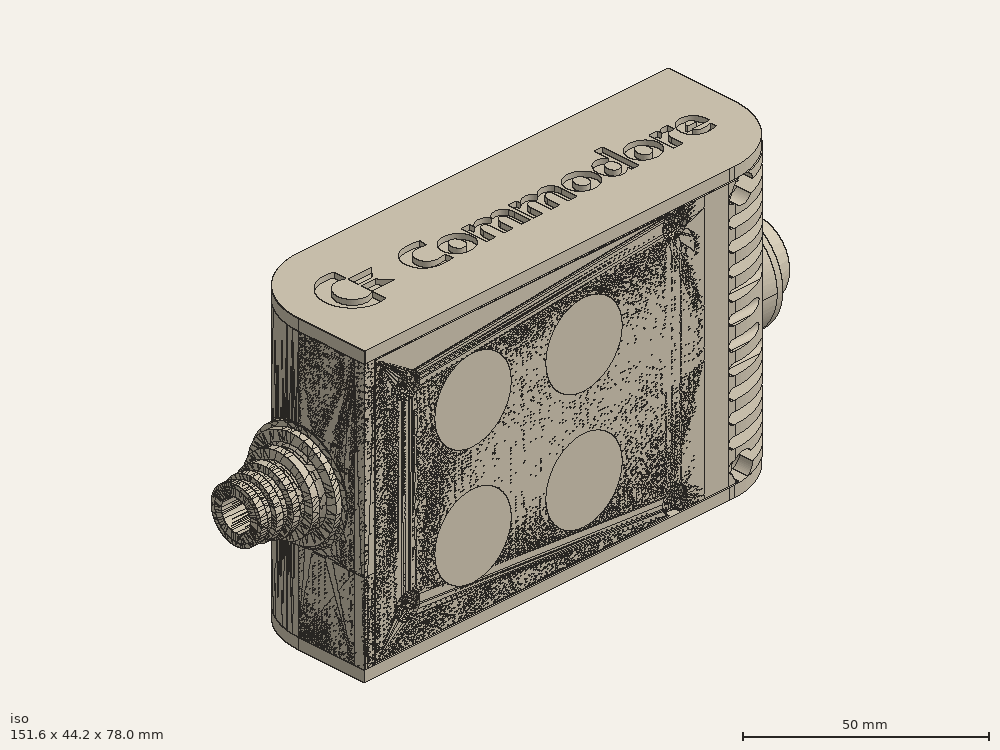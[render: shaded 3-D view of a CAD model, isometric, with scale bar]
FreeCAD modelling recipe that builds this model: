
FCSTD DOCUMENT  (FreeCAD 0.19R0.19.2)
Label: enclosure_223FCStd
License: All rights reserved
LicenseURL: http://en.wikipedia.org/wiki/All_rights_reserved
objects: Part::Revolution×152, Part::MultiFuse×148, Part::Feature×146, Sketcher::SketchObject×93, Part::Extrusion×78, Part::Cut×74, Part::Cylinder×70, Part::Fillet×58, Part::Box×38, App::MeasureDistance×4, Part::Chamfer×4, Part::FeaturePython×2, Image::ImagePlane×1, PartDesign::Body×1, Part::Mirroring×1
note: 865 computed .brp shape members not serialized (recipe doc carries the construction recipe); baked Part::Feature solids carry a one-line shape summary decoded from their .brp

FEATURE [Sketcher::SketchObject] Sketch  label="topSketch"
  FullyConstrained = true
  sketch-geometry (20):
    g0: LineSegment StartX=5.21097e-06 StartY=3 StartZ=0 EndX=5.21097e-06 EndY=19 EndZ=0
    g1: ArcOfCircle CenterX=19 CenterY=19 CenterZ=0 NormalX=0 NormalY=0 NormalZ=1 AngleXU=0 Radius=19 StartAngle=1.5708 EndAngle=3.14159
    g2: ArcOfCircle CenterX=19 CenterY=19 CenterZ=0 NormalX=0 NormalY=0 NormalZ=1 AngleXU=0 Radius=16 StartAngle=1.5708 EndAngle=3.14159
    g3: LineSegment StartX=114 StartY=35 StartZ=0 EndX=19 EndY=35 EndZ=0
    g4: LineSegment StartX=5.21097e-06 StartY=3 StartZ=0 EndX=5.21097e-06 EndY=0 EndZ=0
    g5: LineSegment StartX=3 StartY=0 StartZ=0 EndX=5.21097e-06 EndY=0 EndZ=0
    g6: LineSegment StartX=3 StartY=19 StartZ=0 EndX=3 EndY=0 EndZ=0
    g7: LineSegment StartX=19 StartY=38 StartZ=0 EndX=124 EndY=38 EndZ=0
    g8: Circle CenterX=119 CenterY=35 CenterZ=0 NormalX=0 NormalY=0 NormalZ=1 AngleXU=0 Radius=1
    g9: Circle CenterX=121 CenterY=35 CenterZ=0 NormalX=0 NormalY=0 NormalZ=1 AngleXU=0 Radius=1
    g10: Circle CenterX=121 CenterY=33 CenterZ=0 NormalX=0 NormalY=0 NormalZ=1 AngleXU=0 Radius=1
    g11: BSplineCurve PolesCount=3 KnotsCount=2 Degree=2 IsPeriodic=0
    g12: GeomPoint X=119 Y=35 Z=0
    g13: GeomPoint X=121 Y=33 Z=0
    g14: LineSegment StartX=119 StartY=35 StartZ=0 EndX=114 EndY=35 EndZ=0
    g15: ArcOfCircle CenterX=105 CenterY=19 CenterZ=0 NormalX=0 NormalY=0 NormalZ=1 AngleXU=0 Radius=19 StartAngle=5.7297 EndAngle=6.28319
    g16: ArcOfCircle CenterX=105 CenterY=19 CenterZ=0 NormalX=0 NormalY=0 NormalZ=1 AngleXU=0 Radius=16 StartAngle=5.60905 EndAngle=6.28319
    g17: LineSegment StartX=121 StartY=33 StartZ=0 EndX=121 EndY=19 EndZ=0
    g18: LineSegment StartX=124 StartY=38 StartZ=0 EndX=124 EndY=19 EndZ=0
    g19: LineSegment StartX=117.5 StartY=9.01251 StartZ=0 EndX=121.163 EndY=9.0125 EndZ=0
  constraints (46):
    c: Vertical(g0)
    c: Block(g0)
    c: Coincident(g1,g0)
    c: Block(g1)
    c: Coincident(g2,g1)
    c: Block(g2)
    c: Coincident(g3,g2)
    c: Horizontal(g3)
    c: Tangent(g3,g2)
    c: Coincident(g4,g0)
    c: Distance(g4) = 3
    c: Vertical(g4)
    c: Coincident(g5,g4)
    c: Horizontal(g5)
    c: Coincident(g6,g2)
    c: Coincident(g6,g5)
    c: Vertical(g6)
    c: Horizontal(g7)
    c: Distance(g7) = 105
    c: Coincident(g7,g1)
    c: Block(g3)
    c: Weight(g8) = 1
    c: Equal(g8,g9)
    c: Equal(g8,g10)
    c: InternalAlignment(g8,g11)
    c: InternalAlignment(g9,g11)
    c: InternalAlignment(g10,g11)
    c: InternalAlignment(g12,g11)
    c: InternalAlignment(g13,g11)
    c: Block(g11)
    c: Coincident(g14,g11)
    c: Coincident(g14,g3)
    c: Horizontal(g14)
    c: Block(g15)
    c: Coincident(g16,g15)
    c: Block(g16)
    c: Coincident(g17,g11)
    c: Coincident(g17,g16)
    c: Vertical(g17)
    c: Distance(g17) = 14
    c: Coincident(g18,g7)
    c: Coincident(g18,g15)
    c: Vertical(g18)
    c: Distance(g18) = 19
    c: Coincident(g19,g16)
    c: Coincident(g19,g15)
FEATURE [Sketcher::SketchObject] Sketch001  label="bottomSketch"
  FullyConstrained = true
  sketch-geometry (32):
    g0: LineSegment StartX=3.3 StartY=-6.03275e-07 StartZ=0 EndX=98 EndY=-6.03275e-07 EndZ=0
    g1: ArcOfCircle CenterX=98 CenterY=19 CenterZ=0 NormalX=0 NormalY=0 NormalZ=1 AngleXU=0 Radius=19 StartAngle=4.71239 EndAngle=5.71103
    g2: LineSegment StartX=6.3 StartY=8 StartZ=0 EndX=3.3 EndY=8 EndZ=0
    g3: LineSegment StartX=3.3 StartY=8 StartZ=0 EndX=3.3 EndY=-6.03275e-07 EndZ=0
    g4: ArcOfCircle CenterX=8.3 CenterY=5 CenterZ=0 NormalX=0 NormalY=0 NormalZ=1 AngleXU=0 Radius=2 StartAngle=3.14159 EndAngle=4.71239
    g5: LineSegment StartX=6.3 StartY=8 StartZ=0 EndX=6.3 EndY=5 EndZ=0
    g6: ArcOfCircle CenterX=98 CenterY=19 CenterZ=0 NormalX=0 NormalY=0 NormalZ=1 AngleXU=0 Radius=12.7 StartAngle=4.71239 EndAngle=6.28319
    g7: LineSegment StartX=94.7 StartY=3 StartZ=0 EndX=8.3 EndY=3 EndZ=0
    g8-g12: Circle x5 (B-spline internal-alignment scaffolding for g13; pole/knot coordinates omitted)
    g13: BSplineCurve PolesCount=5 KnotsCount=3 Degree=3 IsPeriodic=0
    g14: GeomPoint X=98 Y=6.3 Z=0
    g15: GeomPoint X=96.3938 Y=4.71946 Z=0
    g16: GeomPoint X=94.7 Y=3 Z=0
    g17-g23: Circle x7 (B-spline internal-alignment scaffolding for g24; pole/knot coordinates omitted)
    g24: BSplineCurve PolesCount=7 KnotsCount=5 Degree=3 IsPeriodic=0
    g25-g29: GeomPoint x5 (B-spline internal-alignment scaffolding for g24; pole/knot coordinates omitted)
    g30: ArcOfCircle CenterX=98 CenterY=19 CenterZ=0 NormalX=0 NormalY=0 NormalZ=1 AngleXU=0 Radius=15.7 StartAngle=5.81226 EndAngle=6.28319
    g31: LineSegment StartX=110.7 StartY=19 StartZ=0 EndX=113.7 EndY=19 EndZ=0
  constraints (41):
    c: Horizontal(g0)
    c: Coincident(g1,g0)
    c: Block(g1)
    c: Horizontal(g2)
    c: Distance(g2) = 3
    c: Coincident(g3,g2)
    c: Vertical(g3)
    c: Coincident(g3,g0)
    c: Block(g4)
    c: Block(g2)
    c: Coincident(g5,g2)
    c: Coincident(g5,g4)
    c: Vertical(g5)
    c: Coincident(g6,g1)
    c: Block(g6)
    c: Coincident(g7,g4)
    c: Horizontal(g7)
    c: Block(g0)
    c: Block(g7)
    c: Block(g3)
    c: Coincident(g13,g6)
    c: Weight(g8) = 1
    c: Equal(g8, g9-g12) x4
    c: Coincident(g13,g7)
    c: InternalAlignment(g8-g12 -> g13) x5
    c: InternalAlignment(g14,g13)
    c: InternalAlignment(g15,g13)
    c: InternalAlignment(g16,g13)
    c: Block(g13)
    c: Weight(g17) = 1
    c: Equal(g17, g18-g23) x6
    c: Coincident(g24,g1)
    c: InternalAlignment(g17-g23 -> g24) x7
    c: InternalAlignment(g25-g29 -> g24) x5
    c: Block(g24)
    c: Coincident(g30,g24)
    c: Coincident(g31,g6)
    c: Coincident(g31,g30)
    c: Horizontal(g31)
    c: Block(g31)
    c: Block(g30)
FEATURE [Part::Extrusion] Extrude  label="top"
  Base = -> Sketch
  Dir = (0,0,1)
  DirMode = 2
  FaceMakerClass = Part::FaceMakerBullseye
  LengthFwd = 72
  LengthRev = 0
  Solid = true
  Symmetric = false
FEATURE [Part::Extrusion] Extrude001  label="bottom"
  Base = -> Sketch001
  Dir = (0,0,1)
  DirMode = 2
  FaceMakerClass = Part::FaceMakerBullseye
  LengthFwd = 71.4
  LengthRev = 0
  Placement = pos=(0,0,0.3) rot=(0,0,1;0rad)
  Solid = true
  Symmetric = false
FEATURE [Sketcher::SketchObject] Sketch002  label="topSketch001"
  FullyConstrained = true
  sketch-geometry (8):
    g0: ArcOfCircle CenterX=19 CenterY=19.0975 CenterZ=0 NormalX=0 NormalY=0 NormalZ=1 AngleXU=0 Radius=18.9025 StartAngle=1.5708 EndAngle=3.14674
    g1: LineSegment StartX=0.0977805 StartY=19.0003 StartZ=0 EndX=0.0977805 EndY=0.000251602 EndZ=0
    g2: LineSegment StartX=19 StartY=38 StartZ=0 EndX=124 EndY=38 EndZ=0
    g3: LineSegment StartX=0.0977805 StartY=0.000251602 StartZ=0 EndX=105.098 EndY=0.000251602 EndZ=0
    g4: LineSegment StartX=124 StartY=38 StartZ=0 EndX=125.616 EndY=38 EndZ=0
    g5: LineSegment StartX=105.098 StartY=0.000251602 StartZ=0 EndX=106.713 EndY=0.000251602 EndZ=0
    g6: ArcOfCircle CenterX=106.616 CenterY=19 CenterZ=0 NormalX=0 NormalY=0 NormalZ=1 AngleXU=0 Radius=19 StartAngle=4.71754 EndAngle=6.28319
    g7: LineSegment StartX=125.616 StartY=38 StartZ=0 EndX=125.616 EndY=19 EndZ=0
  constraints (21):
    c: Block(g0)
    c: Coincident(g1,g0)
    c: Vertical(g1)
    c: Horizontal(g2)
    c: Distance(g2) = 105
    c: Coincident(g2,g0)
    c: Distance(g1) = 19
    c: Coincident(g3,g1)
    c: Horizontal(g3)
    c: Distance(g3) = 105
    c: Coincident(g4,g2)
    c: Horizontal(g4)
    c: Distance(g4) = 1.61553
    c: Horizontal(g5)
    c: Equal(g4,g5) = 1.61553
    c: Coincident(g5,g3)
    c: Block(g6)
    c: Coincident(g6,g5)
    c: Coincident(g7,g4)
    c: Coincident(g7,g6)
    c: Vertical(g7)
FEATURE [Part::Extrusion] Extrude002  label="sideA"
  Base = -> Sketch002
  Dir = (0,0,1)
  DirMode = 2
  FaceMakerClass = Part::FaceMakerBullseye
  LengthFwd = 3
  LengthRev = 0
  Placement = pos=(0,0,-3) rot=(0,0,1;0rad)
  Solid = true
  Symmetric = false
FEATURE [Sketcher::SketchObject] Sketch003  label="topSketch002"
  FullyConstrained = true
  sketch-geometry (6):
    g0: LineSegment StartX=19 StartY=38 StartZ=0 EndX=117 EndY=38 EndZ=0
    g1: ArcOfCircle CenterX=19 CenterY=19 CenterZ=0 NormalX=0 NormalY=0 NormalZ=1 AngleXU=0 Radius=19 StartAngle=1.5708 EndAngle=3.14159
    g2: LineSegment StartX=117 StartY=38 StartZ=0 EndX=117 EndY=19 EndZ=0
    g3: LineSegment StartX=98 StartY=1.0161e-12 StartZ=0 EndX=5.22862e-06 EndY=1.0161e-12 EndZ=0
    g4: LineSegment StartX=5.22862e-06 StartY=19 StartZ=0 EndX=5.22862e-06 EndY=1.0161e-12 EndZ=0
    g5: ArcOfCircle CenterX=98 CenterY=19 CenterZ=0 NormalX=0 NormalY=0 NormalZ=1 AngleXU=0 Radius=19 StartAngle=4.71239 EndAngle=6.28319
  constraints (16):
    c: Horizontal(g0)
    c: Distance(g0) = 98
    c: Coincident(g1,g0)
    c: Block(g1)
    c: Coincident(g2,g0)
    c: Vertical(g2)
    c: Distance(g2) = 19
    c: Horizontal(g3)
    c: Coincident(g4,g1)
    c: Vertical(g4)
    c: Coincident(g3,g4)
    c: Block(g3)
    c: Coincident(g5,g2)
    c: Coincident(g5,g3)
    c: Block(g0)
    c: Block(g5)
FEATURE [Sketcher::SketchObject] Sketch004
  FullyConstrained = true
  MapMode = 3
  Placement = pos=(0,0,0) rot=(1,0,0;1.5708rad)
  Support = -> [Extrude]
  sketch-geometry (8):
    g0: Circle CenterX=80.351 CenterY=-67.6202 CenterZ=0 NormalX=0 NormalY=0 NormalZ=1 AngleXU=0 Radius=2
    g1: Circle CenterX=80.351 CenterY=-67.6202 CenterZ=0 NormalX=0 NormalY=0 NormalZ=1 AngleXU=0 Radius=3
    g2: Circle CenterX=80.351 CenterY=-4.92017 CenterZ=0 NormalX=0 NormalY=0 NormalZ=1 AngleXU=0 Radius=2
    g3: Circle CenterX=80.351 CenterY=-4.92017 CenterZ=0 NormalX=0 NormalY=0 NormalZ=1 AngleXU=0 Radius=3
    g4: Circle CenterX=23.851 CenterY=-4.92017 CenterZ=0 NormalX=0 NormalY=0 NormalZ=1 AngleXU=0 Radius=2
    g5: Circle CenterX=23.851 CenterY=-4.92017 CenterZ=0 NormalX=0 NormalY=0 NormalZ=1 AngleXU=0 Radius=3
    g6: Circle CenterX=23.851 CenterY=-67.6202 CenterZ=0 NormalX=0 NormalY=0 NormalZ=1 AngleXU=0 Radius=2
    g7: Circle CenterX=23.851 CenterY=-67.6202 CenterZ=0 NormalX=0 NormalY=0 NormalZ=1 AngleXU=0 Radius=3
  constraints (8):
    c: Block(g3)
    c: Block(g2)
    c: Block(g1)
    c: Block(g0)
    c: Block(g6)
    c: Block(g7)
    c: Block(g4)
    c: Block(g5)
FEATURE [Part::Extrusion] Extrude004
  Base = -> Sketch004
  Dir = (0,-1,2e-16)
  DirMode = 2
  FaceMakerClass = Part::FaceMakerBullseye
  LengthFwd = 6
  LengthRev = 0
  Placement = pos=(0,9,0) rot=(0,0,1;0rad)
  Solid = true
  Symmetric = false
FEATURE [Sketcher::SketchObject] Sketch005
  FullyConstrained = true
  MapMode = 3
  Placement = pos=(0,0,0) rot=(1,0,0;1.5708rad)
  Support = -> [Extrude]
  sketch-geometry (8):
    g0: Circle CenterX=80.351 CenterY=-67.6202 CenterZ=0 NormalX=0 NormalY=0 NormalZ=1 AngleXU=0 Radius=3
    g1: Circle CenterX=80.351 CenterY=-4.92017 CenterZ=0 NormalX=0 NormalY=0 NormalZ=1 AngleXU=0 Radius=3
    g2: Circle CenterX=23.851 CenterY=-4.92017 CenterZ=0 NormalX=0 NormalY=0 NormalZ=1 AngleXU=0 Radius=3
    g3: Circle CenterX=23.851 CenterY=-67.6202 CenterZ=0 NormalX=0 NormalY=0 NormalZ=1 AngleXU=0 Radius=3
    g4: Circle CenterX=23.851 CenterY=-67.6202 CenterZ=0 NormalX=0 NormalY=0 NormalZ=1 AngleXU=0 Radius=5
    g5: Circle CenterX=80.351 CenterY=-67.6202 CenterZ=0 NormalX=0 NormalY=0 NormalZ=1 AngleXU=0 Radius=5
    g6: Circle CenterX=23.851 CenterY=-4.92017 CenterZ=0 NormalX=0 NormalY=0 NormalZ=1 AngleXU=0 Radius=5
    g7: Circle CenterX=80.351 CenterY=-4.92017 CenterZ=0 NormalX=0 NormalY=0 NormalZ=1 AngleXU=0 Radius=5
  constraints (8):
    c: Block(g1)
    c: Block(g0)
    c: Block(g3)
    c: Block(g2)
    c: Block(g5)
    c: Block(g4)
    c: Block(g6)
    c: Block(g7)
FEATURE [Part::Extrusion] Extrude005
  Base = -> Sketch005
  Dir = (0,-1,2e-16)
  DirMode = 2
  FaceMakerClass = Part::FaceMakerBullseye
  LengthFwd = 2
  LengthRev = 0
  Solid = true
  Symmetric = false
FEATURE [Sketcher::SketchObject] Sketch006
  FullyConstrained = true
  MapMode = 3
  Placement = pos=(0,0,0) rot=(1,0,0;1.5708rad)
  sketch-geometry (8):
    g0: Circle CenterX=80.351 CenterY=-67.6202 CenterZ=0 NormalX=0 NormalY=0 NormalZ=1 AngleXU=0 Radius=3
    g1: Circle CenterX=80.351 CenterY=-4.92017 CenterZ=0 NormalX=0 NormalY=0 NormalZ=1 AngleXU=0 Radius=3
    g2: Circle CenterX=23.851 CenterY=-4.92017 CenterZ=0 NormalX=0 NormalY=0 NormalZ=1 AngleXU=0 Radius=3
    g3: Circle CenterX=23.851 CenterY=-67.6202 CenterZ=0 NormalX=0 NormalY=0 NormalZ=1 AngleXU=0 Radius=3
    g4: Circle CenterX=23.851 CenterY=-67.6202 CenterZ=0 NormalX=0 NormalY=0 NormalZ=1 AngleXU=0 Radius=5
    g5: Circle CenterX=80.351 CenterY=-67.6202 CenterZ=0 NormalX=0 NormalY=0 NormalZ=1 AngleXU=0 Radius=5
    g6: Circle CenterX=23.851 CenterY=-4.92017 CenterZ=0 NormalX=0 NormalY=0 NormalZ=1 AngleXU=0 Radius=5
    g7: Circle CenterX=80.351 CenterY=-4.92017 CenterZ=0 NormalX=0 NormalY=0 NormalZ=1 AngleXU=0 Radius=5
  constraints (8):
    c: Block(g1)
    c: Block(g0)
    c: Block(g3)
    c: Block(g2)
    c: Block(g5)
    c: Block(g4)
    c: Block(g6)
    c: Block(g7)
FEATURE [Part::Extrusion] Extrude007
  Base = -> Sketch006
  Dir = (0,-1,2e-16)
  DirMode = 2
  FaceMakerClass = Part::FaceMakerBullseye
  LengthFwd = 2
  LengthRev = 0
  Solid = true
  Symmetric = false
FEATURE [Part::Fillet] Fillet
  Base = -> Extrude007
  Edges = 4 edges r=1.99: [Edge6,Edge12,Edge18,Edge24]
FEATURE [Part::Cut] Cut
  Base = -> Extrude005
  Placement = pos=(0,5,0) rot=(0,0,1;0rad)
  Tool = -> Fillet
FEATURE [Part::MultiFuse] Fusion  label="pCBScrews"
  Placement = pos=(-2.5,0,72.3) rot=(0,0,1;0rad)
  Shapes = -> [Extrude004,Cut]
FEATURE [App::MeasureDistance] Distance  label="Distance: 0.69 mm"
  Distance = 0.685967
  P1 = (24.0138,2.9647,0.3)
  P2 = (23.8901,3,-0.373787)
FEATURE [App::MeasureDistance] Distance001  label="Distance: 0.53 mm"
  Distance = 0.533607
  P1 = (80.2939,3,72.2334)
  P2 = (80.281,2.99661,71.7)
FEATURE [Part::Fillet] Fillet001
  Base = -> Extrude001
  Edges = 1 edges r=2.4: [Edge17]
FEATURE [Part::Fillet] Fillet002  label="bottom001"
  Base = -> Fillet001
  Edges = 1 edges r=2.4: [Edge36]
FEATURE [Part::Fillet] Fillet003  label="top001"
  Base = -> Extrude
  Edges = 1 edges r=2: [Edge1]
FEATURE [Sketcher::SketchObject] Sketch007
  FullyConstrained = true
  sketch-geometry (16):
    g0: LineSegment StartX=4 StartY=0 StartZ=0 EndX=4 EndY=2.4 EndZ=0
    g1: LineSegment StartX=4 StartY=2.4 StartZ=0 EndX=7 EndY=2.4 EndZ=0
    g2: LineSegment StartX=4 StartY=0 StartZ=0 EndX=5.7 EndY=0 EndZ=0
    g3: LineSegment StartX=5.7 StartY=0 StartZ=0 EndX=5.7 EndY=-5.6 EndZ=0
    g4-g8: Circle x5 (B-spline internal-alignment scaffolding for g9; pole/knot coordinates omitted)
    g9: BSplineCurve PolesCount=5 KnotsCount=3 Degree=3 IsPeriodic=0
    g10: GeomPoint X=7 Y=2.4 Z=0
    g11: GeomPoint X=10.4582 Y=-1.55472 Z=0
    g12: GeomPoint X=14 Y=-5.6 Z=0
    g13: LineSegment StartX=14 StartY=-5.6 StartZ=0 EndX=14 EndY=-14.1 EndZ=0
    g14: LineSegment StartX=14 StartY=-14.1 StartZ=0 EndX=6.5 EndY=-14.1 EndZ=0
    g15: LineSegment StartX=5.7 StartY=-5.6 StartZ=0 EndX=6.5 EndY=-14.1 EndZ=0
  constraints (28):
    c: Distance(g0) = 2.4
    c: Vertical(g0)
    c: Block(g0)
    c: Coincident(g1,g0)
    c: Horizontal(g1)
    c: Distance(g1) = 3
    c: Coincident(g2,g0)
    c: Horizontal(g2)
    c: Distance(g2) = 1.7
    c: Coincident(g3,g2)
    c: Vertical(g3)
    c: Distance(g3) = 5.6
    c: Coincident(g9,g1)
    c: Weight(g4) = 1
    c: Equal(g4, g5-g8) x4
    c: InternalAlignment(g4-g8 -> g9) x5
    c: InternalAlignment(g10,g9)
    c: InternalAlignment(g11,g9)
    c: InternalAlignment(g12,g9)
    c: Block(g9)
    c: Coincident(g13,g9)
    c: Vertical(g13)
    c: Distance(g13) = 8.5
    c: Coincident(g14,g13)
    c: Horizontal(g14)
    c: Distance(g14) = 7.5
    c: Coincident(g15,g3)
    c: Coincident(g15,g14)
FEATURE [Part::Feature] Face
  shape: bbox 10 x 16.5 x 2e-07 mm, 1 faces, 0 solids (baked)
FEATURE [Part::Revolution] Revolve  label="plugHousing"
  Angle = 360
  Axis = (0,1,0)
  Base = (0,0,0)
  FaceMakerClass = Part::FaceMakerBullseye
  Placement = pos=(0,0,36.15) rot=(0,0,1;0rad)
  Solid = false
  Source = -> Face
  Symmetric = false
FEATURE [Part::Feature] Face001
  shape: bbox 10 x 16.5 x 2e-07 mm, 1 faces, 0 solids (baked)
FEATURE [Part::Revolution] Revolve001  label="plugHousing001"
  Angle = 360
  Axis = (0,1,0)
  Base = (0,0,0)
  FaceMakerClass = Part::FaceMakerBullseye
  Placement = pos=(0,0,36.15) rot=(0,0,1;0rad)
  Solid = false
  Source = -> Face001
  Symmetric = false
FEATURE [Part::MultiFuse] Fusion001  label="plugHousing002"
  Placement = pos=(0,0,0) rot=(0,0,1;1.5708rad)
  Shapes = -> [Revolve001,Revolve]
FEATURE [Part::Feature] Face002
  shape: bbox 10 x 16.5 x 2e-07 mm, 1 faces, 0 solids (baked)
FEATURE [Part::Revolution] Revolve003  label="plugHousing005"
  Angle = 360
  Axis = (0,1,0)
  Base = (0,0,0)
  FaceMakerClass = Part::FaceMakerBullseye
  Placement = pos=(0,0,36.15) rot=(0,0,1;0rad)
  Solid = false
  Source = -> Face002
  Symmetric = false
FEATURE [Part::Feature] Face003
  shape: bbox 10 x 16.5 x 2e-07 mm, 1 faces, 0 solids (baked)
FEATURE [Part::Revolution] Revolve002  label="plugHousing003"
  Angle = 360
  Axis = (0,1,0)
  Base = (0,0,0)
  FaceMakerClass = Part::FaceMakerBullseye
  Placement = pos=(0,0,36.15) rot=(0,0,1;0rad)
  Solid = false
  Source = -> Face003
  Symmetric = false
FEATURE [Part::MultiFuse] Fusion002  label="plugHousing004"
  Placement = pos=(0,0,0) rot=(0,0,1;1.5708rad)
  Shapes = -> [Revolve002,Revolve003]
FEATURE [Part::MultiFuse] Fusion003  label="plugHousing006"
  Placement = pos=(0,19,0) rot=(0,0,1;3.14159rad)
  Shapes = -> [Fusion002,Fusion001]
FEATURE [Part::Feature] Face004
  shape: bbox 10 x 16.5 x 2e-07 mm, 1 faces, 0 solids (baked)
FEATURE [Part::Revolution] Revolve006  label="plugHousing010"
  Angle = 360
  Axis = (0,1,0)
  Base = (0,0,0)
  FaceMakerClass = Part::FaceMakerBullseye
  Placement = pos=(0,0,36.15) rot=(0,0,1;0rad)
  Solid = false
  Source = -> Face004
  Symmetric = false
FEATURE [Part::Feature] Face005
  shape: bbox 10 x 16.5 x 2e-07 mm, 1 faces, 0 solids (baked)
FEATURE [Part::Revolution] Revolve007  label="plugHousing011"
  Angle = 360
  Axis = (0,1,0)
  Base = (0,0,0)
  FaceMakerClass = Part::FaceMakerBullseye
  Placement = pos=(0,0,36.15) rot=(0,0,1;0rad)
  Solid = false
  Source = -> Face005
  Symmetric = false
FEATURE [Part::Feature] Face006
  shape: bbox 10 x 16.5 x 2e-07 mm, 1 faces, 0 solids (baked)
FEATURE [Part::Revolution] Revolve004  label="plugHousing007"
  Angle = 360
  Axis = (0,1,0)
  Base = (0,0,0)
  FaceMakerClass = Part::FaceMakerBullseye
  Placement = pos=(0,0,36.15) rot=(0,0,1;0rad)
  Solid = false
  Source = -> Face006
  Symmetric = false
FEATURE [Part::MultiFuse] Fusion004  label="plugHousing009"
  Placement = pos=(0,0,0) rot=(0,0,1;1.5708rad)
  Shapes = -> [Revolve004,Revolve007]
FEATURE [Part::Feature] Face007
  shape: bbox 10 x 16.5 x 2e-07 mm, 1 faces, 0 solids (baked)
FEATURE [Part::Revolution] Revolve005  label="plugHousing008"
  Angle = 360
  Axis = (0,1,0)
  Base = (0,0,0)
  FaceMakerClass = Part::FaceMakerBullseye
  Placement = pos=(0,0,36.15) rot=(0,0,1;0rad)
  Solid = false
  Source = -> Face007
  Symmetric = false
FEATURE [Part::MultiFuse] Fusion005  label="plugHousing012"
  Placement = pos=(0,0,0) rot=(0,0,1;1.5708rad)
  Shapes = -> [Revolve006,Revolve005]
FEATURE [Part::MultiFuse] Fusion006  label="plugHousing013"
  Placement = pos=(0,19,0) rot=(0,0,1;3.14159rad)
  Shapes = -> [Fusion005,Fusion004]
FEATURE [Part::MultiFuse] Fusion007  label="plugHousing014"
  Placement = pos=(122.621,0,-0.15) rot=(0,0,1;0rad)
  Shapes = -> [Fusion003,Fusion006]
FEATURE [Part::Cylinder] Cylinder002
  Angle = 360
  AttacherType = Attacher::AttachEngine3D
  Height = 20
  Placement = pos=(0,0,36.15) rot=(0,0,1;0rad)
  Radius = 4
FEATURE [Part::Cylinder] Cylinder003
  Angle = 360
  AttacherType = Attacher::AttachEngine3D
  Height = 10
  Placement = pos=(0,0,36.15) rot=(0,0,1;0rad)
  Radius = 4
FEATURE [Part::MultiFuse] Fusion009  label="removeToCreateHoleForPlugHousing"
  Placement = pos=(70,19,36.15) rot=(0,1,0;1.5708rad)
  Shapes = -> [Cylinder002,Cylinder003]
FEATURE [Part::Cylinder] Cylinder004
  Angle = 360
  AttacherType = Attacher::AttachEngine3D
  Height = 20
  Placement = pos=(0,0,36.15) rot=(0,0,1;0rad)
  Radius = 4
FEATURE [Part::Cylinder] Cylinder005
  Angle = 360
  AttacherType = Attacher::AttachEngine3D
  Height = 10
  Placement = pos=(0,0,36.15) rot=(0,0,1;0rad)
  Radius = 4
FEATURE [Part::MultiFuse] Fusion010  label="removeToCreateHoleForPlugHousing001"
  Placement = pos=(70,19,36.15) rot=(0,1,0;1.5708rad)
  Shapes = -> [Cylinder004,Cylinder005]
FEATURE [Part::Cut] Cut001
  Base = -> Fillet003
  Tool = -> Fusion010
FEATURE [Part::Cut] Cut002  label="Bottom"
  Base = -> Fillet002
  Tool = -> Fusion009
FEATURE [Part::Feature] Face008
  shape: bbox 10 x 16.5 x 2e-07 mm, 1 faces, 0 solids (baked)
FEATURE [Part::Revolution] Revolve011  label="plugHousing021"
  Angle = 360
  Axis = (0,1,0)
  Base = (0,0,0)
  FaceMakerClass = Part::FaceMakerBullseye
  Placement = pos=(0,0,36.15) rot=(0,0,1;0rad)
  Solid = false
  Source = -> Face008
  Symmetric = false
FEATURE [Part::Feature] Face009
  shape: bbox 10 x 16.5 x 2e-07 mm, 1 faces, 0 solids (baked)
FEATURE [Part::Revolution] Revolve012  label="plugHousing022"
  Angle = 360
  Axis = (0,1,0)
  Base = (0,0,0)
  FaceMakerClass = Part::FaceMakerBullseye
  Placement = pos=(0,0,36.15) rot=(0,0,1;0rad)
  Solid = false
  Source = -> Face009
  Symmetric = false
FEATURE [Part::Feature] Face010 .. Face013  x4 (patterned run collapsed; names and placements below)
  shape: bbox 10 x 16.5 x 2e-07 mm, 1 faces, 0 solids (baked)
FEATURE [Part::Revolution] Revolve015  label="plugHousing027"
  Angle = 360
  Axis = (0,1,0)
  Base = (0,0,0)
  FaceMakerClass = Part::FaceMakerBullseye
  Placement = pos=(0,0,36.15) rot=(0,0,1;0rad)
  Solid = false
  Source = -> Face013
  Symmetric = false
FEATURE [Part::Feature] Face014
  shape: bbox 10 x 16.5 x 2e-07 mm, 1 faces, 0 solids (baked)
FEATURE [Part::Feature] Face015
  shape: bbox 10 x 16.5 x 2e-07 mm, 1 faces, 0 solids (baked)
FEATURE [Part::Feature] Face016
  shape: bbox 10 x 16.5 x 2e-07 mm, 1 faces, 0 solids (baked)
FEATURE [Part::Revolution] Revolve019  label="plugHousing033"
  Angle = 360
  Axis = (0,1,0)
  Base = (0,0,0)
  FaceMakerClass = Part::FaceMakerBullseye
  Placement = pos=(0,0,36.15) rot=(0,0,1;0rad)
  Solid = false
  Source = -> Face016
  Symmetric = false
FEATURE [Part::Feature] Face017
  shape: bbox 10 x 16.5 x 2e-07 mm, 1 faces, 0 solids (baked)
FEATURE [Part::Revolution] Revolve020  label="plugHousing034"
  Angle = 360
  Axis = (0,1,0)
  Base = (0,0,0)
  FaceMakerClass = Part::FaceMakerBullseye
  Placement = pos=(0,0,36.15) rot=(0,0,1;0rad)
  Solid = false
  Source = -> Face017
  Symmetric = false
FEATURE [Part::Feature] Face018
  shape: bbox 10 x 16.5 x 2e-07 mm, 1 faces, 0 solids (baked)
FEATURE [Part::Revolution] Revolve016  label="plugHousing030"
  Angle = 360
  Axis = (0,1,0)
  Base = (0,0,0)
  FaceMakerClass = Part::FaceMakerBullseye
  Placement = pos=(0,0,36.15) rot=(0,0,1;0rad)
  Solid = false
  Source = -> Face018
  Symmetric = false
FEATURE [Part::MultiFuse] Fusion020  label="plugHousing038"
  Placement = pos=(0,0,0) rot=(0,0,1;1.5708rad)
  Shapes = -> [Revolve016,Revolve020]
FEATURE [Part::Feature] Face019
  shape: bbox 10 x 16.5 x 2e-07 mm, 1 faces, 0 solids (baked)
FEATURE [Part::Feature] Face020
  shape: bbox 10 x 16.5 x 2e-07 mm, 1 faces, 0 solids (baked)
FEATURE [Part::Revolution] Revolve017  label="plugHousing031"
  Angle = 360
  Axis = (0,1,0)
  Base = (0,0,0)
  FaceMakerClass = Part::FaceMakerBullseye
  Placement = pos=(0,0,36.15) rot=(0,0,1;0rad)
  Solid = false
  Source = -> Face020
  Symmetric = false
FEATURE [Part::MultiFuse] Fusion021  label="plugHousing039"
  Placement = pos=(0,0,0) rot=(0,0,1;1.5708rad)
  Shapes = -> [Revolve019,Revolve017]
FEATURE [Part::MultiFuse] Fusion023  label="plugHousing041"
  Placement = pos=(0,19,0) rot=(0,0,1;3.14159rad)
  Shapes = -> [Fusion021,Fusion020]
FEATURE [Part::Revolution] Revolve022  label="plugHousing043"
  Angle = 360
  Axis = (0,1,0)
  Base = (0,0,0)
  FaceMakerClass = Part::FaceMakerBullseye
  Placement = pos=(0,0,36.15) rot=(0,0,1;0rad)
  Solid = false
  Source = -> Face019
  Symmetric = false
FEATURE [Part::Feature] Face021
  shape: bbox 10 x 16.5 x 2e-07 mm, 1 faces, 0 solids (baked)
FEATURE [Part::Revolution] Revolve023  label="plugHousing044"
  Angle = 360
  Axis = (0,1,0)
  Base = (0,0,0)
  FaceMakerClass = Part::FaceMakerBullseye
  Placement = pos=(0,0,36.15) rot=(0,0,1;0rad)
  Solid = false
  Source = -> Face021
  Symmetric = false
FEATURE [Part::Feature] Face022
  shape: bbox 10 x 16.5 x 2e-07 mm, 1 faces, 0 solids (baked)
FEATURE [Part::Revolution] Revolve018  label="plugHousing032"
  Angle = 360
  Axis = (0,1,0)
  Base = (0,0,0)
  FaceMakerClass = Part::FaceMakerBullseye
  Placement = pos=(0,0,36.15) rot=(0,0,1;0rad)
  Solid = false
  Source = -> Face022
  Symmetric = false
FEATURE [Part::MultiFuse] Fusion022  label="plugHousing040"
  Placement = pos=(0,0,0) rot=(0,0,1;1.5708rad)
  Shapes = -> [Revolve018,Revolve023]
FEATURE [Part::Feature] Face023
  shape: bbox 10 x 16.5 x 2e-07 mm, 1 faces, 0 solids (baked)
FEATURE [Part::Revolution] Revolve021  label="plugHousing035"
  Angle = 360
  Axis = (0,1,0)
  Base = (0,0,0)
  FaceMakerClass = Part::FaceMakerBullseye
  Placement = pos=(0,0,36.15) rot=(0,0,1;0rad)
  Solid = false
  Source = -> Face023
  Symmetric = false
FEATURE [Part::MultiFuse] Fusion018  label="plugHousing036"
  Placement = pos=(0,0,0) rot=(0,0,1;1.5708rad)
  Shapes = -> [Revolve022,Revolve021]
FEATURE [Part::MultiFuse] Fusion019  label="plugHousing037"
  Placement = pos=(0,19,0) rot=(0,0,1;3.14159rad)
  Shapes = -> [Fusion018,Fusion022]
FEATURE [Part::MultiFuse] Fusion024  label="plugHousing042"
  Placement = pos=(122.621,0,-0.15) rot=(0,0,1;0rad)
  Shapes = -> [Fusion023,Fusion019]
FEATURE [Part::Cylinder] Cylinder006
  Angle = 360
  AttacherType = Attacher::AttachEngine3D
  Height = 20
  Placement = pos=(0,0,36.15) rot=(0,0,1;0rad)
  Radius = 14.3
FEATURE [Part::Cylinder] Cylinder007
  Angle = 360
  AttacherType = Attacher::AttachEngine3D
  Height = 10
  Placement = pos=(0,0,36.15) rot=(0,0,1;0rad)
  Radius = 4
FEATURE [Part::MultiFuse] Fusion026  label="removeToCreteHoleForPlugHousing"
  Placement = pos=(70,19,36) rot=(0,1,0;1.5708rad)
  Shapes = -> [Cylinder006,Cylinder007]
FEATURE [Part::Box] Box001  label="Cube001"
  AttacherType = Attacher::AttachEngine3D
  Height = 28
  Length = 3
  Placement = pos=(110.7,19,22) rot=(0,0,1;0rad)
  Width = 15.7
FEATURE [Part::Cut] Cut003  label="top002"
  Base = -> Cut001
  Tool = -> Fusion007
FEATURE [Part::Revolution] Revolve008  label="plugHousing015"
  Angle = 360
  Axis = (0,1,0)
  Base = (0,0,0)
  FaceMakerClass = Part::FaceMakerBullseye
  Placement = pos=(0,0,36.15) rot=(0,0,1;0rad)
  Solid = false
  Source = -> Face010
  Symmetric = false
FEATURE [Part::MultiFuse] Fusion013  label="plugHousing020"
  Placement = pos=(0,0,0) rot=(0,0,1;1.5708rad)
  Shapes = -> [Revolve008,Revolve012]
FEATURE [Part::Cut] Cut004  label="top003"
  Base = -> Cut003
  Placement = pos=(1,0,0) rot=(0,0,1;0rad)
  Tool = -> Fusion026
FEATURE [Part::Cylinder] Cylinder008
  Angle = 360
  AttacherType = Attacher::AttachEngine3D
  Height = 20
  Placement = pos=(0,0,36.15) rot=(0,0,1;0rad)
  Radius = 10.3
FEATURE [Part::Cylinder] Cylinder009
  Angle = 360
  AttacherType = Attacher::AttachEngine3D
  Height = 10
  Placement = pos=(0,0,36.15) rot=(0,0,1;0rad)
  Radius = 4
FEATURE [Part::MultiFuse] Fusion027  label="removeToCreteHoleForPlugHousing001"
  Placement = pos=(70,19,36) rot=(0,1,0;1.5708rad)
  Shapes = -> [Cylinder008,Cylinder009]
FEATURE [Part::Cut] Cut005  label="plugHousingTab"
  Base = -> Box001
  Tool = -> Fusion027
FEATURE [Part::MultiFuse] Fusion028  label="plugHousing045"
  Shapes = -> [Fusion024,Cut005]
FEATURE [Part::Box] Box002  label="Cube002"
  AttacherType = Attacher::AttachEngine3D
  Height = 28.8
  Length = 3
  Placement = pos=(107.3,28,21.6) rot=(0,0,1;0rad)
  Width = 7
FEATURE [Part::Box] Box003  label="Cube003"
  AttacherType = Attacher::AttachEngine3D
  Height = 3
  Length = 6.4
  Placement = pos=(107.3,28,18.6) rot=(0,0,1;0rad)
  Width = 7
FEATURE [Part::Box] Box004  label="Cube004"
  AttacherType = Attacher::AttachEngine3D
  Height = 3
  Length = 6.4
  Placement = pos=(107.3,28,50.4) rot=(0,0,1;0rad)
  Width = 7
FEATURE [Part::MultiFuse] Fusion029  label="plugHousingBracketHolder"
  Shapes = -> [Box004,Box002,Box003]
FEATURE [Part::Cylinder] Cylinder010
  Angle = 360
  AttacherType = Attacher::AttachEngine3D
  Height = 20
  Placement = pos=(0,0,36.15) rot=(0,0,1;0rad)
  Radius = 14.3
FEATURE [Part::Cylinder] Cylinder011
  Angle = 360
  AttacherType = Attacher::AttachEngine3D
  Height = 10
  Placement = pos=(0,0,36.15) rot=(0,0,1;0rad)
  Radius = 4
FEATURE [Part::MultiFuse] Fusion030  label="removeToCreteHoleForPlugHousing002"
  Placement = pos=(70,19,36) rot=(0,1,0;1.5708rad)
  Shapes = -> [Cylinder010,Cylinder011]
FEATURE [Part::Cut] Cut006  label="plugHousingBracketHolder001"
  Base = -> Fusion029
  Tool = -> Fusion030
FEATURE [Part::Cylinder] Cylinder012
  Angle = 360
  AttacherType = Attacher::AttachEngine3D
  Height = 20
  Placement = pos=(0,0,36.15) rot=(0,0,1;0rad)
  Radius = 7
FEATURE [Part::Cylinder] Cylinder013
  Angle = 360
  AttacherType = Attacher::AttachEngine3D
  Height = 10
  Placement = pos=(0,0,36.15) rot=(0,0,1;0rad)
  Radius = 4
FEATURE [Part::MultiFuse] Fusion032  label="removeToCreteHoleForPlugHousing003"
  Placement = pos=(70,19,36) rot=(0,1,0;1.5708rad)
  Shapes = -> [Cylinder012,Cylinder013]
FEATURE [Part::Cut] Cut007  label="bottom002"
  Base = -> Cut002
  Tool = -> Fusion032
FEATURE [Sketcher::SketchObject] Sketch008
  FullyConstrained = true
  sketch-geometry (54):
    g0: LineSegment StartX=-4.2 StartY=0 StartZ=0 EndX=-6.2 EndY=0 EndZ=0
    g1: LineSegment StartX=-14 StartY=-18 StartZ=0 EndX=-14 EndY=-26.5 EndZ=0
    g2: LineSegment StartX=-4.2 StartY=0 StartZ=0 EndX=-4.2 EndY=-13.4877 EndZ=0
    g3: Circle CenterX=-4.2 CenterY=-13.4877 CenterZ=0 NormalX=0 NormalY=0 NormalZ=1 AngleXU=0 Radius=1
    g4: Circle CenterX=-4.2 CenterY=-26.5 CenterZ=0 NormalX=0 NormalY=0 NormalZ=1 AngleXU=0 Radius=1
    g5: Circle CenterX=-8.2 CenterY=-26.5 CenterZ=0 NormalX=0 NormalY=0 NormalZ=1 AngleXU=0 Radius=1
    g6: BSplineCurve PolesCount=3 KnotsCount=2 Degree=2 IsPeriodic=0
    g7: GeomPoint X=-4.2 Y=-13.4877 Z=0
    g8: GeomPoint X=-8.2 Y=-26.5 Z=0
    g9: LineSegment StartX=-14 StartY=-26.5 StartZ=0 EndX=-8.2 EndY=-26.5 EndZ=0
    g10: LineSegment StartX=-10.15 StartY=-12 StartZ=0 EndX=-10.15 EndY=-14 EndZ=0
    g11: LineSegment StartX=-12.8401 StartY=-16 StartZ=0 EndX=-10.1571 EndY=-16 EndZ=0
    g12: LineSegment StartX=-10.15 StartY=-14 StartZ=0 EndX=-8.70761 EndY=-14 EndZ=0
    g13: LineSegment StartX=-12.8401 StartY=-16 StartZ=0 EndX=-12.8401 EndY=-17.6958 EndZ=0
    g14: LineSegment StartX=-10.15 StartY=-12 StartZ=0 EndX=-7.79258 EndY=-12 EndZ=0
    g15: Circle CenterX=-6.2215 CenterY=-2 CenterZ=0 NormalX=0 NormalY=0 NormalZ=1 AngleXU=0 Radius=1
    g16: Circle CenterX=-6.22762 CenterY=-2.58724 CenterZ=0 NormalX=0 NormalY=0 NormalZ=1 AngleXU=0 Radius=1
    g17: Circle CenterX=-6.32538 CenterY=-4 CenterZ=0 NormalX=0 NormalY=0 NormalZ=1 AngleXU=0 Radius=1
    g18: BSplineCurve PolesCount=3 KnotsCount=2 Degree=2 IsPeriodic=0
    g19: GeomPoint X=-6.2215 Y=-2 Z=0
    g20: GeomPoint X=-6.32538 Y=-4 Z=0
    g21: Circle CenterX=-6.48644 CenterY=-5.99526 CenterZ=0 NormalX=0 NormalY=0 NormalZ=1 AngleXU=0 Radius=1
    g22: Circle CenterX=-6.58486 CenterY=-6.99526 CenterZ=0 NormalX=0 NormalY=0 NormalZ=1 AngleXU=0 Radius=1
    g23: Circle CenterX=-6.77343 CenterY=-8 CenterZ=0 NormalX=0 NormalY=0 NormalZ=1 AngleXU=0 Radius=1
    g24: BSplineCurve PolesCount=3 KnotsCount=2 Degree=2 IsPeriodic=0
    g25: GeomPoint X=-6.48644 Y=-5.99526 Z=0
    g26: GeomPoint X=-6.77343 Y=-8 Z=0
    g27: Circle CenterX=-7.19003 CenterY=-10 CenterZ=0 NormalX=0 NormalY=0 NormalZ=1 AngleXU=0 Radius=1
    g28: Circle CenterX=-7.44407 CenterY=-11.0915 CenterZ=0 NormalX=0 NormalY=0 NormalZ=1 AngleXU=0 Radius=1
    g29: Circle CenterX=-7.79258 CenterY=-12 CenterZ=0 NormalX=0 NormalY=0 NormalZ=1 AngleXU=0 Radius=1
    g30: BSplineCurve PolesCount=3 KnotsCount=2 Degree=2 IsPeriodic=0
    g31: GeomPoint X=-7.19003 Y=-10 Z=0
    g32: GeomPoint X=-7.79258 Y=-12 Z=0
    g33: Circle CenterX=-8.70761 CenterY=-14 CenterZ=0 NormalX=0 NormalY=0 NormalZ=1 AngleXU=0 Radius=1
    g34: Circle CenterX=-9.33087 CenterY=-15.1837 CenterZ=0 NormalX=0 NormalY=0 NormalZ=1 AngleXU=0 Radius=1
    g35: Circle CenterX=-10.1571 CenterY=-16 CenterZ=0 NormalX=0 NormalY=0 NormalZ=1 AngleXU=0 Radius=1
    g36: BSplineCurve PolesCount=3 KnotsCount=2 Degree=2 IsPeriodic=0
    g37: GeomPoint X=-8.70761 Y=-14 Z=0
    g38: GeomPoint X=-10.1571 Y=-16 Z=0
    g39: Circle CenterX=-12.8401 CenterY=-17.6958 CenterZ=0 NormalX=0 NormalY=0 NormalZ=1 AngleXU=0 Radius=1
    g40: Circle CenterX=-13.3521 CenterY=-17.9027 CenterZ=0 NormalX=0 NormalY=0 NormalZ=1 AngleXU=0 Radius=1
    g41: Circle CenterX=-14 CenterY=-18 CenterZ=0 NormalX=0 NormalY=0 NormalZ=1 AngleXU=0 Radius=1
    g42: BSplineCurve PolesCount=3 KnotsCount=2 Degree=2 IsPeriodic=0
    g43: GeomPoint X=-12.8401 Y=-17.6958 Z=0
    g44: GeomPoint X=-14 Y=-18 Z=0
    g45: LineSegment StartX=-6.2 StartY=0 StartZ=0 EndX=-7.2 EndY=0 EndZ=0
    g46: LineSegment StartX=-7.2 StartY=0 StartZ=0 EndX=-7.2 EndY=-2 EndZ=0
    g47: LineSegment StartX=-7.2 StartY=-2 StartZ=0 EndX=-6.2215 EndY=-2 EndZ=0
    g48: LineSegment StartX=-6.32538 StartY=-4 StartZ=0 EndX=-7.65538 EndY=-4 EndZ=0
    g49: LineSegment StartX=-7.65538 StartY=-4 StartZ=0 EndX=-7.65538 EndY=-5.99526 EndZ=0
    g50: LineSegment StartX=-7.65538 StartY=-5.99526 StartZ=0 EndX=-6.48644 EndY=-5.99526 EndZ=0
    g51: LineSegment StartX=-6.77343 StartY=-8 StartZ=0 EndX=-8.43343 EndY=-8 EndZ=0
    g52: LineSegment StartX=-8.43343 StartY=-8 StartZ=0 EndX=-8.43343 EndY=-10 EndZ=0
    g53: LineSegment StartX=-8.43343 StartY=-10 StartZ=0 EndX=-7.19003 EndY=-10 EndZ=0
  constraints (112):
    c: Horizontal(g0)
    c: Distance(g0) = 2
    c: Block(g0)
    c: Vertical(g1)
    c: Coincident(g2,g0)
    c: Vertical(g2)
    c: Block(g2)
    c: Coincident(g6,g2)
    c: Weight(g3) = 1
    c: Equal(g3,g4)
    c: Equal(g3,g5)
    c: InternalAlignment(g3,g6)
    c: InternalAlignment(g4,g6)
    c: InternalAlignment(g5,g6)
    c: InternalAlignment(g7,g6)
    c: InternalAlignment(g8,g6)
    c: Block(g6)
    c: Coincident(g9,g1)
    c: Coincident(g9,g6)
    c: Horizontal(g9)
    c: Vertical(g10)
    c: Block(g10)
    c: Horizontal(g11)
    c: Block(g11)
    c: Coincident(g12,g10)
    c: Horizontal(g12)
    c: Block(g12)
    c: Coincident(g13,g11)
    c: Vertical(g13)
    c: Block(g13)
    c: Coincident(g14,g10)
    c: Horizontal(g14)
    c: Block(g14)
    c: Block(g9)
    c: Block(g1)
    c: Weight(g15) = 1
    c: Equal(g15,g16)
    c: Equal(g15,g17)
    c: InternalAlignment(g15,g18)
    c: InternalAlignment(g16,g18)
    c: InternalAlignment(g17,g18)
    c: InternalAlignment(g19,g18)
    c: InternalAlignment(g20,g18)
    c: Weight(g21) = 1
    c: Equal(g21,g22)
    c: Equal(g21,g23)
    c: InternalAlignment(g21,g24)
    c: InternalAlignment(g22,g24)
    c: InternalAlignment(g23,g24)
    c: InternalAlignment(g25,g24)
    c: InternalAlignment(g26,g24)
    c: Weight(g27) = 1
    c: Equal(g27,g28)
    c: Equal(g27,g29)
    c: Coincident(g30,g14)
    c: InternalAlignment(g27,g30)
    c: InternalAlignment(g28,g30)
    c: InternalAlignment(g29,g30)
    c: InternalAlignment(g31,g30)
    c: InternalAlignment(g32,g30)
    c: Coincident(g36,g12)
    c: Weight(g33) = 1
    c: Equal(g33,g34)
    c: Equal(g33,g35)
    c: Coincident(g36,g11)
    c: InternalAlignment(g33,g36)
    c: InternalAlignment(g34,g36)
    c: InternalAlignment(g35,g36)
    c: InternalAlignment(g37,g36)
    c: InternalAlignment(g38,g36)
    c: Coincident(g42,g13)
    c: Weight(g39) = 1
    c: Equal(g39,g40)
    c: Equal(g39,g41)
    c: Coincident(g42,g1)
    c: InternalAlignment(g39,g42)
    c: InternalAlignment(g40,g42)
    c: InternalAlignment(g41,g42)
    c: InternalAlignment(g43,g42)
    c: InternalAlignment(g44,g42)
    c: Block(g18)
    c: Block(g24)
    c: Block(g30)
    c: Block(g36)
    c: Block(g42)
    c: Horizontal(g45)
    c: Coincident(g45,g0)
    c: Vertical(g46)
    c: Coincident(g46,g45)
    c: Coincident(g47,g46)
    c: Coincident(g47,g18)
    c: Horizontal(g47)
    c: Block(g46)
    c: Coincident(g48,g18)
    c: Horizontal(g48)
    c: Distance(g48) = 1.33
    c: Vertical(g49)
    c: Coincident(g49,g48)
    c: Coincident(g50,g49)
    c: Coincident(g50,g24)
    c: Horizontal(g50)
    c: Tangent(g50,g22)
    c: Horizontal(g51)
    c: Coincident(g51,g24)
    c: Block(g51)
    c: Vertical(g52)
    c: Block(g52)
    c: Coincident(g52,g51)
    c: Coincident(g53,g52)
    c: Coincident(g53,g30)
    c: Horizontal(g53)
    c: Distance(g1) = 8.5
FEATURE [Part::Feature] Face024
  shape: bbox 9.8 x 26.5 x 2e-07 mm, 1 faces, 0 solids (baked)
FEATURE [Part::Revolution] Revolve024
  Angle = 360
  Axis = (0,1,0)
  Base = (0,0,0)
  FaceMakerClass = Part::FaceMakerBullseye
  Placement = pos=(0,0,0) rot=(0,0,1;1.5708rad)
  Solid = false
  Source = -> Face024
  Symmetric = false
FEATURE [Part::Feature] Face025
  shape: bbox 9.8 x 26.5 x 2e-07 mm, 1 faces, 0 solids (baked)
FEATURE [Part::Revolution] Revolve025
  Angle = 360
  Axis = (0,1,0)
  Base = (0,0,0)
  FaceMakerClass = Part::FaceMakerBullseye
  Placement = pos=(0,0,0) rot=(0,0,1;1.5708rad)
  Solid = false
  Source = -> Face025
  Symmetric = false
FEATURE [Part::MultiFuse] Fusion033
  Placement = pos=(-18,19,36) rot=(0,0,1;0rad)
  Shapes = -> [Revolve025,Revolve024]
FEATURE [Part::Cylinder] Cylinder014
  Angle = 360
  AttacherType = Attacher::AttachEngine3D
  Height = 20
  Placement = pos=(0,0,36.15) rot=(0,0,1;0rad)
  Radius = 14.3
FEATURE [Part::Cylinder] Cylinder015
  Angle = 360
  AttacherType = Attacher::AttachEngine3D
  Height = 10
  Placement = pos=(0,0,36.15) rot=(0,0,1;0rad)
  Radius = 4
FEATURE [Part::MultiFuse] Fusion034  label="removeToCreteHoleForPlugHousing004"
  Placement = pos=(-42,19,36) rot=(0,1,0;1.5708rad)
  Shapes = -> [Cylinder014,Cylinder015]
FEATURE [Part::Cut] Cut008  label="top004"
  Base = -> Cut004
  Placement = pos=(-1,0,0) rot=(0,0,1;0rad)
  Tool = -> Fusion034
FEATURE [Part::Box] Box005  label="Cube005"
  AttacherType = Attacher::AttachEngine3D
  Height = 28
  Length = 3
  Placement = pos=(110.7,19,22) rot=(0,0,1;0rad)
  Width = 15.7
FEATURE [Part::Cylinder] Cylinder016
  Angle = 360
  AttacherType = Attacher::AttachEngine3D
  Height = 10
  Placement = pos=(0,0,36.15) rot=(0,0,1;0rad)
  Radius = 4
FEATURE [Part::Cylinder] Cylinder017
  Angle = 360
  AttacherType = Attacher::AttachEngine3D
  Height = 20
  Placement = pos=(0,0,36.15) rot=(0,0,1;0rad)
  Radius = 10.3
FEATURE [Part::MultiFuse] Fusion035  label="removeToCreteHoleForPlugHousing005"
  Placement = pos=(70,19,36) rot=(0,1,0;1.5708rad)
  Shapes = -> [Cylinder017,Cylinder016]
FEATURE [Part::Cut] Cut009  label="plugHousingTab001"
  Base = -> Box005
  Placement = pos=(-107.4,-14,0) rot=(0,0,1;0rad)
  Tool = -> Fusion035
FEATURE [Part::Box] Box006  label="Cube006"
  AttacherType = Attacher::AttachEngine3D
  Height = 28
  Length = 3
  Placement = pos=(110.7,19,22) rot=(0,0,1;0rad)
  Width = 15.7
FEATURE [Part::Cylinder] Cylinder018
  Angle = 360
  AttacherType = Attacher::AttachEngine3D
  Height = 10
  Placement = pos=(0,0,36.15) rot=(0,0,1;0rad)
  Radius = 4
FEATURE [Part::Cylinder] Cylinder019
  Angle = 360
  AttacherType = Attacher::AttachEngine3D
  Height = 20
  Placement = pos=(0,0,36.15) rot=(0,0,1;0rad)
  Radius = 10.3
FEATURE [Part::MultiFuse] Fusion036  label="removeToCreteHoleForPlugHousing006"
  Placement = pos=(70,19,36) rot=(0,1,0;1.5708rad)
  Shapes = -> [Cylinder019,Cylinder018]
FEATURE [Part::Cut] Cut010  label="plugHousingTab002"
  Base = -> Box006
  Placement = pos=(-107.4,-14,0) rot=(0,0,1;0rad)
  Tool = -> Fusion036
FEATURE [Part::MultiFuse] Fusion037
  Placement = pos=(9.6,23,0) rot=(0,0,1;3.14159rad)
  Shapes = -> [Cut009,Cut010]
FEATURE [Part::Box] Box  label="Cube"
  AttacherType = Attacher::AttachEngine3D
  Height = 10
  Length = 3
  Placement = pos=(3.3,4,12) rot=(0,0,1;0rad)
  Width = 10
FEATURE [Part::Fillet] Fillet004
  Base = -> Fusion028
  Edges = 1 edges r=2: [Edge25]
FEATURE [Part::Fillet] Fillet005  label="plugHousing046"
  Base = -> Fillet004
  Edges = 1 edges r=2: [Edge8]
FEATURE [Part::Fillet] Fillet006
  Base = -> Box
  Edges = 1 edges r=2: [Edge11]
FEATURE [Part::Box] Box007  label="Cube007"
  AttacherType = Attacher::AttachEngine3D
  Height = 10
  Length = 3
  Placement = pos=(3.3,4,50) rot=(0,0,1;0rad)
  Width = 10
FEATURE [Part::Fillet] Fillet007
  Base = -> Box007
  Edges = 1 edges r=2: [Edge12]
FEATURE [Part::Box] Box008  label="Cube008"
  AttacherType = Attacher::AttachEngine3D
  Height = 28
  Length = 4
  Placement = pos=(5,0,22) rot=(0,0,1;0rad)
  Width = 10
FEATURE [Part::Fillet] Fillet008
  Base = -> Box008
  Edges = 1 edges r=1: [Edge7]
FEATURE [Part::Fillet] Fillet009
  Base = -> Fillet008
  Edges = 1 edges r=2: [Edge5]
FEATURE [Part::Fillet] Fillet010
  Base = -> Fillet009
  Edges = 1 edges r=2: [Edge2]
FEATURE [Sketcher::SketchObject] Sketch009  label="topSketch003"
  FullyConstrained = true
  sketch-geometry (4):
    g0: LineSegment StartX=16.8446 StartY=31.512 StartZ=0 EndX=16.3251 EndY=34.4666 EndZ=0
    g1: ArcOfCircle CenterX=19 CenterY=19.2524 CenterZ=0 NormalX=0 NormalY=0 NormalZ=1 AngleXU=0 Radius=15.4476 StartAngle=1.74483 EndAngle=2.72717
    g2: ArcOfCircle CenterX=19 CenterY=19.2524 CenterZ=0 NormalX=0 NormalY=0 NormalZ=1 AngleXU=0 Radius=12.4476 StartAngle=1.74483 EndAngle=2.73189
    g3: LineSegment StartX=4.86004 StartY=25.4725 StartZ=0 EndX=7.58253 EndY=24.2107 EndZ=0
  constraints (7):
    c: Block(g0)
    c: Coincident(g1,g0)
    c: Coincident(g2,g0)
    c: Coincident(g3,g1)
    c: Coincident(g3,g2)
    c: Block(g1)
    c: Block(g2)
FEATURE [Part::Extrusion] Extrude008
  Base = -> Sketch009
  Dir = (0,0,1)
  DirMode = 2
  FaceMakerClass = Part::FaceMakerBullseye
  LengthFwd = 10
  LengthRev = 0
  Placement = pos=(0,0,31) rot=(0,0,1;0rad)
  Solid = true
  Symmetric = false
FEATURE [Part::Cylinder] Cylinder020
  Angle = 360
  AttacherType = Attacher::AttachEngine3D
  Height = 20
  Placement = pos=(0,0,36.15) rot=(0,0,1;0rad)
  Radius = 8.2
FEATURE [Part::Cylinder] Cylinder021
  Angle = 360
  AttacherType = Attacher::AttachEngine3D
  Height = 10
  Placement = pos=(0,0,36.15) rot=(0,0,1;0rad)
  Radius = 4
FEATURE [Part::MultiFuse] Fusion038  label="removeToCreteHoleForPlugHousing007"
  Placement = pos=(-42,19,36) rot=(0,1,0;1.5708rad)
  Shapes = -> [Cylinder020,Cylinder021]
FEATURE [Part::Cut] Cut011
  Base = -> Extrude008
  Tool = -> Fusion038
FEATURE [Part::Fillet] Fillet011
  Base = -> Cut011
  Edges = 1 edges r=2: [Edge1]
FEATURE [Part::Fillet] Fillet012
  Base = -> Fillet011
  Edges = 1 edges r=2.5: [Edge1]
FEATURE [Part::Fillet] Fillet013
  Base = -> Fillet012
  Edges = 1 edges r=2.5: [Edge2]
FEATURE [Part::Box] Box010  label="Cube010"
  AttacherType = Attacher::AttachEngine3D
  Height = 16
  Length = 8
  Placement = pos=(12.7,31.52,28) rot=(0,0,1;0rad)
  Width = 4
FEATURE [Sketcher::SketchObject] Sketch010  label="topSketch004"
  FullyConstrained = true
  sketch-geometry (4):
    g0: LineSegment StartX=16.8446 StartY=31.512 StartZ=0 EndX=16.3251 EndY=34.4666 EndZ=0
    g1: ArcOfCircle CenterX=19 CenterY=19.2524 CenterZ=0 NormalX=0 NormalY=0 NormalZ=1 AngleXU=0 Radius=15.4476 StartAngle=1.74483 EndAngle=2.72717
    g2: ArcOfCircle CenterX=19 CenterY=19.2524 CenterZ=0 NormalX=0 NormalY=0 NormalZ=1 AngleXU=0 Radius=12.4476 StartAngle=1.74483 EndAngle=2.73189
    g3: LineSegment StartX=4.86004 StartY=25.4725 StartZ=0 EndX=7.58253 EndY=24.2107 EndZ=0
  constraints (7):
    c: Block(g0)
    c: Coincident(g1,g0)
    c: Coincident(g2,g0)
    c: Coincident(g3,g1)
    c: Coincident(g3,g2)
    c: Block(g1)
    c: Block(g2)
FEATURE [Part::Cylinder] Cylinder022
  Angle = 360
  AttacherType = Attacher::AttachEngine3D
  Height = 10
  Placement = pos=(0,0,36.15) rot=(0,0,1;0rad)
  Radius = 4
FEATURE [Sketcher::SketchObject] Sketch011  label="topSketch005"
  FullyConstrained = true
  sketch-geometry (4):
    g0: LineSegment StartX=16.8446 StartY=31.512 StartZ=0 EndX=16.3251 EndY=34.4666 EndZ=0
    g1: ArcOfCircle CenterX=19 CenterY=19.2524 CenterZ=0 NormalX=0 NormalY=0 NormalZ=1 AngleXU=0 Radius=15.4476 StartAngle=1.74483 EndAngle=2.72717
    g2: ArcOfCircle CenterX=19 CenterY=19.2524 CenterZ=0 NormalX=0 NormalY=0 NormalZ=1 AngleXU=0 Radius=12.4476 StartAngle=1.74483 EndAngle=2.73189
    g3: LineSegment StartX=4.86004 StartY=25.4725 StartZ=0 EndX=7.58253 EndY=24.2107 EndZ=0
  constraints (7):
    c: Block(g0)
    c: Coincident(g1,g0)
    c: Coincident(g2,g0)
    c: Coincident(g3,g1)
    c: Coincident(g3,g2)
    c: Block(g1)
    c: Block(g2)
FEATURE [Part::Extrusion] Extrude010
  Base = -> Sketch011
  Dir = (0,0,1)
  DirMode = 2
  FaceMakerClass = Part::FaceMakerBullseye
  LengthFwd = 10.6
  LengthRev = 0
  Placement = pos=(0,0,31) rot=(0,0,1;0rad)
  Solid = true
  Symmetric = false
FEATURE [Part::Cylinder] Cylinder023
  Angle = 360
  AttacherType = Attacher::AttachEngine3D
  Height = 20
  Placement = pos=(0,0,36.15) rot=(0,0,1;0rad)
  Radius = 8.2
FEATURE [Part::MultiFuse] Fusion039  label="removeToCreteHoleForPlugHousing008"
  Placement = pos=(-42,19,36) rot=(0,1,0;1.5708rad)
  Shapes = -> [Cylinder023,Cylinder022]
FEATURE [Part::Cut] Cut012
  Base = -> Extrude010
  Placement = pos=(0,0,-0.3) rot=(0,0,1;0rad)
  Tool = -> Fusion039
FEATURE [Part::Cut] Cut013
  Base = -> Box010
  Tool = -> Cut012
FEATURE [Part::Fillet] Fillet014
  Base = -> Cut013
  Edges = 1 edges r=0.7: [Edge13]
FEATURE [Part::Fillet] Fillet015
  Base = -> Fillet014
  Edges = 1 edges r=0.7: [Edge13]
FEATURE [Part::Fillet] Fillet016
  Base = -> Fillet015
  Edges = 1 edges r=0.7: [Edge16]
FEATURE [Part::Fillet] Fillet017
  Base = -> Fillet016
  Edges = 1 edges r=0.7: [Edge11]
FEATURE [Part::Fillet] Fillet018
  Base = -> Fillet017
  Edges = 1 edges r=0.7: [Edge10]
FEATURE [Part::Fillet] Fillet019
  Base = -> Fillet018
  Edges = 1 edges r=1.2: [Edge5]
FEATURE [Part::Fillet] Fillet020
  Base = -> Fillet019
  Edges = 1 edges r=1.2: [Edge12]
FEATURE [Part::Fillet] Fillet021
  Base = -> Fillet020
  Edges = 1 edges r=2: [Edge1]
  Placement = pos=(0.3,0,0) rot=(0,0,1;0rad)
FEATURE [Part::MultiFuse] Fusion040  label="top005"
  Shapes = -> [Cut008,Fillet021]
FEATURE [Part::MultiFuse] Fusion041  label="wireHolder"
  Shapes = -> [Fusion033,Fillet013]
FEATURE [Part::MultiFuse] Fusion042
  Shapes = -> [Fillet007,Fusion041]
FEATURE [Part::MultiFuse] Fusion043  label="wireHolder001"
  Shapes = -> [Fusion042,Fillet010]
FEATURE [Part::MultiFuse] Fusion044  label="wireHolder002"
  Shapes = -> [Fillet006,Fusion037,Fusion043]
FEATURE [Part::Feature] Face026
  shape: bbox 11 x 6 x 2e-07 mm, 1 faces, 0 solids (baked)
FEATURE [Part::Revolution] Revolve026
  Angle = 360
  Axis = (0,1,0)
  Base = (0,0,0)
  FaceMakerClass = Part::FaceMakerBullseye
  Placement = pos=(30.3,-1,19.7) rot=(0,0,1;0rad)
  Solid = false
  Source = -> Face026
  Symmetric = false
FEATURE [Sketcher::SketchObject] Sketch013  label="topSketch006"
  FullyConstrained = true
  sketch-geometry (13):
    g0: LineSegment StartX=117 StartY=19 StartZ=0 EndX=117 EndY=38 EndZ=0
    g1: ArcOfCircle CenterX=98 CenterY=19 CenterZ=0 NormalX=0 NormalY=0 NormalZ=1 AngleXU=0 Radius=19 StartAngle=5.7297 EndAngle=6.28319
    g2: LineSegment StartX=0 StartY=3 StartZ=0 EndX=0 EndY=19 EndZ=0
    g3: LineSegment StartX=19 StartY=38 StartZ=0 EndX=117 EndY=38 EndZ=0
    g4: ArcOfCircle CenterX=19 CenterY=19 CenterZ=0 NormalX=0 NormalY=0 NormalZ=1 AngleXU=0 Radius=19 StartAngle=1.5708 EndAngle=3.14159
    g5: ArcOfCircle CenterX=19 CenterY=19 CenterZ=0 NormalX=0 NormalY=0 NormalZ=1 AngleXU=0 Radius=16 StartAngle=1.5708 EndAngle=3.14159
    g6: ArcOfCircle CenterX=98 CenterY=19 CenterZ=0 NormalX=0 NormalY=0 NormalZ=1 AngleXU=0 Radius=16 StartAngle=5.60905 EndAngle=6.28319
    g7: LineSegment StartX=114 StartY=19 StartZ=0 EndX=114 EndY=35 EndZ=0
    g8: LineSegment StartX=110.5 StartY=9.01251 StartZ=0 EndX=114.163 EndY=9.01251 EndZ=0
    g9: LineSegment StartX=114 StartY=35 StartZ=0 EndX=19 EndY=35 EndZ=0
    g10: LineSegment StartX=0 StartY=3 StartZ=0 EndX=0 EndY=0 EndZ=0
    g11: LineSegment StartX=3 StartY=0 StartZ=0 EndX=0 EndY=0 EndZ=0
    g12: LineSegment StartX=3 StartY=19 StartZ=0 EndX=3 EndY=0 EndZ=0
  constraints (33):
    c: Vertical(g0)
    c: Distance(g0) = 19
    c: Block(g0)
    c: Coincident(g1,g0)
    c: Block(g1)
    c: Vertical(g2)
    c: Block(g2)
    c: Coincident(g3,g0)
    c: Horizontal(g3)
    c: Distance(g3) = 98
    c: Coincident(g4,g3)
    c: Coincident(g4,g2)
    c: Block(g4)
    c: Coincident(g5,g4)
    c: Coincident(g6,g1)
    c: Block(g6)
    c: Block(g5)
    c: Coincident(g7,g6)
    c: Vertical(g7)
    c: Coincident(g8,g6)
    c: Coincident(g8,g1)
    c: Coincident(g9,g7)
    c: Coincident(g9,g5)
    c: Horizontal(g9)
    c: Tangent(g9,g5)
    c: Coincident(g10,g2)
    c: Distance(g10) = 3
    c: Vertical(g10)
    c: Coincident(g11,g10)
    c: Horizontal(g11)
    c: Coincident(g12,g5)
    c: Coincident(g12,g11)
    c: Vertical(g12)
FEATURE [Part::Extrusion] Extrude011  label="top006"
  Base = -> Sketch013
  Dir = (0,0,1)
  DirMode = 2
  FaceMakerClass = Part::FaceMakerBullseye
  LengthFwd = 72
  LengthRev = 0
  Solid = true
  Symmetric = false
FEATURE [Sketcher::SketchObject] Sketch014
  FullyConstrained = true
  MapMode = 3
  Placement = pos=(0,0,0) rot=(1,0,0;1.5708rad)
  Support = -> [Extrude011]
  sketch-geometry (8):
    g0: Circle CenterX=80.351 CenterY=-67.6202 CenterZ=0 NormalX=0 NormalY=0 NormalZ=1 AngleXU=0 Radius=2
    g1: Circle CenterX=80.351 CenterY=-67.6202 CenterZ=0 NormalX=0 NormalY=0 NormalZ=1 AngleXU=0 Radius=3
    g2: Circle CenterX=80.351 CenterY=-4.92017 CenterZ=0 NormalX=0 NormalY=0 NormalZ=1 AngleXU=0 Radius=2
    g3: Circle CenterX=80.351 CenterY=-4.92017 CenterZ=0 NormalX=0 NormalY=0 NormalZ=1 AngleXU=0 Radius=3
    g4: Circle CenterX=23.851 CenterY=-4.92017 CenterZ=0 NormalX=0 NormalY=0 NormalZ=1 AngleXU=0 Radius=2
    g5: Circle CenterX=23.851 CenterY=-4.92017 CenterZ=0 NormalX=0 NormalY=0 NormalZ=1 AngleXU=0 Radius=3
    g6: Circle CenterX=23.851 CenterY=-67.6202 CenterZ=0 NormalX=0 NormalY=0 NormalZ=1 AngleXU=0 Radius=2
    g7: Circle CenterX=23.851 CenterY=-67.6202 CenterZ=0 NormalX=0 NormalY=0 NormalZ=1 AngleXU=0 Radius=3
  constraints (8):
    c: Block(g3)
    c: Block(g2)
    c: Block(g1)
    c: Block(g0)
    c: Block(g6)
    c: Block(g7)
    c: Block(g4)
    c: Block(g5)
FEATURE [Part::Feature] Face027
  shape: bbox 11 x 6 x 2e-07 mm, 1 faces, 0 solids (baked)
FEATURE [Part::Revolution] Revolve027
  Angle = 360
  Axis = (0,1,0)
  Base = (0,0,0)
  FaceMakerClass = Part::FaceMakerBullseye
  Placement = pos=(30.3,-1,51.7) rot=(0,0,1;0rad)
  Solid = false
  Source = -> Face027
  Symmetric = false
FEATURE [Part::Feature] Face028
  shape: bbox 11 x 6 x 2e-07 mm, 1 faces, 0 solids (baked)
FEATURE [Part::Revolution] Revolve028
  Angle = 360
  Axis = (0,1,0)
  Base = (0,0,0)
  FaceMakerClass = Part::FaceMakerBullseye
  Placement = pos=(62.3,-1,19.7) rot=(0,0,1;0rad)
  Solid = false
  Source = -> Face028
  Symmetric = false
FEATURE [Part::Feature] Face029
  shape: bbox 11 x 6 x 2e-07 mm, 1 faces, 0 solids (baked)
FEATURE [Part::Revolution] Revolve029
  Angle = 360
  Axis = (0,1,0)
  Base = (0,0,0)
  FaceMakerClass = Part::FaceMakerBullseye
  Placement = pos=(62.3,-1,51.7) rot=(0,0,1;0rad)
  Solid = false
  Source = -> Face029
  Symmetric = false
FEATURE [Part::Feature] Wire
  shape: bbox 11 x 5.2 x 2e-07 mm, 0 faces, 0 solids (baked)
FEATURE [Part::Revolution] Revolve030
  Angle = 360
  Axis = (0,1,0)
  Base = (0,0,0)
  FaceMakerClass = Part::FaceMakerBullseye
  Placement = pos=(30.3,38,19.7) rot=(0,0,1;0rad)
  Solid = true
  Source = -> Wire
  Symmetric = false
FEATURE [Part::Feature] Wire001
  shape: bbox 11 x 5.2 x 2e-07 mm, 0 faces, 0 solids (baked)
FEATURE [Part::Revolution] Revolve031
  Angle = 360
  Axis = (0,1,0)
  Base = (0,0,0)
  FaceMakerClass = Part::FaceMakerBullseye
  Placement = pos=(30.3,38,51.7) rot=(0,0,1;0rad)
  Solid = true
  Source = -> Wire001
  Symmetric = false
FEATURE [Part::Feature] Wire002
  shape: bbox 11 x 5.2 x 2e-07 mm, 0 faces, 0 solids (baked)
FEATURE [Part::Revolution] Revolve032
  Angle = 360
  Axis = (0,1,0)
  Base = (0,0,0)
  FaceMakerClass = Part::FaceMakerBullseye
  Placement = pos=(62.3,38,51.7) rot=(0,0,1;0rad)
  Solid = true
  Source = -> Wire002
  Symmetric = false
FEATURE [Part::Feature] Wire003
  shape: bbox 11 x 5.2 x 2e-07 mm, 0 faces, 0 solids (baked)
FEATURE [Part::Revolution] Revolve033
  Angle = 360
  Axis = (0,1,0)
  Base = (0,0,0)
  FaceMakerClass = Part::FaceMakerBullseye
  Placement = pos=(62.3,38,19.7) rot=(0,0,1;0rad)
  Solid = true
  Source = -> Wire003
  Symmetric = false
FEATURE [Part::MultiFuse] Fusion045  label="altRandScrewHousing"
  Shapes = -> [Revolve029,Revolve027,Revolve028,Revolve026]
FEATURE [Part::MultiFuse] Fusion046  label="fanScrewHousing"
  Shapes = -> [Revolve033,Revolve032,Revolve031,Revolve030]
FEATURE [Sketcher::SketchObject] Sketch015
  FullyConstrained = true
  sketch-geometry (17):
    g0: Circle CenterX=-3.5 CenterY=23.5 CenterZ=0 NormalX=0 NormalY=0 NormalZ=1 AngleXU=0 Radius=1
    g1: Circle CenterX=-1 CenterY=15.25 CenterZ=0 NormalX=0 NormalY=0 NormalZ=1 AngleXU=0 Radius=1
    g2: Circle CenterX=-3.5 CenterY=7 CenterZ=0 NormalX=0 NormalY=0 NormalZ=1 AngleXU=0 Radius=1
    g3: BSplineCurve PolesCount=3 KnotsCount=2 Degree=2 IsPeriodic=0
    g4: GeomPoint X=-3.5 Y=23.5 Z=0
    g5: GeomPoint X=-3.5 Y=7 Z=0
    g6: Circle CenterX=-4.8 CenterY=30.5 CenterZ=0 NormalX=0 NormalY=0 NormalZ=1 AngleXU=0 Radius=1
    g7: Circle CenterX=-3.5 CenterY=30.5 CenterZ=0 NormalX=0 NormalY=0 NormalZ=1 AngleXU=0 Radius=1
    g8: Circle CenterX=-3.5 CenterY=29.2 CenterZ=0 NormalX=0 NormalY=0 NormalZ=1 AngleXU=0 Radius=1
    g9: BSplineCurve PolesCount=3 KnotsCount=2 Degree=2 IsPeriodic=0
    g10: GeomPoint X=-4.8 Y=30.5 Z=0
    g11: GeomPoint X=-3.5 Y=29.2 Z=0
    g12: LineSegment StartX=-3.5 StartY=29.2 StartZ=0 EndX=-3.5 EndY=23.5 EndZ=0
    g13: LineSegment StartX=-4.8 StartY=30.5 StartZ=0 EndX=0 EndY=30.5 EndZ=0
    g14: LineSegment StartX=-3.5 StartY=0.3 StartZ=0 EndX=0 EndY=0.3 EndZ=0
    g15: LineSegment StartX=-3.5 StartY=0.3 StartZ=0 EndX=-3.5 EndY=7 EndZ=0
    g16: LineSegment StartX=0 StartY=0.3 StartZ=0 EndX=0 EndY=30.5 EndZ=0
  constraints (34):
    c: Weight(g0) = 1
    c: Equal(g0,g1)
    c: Equal(g0,g2)
    c: InternalAlignment(g0,g3)
    c: InternalAlignment(g1,g3)
    c: InternalAlignment(g2,g3)
    c: InternalAlignment(g4,g3)
    c: InternalAlignment(g5,g3)
    c: Block(g3)
    c: Weight(g6) = 1
    c: Equal(g6,g7)
    c: Equal(g6,g8)
    c: InternalAlignment(g6,g9)
    c: InternalAlignment(g7,g9)
    c: InternalAlignment(g8,g9)
    c: InternalAlignment(g10,g9)
    c: InternalAlignment(g11,g9)
    c: Block(g9)
    c: Coincident(g12,g9)
    c: Coincident(g12,g3)
    c: Vertical(g12)
    c: Coincident(g13,g9)
    c: Horizontal(g13)
    c: Distance(g13) = 4.8
    c: Horizontal(g14)
    c: Block(g14)
    c: Coincident(g15,g14)
    c: Coincident(g15,g3)
    c: Vertical(g15)
    c: Coincident(g16,g14)
    c: Coincident(g16,g13)
    c: Vertical(g16)
    c: Tangent(g16,g1)
    c: Distance(g14) = 3.5
FEATURE [Sketcher::SketchObject] Sketch016
  FullyConstrained = true
  sketch-geometry (16):
    g0: Circle CenterX=-3.5 CenterY=23.5 CenterZ=0 NormalX=0 NormalY=0 NormalZ=1 AngleXU=0 Radius=1
    g1: Circle CenterX=-1 CenterY=15.25 CenterZ=0 NormalX=0 NormalY=0 NormalZ=1 AngleXU=0 Radius=1
    g2: Circle CenterX=-3.5 CenterY=7 CenterZ=0 NormalX=0 NormalY=0 NormalZ=1 AngleXU=0 Radius=1
    g3: BSplineCurve PolesCount=3 KnotsCount=2 Degree=2 IsPeriodic=0
    g4: GeomPoint X=-3.5 Y=23.5 Z=0
    g5: GeomPoint X=-3.5 Y=7 Z=0
    g6: LineSegment StartX=-3.5 StartY=28.2 StartZ=0 EndX=-3.5 EndY=23.5 EndZ=0
    g7: LineSegment StartX=0 StartY=29.5 StartZ=0 EndX=0 EndY=30 EndZ=0
    g8: LineSegment StartX=-3.5 StartY=28.2 StartZ=0 EndX=-3.5 EndY=30 EndZ=0
    g9: LineSegment StartX=0 StartY=30 StartZ=0 EndX=0 EndY=30.5 EndZ=0
    g10: LineSegment StartX=0 StartY=30.5 StartZ=0 EndX=-3.5 EndY=30.5 EndZ=0
    g11: LineSegment StartX=-3.5 StartY=30.5 StartZ=0 EndX=-3.5 EndY=30 EndZ=0
    g12: LineSegment StartX=0 StartY=29.5 StartZ=0 EndX=0 EndY=5 EndZ=0
    g13: LineSegment StartX=-3.5 StartY=0.3 StartZ=0 EndX=-3.5 EndY=7 EndZ=0
    g14: LineSegment StartX=-3.5 StartY=0.3 StartZ=0 EndX=0 EndY=0.3 EndZ=0
    g15: LineSegment StartX=0 StartY=5 StartZ=0 EndX=0 EndY=0.3 EndZ=0
  constraints (39):
    c: Weight(g0) = 1
    c: Equal(g0,g1)
    c: Equal(g0,g2)
    c: InternalAlignment(g0,g3)
    c: InternalAlignment(g1,g3)
    c: InternalAlignment(g2,g3)
    c: InternalAlignment(g4,g3)
    c: InternalAlignment(g5,g3)
    c: Block(g3)
    c: Coincident(g6,g3)
    c: Vertical(g6)
    c: Vertical(g7)
    c: Distance(g7) = 0.5
    c: Coincident(g8,g6)
    c: Vertical(g8)
    c: Block(g6)
    c: Block(g7)
    c: Vertical(g9)
    c: Equal(g7,g9) = 0.5
    c: Block(g9)
    c: Coincident(g9,g7)
    c: Horizontal(g10)
    c: Coincident(g10,g9)
    c: Coincident(g11,g10)
    c: Coincident(g11,g8)
    c: Vertical(g11)
    c: Block(g11)
    c: Coincident(g12,g7)
    c: Vertical(g12)
    c: Coincident(g13,g3)
    c: Vertical(g13)
    c: Distance(g13) = 6.7
    c: Coincident(g14,g13)
    c: Horizontal(g14)
    c: Block(g14)
    c: Coincident(g15,g12)
    c: Coincident(g15,g14)
    c: Vertical(g15)
    c: Block(g15)
FEATURE [Sketcher::SketchObject] Sketch017
  FullyConstrained = true
  sketch-geometry (11):
    g0: LineSegment StartX=-3.5 StartY=1e-16 StartZ=0 EndX=-1.6 EndY=1e-16 EndZ=0
    g1: LineSegment StartX=-1.6 StartY=1e-16 StartZ=0 EndX=-1.6 EndY=1.5 EndZ=0
    g2: LineSegment StartX=-3.5 StartY=1.5 StartZ=0 EndX=-1.6 EndY=1.5 EndZ=0
    g3: LineSegment StartX=-3.5 StartY=1e-16 StartZ=0 EndX=-4.8 EndY=1e-16 EndZ=0
    g4: Circle CenterX=-3.5 CenterY=1.3 CenterZ=0 NormalX=0 NormalY=0 NormalZ=1 AngleXU=0 Radius=1
    g5: Circle CenterX=-3.5 CenterY=1e-16 CenterZ=0 NormalX=0 NormalY=0 NormalZ=1 AngleXU=0 Radius=1
    g6: Circle CenterX=-4.8 CenterY=1e-16 CenterZ=0 NormalX=0 NormalY=0 NormalZ=1 AngleXU=0 Radius=1
    g7: BSplineCurve PolesCount=3 KnotsCount=2 Degree=2 IsPeriodic=0
    g8: GeomPoint X=-3.5 Y=1.3 Z=0
    g9: GeomPoint X=-4.8 Y=1e-16 Z=0
    g10: LineSegment StartX=-3.5 StartY=1.3 StartZ=0 EndX=-3.5 EndY=1.5 EndZ=0
  constraints (24):
    c: Horizontal(g0)
    c: Distance(g0) = 1.9
    c: Block(g0)
    c: Coincident(g1,g0)
    c: Vertical(g1)
    c: Coincident(g2,g1)
    c: Horizontal(g2)
    c: Coincident(g3,g0)
    c: Horizontal(g3)
    c: Distance(g3) = 1.3
    c: Weight(g4) = 1
    c: Equal(g4,g5)
    c: Coincident(g5,g0)
    c: Equal(g4,g6)
    c: Coincident(g7,g3)
    c: InternalAlignment(g4,g7)
    c: InternalAlignment(g5,g7)
    c: InternalAlignment(g6,g7)
    c: InternalAlignment(g8,g7)
    c: InternalAlignment(g9,g7)
    c: Coincident(g10,g7)
    c: Coincident(g10,g2)
    c: Vertical(g10)
    c: Block(g10)
FEATURE [Part::Feature] Face035
  shape: bbox 3.2 x 1.5 x 2e-07 mm, 1 faces, 0 solids (baked)
FEATURE [Part::Revolution] Revolve039  label="backCaseScrewRetainer"
  Angle = 360
  Axis = (0,1,0)
  Base = (0,0,0)
  FaceMakerClass = Part::FaceMakerBullseye
  Placement = pos=(12.5,3,62) rot=(0,0,1;0rad)
  Solid = false
  Source = -> Face035
  Symmetric = false
FEATURE [Part::Feature] Face036
  shape: bbox 3.2 x 1.5 x 2e-07 mm, 1 faces, 0 solids (baked)
FEATURE [Part::Feature] Face039
  shape: bbox 4.8 x 30.2 x 2e-07 mm, 1 faces, 0 solids (baked)
FEATURE [Part::Revolution] Revolve043  label="frontCaseScrewPost002"
  Angle = 360
  Axis = (0,1,0)
  Base = (0,0,0)
  FaceMakerClass = Part::FaceMakerBullseye
  Placement = pos=(89.5,4.5,3.5) rot=(0,0,1;0rad)
  Solid = false
  Source = -> Face039
  Symmetric = false
FEATURE [Part::Feature] Face042
  shape: bbox 4.8 x 30.2 x 2e-07 mm, 1 faces, 0 solids (baked)
FEATURE [Part::Revolution] Revolve046  label="frontCaseScrewPost003"
  Angle = 360
  Axis = (0,1,0)
  Base = (0,0,0)
  FaceMakerClass = Part::FaceMakerBullseye
  Placement = pos=(89.5,4.5,68.5) rot=(0,0,1;0rad)
  Solid = false
  Source = -> Face042
  Symmetric = false
FEATURE [Part::Feature] Face043
  shape: bbox 3.2 x 1.5 x 2e-07 mm, 1 faces, 0 solids (baked)
FEATURE [Part::Revolution] Revolve047  label="frontCaseScrewRetainer002"
  Angle = 360
  Axis = (0,1,0)
  Base = (0,0,0)
  FaceMakerClass = Part::FaceMakerBullseye
  Placement = pos=(89.5,3,68.5) rot=(0,0,1;0rad)
  Solid = false
  Source = -> Face043
  Symmetric = false
FEATURE [Part::Feature] Face044
  shape: bbox 3.2 x 1.5 x 2e-07 mm, 1 faces, 0 solids (baked)
FEATURE [Part::Revolution] Revolve048  label="frontCaseScrewRetainer003"
  Angle = 360
  Axis = (0,1,0)
  Base = (0,0,0)
  FaceMakerClass = Part::FaceMakerBullseye
  Placement = pos=(89.5,3,3.5) rot=(0,0,1;0rad)
  Solid = false
  Source = -> Face044
  Symmetric = false
FEATURE [App::MeasureDistance] Distance002  label="Distance: 1.67 mm"
  Distance = 1.66921
  P1 = (99.2361,4.7524,71.7)
  P2 = (99.2347,6.42161,71.7)
FEATURE [Sketcher::SketchObject] Sketch018
  FullyConstrained = true
  sketch-geometry (7):
    g0: LineSegment StartX=0 StartY=0 StartZ=0 EndX=0 EndY=6 EndZ=0
    g1: Circle CenterX=0 CenterY=0 CenterZ=0 NormalX=0 NormalY=0 NormalZ=1 AngleXU=0 Radius=1
    g2: Circle CenterX=8 CenterY=6 CenterZ=0 NormalX=0 NormalY=0 NormalZ=1 AngleXU=0 Radius=1
    g3: BSplineCurve PolesCount=3 KnotsCount=2 Degree=2 IsPeriodic=0
    g4: GeomPoint X=0 Y=0 Z=0
    g5: GeomPoint X=8 Y=6 Z=0
    g6: LineSegment StartX=0 StartY=6 StartZ=0 EndX=8 EndY=6 EndZ=0
  constraints (14):
    c: Coincident(g0,g-1)
    c: Distance(g0) = 6
    c: Vertical(g0)
    c: Coincident(g3,g0)
    c: Weight(g1) = 1
    c: Equal(g1,g2)
    c: InternalAlignment(g1,g3)
    c: InternalAlignment(g2,g3)
    c: InternalAlignment(g4,g3)
    c: InternalAlignment(g5,g3)
    c: Block(g3)
    c: Coincident(g6,g0)
    c: Coincident(g6,g3)
    c: Horizontal(g6)
FEATURE [Part::Extrusion] Extrude012  label="caseScrewPillarBracket"
  Base = -> Sketch018
  Dir = (0,0,1)
  DirMode = 2
  FaceMakerClass = Part::FaceMakerBullseye
  LengthFwd = 2.4
  LengthRev = 0
  Placement = pos=(15.76,29,8.8) rot=(0,1,0;0rad)
  Solid = true
  Symmetric = false
FEATURE [Sketcher::SketchObject] Sketch019
  FullyConstrained = true
  sketch-geometry (7):
    g0: LineSegment StartX=0 StartY=0 StartZ=0 EndX=0 EndY=6 EndZ=0
    g1: Circle CenterX=0 CenterY=0 CenterZ=0 NormalX=0 NormalY=0 NormalZ=1 AngleXU=0 Radius=1
    g2: Circle CenterX=8 CenterY=6 CenterZ=0 NormalX=0 NormalY=0 NormalZ=1 AngleXU=0 Radius=1
    g3: BSplineCurve PolesCount=3 KnotsCount=2 Degree=2 IsPeriodic=0
    g4: GeomPoint X=0 Y=0 Z=0
    g5: GeomPoint X=8 Y=6 Z=0
    g6: LineSegment StartX=0 StartY=6 StartZ=0 EndX=8 EndY=6 EndZ=0
  constraints (14):
    c: Coincident(g0,g-1)
    c: Distance(g0) = 6
    c: Vertical(g0)
    c: Coincident(g3,g0)
    c: Weight(g1) = 1
    c: Equal(g1,g2)
    c: InternalAlignment(g1,g3)
    c: InternalAlignment(g2,g3)
    c: InternalAlignment(g4,g3)
    c: InternalAlignment(g5,g3)
    c: Block(g3)
    c: Coincident(g6,g0)
    c: Coincident(g6,g3)
    c: Horizontal(g6)
FEATURE [Part::Extrusion] Extrude013  label="caseScrewPillarBracket001"
  Base = -> Sketch019
  Dir = (0,0,1)
  DirMode = 2
  FaceMakerClass = Part::FaceMakerBullseye
  LengthFwd = 2.4
  LengthRev = 0
  Placement = pos=(15.76,29,60.8) rot=(0,0,1;0rad)
  Solid = true
  Symmetric = false
FEATURE [Sketcher::SketchObject] Sketch020
  FullyConstrained = true
  sketch-geometry (7):
    g0: LineSegment StartX=0 StartY=0 StartZ=0 EndX=0 EndY=6 EndZ=0
    g1: Circle CenterX=0 CenterY=0 CenterZ=0 NormalX=0 NormalY=0 NormalZ=1 AngleXU=0 Radius=1
    g2: Circle CenterX=8 CenterY=6 CenterZ=0 NormalX=0 NormalY=0 NormalZ=1 AngleXU=0 Radius=1
    g3: BSplineCurve PolesCount=3 KnotsCount=2 Degree=2 IsPeriodic=0
    g4: GeomPoint X=0 Y=0 Z=0
    g5: GeomPoint X=8 Y=6 Z=0
    g6: LineSegment StartX=0 StartY=6 StartZ=0 EndX=8 EndY=6 EndZ=0
  constraints (14):
    c: Coincident(g0,g-1)
    c: Distance(g0) = 6
    c: Vertical(g0)
    c: Coincident(g3,g0)
    c: Weight(g1) = 1
    c: Equal(g1,g2)
    c: InternalAlignment(g1,g3)
    c: InternalAlignment(g2,g3)
    c: InternalAlignment(g4,g3)
    c: InternalAlignment(g5,g3)
    c: Block(g3)
    c: Coincident(g6,g0)
    c: Coincident(g6,g3)
    c: Horizontal(g6)
FEATURE [Part::Extrusion] Extrude014  label="caseScrewPillarBracket002"
  Base = -> Sketch020
  Dir = (0,0,1)
  DirMode = 2
  FaceMakerClass = Part::FaceMakerBullseye
  LengthFwd = 2.4
  LengthRev = 0
  Placement = pos=(13.7,29,13.26) rot=(0,-1,0;1.5708rad)
  Solid = true
  Symmetric = false
FEATURE [Sketcher::SketchObject] Sketch021
  FullyConstrained = true
  sketch-geometry (7):
    g0: LineSegment StartX=0 StartY=0 StartZ=0 EndX=0 EndY=6 EndZ=0
    g1: Circle CenterX=0 CenterY=0 CenterZ=0 NormalX=0 NormalY=0 NormalZ=1 AngleXU=0 Radius=1
    g2: Circle CenterX=8 CenterY=6 CenterZ=0 NormalX=0 NormalY=0 NormalZ=1 AngleXU=0 Radius=1
    g3: BSplineCurve PolesCount=3 KnotsCount=2 Degree=2 IsPeriodic=0
    g4: GeomPoint X=0 Y=0 Z=0
    g5: GeomPoint X=8 Y=6 Z=0
    g6: LineSegment StartX=0 StartY=6 StartZ=0 EndX=8 EndY=6 EndZ=0
  constraints (14):
    c: Coincident(g0,g-1)
    c: Distance(g0) = 6
    c: Vertical(g0)
    c: Coincident(g3,g0)
    c: Weight(g1) = 1
    c: Equal(g1,g2)
    c: InternalAlignment(g1,g3)
    c: InternalAlignment(g2,g3)
    c: InternalAlignment(g4,g3)
    c: InternalAlignment(g5,g3)
    c: Block(g3)
    c: Coincident(g6,g0)
    c: Coincident(g6,g3)
    c: Horizontal(g6)
FEATURE [Part::Extrusion] Extrude015  label="caseScrewPillarBracket003"
  Base = -> Sketch021
  Dir = (0,0,1)
  DirMode = 2
  FaceMakerClass = Part::FaceMakerBullseye
  LengthFwd = 2.4
  LengthRev = 0
  Placement = pos=(11.3,29,58.74) rot=(0,1,0;1.5708rad)
  Solid = true
  Symmetric = false
FEATURE [Sketcher::SketchObject] Sketch022
  FullyConstrained = true
  sketch-geometry (7):
    g0: LineSegment StartX=0 StartY=0 StartZ=0 EndX=0 EndY=6 EndZ=0
    g1: Circle CenterX=0 CenterY=0 CenterZ=0 NormalX=0 NormalY=0 NormalZ=1 AngleXU=0 Radius=1
    g2: Circle CenterX=8 CenterY=6 CenterZ=0 NormalX=0 NormalY=0 NormalZ=1 AngleXU=0 Radius=1
    g3: BSplineCurve PolesCount=3 KnotsCount=2 Degree=2 IsPeriodic=0
    g4: GeomPoint X=0 Y=0 Z=0
    g5: GeomPoint X=8 Y=6 Z=0
    g6: LineSegment StartX=0 StartY=6 StartZ=0 EndX=8 EndY=6 EndZ=0
  constraints (14):
    c: Coincident(g0,g-1)
    c: Distance(g0) = 6
    c: Vertical(g0)
    c: Coincident(g3,g0)
    c: Weight(g1) = 1
    c: Equal(g1,g2)
    c: InternalAlignment(g1,g3)
    c: InternalAlignment(g2,g3)
    c: InternalAlignment(g4,g3)
    c: InternalAlignment(g5,g3)
    c: Block(g3)
    c: Coincident(g6,g0)
    c: Coincident(g6,g3)
    c: Horizontal(g6)
FEATURE [Part::Extrusion] Extrude016  label="caseScrewPillarBracket004"
  Base = -> Sketch022
  Dir = (0,0,1)
  DirMode = 2
  FaceMakerClass = Part::FaceMakerBullseye
  LengthFwd = 2.4
  LengthRev = 0
  Placement = pos=(88.3,29,65.23) rot=(0,1,0;1.5708rad)
  Solid = true
  Symmetric = false
FEATURE [Sketcher::SketchObject] Sketch023
  FullyConstrained = true
  sketch-geometry (7):
    g0: LineSegment StartX=0 StartY=0 StartZ=0 EndX=0 EndY=6 EndZ=0
    g1: Circle CenterX=0 CenterY=0 CenterZ=0 NormalX=0 NormalY=0 NormalZ=1 AngleXU=0 Radius=1
    g2: Circle CenterX=8 CenterY=6 CenterZ=0 NormalX=0 NormalY=0 NormalZ=1 AngleXU=0 Radius=1
    g3: BSplineCurve PolesCount=3 KnotsCount=2 Degree=2 IsPeriodic=0
    g4: GeomPoint X=0 Y=0 Z=0
    g5: GeomPoint X=8 Y=6 Z=0
    g6: LineSegment StartX=0 StartY=6 StartZ=0 EndX=8 EndY=6 EndZ=0
  constraints (14):
    c: Coincident(g0,g-1)
    c: Distance(g0) = 6
    c: Vertical(g0)
    c: Coincident(g3,g0)
    c: Weight(g1) = 1
    c: Equal(g1,g2)
    c: InternalAlignment(g1,g3)
    c: InternalAlignment(g2,g3)
    c: InternalAlignment(g4,g3)
    c: InternalAlignment(g5,g3)
    c: Block(g3)
    c: Coincident(g6,g0)
    c: Coincident(g6,g3)
    c: Horizontal(g6)
FEATURE [Part::Extrusion] Extrude017  label="caseScrewPillarBracket005"
  Base = -> Sketch023
  Dir = (0,0,1)
  DirMode = 2
  FaceMakerClass = Part::FaceMakerBullseye
  LengthFwd = 2.4
  LengthRev = 0
  Placement = pos=(90.7,29,6.77) rot=(0,-1,0;1.5708rad)
  Solid = true
  Symmetric = false
FEATURE [Sketcher::SketchObject] Sketch024
  FullyConstrained = true
  sketch-geometry (7):
    g0: LineSegment StartX=0 StartY=0 StartZ=0 EndX=0 EndY=6 EndZ=0
    g1: Circle CenterX=0 CenterY=0 CenterZ=0 NormalX=0 NormalY=0 NormalZ=1 AngleXU=0 Radius=1
    g2: Circle CenterX=8 CenterY=6 CenterZ=0 NormalX=0 NormalY=0 NormalZ=1 AngleXU=0 Radius=1
    g3: BSplineCurve PolesCount=3 KnotsCount=2 Degree=2 IsPeriodic=0
    g4: GeomPoint X=0 Y=0 Z=0
    g5: GeomPoint X=8 Y=6 Z=0
    g6: LineSegment StartX=0 StartY=6 StartZ=0 EndX=8 EndY=6 EndZ=0
  constraints (14):
    c: Coincident(g0,g-1)
    c: Distance(g0) = 6
    c: Vertical(g0)
    c: Coincident(g3,g0)
    c: Weight(g1) = 1
    c: Equal(g1,g2)
    c: InternalAlignment(g1,g3)
    c: InternalAlignment(g2,g3)
    c: InternalAlignment(g4,g3)
    c: InternalAlignment(g5,g3)
    c: Block(g3)
    c: Coincident(g6,g0)
    c: Coincident(g6,g3)
    c: Horizontal(g6)
FEATURE [Part::Extrusion] Extrude018  label="caseScrewPillarBracket006"
  Base = -> Sketch024
  Dir = (0,0,1)
  DirMode = 2
  FaceMakerClass = Part::FaceMakerBullseye
  LengthFwd = 2.4
  LengthRev = 0
  Placement = pos=(103.7,29,6.77) rot=(0,-1,0;1.5708rad)
  Solid = true
  Symmetric = false
FEATURE [Sketcher::SketchObject] Sketch025
  FullyConstrained = true
  sketch-geometry (7):
    g0: LineSegment StartX=0 StartY=0 StartZ=0 EndX=0 EndY=6 EndZ=0
    g1: Circle CenterX=0 CenterY=0 CenterZ=0 NormalX=0 NormalY=0 NormalZ=1 AngleXU=0 Radius=1
    g2: Circle CenterX=8 CenterY=6 CenterZ=0 NormalX=0 NormalY=0 NormalZ=1 AngleXU=0 Radius=1
    g3: BSplineCurve PolesCount=3 KnotsCount=2 Degree=2 IsPeriodic=0
    g4: GeomPoint X=0 Y=0 Z=0
    g5: GeomPoint X=8 Y=6 Z=0
    g6: LineSegment StartX=0 StartY=6 StartZ=0 EndX=8 EndY=6 EndZ=0
  constraints (14):
    c: Coincident(g0,g-1)
    c: Distance(g0) = 6
    c: Vertical(g0)
    c: Coincident(g3,g0)
    c: Weight(g1) = 1
    c: Equal(g1,g2)
    c: InternalAlignment(g1,g3)
    c: InternalAlignment(g2,g3)
    c: InternalAlignment(g4,g3)
    c: InternalAlignment(g5,g3)
    c: Block(g3)
    c: Coincident(g6,g0)
    c: Coincident(g6,g3)
    c: Horizontal(g6)
FEATURE [Part::Extrusion] Extrude019  label="caseScrewPillarBracket007"
  Base = -> Sketch025
  Dir = (0,0,1)
  DirMode = 2
  FaceMakerClass = Part::FaceMakerBullseye
  LengthFwd = 2.4
  LengthRev = 0
  Placement = pos=(101.3,29,65.23) rot=(0,1,0;1.5708rad)
  Solid = true
  Symmetric = false
FEATURE [Part::Box] Box011  label="frontCaseScrewPillarBracket"
  AttacherType = Attacher::AttachEngine3D
  Height = 2.4
  Length = 16
  Placement = pos=(87,28,2.3) rot=(0,0,1;0rad)
  Width = 7
FEATURE [Part::Box] Box012  label="frontCaseScrewPillarBracket001"
  AttacherType = Attacher::AttachEngine3D
  Height = 2.4
  Length = 16
  Placement = pos=(87,28,67.3) rot=(0,0,1;0rad)
  Width = 7
FEATURE [Sketcher::SketchObject] Sketch026
  FullyConstrained = true
  sketch-geometry (17):
    g0: Circle CenterX=-3.5 CenterY=23.5 CenterZ=0 NormalX=0 NormalY=0 NormalZ=1 AngleXU=0 Radius=1
    g1: Circle CenterX=-1 CenterY=15.25 CenterZ=0 NormalX=0 NormalY=0 NormalZ=1 AngleXU=0 Radius=1
    g2: Circle CenterX=-3.5 CenterY=7 CenterZ=0 NormalX=0 NormalY=0 NormalZ=1 AngleXU=0 Radius=1
    g3: BSplineCurve PolesCount=3 KnotsCount=2 Degree=2 IsPeriodic=0
    g4: GeomPoint X=-3.5 Y=23.5 Z=0
    g5: GeomPoint X=-3.5 Y=7 Z=0
    g6: Circle CenterX=-4.8 CenterY=30.5 CenterZ=0 NormalX=0 NormalY=0 NormalZ=1 AngleXU=0 Radius=1
    g7: Circle CenterX=-3.5 CenterY=30.5 CenterZ=0 NormalX=0 NormalY=0 NormalZ=1 AngleXU=0 Radius=1
    g8: Circle CenterX=-3.5 CenterY=29.2 CenterZ=0 NormalX=0 NormalY=0 NormalZ=1 AngleXU=0 Radius=1
    g9: BSplineCurve PolesCount=3 KnotsCount=2 Degree=2 IsPeriodic=0
    g10: GeomPoint X=-4.8 Y=30.5 Z=0
    g11: GeomPoint X=-3.5 Y=29.2 Z=0
    g12: LineSegment StartX=-3.5 StartY=29.2 StartZ=0 EndX=-3.5 EndY=23.5 EndZ=0
    g13: LineSegment StartX=-4.8 StartY=30.5 StartZ=0 EndX=0 EndY=30.5 EndZ=0
    g14: LineSegment StartX=-3.5 StartY=5 StartZ=0 EndX=-3.5 EndY=7 EndZ=0
    g15: LineSegment StartX=0 StartY=5 StartZ=0 EndX=0 EndY=30.5 EndZ=0
    g16: LineSegment StartX=-3.5 StartY=5 StartZ=0 EndX=0 EndY=5 EndZ=0
  constraints (33):
    c: Weight(g0) = 1
    c: Equal(g0,g1)
    c: Equal(g0,g2)
    c: InternalAlignment(g0,g3)
    c: InternalAlignment(g1,g3)
    c: InternalAlignment(g2,g3)
    c: InternalAlignment(g4,g3)
    c: InternalAlignment(g5,g3)
    c: Block(g3)
    c: Weight(g6) = 1
    c: Equal(g6,g7)
    c: Equal(g6,g8)
    c: InternalAlignment(g6,g9)
    c: InternalAlignment(g7,g9)
    c: InternalAlignment(g8,g9)
    c: InternalAlignment(g10,g9)
    c: InternalAlignment(g11,g9)
    c: Block(g9)
    c: Coincident(g12,g9)
    c: Coincident(g12,g3)
    c: Vertical(g12)
    c: Coincident(g13,g9)
    c: Horizontal(g13)
    c: Distance(g13) = 4.8
    c: Coincident(g14,g3)
    c: Vertical(g14)
    c: Coincident(g15,g13)
    c: Vertical(g15)
    c: Tangent(g15,g1)
    c: Distance(g14) = 2
    c: Coincident(g16,g14)
    c: Horizontal(g16)
    c: Coincident(g15,g16)
FEATURE [Part::Feature] Face050
  shape: bbox 4.8 x 25.5 x 2e-07 mm, 1 faces, 0 solids (baked)
FEATURE [Part::Revolution] Revolve054  label="moreFrontCaseScrewPost001"
  Angle = 360
  Axis = (0,1,0)
  Base = (0,0,0)
  FaceMakerClass = Part::FaceMakerBullseye
  Placement = pos=(102.5,4.5,3.5) rot=(0,0,1;0rad)
  Solid = false
  Source = -> Face050
  Symmetric = false
FEATURE [Part::Feature] Face051
  shape: bbox 4.8 x 25.5 x 2e-07 mm, 1 faces, 0 solids (baked)
FEATURE [Part::Revolution] Revolve055  label="moreFrontCaseScrewPost002"
  Angle = 360
  Axis = (0,1,0)
  Base = (0,0,0)
  FaceMakerClass = Part::FaceMakerBullseye
  Placement = pos=(102.5,4.5,68.5) rot=(0,0,1;0rad)
  Solid = false
  Source = -> Face051
  Symmetric = false
FEATURE [Sketcher::SketchObject] Sketch027
  FullyConstrained = true
  sketch-geometry (10):
    g0: LineSegment StartX=-1.6 StartY=4.7 StartZ=0 EndX=-1.6 EndY=1.7 EndZ=0
    g1: LineSegment StartX=-3.5 StartY=4.7 StartZ=0 EndX=-1.6 EndY=4.7 EndZ=0
    g2: LineSegment StartX=-1.6 StartY=1.7 StartZ=0 EndX=-1.6 EndY=1.5 EndZ=0
    g3: LineSegment StartX=-1.6 StartY=1.5 StartZ=0 EndX=-5.2 EndY=1.5 EndZ=0
    g4: Circle CenterX=-3.5 CenterY=4.7 CenterZ=0 NormalX=0 NormalY=0 NormalZ=1 AngleXU=0 Radius=1
    g5: Circle CenterX=-3.59627 CenterY=2.99743 CenterZ=0 NormalX=0 NormalY=0 NormalZ=1 AngleXU=0 Radius=1
    g6: Circle CenterX=-5.2 CenterY=1.5 CenterZ=0 NormalX=0 NormalY=0 NormalZ=1 AngleXU=0 Radius=1
    g7: BSplineCurve PolesCount=3 KnotsCount=2 Degree=2 IsPeriodic=0
    g8: GeomPoint X=-3.5 Y=4.7 Z=0
    g9: GeomPoint X=-5.2 Y=1.5 Z=0
  constraints (23):
    c: Vertical(g0)
    c: Distance(g0) = 3
    c: Coincident(g1,g0)
    c: Horizontal(g1)
    c: Block(g0)
    c: Block(g1)
    c: Coincident(g2,g0)
    c: Vertical(g2)
    c: Distance(g2) = 0.2
    c: Coincident(g3,g2)
    c: Horizontal(g3)
    c: Block(g3)
    c: Coincident(g7,g1)
    c: Weight(g4) = 1
    c: Equal(g4,g5)
    c: Equal(g4,g6)
    c: Coincident(g7,g3)
    c: InternalAlignment(g4,g7)
    c: InternalAlignment(g5,g7)
    c: InternalAlignment(g6,g7)
    c: InternalAlignment(g8,g7)
    c: InternalAlignment(g9,g7)
    c: Block(g7)
FEATURE [Sketcher::SketchObject] Sketch028
  FullyConstrained = true
  sketch-geometry (18):
    g0: LineSegment StartX=0 StartY=3e-16 StartZ=0 EndX=0 EndY=1.7 EndZ=0
    g1: LineSegment StartX=-3.5 StartY=0 StartZ=0 EndX=-3.5 EndY=0.9 EndZ=0
    g2: Circle CenterX=-2.7 CenterY=1.7 CenterZ=0 NormalX=0 NormalY=0 NormalZ=1 AngleXU=0 Radius=1
    g3: Circle CenterX=-3.5 CenterY=1.7 CenterZ=0 NormalX=0 NormalY=0 NormalZ=1 AngleXU=0 Radius=1
    g4: Circle CenterX=-3.5 CenterY=0.9 CenterZ=0 NormalX=0 NormalY=0 NormalZ=1 AngleXU=0 Radius=1
    g5: BSplineCurve PolesCount=3 KnotsCount=2 Degree=2 IsPeriodic=0
    g6: GeomPoint X=-2.7 Y=1.7 Z=0
    g7: GeomPoint X=-3.5 Y=0.9 Z=0
    g8: LineSegment StartX=-3.5 StartY=0 StartZ=0 EndX=-3.5 EndY=-7 EndZ=0
    g9: LineSegment StartX=0 StartY=3e-16 StartZ=0 EndX=0 EndY=-7 EndZ=0
    g10: LineSegment StartX=-3.5 StartY=-7 StartZ=0 EndX=0 EndY=-7 EndZ=0
    g11: LineSegment StartX=-2.7 StartY=1.7 StartZ=0 EndX=-1.6 EndY=1.7 EndZ=0
    g12: LineSegment StartX=0 StartY=1.7 StartZ=0 EndX=0 EndY=4.5 EndZ=0
    g13: LineSegment StartX=0 StartY=4.5 StartZ=0 EndX=0 EndY=10.8 EndZ=0
    g14: LineSegment StartX=0 StartY=10.8 StartZ=0 EndX=-2 EndY=10.8 EndZ=0
    g15: LineSegment StartX=-1.6 StartY=4.7 StartZ=0 EndX=-1.6 EndY=1.7 EndZ=0
    g16: LineSegment StartX=-1.6 StartY=4.7 StartZ=0 EndX=-2 EndY=4.7 EndZ=0
    g17: LineSegment StartX=-2 StartY=4.7 StartZ=0 EndX=-2 EndY=10.8 EndZ=0
  constraints (44):
    c: Vertical(g0)
    c: Vertical(g1)
    c: Distance(g1) = 0.9
    c: Block(g0)
    c: Distance(g0) = 1.7
    c: Weight(g2) = 1
    c: Equal(g2,g3)
    c: Equal(g2,g4)
    c: Coincident(g5,g1)
    c: InternalAlignment(g2,g5)
    c: InternalAlignment(g3,g5)
    c: InternalAlignment(g4,g5)
    c: InternalAlignment(g6,g5)
    c: InternalAlignment(g7,g5)
    c: Block(g5)
    c: Coincident(g8,g1)
    c: Vertical(g8)
    c: Distance(g8) = 7
    c: Vertical(g9)
    c: Equal(g8,g9) = 7
    c: Coincident(g9,g0)
    c: Coincident(g10,g8)
    c: Coincident(g10,g9)
    c: Horizontal(g10)
    c: Coincident(g11,g5)
    c: Horizontal(g11)
    c: Coincident(g12,g0)
    c: Vertical(g12)
    c: Distance(g12) = 2.8
    c: Coincident(g13,g12)
    c: Vertical(g13)
    c: Distance(g13) = 6.3
    c: Coincident(g14,g13)
    c: Horizontal(g14)
    c: Distance(g14) = 2
    c: Vertical(g15)
    c: Distance(g15) = 3
    c: Block(g11)
    c: Coincident(g15,g11)
    c: Coincident(g16,g15)
    c: Horizontal(g16)
    c: Coincident(g17,g16)
    c: Coincident(g17,g14)
    c: Vertical(g17)
FEATURE [Part::Revolution] Revolve040  label="backCaseScrewRetainer001"
  Angle = 360
  Axis = (0,1,0)
  Base = (0,0,0)
  FaceMakerClass = Part::FaceMakerBullseye
  Placement = pos=(12.5,3,10) rot=(0,0,1;0rad)
  Solid = false
  Source = -> Face036
  Symmetric = false
FEATURE [Part::Feature] Face055
  shape: bbox 3.5 x 30.2 x 2e-07 mm, 1 faces, 0 solids (baked)
FEATURE [Part::Revolution] Revolve059  label="backCaseScrewPost"
  Angle = 360
  Axis = (0,1,0)
  Base = (0,0,0)
  FaceMakerClass = Part::FaceMakerBullseye
  Placement = pos=(12.5,4.5,10) rot=(0,0,1;0rad)
  Solid = false
  Source = -> Face055
  Symmetric = false
FEATURE [Part::Feature] Face056
  shape: bbox 3.5 x 30.2 x 2e-07 mm, 1 faces, 0 solids (baked)
FEATURE [Part::Revolution] Revolve060  label="backCaseScrewPost001"
  Angle = 360
  Axis = (0,1,0)
  Base = (0,0,0)
  FaceMakerClass = Part::FaceMakerBullseye
  Placement = pos=(12.5,4.5,62) rot=(0,0,1;0rad)
  Solid = false
  Source = -> Face056
  Symmetric = false
FEATURE [Part::Feature] Face057
  shape: bbox 3.5 x 17.8 x 2e-07 mm, 1 faces, 0 solids (baked)
FEATURE [Part::Revolution] Revolve061  label="removeToCreateScrewAndThreadedInsertHole"
  Angle = 360
  Axis = (0,1,0)
  Base = (0,0,0)
  FaceMakerClass = Part::FaceMakerBullseye
  Placement = pos=(12.5,0,10) rot=(0,0,1;0rad)
  Solid = false
  Source = -> Face057
  Symmetric = false
FEATURE [Part::Feature] Face058
  shape: bbox 3.5 x 17.8 x 2e-07 mm, 1 faces, 0 solids (baked)
FEATURE [Part::Revolution] Revolve062  label="removeToCreateScrewAndThreadedInsertHole001"
  Angle = 360
  Axis = (0,1,0)
  Base = (0,0,0)
  FaceMakerClass = Part::FaceMakerBullseye
  Placement = pos=(12.5,0,62) rot=(0,0,1;0rad)
  Solid = false
  Source = -> Face058
  Symmetric = false
FEATURE [Part::Feature] Face059
  shape: bbox 3.5 x 17.8 x 2e-07 mm, 1 faces, 0 solids (baked)
FEATURE [Part::Revolution] Revolve063  label="removeToCreateScrewAndThreadedInsertHole002"
  Angle = 360
  Axis = (0,1,0)
  Base = (0,0,0)
  FaceMakerClass = Part::FaceMakerBullseye
  Placement = pos=(89.5,0,68.5) rot=(0,0,1;0rad)
  Solid = false
  Source = -> Face059
  Symmetric = false
FEATURE [Part::Feature] Face060
  shape: bbox 3.5 x 17.8 x 2e-07 mm, 1 faces, 0 solids (baked)
FEATURE [Part::Revolution] Revolve064  label="removeToCreateScrewAndThreadedInsertHole003"
  Angle = 360
  Axis = (0,1,0)
  Base = (0,0,0)
  FaceMakerClass = Part::FaceMakerBullseye
  Placement = pos=(89.5,0,3.5) rot=(0,0,1;0rad)
  Solid = false
  Source = -> Face060
  Symmetric = false
FEATURE [Part::Feature] Face061
  shape: bbox 3.5 x 17.8 x 2e-07 mm, 1 faces, 0 solids (baked)
FEATURE [Part::Revolution] Revolve065  label="removeToCreateScrewAndThreadedInsertHole004"
  Angle = 360
  Axis = (0,1,0)
  Base = (0,0,0)
  FaceMakerClass = Part::FaceMakerBullseye
  Placement = pos=(102.5,4.7,3.5) rot=(0,0,1;0rad)
  Solid = false
  Source = -> Face061
  Symmetric = false
FEATURE [Part::Feature] Face062
  shape: bbox 3.5 x 17.8 x 2e-07 mm, 1 faces, 0 solids (baked)
FEATURE [Part::Revolution] Revolve066  label="removeToCreateScrewAndThreadedInsertHole005"
  Angle = 360
  Axis = (0,1,0)
  Base = (0,0,0)
  FaceMakerClass = Part::FaceMakerBullseye
  Placement = pos=(102.5,4.7,68.5) rot=(0,0,1;0rad)
  Solid = false
  Source = -> Face062
  Symmetric = false
FEATURE [Part::MultiFuse] Fusion047  label="makeHoles"
  Shapes = -> [Revolve066,Revolve065,Revolve064,Revolve063,Revolve062,Revolve061]
FEATURE [Part::Feature] Face063
  shape: bbox 3.6 x 3.2 x 2e-07 mm, 1 faces, 0 solids (baked)
FEATURE [Part::Revolution] Revolve067  label="moreFrontCaseScrewRetainer002"
  Angle = 360
  Axis = (0,1,0)
  Base = (0,0,0)
  FaceMakerClass = Part::FaceMakerBullseye
  Placement = pos=(102.5,4.5,68.5) rot=(0,0,1;0rad)
  Solid = false
  Source = -> Face063
  Symmetric = false
FEATURE [Part::Feature] Face064
  shape: bbox 3.6 x 3.2 x 2e-07 mm, 1 faces, 0 solids (baked)
FEATURE [Part::Revolution] Revolve068  label="moreFrontCaseScrewRetainer003"
  Angle = 360
  Axis = (0,1,0)
  Base = (0,0,0)
  FaceMakerClass = Part::FaceMakerBullseye
  Placement = pos=(102.5,4.5,3.5) rot=(0,0,1;0rad)
  Solid = false
  Source = -> Face064
  Symmetric = false
FEATURE [Part::Feature] Face065
  shape: bbox 3.5 x 17.8 x 2e-07 mm, 1 faces, 0 solids (baked)
FEATURE [Part::Revolution] Revolve069  label="removeToCreateScrewAndThreadedInsertHole006"
  Angle = 360
  Axis = (0,1,0)
  Base = (0,0,0)
  FaceMakerClass = Part::FaceMakerBullseye
  Placement = pos=(12.5,0,10) rot=(0,0,1;0rad)
  Solid = false
  Source = -> Face065
  Symmetric = false
FEATURE [Part::Feature] Face066
  shape: bbox 3.5 x 17.8 x 2e-07 mm, 1 faces, 0 solids (baked)
FEATURE [Part::Revolution] Revolve070  label="removeToCreateScrewAndThreadedInsertHole007"
  Angle = 360
  Axis = (0,1,0)
  Base = (0,0,0)
  FaceMakerClass = Part::FaceMakerBullseye
  Placement = pos=(12.5,0,62) rot=(0,0,1;0rad)
  Solid = false
  Source = -> Face066
  Symmetric = false
FEATURE [Part::Feature] Face067
  shape: bbox 3.5 x 17.8 x 2e-07 mm, 1 faces, 0 solids (baked)
FEATURE [Part::Revolution] Revolve071  label="removeToCreateScrewAndThreadedInsertHole008"
  Angle = 360
  Axis = (0,1,0)
  Base = (0,0,0)
  FaceMakerClass = Part::FaceMakerBullseye
  Placement = pos=(89.5,0,68.5) rot=(0,0,1;0rad)
  Solid = false
  Source = -> Face067
  Symmetric = false
FEATURE [Part::Feature] Face068
  shape: bbox 3.5 x 17.8 x 2e-07 mm, 1 faces, 0 solids (baked)
FEATURE [Part::Revolution] Revolve072  label="removeToCreateScrewAndThreadedInsertHole009"
  Angle = 360
  Axis = (0,1,0)
  Base = (0,0,0)
  FaceMakerClass = Part::FaceMakerBullseye
  Placement = pos=(89.5,0,3.5) rot=(0,0,1;0rad)
  Solid = false
  Source = -> Face068
  Symmetric = false
FEATURE [Part::Feature] Face069
  shape: bbox 3.5 x 17.8 x 2e-07 mm, 1 faces, 0 solids (baked)
FEATURE [Part::Feature] Face070
  shape: bbox 3.5 x 17.8 x 2e-07 mm, 1 faces, 0 solids (baked)
FEATURE [Part::Revolution] Revolve073  label="removeToCreateScrewAndThreadedInsertHole010"
  Angle = 360
  Axis = (0,1,0)
  Base = (0,0,0)
  FaceMakerClass = Part::FaceMakerBullseye
  Placement = pos=(102.5,4.7,3.5) rot=(0,0,1;0rad)
  Solid = false
  Source = -> Face069
  Symmetric = false
FEATURE [Part::Revolution] Revolve074  label="removeToCreateScrewAndThreadedInsertHole011"
  Angle = 360
  Axis = (0,1,0)
  Base = (0,0,0)
  FaceMakerClass = Part::FaceMakerBullseye
  Placement = pos=(102.5,4.7,68.5) rot=(0,0,1;0rad)
  Solid = false
  Source = -> Face070
  Symmetric = false
FEATURE [Part::MultiFuse] Fusion048  label="makeHoles001"
  Shapes = -> [Revolve074,Revolve073,Revolve072,Revolve071,Revolve070,Revolve069]
FEATURE [Part::MultiFuse] Fusion049  label="caseScrewRetainers"
  Shapes = -> [Revolve067,Revolve068,Revolve048,Revolve047,Revolve039,Revolve040]
FEATURE [Part::Cut] Cut015  label="caseScrewRetainers001"
  Base = -> Fusion049
  Tool = -> Fusion048
FEATURE [Part::MultiFuse] Fusion050  label="casePillars"
  Shapes = -> [Revolve055,Revolve054,Revolve043,Revolve046,Revolve059,Revolve060]
FEATURE [Part::Feature] Face071 .. Face076  x6 (patterned run collapsed; names and placements below)
  shape: bbox 3.5 x 17.8 x 2e-07 mm, 1 faces, 0 solids (baked)
FEATURE [Part::Revolution] Revolve075  label="removeToCreateScrewAndThreadedInsertHole012"
  Angle = 360
  Axis = (0,1,0)
  Base = (0,0,0)
  FaceMakerClass = Part::FaceMakerBullseye
  Placement = pos=(12.5,0,10) rot=(0,0,1;0rad)
  Solid = false
  Source = -> Face071
  Symmetric = false
FEATURE [Part::Revolution] Revolve076  label="removeToCreateScrewAndThreadedInsertHole013"
  Angle = 360
  Axis = (0,1,0)
  Base = (0,0,0)
  FaceMakerClass = Part::FaceMakerBullseye
  Placement = pos=(12.5,0,62) rot=(0,0,1;0rad)
  Solid = false
  Source = -> Face072
  Symmetric = false
FEATURE [Part::Revolution] Revolve077  label="removeToCreateScrewAndThreadedInsertHole014"
  Angle = 360
  Axis = (0,1,0)
  Base = (0,0,0)
  FaceMakerClass = Part::FaceMakerBullseye
  Placement = pos=(89.5,0,68.5) rot=(0,0,1;0rad)
  Solid = false
  Source = -> Face073
  Symmetric = false
FEATURE [Part::Revolution] Revolve078  label="removeToCreateScrewAndThreadedInsertHole015"
  Angle = 360
  Axis = (0,1,0)
  Base = (0,0,0)
  FaceMakerClass = Part::FaceMakerBullseye
  Placement = pos=(89.5,0,3.5) rot=(0,0,1;0rad)
  Solid = false
  Source = -> Face074
  Symmetric = false
FEATURE [Part::Revolution] Revolve079  label="removeToCreateScrewAndThreadedInsertHole016"
  Angle = 360
  Axis = (0,1,0)
  Base = (0,0,0)
  FaceMakerClass = Part::FaceMakerBullseye
  Placement = pos=(102.5,4.7,3.5) rot=(0,0,1;0rad)
  Solid = false
  Source = -> Face075
  Symmetric = false
FEATURE [Part::Revolution] Revolve080  label="removeToCreateScrewAndThreadedInsertHole017"
  Angle = 360
  Axis = (0,1,0)
  Base = (0,0,0)
  FaceMakerClass = Part::FaceMakerBullseye
  Placement = pos=(102.5,4.7,68.5) rot=(0,0,1;0rad)
  Solid = false
  Source = -> Face076
  Symmetric = false
FEATURE [Part::MultiFuse] Fusion051  label="makeHoles002"
  Shapes = -> [Revolve080,Revolve079,Revolve078,Revolve077,Revolve076,Revolve075]
FEATURE [Part::Cut] Cut016  label="caesPillars"
  Base = -> Fusion050
  Tool = -> Fusion051
FEATURE [Part::Revolution] Revolve009  label="plugHousing016"
  Angle = 360
  Axis = (0,1,0)
  Base = (0,0,0)
  FaceMakerClass = Part::FaceMakerBullseye
  Placement = pos=(0,0,36.15) rot=(0,0,1;0rad)
  Solid = false
  Source = -> Face012
  Symmetric = false
FEATURE [Part::MultiFuse] Fusion014  label="plugHousing023"
  Placement = pos=(0,0,0) rot=(0,0,1;1.5708rad)
  Shapes = -> [Revolve011,Revolve009]
FEATURE [Part::Revolution] Revolve010  label="plugHousing017"
  Angle = 360
  Axis = (0,1,0)
  Base = (0,0,0)
  FaceMakerClass = Part::FaceMakerBullseye
  Placement = pos=(0,0,36.15) rot=(0,0,1;0rad)
  Solid = false
  Source = -> Face014
  Symmetric = false
FEATURE [Part::MultiFuse] Fusion015  label="plugHousing024"
  Placement = pos=(0,0,0) rot=(0,0,1;1.5708rad)
  Shapes = -> [Revolve010,Revolve015]
FEATURE [Part::Revolution] Revolve014  label="plugHousing026"
  Angle = 360
  Axis = (0,1,0)
  Base = (0,0,0)
  FaceMakerClass = Part::FaceMakerBullseye
  Placement = pos=(0,0,36.15) rot=(0,0,1;0rad)
  Solid = false
  Source = -> Face011
  Symmetric = false
FEATURE [Part::Revolution] Revolve013  label="plugHousing025"
  Angle = 360
  Axis = (0,1,0)
  Base = (0,0,0)
  FaceMakerClass = Part::FaceMakerBullseye
  Placement = pos=(0,0,36.15) rot=(0,0,1;0rad)
  Solid = false
  Source = -> Face015
  Symmetric = false
FEATURE [Part::MultiFuse] Fusion016  label="plugHousing028"
  Placement = pos=(0,19,0) rot=(0,0,1;3.14159rad)
  Shapes = -> [Fusion014,Fusion013]
FEATURE [Part::MultiFuse] Fusion011  label="plugHousing018"
  Placement = pos=(0,0,0) rot=(0,0,1;1.5708rad)
  Shapes = -> [Revolve014,Revolve013]
FEATURE [Part::MultiFuse] Fusion012  label="plugHousing019"
  Placement = pos=(0,19,0) rot=(0,0,1;3.14159rad)
  Shapes = -> [Fusion011,Fusion015]
FEATURE [Part::MultiFuse] Fusion017  label="plugHousing029"
  Placement = pos=(122.621,0,-0.15) rot=(0,0,1;0rad)
  Shapes = -> [Fusion016,Fusion012]
FEATURE [Part::MultiFuse] Fusion052  label="casePillarRetainers"
  Shapes = -> [Extrude012,Extrude013,Extrude014,Extrude015,Extrude016,Extrude017,Extrude018,Extrude019,Box011,Box012]
FEATURE [Part::Feature] Face077
  shape: bbox 3.5 x 17.8 x 2e-07 mm, 1 faces, 0 solids (baked)
FEATURE [Part::Revolution] Revolve081  label="removeToCreateScrewAndThreadedInsertHole018"
  Angle = 360
  Axis = (0,1,0)
  Base = (0,0,0)
  FaceMakerClass = Part::FaceMakerBullseye
  Placement = pos=(62.3,30.3,19.7) rot=(0,0,1;0rad)
  Solid = false
  Source = -> Face077
  Symmetric = false
FEATURE [Part::Feature] Face078
  shape: bbox 3.5 x 17.8 x 2e-07 mm, 1 faces, 0 solids (baked)
FEATURE [Part::Revolution] Revolve082  label="removeToCreateScrewAndThreadedInsertHole019"
  Angle = 360
  Axis = (0,1,0)
  Base = (0,0,0)
  FaceMakerClass = Part::FaceMakerBullseye
  Placement = pos=(62.3,30.3,51.7) rot=(0,0,1;0rad)
  Solid = false
  Source = -> Face078
  Symmetric = false
FEATURE [Part::Feature] Face079
  shape: bbox 3.5 x 17.8 x 2e-07 mm, 1 faces, 0 solids (baked)
FEATURE [Part::Revolution] Revolve083  label="removeToCreateScrewAndThreadedInsertHole020"
  Angle = 360
  Axis = (0,1,0)
  Base = (0,0,0)
  FaceMakerClass = Part::FaceMakerBullseye
  Placement = pos=(30.3,30.3,19.7) rot=(0,0,1;0rad)
  Solid = false
  Source = -> Face079
  Symmetric = false
FEATURE [Part::Feature] Face080
  shape: bbox 3.5 x 17.8 x 2e-07 mm, 1 faces, 0 solids (baked)
FEATURE [Part::Revolution] Revolve084  label="removeToCreateScrewAndThreadedInsertHole021"
  Angle = 360
  Axis = (0,1,0)
  Base = (0,0,0)
  FaceMakerClass = Part::FaceMakerBullseye
  Placement = pos=(30.3,30.3,51.7) rot=(0,0,1;0rad)
  Solid = false
  Source = -> Face080
  Symmetric = false
FEATURE [Part::MultiFuse] Fusion053  label="createThreadedInsertHolesForFan"
  Shapes = -> [Revolve081,Revolve082,Revolve083,Revolve084]
FEATURE [Part::Cut] Cut017  label="fanScrewHousing001"
  Base = -> Fusion046
  Tool = -> Fusion053
FEATURE [Part::Feature] Face081
  shape: bbox 3.5 x 17.8 x 2e-07 mm, 1 faces, 0 solids (baked)
FEATURE [Part::Revolution] Revolve085  label="removeToCreateScrewAndThreadedInsertHole022"
  Angle = 360
  Axis = (0,1,0)
  Base = (0,0,0)
  FaceMakerClass = Part::FaceMakerBullseye
  Placement = pos=(62.3,30.3,19.7) rot=(0,0,1;0rad)
  Solid = false
  Source = -> Face081
  Symmetric = false
FEATURE [Part::Feature] Face082
  shape: bbox 3.5 x 17.8 x 2e-07 mm, 1 faces, 0 solids (baked)
FEATURE [Part::Revolution] Revolve086  label="removeToCreateScrewAndThreadedInsertHole023"
  Angle = 360
  Axis = (0,1,0)
  Base = (0,0,0)
  FaceMakerClass = Part::FaceMakerBullseye
  Placement = pos=(62.3,30.3,51.7) rot=(0,0,1;0rad)
  Solid = false
  Source = -> Face082
  Symmetric = false
FEATURE [Part::Feature] Face083
  shape: bbox 3.5 x 17.8 x 2e-07 mm, 1 faces, 0 solids (baked)
FEATURE [Part::Revolution] Revolve087  label="removeToCreateScrewAndThreadedInsertHole024"
  Angle = 360
  Axis = (0,1,0)
  Base = (0,0,0)
  FaceMakerClass = Part::FaceMakerBullseye
  Placement = pos=(30.3,30.3,19.7) rot=(0,0,1;0rad)
  Solid = false
  Source = -> Face083
  Symmetric = false
FEATURE [Part::Feature] Face084
  shape: bbox 3.5 x 17.8 x 2e-07 mm, 1 faces, 0 solids (baked)
FEATURE [Part::Revolution] Revolve088  label="removeToCreateScrewAndThreadedInsertHole025"
  Angle = 360
  Axis = (0,1,0)
  Base = (0,0,0)
  FaceMakerClass = Part::FaceMakerBullseye
  Placement = pos=(30.3,30.3,51.7) rot=(0,0,1;0rad)
  Solid = false
  Source = -> Face084
  Symmetric = false
FEATURE [Part::MultiFuse] Fusion054  label="createThreadedInsertHolesForFan001"
  Shapes = -> [Revolve085,Revolve086,Revolve087,Revolve088]
FEATURE [Part::Cut] Cut018  label="top007"
  Base = -> Fusion040
  Tool = -> Fusion054
FEATURE [Sketcher::SketchObject] Sketch029
  FullyConstrained = false
  Placement = pos=(0,0,0) rot=(1,0,0;1.5708rad)
  sketch-geometry (24):
    g0: ArcOfCircle CenterX=-4 CenterY=-10.5 CenterZ=0 NormalX=0 NormalY=0 NormalZ=1 AngleXU=0 Radius=1.5 StartAngle=6e-16 EndAngle=3.14159
    g1: ArcOfCircle CenterX=-34.2 CenterY=-10.5 CenterZ=0 NormalX=0 NormalY=0 NormalZ=1 AngleXU=0 Radius=1.5 StartAngle=0 EndAngle=3.14159
    g2: ArcOfCircle CenterX=-34.2 CenterY=-27.7 CenterZ=0 NormalX=0 NormalY=0 NormalZ=1 AngleXU=0 Radius=1.5 StartAngle=3.14159 EndAngle=6.28319
    g3: ArcOfCircle CenterX=-4 CenterY=-27.7 CenterZ=0 NormalX=0 NormalY=0 NormalZ=1 AngleXU=0 Radius=1.5 StartAngle=3.1416 EndAngle=6.28319
    g4: ArcOfCircle CenterX=-10 CenterY=-4.3 CenterZ=0 NormalX=0 NormalY=0 NormalZ=1 AngleXU=0 Radius=1.5 StartAngle=2e-16 EndAngle=3.14159
    g5: ArcOfCircle CenterX=-16.1 CenterY=-1.8 CenterZ=0 NormalX=0 NormalY=0 NormalZ=1 AngleXU=0 Radius=1.5 StartAngle=5e-16 EndAngle=3.14159
    g6: ArcOfCircle CenterX=-22.1 CenterY=-1.8 CenterZ=0 NormalX=0 NormalY=0 NormalZ=1 AngleXU=0 Radius=1.5 StartAngle=5e-16 EndAngle=3.14159
    g7: ArcOfCircle CenterX=-28.2 CenterY=-4.3 CenterZ=0 NormalX=0 NormalY=0 NormalZ=1 AngleXU=0 Radius=1.5 StartAngle=2e-16 EndAngle=3.14159
    g8: ArcOfCircle CenterX=-10 CenterY=-33.9 CenterZ=0 NormalX=0 NormalY=0 NormalZ=1 AngleXU=0 Radius=1.5 StartAngle=3.14159 EndAngle=6.28319
    g9: ArcOfCircle CenterX=-16.1 CenterY=-36.4 CenterZ=0 NormalX=0 NormalY=0 NormalZ=1 AngleXU=0 Radius=1.5 StartAngle=3.14159 EndAngle=6.28319
    g10: ArcOfCircle CenterX=-22.1 CenterY=-36.4 CenterZ=0 NormalX=0 NormalY=0 NormalZ=1 AngleXU=0 Radius=1.5 StartAngle=3.14159 EndAngle=6.28319
    g11: ArcOfCircle CenterX=-28.2 CenterY=-33.9 CenterZ=0 NormalX=0 NormalY=0 NormalZ=1 AngleXU=0 Radius=1.5 StartAngle=3.14159 EndAngle=6.28319
    g12: LineSegment StartX=-35.7 StartY=-10.5 StartZ=0 EndX=-35.7 EndY=-27.7 EndZ=0
    g13: LineSegment StartX=-32.7 StartY=-10.5 StartZ=0 EndX=-32.7 EndY=-27.7 EndZ=0
    g14: LineSegment StartX=-29.7 StartY=-33.9 StartZ=0 EndX=-29.7 EndY=-4.3 EndZ=0
    g15: LineSegment StartX=-26.7 StartY=-33.9 StartZ=0 EndX=-26.7 EndY=-4.3 EndZ=0
    g16: LineSegment StartX=-2.5 StartY=-10.5 StartZ=0 EndX=-2.5 EndY=-27.7 EndZ=0
    g17: LineSegment StartX=-8.5 StartY=-4.3 StartZ=0 EndX=-8.5 EndY=-33.9 EndZ=0
    g18: LineSegment StartX=-5.5 StartY=-10.5 StartZ=0 EndX=-5.5 EndY=-27.7 EndZ=0
    g19: LineSegment StartX=-11.5 StartY=-4.3 StartZ=0 EndX=-11.5 EndY=-33.9 EndZ=0
    g20: LineSegment StartX=-14.6 StartY=-1.8 StartZ=0 EndX=-14.6 EndY=-36.4 EndZ=0
    g21: LineSegment StartX=-17.6 StartY=-1.8 StartZ=0 EndX=-17.6 EndY=-36.4 EndZ=0
    g22: LineSegment StartX=-20.6 StartY=-36.4 StartZ=0 EndX=-20.6 EndY=-1.8 EndZ=0
    g23: LineSegment StartX=-23.6 StartY=-1.8 StartZ=0 EndX=-23.6 EndY=-36.4 EndZ=0
  constraints (48):
    c: Block(g0)
    c: Block(g1)
    c: Block(g2)
    c: Block(g3)
    c: Block(g4)
    c: Block(g5)
    c: Block(g6)
    c: Block(g7)
    c: Block(g8)
    c: Block(g9)
    c: Block(g10)
    c: Block(g11)
    c: Coincident(g12,g1)
    c: Coincident(g12,g2)
    c: Vertical(g12)
    c: Coincident(g13,g1)
    c: Coincident(g13,g2)
    c: Vertical(g13)
    c: Coincident(g14,g11)
    c: Coincident(g14,g7)
    c: Vertical(g14)
    c: Coincident(g15,g11)
    c: Coincident(g15,g7)
    c: Vertical(g15)
    c: Coincident(g16,g0)
    c: Coincident(g16,g3)
    c: Vertical(g16)
    c: Coincident(g17,g4)
    c: Coincident(g17,g8)
    c: Vertical(g17)
    c: Coincident(g18,g0)
    c: Coincident(g18,g3)
    c: Vertical(g18)
    c: Coincident(g19,g4)
    c: Coincident(g19,g8)
    c: Vertical(g19)
    c: Coincident(g20,g5)
    c: Coincident(g20,g9)
    c: Vertical(g20)
    c: Coincident(g21,g5)
    c: Coincident(g21,g9)
    c: Vertical(g21)
    c: Coincident(g22,g10)
    c: Coincident(g22,g6)
    c: Vertical(g22)
    c: Coincident(g23,g6)
    c: Coincident(g23,g10)
    c: Vertical(g23)
FEATURE [Part::Extrusion] Extrude020  label="removeToCreateFanGrillHoles"
  Base = -> Sketch029
  Dir = (0,-1,6e-16)
  DirMode = 2
  FaceMakerClass = Part::FaceMakerBullseye
  LengthFwd = 10
  LengthRev = 0
  Placement = pos=(65.4,44,54.82) rot=(0,0,1;0rad)
  Solid = true
  Symmetric = false
FEATURE [Part::MultiFuse] Fusion055  label="top008"
  Shapes = -> [Cut017,Cut018]
FEATURE [Part::Cut] Cut019  label="top009"
  Base = -> Fusion055
  Tool = -> Extrude020
FEATURE [App::MeasureDistance] Distance003  label="Distance: 71.95 mm"
  Distance = 71.9513
  P1 = (117,38,72)
  P2 = (117,38,0.0487319)
FEATURE [Sketcher::SketchObject] Sketch030
  FullyConstrained = true
  Placement = pos=(117,19,0) rot=(0.57735,0.57735,0.57735;2.0944rad)
  sketch-geometry (48):
    g0: LineSegment StartX=-49.19 StartY=69.25 StartZ=0 EndX=-49.19 EndY=66.25 EndZ=0
    g1: LineSegment StartX=-49.19 StartY=63.5 StartZ=0 EndX=-49.19 EndY=60.5 EndZ=0
    g2: LineSegment StartX=-49.19 StartY=57.75 StartZ=0 EndX=-49.19 EndY=54.75 EndZ=0
    g3: LineSegment StartX=-49.19 StartY=52 StartZ=0 EndX=-49.19 EndY=49 EndZ=0
    g4: LineSegment StartX=-49.19 StartY=46.25 StartZ=0 EndX=-49.19 EndY=43.25 EndZ=0
    g5: LineSegment StartX=-49.19 StartY=40.5 StartZ=0 EndX=-49.19 EndY=37.5 EndZ=0
    g6: LineSegment StartX=-49.19 StartY=34.5 StartZ=0 EndX=-49.19 EndY=31.5 EndZ=0
    g7: LineSegment StartX=-49.19 StartY=28.75 StartZ=0 EndX=-49.19 EndY=25.75 EndZ=0
    g8: LineSegment StartX=-49.19 StartY=23 StartZ=0 EndX=-49.19 EndY=20 EndZ=0
    g9: LineSegment StartX=-49.19 StartY=17.25 StartZ=0 EndX=-49.19 EndY=14.25 EndZ=0
    g10: LineSegment StartX=-49.19 StartY=11.5 StartZ=0 EndX=-49.19 EndY=8.5 EndZ=0
    g11: LineSegment StartX=-49.19 StartY=5.75 StartZ=0 EndX=-49.19 EndY=2.75 EndZ=0
    g12: ArcOfCircle CenterX=-1.5 CenterY=67.75 CenterZ=0 NormalX=0 NormalY=0 NormalZ=1 AngleXU=0 Radius=1.5 StartAngle=4.71239 EndAngle=7.85398
    g13: ArcOfCircle CenterX=-1.5 CenterY=62 CenterZ=0 NormalX=0 NormalY=0 NormalZ=1 AngleXU=0 Radius=1.5 StartAngle=4.71239 EndAngle=7.85398
    g14: ArcOfCircle CenterX=-1.5 CenterY=56.25 CenterZ=0 NormalX=0 NormalY=0 NormalZ=1 AngleXU=0 Radius=1.5 StartAngle=4.71239 EndAngle=7.85398
    g15: ArcOfCircle CenterX=-11.49 CenterY=50.5 CenterZ=0 NormalX=0 NormalY=0 NormalZ=1 AngleXU=0 Radius=1.5 StartAngle=4.71239 EndAngle=7.85398
    g16: ArcOfCircle CenterX=-16.28 CenterY=44.75 CenterZ=0 NormalX=0 NormalY=0 NormalZ=1 AngleXU=0 Radius=1.5 StartAngle=4.71239 EndAngle=7.85398
    g17: ArcOfCircle CenterX=-18.2337 CenterY=39 CenterZ=0 NormalX=0 NormalY=0 NormalZ=1 AngleXU=0 Radius=1.5 StartAngle=4.71485 EndAngle=7.85398
    g18: ArcOfCircle CenterX=-16.2837 CenterY=27.25 CenterZ=0 NormalX=0 NormalY=0 NormalZ=1 AngleXU=0 Radius=1.5 StartAngle=4.71485 EndAngle=7.85398
    g19: ArcOfCircle CenterX=-18.2337 CenterY=33 CenterZ=0 NormalX=0 NormalY=0 NormalZ=1 AngleXU=0 Radius=1.5 StartAngle=4.71485 EndAngle=7.85398
    g20: ArcOfCircle CenterX=-11.49 CenterY=21.5 CenterZ=0 NormalX=0 NormalY=0 NormalZ=1 AngleXU=0 Radius=1.5 StartAngle=4.71239 EndAngle=7.85398
    g21: ArcOfCircle CenterX=-1.5 CenterY=4.25 CenterZ=0 NormalX=0 NormalY=0 NormalZ=1 AngleXU=0 Radius=1.5 StartAngle=4.71239 EndAngle=7.85398
    g22: ArcOfCircle CenterX=-1.5 CenterY=10 CenterZ=0 NormalX=0 NormalY=0 NormalZ=1 AngleXU=0 Radius=1.5 StartAngle=4.71239 EndAngle=7.85398
    g23: ArcOfCircle CenterX=-1.5 CenterY=15.75 CenterZ=0 NormalX=0 NormalY=0 NormalZ=1 AngleXU=0 Radius=1.5 StartAngle=4.71239 EndAngle=7.85398
    g24: LineSegment StartX=-49.19 StartY=69.25 StartZ=0 EndX=-1.5 EndY=69.25 EndZ=0
    g25: LineSegment StartX=-49.19 StartY=66.25 StartZ=0 EndX=-1.5 EndY=66.25 EndZ=0
    g26: LineSegment StartX=-49.19 StartY=63.5 StartZ=0 EndX=-1.5 EndY=63.5 EndZ=0
    g27: LineSegment StartX=-49.19 StartY=60.5 StartZ=0 EndX=-1.5 EndY=60.5 EndZ=0
    g28: LineSegment StartX=-49.19 StartY=57.75 StartZ=0 EndX=-1.5 EndY=57.75 EndZ=0
    g29: LineSegment StartX=-49.19 StartY=54.75 StartZ=0 EndX=-1.5 EndY=54.75 EndZ=0
    g30: LineSegment StartX=-49.19 StartY=52 StartZ=0 EndX=-11.49 EndY=52 EndZ=0
    g31: LineSegment StartX=-49.19 StartY=49 StartZ=0 EndX=-11.49 EndY=49 EndZ=0
    g32: LineSegment StartX=-49.19 StartY=46.25 StartZ=0 EndX=-16.28 EndY=46.25 EndZ=0
    g33: LineSegment StartX=-49.19 StartY=43.25 StartZ=0 EndX=-16.28 EndY=43.25 EndZ=0
    g34: LineSegment StartX=-49.19 StartY=40.5 StartZ=0 EndX=-18.2337 EndY=40.5 EndZ=0
    g35: LineSegment StartX=-49.19 StartY=37.5 StartZ=0 EndX=-18.23 EndY=37.5 EndZ=0
    g36: LineSegment StartX=-49.19 StartY=34.5 StartZ=0 EndX=-18.2337 EndY=34.5 EndZ=0
    g37: LineSegment StartX=-49.19 StartY=31.5 StartZ=0 EndX=-18.23 EndY=31.5 EndZ=0
    g38: LineSegment StartX=-49.19 StartY=28.75 StartZ=0 EndX=-16.2837 EndY=28.75 EndZ=0
    g39: LineSegment StartX=-49.19 StartY=25.75 StartZ=0 EndX=-16.28 EndY=25.75 EndZ=0
    g40: LineSegment StartX=-49.19 StartY=23 StartZ=0 EndX=-11.49 EndY=23 EndZ=0
    g41: LineSegment StartX=-49.19 StartY=20 StartZ=0 EndX=-11.49 EndY=20 EndZ=0
    g42: LineSegment StartX=-49.19 StartY=17.25 StartZ=0 EndX=-1.5 EndY=17.25 EndZ=0
    g43: LineSegment StartX=-49.19 StartY=14.25 StartZ=0 EndX=-1.5 EndY=14.25 EndZ=0
    g44: LineSegment StartX=-49.19 StartY=11.5 StartZ=0 EndX=-1.5 EndY=11.5 EndZ=0
    g45: LineSegment StartX=-49.19 StartY=8.5 StartZ=0 EndX=-1.5 EndY=8.5 EndZ=0
    g46: LineSegment StartX=-49.19 StartY=5.75 StartZ=0 EndX=-1.5 EndY=5.75 EndZ=0
    g47: LineSegment StartX=-49.19 StartY=2.75 StartZ=0 EndX=-1.5 EndY=2.75 EndZ=0
  constraints (120):
    c: Vertical(g0)
    c: Distance(g0) = 3
    c: Block(g0)
    c: Vertical(g1)
    c: Distance(g1) = 3
    c: Vertical(g2)
    c: Equal(g0,g2) = 3
    c: Block(g2)
    c: Vertical(g3)
    c: Equal(g1,g3) = 3
    c: Vertical(g4)
    c: Equal(g0,g4) = 3
    c: Block(g4)
    c: Vertical(g5)
    c: Equal(g1,g5) = 3
    c: Vertical(g6)
    c: Equal(g0,g6) = 3
    c: Block(g6)
    c: Vertical(g7)
    c: Equal(g1,g7) = 3
    c: Vertical(g8)
    c: Equal(g0,g8) = 3
    c: Block(g8)
    c: Vertical(g9)
    c: Equal(g1,g9) = 3
    c: Vertical(g10)
    c: Equal(g0,g10) = 3
    c: Block(g10)
    c: Vertical(g11)
    c: Equal(g1,g11) = 3
    c: Block(g12)
    c: Block(g13)
    c: Block(g14)
    c: Block(g15)
    c: Block(g16)
    c: Block(g17)
    c: Block(g18)
    c: Block(g19)
    c: Block(g20)
    c: Block(g21)
    c: Block(g22)
    c: Block(g23)
    c: Block(g11)
    c: Block(g9)
    c: Block(g7)
    c: Block(g5)
    c: Block(g3)
    c: Block(g1)
    c: Coincident(g24,g0)
    c: Coincident(g24,g12)
    c: Horizontal(g24)
    c: Coincident(g25,g0)
    c: Coincident(g25,g12)
    c: Horizontal(g25)
    c: Coincident(g26,g1)
    c: Coincident(g26,g13)
    c: Horizontal(g26)
    c: Coincident(g27,g1)
    c: Coincident(g27,g13)
    c: Horizontal(g27)
    c: Coincident(g28,g2)
    c: Coincident(g28,g14)
    c: Horizontal(g28)
    c: Coincident(g29,g2)
    c: Coincident(g29,g14)
    c: Horizontal(g29)
    c: Coincident(g30,g3)
    c: Coincident(g30,g15)
    c: Horizontal(g30)
    c: Coincident(g31,g3)
    c: Coincident(g31,g15)
    c: Horizontal(g31)
    c: Coincident(g32,g4)
    c: Coincident(g32,g16)
    c: Horizontal(g32)
    c: Coincident(g33,g4)
    c: Coincident(g33,g16)
    c: Horizontal(g33)
    c: Coincident(g34,g5)
    c: Coincident(g34,g17)
    c: Horizontal(g34)
    c: Coincident(g35,g5)
    c: Coincident(g35,g17)
    c: Horizontal(g35)
    c: Coincident(g36,g6)
    c: Coincident(g36,g19)
    c: Horizontal(g36)
    c: Coincident(g37,g6)
    c: Coincident(g37,g19)
    c: Horizontal(g37)
    c: Coincident(g38,g7)
    c: Coincident(g38,g18)
    c: Horizontal(g38)
    c: Coincident(g39,g7)
    c: Coincident(g39,g18)
    c: Horizontal(g39)
    c: Coincident(g40,g8)
    c: Coincident(g40,g20)
    c: Horizontal(g40)
    c: Coincident(g41,g8)
    c: Coincident(g41,g20)
    c: Horizontal(g41)
    c: Coincident(g42,g9)
    c: Coincident(g42,g23)
    c: Horizontal(g42)
    c: Coincident(g43,g9)
    c: Coincident(g43,g23)
    c: Horizontal(g43)
    c: Coincident(g44,g10)
    c: Coincident(g44,g22)
    c: Horizontal(g44)
    c: Coincident(g45,g10)
    c: Coincident(g45,g22)
    c: Horizontal(g45)
    c: Coincident(g46,g11)
    c: Coincident(g46,g21)
    c: Horizontal(g46)
    c: Coincident(g47,g11)
    c: Coincident(g47,g21)
    c: Horizontal(g47)
FEATURE [Sketcher::SketchObject] Sketch031
  FullyConstrained = true
  Placement = pos=(117,19,0) rot=(0.57735,0.57735,0.57735;2.0944rad)
  sketch-geometry (24):
    g0: ArcOfCircle CenterX=-49.19 CenterY=67.75 CenterZ=0 NormalX=0 NormalY=0 NormalZ=1 AngleXU=0 Radius=1.5 StartAngle=1.5708 EndAngle=4.71239
    g1: ArcOfCircle CenterX=-49.19 CenterY=62 CenterZ=0 NormalX=0 NormalY=0 NormalZ=1 AngleXU=0 Radius=1.5 StartAngle=1.5708 EndAngle=4.71239
    g2: ArcOfCircle CenterX=-49.19 CenterY=56.25 CenterZ=0 NormalX=0 NormalY=0 NormalZ=1 AngleXU=0 Radius=1.5 StartAngle=1.5708 EndAngle=4.71239
    g3: ArcOfCircle CenterX=-49.19 CenterY=50.5 CenterZ=0 NormalX=0 NormalY=0 NormalZ=1 AngleXU=0 Radius=1.5 StartAngle=1.5708 EndAngle=4.71239
    g4: ArcOfCircle CenterX=-49.19 CenterY=44.75 CenterZ=0 NormalX=0 NormalY=0 NormalZ=1 AngleXU=0 Radius=1.5 StartAngle=1.5708 EndAngle=4.71239
    g5: ArcOfCircle CenterX=-49.19 CenterY=39 CenterZ=0 NormalX=0 NormalY=0 NormalZ=1 AngleXU=0 Radius=1.5 StartAngle=1.5708 EndAngle=4.71239
    g6: ArcOfCircle CenterX=-49.19 CenterY=33 CenterZ=0 NormalX=0 NormalY=0 NormalZ=1 AngleXU=0 Radius=1.5 StartAngle=1.5708 EndAngle=4.71239
    g7: ArcOfCircle CenterX=-49.19 CenterY=27.25 CenterZ=0 NormalX=0 NormalY=0 NormalZ=1 AngleXU=0 Radius=1.5 StartAngle=1.5708 EndAngle=4.71239
    g8: ArcOfCircle CenterX=-49.19 CenterY=21.5 CenterZ=0 NormalX=0 NormalY=0 NormalZ=1 AngleXU=0 Radius=1.5 StartAngle=1.5708 EndAngle=4.71239
    g9: ArcOfCircle CenterX=-49.19 CenterY=15.75 CenterZ=0 NormalX=0 NormalY=0 NormalZ=1 AngleXU=0 Radius=1.5 StartAngle=1.5708 EndAngle=4.71239
    g10: ArcOfCircle CenterX=-49.19 CenterY=10 CenterZ=0 NormalX=0 NormalY=0 NormalZ=1 AngleXU=0 Radius=1.5 StartAngle=1.5708 EndAngle=4.71239
    g11: ArcOfCircle CenterX=-49.19 CenterY=4.25 CenterZ=0 NormalX=0 NormalY=0 NormalZ=1 AngleXU=0 Radius=1.5 StartAngle=1.5708 EndAngle=4.71239
    g12: LineSegment StartX=-49.19 StartY=69.25 StartZ=0 EndX=-49.19 EndY=66.25 EndZ=0
    g13: LineSegment StartX=-49.19 StartY=63.5 StartZ=0 EndX=-49.19 EndY=60.5 EndZ=0
    g14: LineSegment StartX=-49.19 StartY=57.75 StartZ=0 EndX=-49.19 EndY=54.75 EndZ=0
    g15: LineSegment StartX=-49.19 StartY=52 StartZ=0 EndX=-49.19 EndY=49 EndZ=0
    g16: LineSegment StartX=-49.19 StartY=46.25 StartZ=0 EndX=-49.19 EndY=43.25 EndZ=0
    g17: LineSegment StartX=-49.19 StartY=40.5 StartZ=0 EndX=-49.19 EndY=37.5 EndZ=0
    g18: LineSegment StartX=-49.19 StartY=34.5 StartZ=0 EndX=-49.19 EndY=31.5 EndZ=0
    g19: LineSegment StartX=-49.19 StartY=28.75 StartZ=0 EndX=-49.19 EndY=25.75 EndZ=0
    g20: LineSegment StartX=-49.19 StartY=23 StartZ=0 EndX=-49.19 EndY=20 EndZ=0
    g21: LineSegment StartX=-49.19 StartY=17.25 StartZ=0 EndX=-49.19 EndY=14.25 EndZ=0
    g22: LineSegment StartX=-49.19 StartY=11.5 StartZ=0 EndX=-49.19 EndY=8.5 EndZ=0
    g23: LineSegment StartX=-49.19 StartY=5.75 StartZ=0 EndX=-49.19 EndY=2.75 EndZ=0
  constraints (48):
    c: Block(g0)
    c: Block(g1)
    c: Block(g2)
    c: Block(g3)
    c: Block(g4)
    c: Block(g5)
    c: Block(g6)
    c: Block(g7)
    c: Block(g8)
    c: Block(g9)
    c: Block(g10)
    c: Block(g11)
    c: Coincident(g12,g0)
    c: Coincident(g12,g0)
    c: Vertical(g12)
    c: Vertical(g13)
    c: Coincident(g13,g1)
    c: Vertical(g14)
    c: Coincident(g14,g2)
    c: Vertical(g15)
    c: Coincident(g15,g3)
    c: Vertical(g16)
    c: Coincident(g16,g4)
    c: Vertical(g17)
    c: Coincident(g17,g5)
    c: Vertical(g18)
    c: Coincident(g18,g6)
    c: Vertical(g19)
    c: Coincident(g19,g7)
    c: Vertical(g20)
    c: Coincident(g20,g8)
    c: Vertical(g21)
    c: Coincident(g21,g9)
    c: Vertical(g22)
    c: Coincident(g22,g10)
    c: Vertical(g23)
    c: Coincident(g23,g11)
    c: Block(g23)
    c: Block(g22)
    c: Block(g21)
    c: Block(g20)
    c: Block(g13)
    c: Block(g14)
    c: Block(g15)
    c: Block(g16)
    c: Block(g17)
    c: Block(g18)
    c: Block(g19)
FEATURE [Part::Extrusion] Extrude022
  Base = -> Sketch030
  Dir = (1,-2e-16,2e-16)
  DirMode = 2
  FaceMakerClass = Part::FaceMakerBullseye
  LengthFwd = 19
  LengthRev = 0
  Placement = pos=(-19,0,0) rot=(0,0,1;0rad)
  Solid = true
  Symmetric = false
FEATURE [Part::Fillet] Fillet022
  Base = -> Extrude022
  Edges = 24 edges r=1.49: [Edge6,Edge11,Edge18,Edge23,Edge30,Edge35,Edge42,Edge47,Edge54,Edge59,Edge66,Edge71,Edge78,Edge83,Edge90,Edge95,Edge102,Edge107,Edge114,Edge119,Edge126,Edge131,Edge138,Edge143]
FEATURE [Part::Cut] Cut020  label="top010"
  Base = -> Cut019
  Tool = -> Fillet022
FEATURE [Sketcher::SketchObject] Sketch032
  FullyConstrained = true
  Placement = pos=(117,19,0) rot=(0.57735,0.57735,0.57735;2.0944rad)
  sketch-geometry (48):
    g0: LineSegment StartX=-49.19 StartY=69.25 StartZ=0 EndX=-49.19 EndY=66.25 EndZ=0
    g1: LineSegment StartX=-49.19 StartY=63.5 StartZ=0 EndX=-49.19 EndY=60.5 EndZ=0
    g2: LineSegment StartX=-49.19 StartY=57.75 StartZ=0 EndX=-49.19 EndY=54.75 EndZ=0
    g3: LineSegment StartX=-49.19 StartY=52 StartZ=0 EndX=-49.19 EndY=49 EndZ=0
    g4: LineSegment StartX=-49.19 StartY=46.25 StartZ=0 EndX=-49.19 EndY=43.25 EndZ=0
    g5: LineSegment StartX=-49.19 StartY=40.5 StartZ=0 EndX=-49.19 EndY=37.5 EndZ=0
    g6: LineSegment StartX=-49.19 StartY=34.5 StartZ=0 EndX=-49.19 EndY=31.5 EndZ=0
    g7: LineSegment StartX=-49.19 StartY=28.75 StartZ=0 EndX=-49.19 EndY=25.75 EndZ=0
    g8: LineSegment StartX=-49.19 StartY=23 StartZ=0 EndX=-49.19 EndY=20 EndZ=0
    g9: LineSegment StartX=-49.19 StartY=17.25 StartZ=0 EndX=-49.19 EndY=14.25 EndZ=0
    g10: LineSegment StartX=-49.19 StartY=11.5 StartZ=0 EndX=-49.19 EndY=8.5 EndZ=0
    g11: LineSegment StartX=-49.19 StartY=5.75 StartZ=0 EndX=-49.19 EndY=2.75 EndZ=0
    g12: ArcOfCircle CenterX=-1.5 CenterY=67.75 CenterZ=0 NormalX=0 NormalY=0 NormalZ=1 AngleXU=0 Radius=1.5 StartAngle=4.71239 EndAngle=7.85398
    g13: ArcOfCircle CenterX=-1.5 CenterY=62 CenterZ=0 NormalX=0 NormalY=0 NormalZ=1 AngleXU=0 Radius=1.5 StartAngle=4.71239 EndAngle=7.85398
    g14: ArcOfCircle CenterX=-1.5 CenterY=56.25 CenterZ=0 NormalX=0 NormalY=0 NormalZ=1 AngleXU=0 Radius=1.5 StartAngle=4.71239 EndAngle=7.85398
    g15: ArcOfCircle CenterX=-11.49 CenterY=50.5 CenterZ=0 NormalX=0 NormalY=0 NormalZ=1 AngleXU=0 Radius=1.5 StartAngle=4.71239 EndAngle=7.85398
    g16: ArcOfCircle CenterX=-16.28 CenterY=44.75 CenterZ=0 NormalX=0 NormalY=0 NormalZ=1 AngleXU=0 Radius=1.5 StartAngle=4.71239 EndAngle=7.85398
    g17: ArcOfCircle CenterX=-18.2337 CenterY=39 CenterZ=0 NormalX=0 NormalY=0 NormalZ=1 AngleXU=0 Radius=1.5 StartAngle=4.71485 EndAngle=7.85398
    g18: ArcOfCircle CenterX=-16.2837 CenterY=27.25 CenterZ=0 NormalX=0 NormalY=0 NormalZ=1 AngleXU=0 Radius=1.5 StartAngle=4.71485 EndAngle=7.85398
    g19: ArcOfCircle CenterX=-18.2337 CenterY=33 CenterZ=0 NormalX=0 NormalY=0 NormalZ=1 AngleXU=0 Radius=1.5 StartAngle=4.71485 EndAngle=7.85398
    g20: ArcOfCircle CenterX=-11.49 CenterY=21.5 CenterZ=0 NormalX=0 NormalY=0 NormalZ=1 AngleXU=0 Radius=1.5 StartAngle=4.71239 EndAngle=7.85398
    g21: ArcOfCircle CenterX=-1.5 CenterY=4.25 CenterZ=0 NormalX=0 NormalY=0 NormalZ=1 AngleXU=0 Radius=1.5 StartAngle=4.71239 EndAngle=7.85398
    g22: ArcOfCircle CenterX=-1.5 CenterY=10 CenterZ=0 NormalX=0 NormalY=0 NormalZ=1 AngleXU=0 Radius=1.5 StartAngle=4.71239 EndAngle=7.85398
    g23: ArcOfCircle CenterX=-1.5 CenterY=15.75 CenterZ=0 NormalX=0 NormalY=0 NormalZ=1 AngleXU=0 Radius=1.5 StartAngle=4.71239 EndAngle=7.85398
    g24: LineSegment StartX=-49.19 StartY=69.25 StartZ=0 EndX=-1.5 EndY=69.25 EndZ=0
    g25: LineSegment StartX=-49.19 StartY=66.25 StartZ=0 EndX=-1.5 EndY=66.25 EndZ=0
    g26: LineSegment StartX=-49.19 StartY=63.5 StartZ=0 EndX=-1.5 EndY=63.5 EndZ=0
    g27: LineSegment StartX=-49.19 StartY=60.5 StartZ=0 EndX=-1.5 EndY=60.5 EndZ=0
    g28: LineSegment StartX=-49.19 StartY=57.75 StartZ=0 EndX=-1.5 EndY=57.75 EndZ=0
    g29: LineSegment StartX=-49.19 StartY=54.75 StartZ=0 EndX=-1.5 EndY=54.75 EndZ=0
    g30: LineSegment StartX=-49.19 StartY=52 StartZ=0 EndX=-11.49 EndY=52 EndZ=0
    g31: LineSegment StartX=-49.19 StartY=49 StartZ=0 EndX=-11.49 EndY=49 EndZ=0
    g32: LineSegment StartX=-49.19 StartY=46.25 StartZ=0 EndX=-16.28 EndY=46.25 EndZ=0
    g33: LineSegment StartX=-49.19 StartY=43.25 StartZ=0 EndX=-16.28 EndY=43.25 EndZ=0
    g34: LineSegment StartX=-49.19 StartY=40.5 StartZ=0 EndX=-18.2337 EndY=40.5 EndZ=0
    g35: LineSegment StartX=-49.19 StartY=37.5 StartZ=0 EndX=-18.23 EndY=37.5 EndZ=0
    g36: LineSegment StartX=-49.19 StartY=34.5 StartZ=0 EndX=-18.2337 EndY=34.5 EndZ=0
    g37: LineSegment StartX=-49.19 StartY=31.5 StartZ=0 EndX=-18.23 EndY=31.5 EndZ=0
    g38: LineSegment StartX=-49.19 StartY=28.75 StartZ=0 EndX=-16.2837 EndY=28.75 EndZ=0
    g39: LineSegment StartX=-49.19 StartY=25.75 StartZ=0 EndX=-16.28 EndY=25.75 EndZ=0
    g40: LineSegment StartX=-49.19 StartY=23 StartZ=0 EndX=-11.49 EndY=23 EndZ=0
    g41: LineSegment StartX=-49.19 StartY=20 StartZ=0 EndX=-11.49 EndY=20 EndZ=0
    g42: LineSegment StartX=-49.19 StartY=17.25 StartZ=0 EndX=-1.5 EndY=17.25 EndZ=0
    g43: LineSegment StartX=-49.19 StartY=14.25 StartZ=0 EndX=-1.5 EndY=14.25 EndZ=0
    g44: LineSegment StartX=-49.19 StartY=11.5 StartZ=0 EndX=-1.5 EndY=11.5 EndZ=0
    g45: LineSegment StartX=-49.19 StartY=8.5 StartZ=0 EndX=-1.5 EndY=8.5 EndZ=0
    g46: LineSegment StartX=-49.19 StartY=5.75 StartZ=0 EndX=-1.5 EndY=5.75 EndZ=0
    g47: LineSegment StartX=-49.19 StartY=2.75 StartZ=0 EndX=-1.5 EndY=2.75 EndZ=0
  constraints (120):
    c: Vertical(g0)
    c: Distance(g0) = 3
    c: Block(g0)
    c: Vertical(g1)
    c: Distance(g1) = 3
    c: Vertical(g2)
    c: Equal(g0,g2) = 3
    c: Block(g2)
    c: Vertical(g3)
    c: Equal(g1,g3) = 3
    c: Vertical(g4)
    c: Equal(g0,g4) = 3
    c: Block(g4)
    c: Vertical(g5)
    c: Equal(g1,g5) = 3
    c: Vertical(g6)
    c: Equal(g0,g6) = 3
    c: Block(g6)
    c: Vertical(g7)
    c: Equal(g1,g7) = 3
    c: Vertical(g8)
    c: Equal(g0,g8) = 3
    c: Block(g8)
    c: Vertical(g9)
    c: Equal(g1,g9) = 3
    c: Vertical(g10)
    c: Equal(g0,g10) = 3
    c: Block(g10)
    c: Vertical(g11)
    c: Equal(g1,g11) = 3
    c: Block(g12)
    c: Block(g13)
    c: Block(g14)
    c: Block(g15)
    c: Block(g16)
    c: Block(g17)
    c: Block(g18)
    c: Block(g19)
    c: Block(g20)
    c: Block(g21)
    c: Block(g22)
    c: Block(g23)
    c: Block(g11)
    c: Block(g9)
    c: Block(g7)
    c: Block(g5)
    c: Block(g3)
    c: Block(g1)
    c: Coincident(g24,g0)
    c: Coincident(g24,g12)
    c: Horizontal(g24)
    c: Coincident(g25,g0)
    c: Coincident(g25,g12)
    c: Horizontal(g25)
    c: Coincident(g26,g1)
    c: Coincident(g26,g13)
    c: Horizontal(g26)
    c: Coincident(g27,g1)
    c: Coincident(g27,g13)
    c: Horizontal(g27)
    c: Coincident(g28,g2)
    c: Coincident(g28,g14)
    c: Horizontal(g28)
    c: Coincident(g29,g2)
    c: Coincident(g29,g14)
    c: Horizontal(g29)
    c: Coincident(g30,g3)
    c: Coincident(g30,g15)
    c: Horizontal(g30)
    c: Coincident(g31,g3)
    c: Coincident(g31,g15)
    c: Horizontal(g31)
    c: Coincident(g32,g4)
    c: Coincident(g32,g16)
    c: Horizontal(g32)
    c: Coincident(g33,g4)
    c: Coincident(g33,g16)
    c: Horizontal(g33)
    c: Coincident(g34,g5)
    c: Coincident(g34,g17)
    c: Horizontal(g34)
    c: Coincident(g35,g5)
    c: Coincident(g35,g17)
    c: Horizontal(g35)
    c: Coincident(g36,g6)
    c: Coincident(g36,g19)
    c: Horizontal(g36)
    c: Coincident(g37,g6)
    c: Coincident(g37,g19)
    c: Horizontal(g37)
    c: Coincident(g38,g7)
    c: Coincident(g38,g18)
    c: Horizontal(g38)
    c: Coincident(g39,g7)
    c: Coincident(g39,g18)
    c: Horizontal(g39)
    c: Coincident(g40,g8)
    c: Coincident(g40,g20)
    c: Horizontal(g40)
    c: Coincident(g41,g8)
    c: Coincident(g41,g20)
    c: Horizontal(g41)
    c: Coincident(g42,g9)
    c: Coincident(g42,g23)
    c: Horizontal(g42)
    c: Coincident(g43,g9)
    c: Coincident(g43,g23)
    c: Horizontal(g43)
    c: Coincident(g44,g10)
    c: Coincident(g44,g22)
    c: Horizontal(g44)
    c: Coincident(g45,g10)
    c: Coincident(g45,g22)
    c: Horizontal(g45)
    c: Coincident(g46,g11)
    c: Coincident(g46,g21)
    c: Horizontal(g46)
    c: Coincident(g47,g11)
    c: Coincident(g47,g21)
    c: Horizontal(g47)
FEATURE [Part::Extrusion] Extrude023
  Base = -> Sketch032
  Dir = (1,-2e-16,2e-16)
  DirMode = 2
  FaceMakerClass = Part::FaceMakerBullseye
  LengthFwd = 19
  LengthRev = 0
  Placement = pos=(-19,0,0) rot=(0,0,1;0rad)
  Solid = true
  Symmetric = false
FEATURE [Part::Fillet] Fillet023
  Base = -> Extrude023
  Edges = <same value as first occurrence — deduplicated (x6 in doc)>
  Placement = pos=(0,0.05,0) rot=(0,0,1;0rad)
FEATURE [Part::Cut] Cut014  label="bottom003"
  Base = -> Cut007
  Tool = -> Fusion047
FEATURE [Part::Cut] Cut021  label="bottom004"
  Base = -> Cut014
  Tool = -> Fillet023
FEATURE [Sketcher::SketchObject] Sketch033
  FullyConstrained = true
  Placement = pos=(117,19,0) rot=(0.57735,0.57735,0.57735;2.0944rad)
  sketch-geometry (8):
    g0: LineSegment StartX=-49.19 StartY=69.25 StartZ=0 EndX=-49.19 EndY=66.25 EndZ=0
    g1: LineSegment StartX=-49.19 StartY=5.75 StartZ=0 EndX=-49.19 EndY=2.75 EndZ=0
    g2: ArcOfCircle CenterX=-1.5 CenterY=67.75 CenterZ=0 NormalX=0 NormalY=0 NormalZ=1 AngleXU=0 Radius=1.5 StartAngle=4.71239 EndAngle=7.85398
    g3: ArcOfCircle CenterX=-1.5 CenterY=4.25 CenterZ=0 NormalX=0 NormalY=0 NormalZ=1 AngleXU=0 Radius=1.5 StartAngle=4.71239 EndAngle=7.85398
    g4: LineSegment StartX=-49.19 StartY=69.25 StartZ=0 EndX=-1.5 EndY=69.25 EndZ=0
    g5: LineSegment StartX=-49.19 StartY=66.25 StartZ=0 EndX=-1.5 EndY=66.25 EndZ=0
    g6: LineSegment StartX=-49.19 StartY=5.75 StartZ=0 EndX=-1.5 EndY=5.75 EndZ=0
    g7: LineSegment StartX=-49.19 StartY=2.75 StartZ=0 EndX=-1.5 EndY=2.75 EndZ=0
  constraints (19):
    c: Vertical(g0)
    c: Distance(g0) = 3
    c: Block(g0)
    c: Vertical(g1)
    c: Block(g2)
    c: Block(g3)
    c: Block(g1)
    c: Coincident(g4,g0)
    c: Coincident(g4,g2)
    c: Horizontal(g4)
    c: Coincident(g5,g0)
    c: Coincident(g5,g2)
    c: Horizontal(g5)
    c: Coincident(g6,g1)
    c: Coincident(g6,g3)
    c: Horizontal(g6)
    c: Coincident(g7,g1)
    c: Coincident(g7,g3)
    c: Horizontal(g7)
FEATURE [Sketcher::SketchObject] Sketch034
  FullyConstrained = true
  Placement = pos=(117,19,0) rot=(0.57735,0.57735,0.57735;2.0944rad)
  sketch-geometry (8):
    g0: LineSegment StartX=-49.19 StartY=63.5 StartZ=0 EndX=-49.19 EndY=60.5 EndZ=0
    g1: LineSegment StartX=-49.19 StartY=11.5 StartZ=0 EndX=-49.19 EndY=8.5 EndZ=0
    g2: ArcOfCircle CenterX=-1.5 CenterY=62 CenterZ=0 NormalX=0 NormalY=0 NormalZ=1 AngleXU=0 Radius=1.5 StartAngle=4.71239 EndAngle=7.85398
    g3: ArcOfCircle CenterX=-1.5 CenterY=10 CenterZ=0 NormalX=0 NormalY=0 NormalZ=1 AngleXU=0 Radius=1.5 StartAngle=4.71239 EndAngle=7.85398
    g4: LineSegment StartX=-49.19 StartY=63.5 StartZ=0 EndX=-1.5 EndY=63.5 EndZ=0
    g5: LineSegment StartX=-49.19 StartY=60.5 StartZ=0 EndX=-1.5 EndY=60.5 EndZ=0
    g6: LineSegment StartX=-49.19 StartY=11.5 StartZ=0 EndX=-1.5 EndY=11.5 EndZ=0
    g7: LineSegment StartX=-49.19 StartY=8.5 StartZ=0 EndX=-1.5 EndY=8.5 EndZ=0
  constraints (19):
    c: Vertical(g0)
    c: Distance(g0) = 3
    c: Vertical(g1)
    c: Block(g1)
    c: Block(g2)
    c: Block(g3)
    c: Block(g0)
    c: Coincident(g4,g0)
    c: Coincident(g4,g2)
    c: Horizontal(g4)
    c: Coincident(g5,g0)
    c: Coincident(g5,g2)
    c: Horizontal(g5)
    c: Coincident(g6,g1)
    c: Coincident(g6,g3)
    c: Horizontal(g6)
    c: Coincident(g7,g1)
    c: Coincident(g7,g3)
    c: Horizontal(g7)
FEATURE [Part::Extrusion] Extrude024
  Base = -> Sketch033
  Dir = (1,0,0)
  DirMode = 2
  FaceMakerClass = Part::FaceMakerBullseye
  LengthFwd = 10
  LengthRev = 0
  Solid = true
  Symmetric = false
FEATURE [Part::Extrusion] Extrude025
  Base = -> Sketch034
  Dir = (1,0,0)
  DirMode = 2
  FaceMakerClass = Part::FaceMakerBullseye
  LengthFwd = 10
  LengthRev = 0
  Solid = true
  Symmetric = false
FEATURE [Part::Fillet] Fillet024  label="removeFromtMoreFrontCaseScrewRetainers"
  Base = -> Extrude024
  Edges = 4 edges r=1.49: [Edge6,Edge11,Edge18,Edge23]
  Placement = pos=(-11,0,0) rot=(0,0,1;0rad)
FEATURE [Part::Fillet] Fillet025  label="removeFromtMoreFrontCaseScrewRetainers001"
  Base = -> Extrude025
  Edges = 4 edges r=1.49: [Edge6,Edge11,Edge18,Edge23]
  Placement = pos=(-19,0,0) rot=(0,0,1;0rad)
FEATURE [Part::Cut] Cut022
  Base = -> Cut015
  Tool = -> Fillet025
FEATURE [Part::Cut] Cut023  label="screwRetainers"
  Base = -> Cut022
  Tool = -> Fillet024
FEATURE [Part::MultiFuse] Fusion056  label="bottom005"
  Shapes = -> [Fusion044,Cut021]
FEATURE [Part::MultiFuse] Fusion057  label="casePillars001"
  Shapes = -> [Cut016,Fusion052]
FEATURE [Part::MultiFuse] Fusion058  label="bottom006"
  Shapes = -> [Fusion056,Cut023]
FEATURE [Part::MultiFuse] Fusion059  label="bottom007"
  Shapes = -> [Fusion058,Fillet005]
FEATURE [Part::MultiFuse] Fusion060  label="bottom008"
  Shapes = -> [Fusion059,Fusion]
FEATURE [Part::MultiFuse] Fusion061  label="top011"
  Shapes = -> [Cut006,Cut020]
FEATURE [Part::MultiFuse] Fusion062  label="top012"
  Shapes = -> [Fusion057,Fusion061]
FEATURE [Sketcher::SketchObject] Sketch035  label="topSketch007"
  FullyConstrained = true
  sketch-geometry (6):
    g0: LineSegment StartX=19 StartY=38 StartZ=0 EndX=117 EndY=38 EndZ=0
    g1: ArcOfCircle CenterX=19 CenterY=19 CenterZ=0 NormalX=0 NormalY=0 NormalZ=1 AngleXU=0 Radius=19 StartAngle=1.5708 EndAngle=3.14159
    g2: LineSegment StartX=117 StartY=38 StartZ=0 EndX=117 EndY=19 EndZ=0
    g3: LineSegment StartX=98 StartY=1.0161e-12 StartZ=0 EndX=5.22862e-06 EndY=1.0161e-12 EndZ=0
    g4: LineSegment StartX=5.22862e-06 StartY=19 StartZ=0 EndX=5.22862e-06 EndY=1.0161e-12 EndZ=0
    g5: ArcOfCircle CenterX=98 CenterY=19 CenterZ=0 NormalX=0 NormalY=0 NormalZ=1 AngleXU=0 Radius=19 StartAngle=4.71239 EndAngle=6.28319
  constraints (16):
    c: Horizontal(g0)
    c: Distance(g0) = 98
    c: Coincident(g1,g0)
    c: Block(g1)
    c: Coincident(g2,g0)
    c: Vertical(g2)
    c: Distance(g2) = 19
    c: Horizontal(g3)
    c: Coincident(g4,g1)
    c: Vertical(g4)
    c: Coincident(g3,g4)
    c: Block(g3)
    c: Coincident(g5,g2)
    c: Coincident(g5,g3)
    c: Block(g0)
    c: Block(g5)
FEATURE [Part::Extrusion] Extrude026  label="sideA001"
  Base = -> Sketch035
  Dir = (0,0,1)
  DirMode = 2
  FaceMakerClass = Part::FaceMakerBullseye
  LengthFwd = 3
  LengthRev = 0
  Placement = pos=(0,0,-2.7) rot=(0,0,1;0rad)
  Solid = true
  Symmetric = false
FEATURE [Sketcher::SketchObject] Sketch036  label="topSketch008"
  FullyConstrained = true
  sketch-geometry (6):
    g0: LineSegment StartX=19 StartY=38 StartZ=0 EndX=117 EndY=38 EndZ=0
    g1: ArcOfCircle CenterX=19 CenterY=19 CenterZ=0 NormalX=0 NormalY=0 NormalZ=1 AngleXU=0 Radius=19 StartAngle=1.5708 EndAngle=3.14159
    g2: LineSegment StartX=117 StartY=38 StartZ=0 EndX=117 EndY=19 EndZ=0
    g3: LineSegment StartX=98 StartY=1.0161e-12 StartZ=0 EndX=5.22862e-06 EndY=1.0161e-12 EndZ=0
    g4: LineSegment StartX=5.22862e-06 StartY=19 StartZ=0 EndX=5.22862e-06 EndY=1.0161e-12 EndZ=0
    g5: ArcOfCircle CenterX=98 CenterY=19 CenterZ=0 NormalX=0 NormalY=0 NormalZ=1 AngleXU=0 Radius=19 StartAngle=4.71239 EndAngle=6.28319
  constraints (16):
    c: Horizontal(g0)
    c: Distance(g0) = 98
    c: Coincident(g1,g0)
    c: Block(g1)
    c: Coincident(g2,g0)
    c: Vertical(g2)
    c: Distance(g2) = 19
    c: Horizontal(g3)
    c: Coincident(g4,g1)
    c: Vertical(g4)
    c: Coincident(g3,g4)
    c: Block(g3)
    c: Coincident(g5,g2)
    c: Coincident(g5,g3)
    c: Block(g0)
    c: Block(g5)
FEATURE [Part::Extrusion] Extrude027  label="sideB001"
  Base = -> Sketch036
  Dir = (0,0,1)
  DirMode = 2
  FaceMakerClass = Part::FaceMakerBullseye
  LengthFwd = 3
  LengthRev = 0
  Placement = pos=(0,0,71.7) rot=(0,0,1;0rad)
  Solid = true
  Symmetric = false
FEATURE [Part::MultiFuse] Fusion064  label="removeFromBottom"
  Shapes = -> [Extrude026,Extrude027]
FEATURE [Part::Cut] Cut024  label="bottom009"
  Base = -> Fusion060
  Tool = -> Fusion064
FEATURE [Sketcher::SketchObject] Sketch037  label="topSketch009"
  FullyConstrained = true
  sketch-geometry (8):
    g0: ArcOfCircle CenterX=19 CenterY=19.1201 CenterZ=0 NormalX=0 NormalY=0 NormalZ=1 AngleXU=0 Radius=18.8799 StartAngle=1.5708 EndAngle=3.14793
    g1: LineSegment StartX=0.120501 StartY=19.0004 StartZ=0 EndX=0.120501 EndY=0.000382114 EndZ=0
    g2: LineSegment StartX=19 StartY=38 StartZ=0 EndX=124 EndY=38 EndZ=0
    g3: LineSegment StartX=0.120501 StartY=0.000382114 StartZ=0 EndX=105.121 EndY=0.000382114 EndZ=0
    g4: LineSegment StartX=124 StartY=38 StartZ=0 EndX=125.616 EndY=38 EndZ=0
    g5: LineSegment StartX=105.121 StartY=0.000382114 StartZ=0 EndX=106.736 EndY=0.000382114 EndZ=0
    g6: ArcOfCircle CenterX=106.616 CenterY=19 CenterZ=0 NormalX=0 NormalY=0 NormalZ=1 AngleXU=0 Radius=19 StartAngle=4.71873 EndAngle=6.28319
    g7: LineSegment StartX=125.616 StartY=38 StartZ=0 EndX=125.616 EndY=19 EndZ=0
  constraints (21):
    c: Block(g0)
    c: Coincident(g1,g0)
    c: Vertical(g1)
    c: Horizontal(g2)
    c: Distance(g2) = 105
    c: Coincident(g2,g0)
    c: Distance(g1) = 19
    c: Coincident(g3,g1)
    c: Horizontal(g3)
    c: Distance(g3) = 105
    c: Coincident(g4,g2)
    c: Horizontal(g4)
    c: Distance(g4) = 1.61553
    c: Horizontal(g5)
    c: Equal(g4,g5) = 1.61553
    c: Coincident(g5,g3)
    c: Block(g6)
    c: Coincident(g6,g5)
    c: Coincident(g7,g4)
    c: Coincident(g7,g6)
    c: Vertical(g7)
FEATURE [Part::Extrusion] Extrude028  label="sideB"
  Base = -> Sketch037
  Dir = (0,0,1)
  DirMode = 2
  FaceMakerClass = Part::FaceMakerBullseye
  LengthFwd = 3
  LengthRev = 0
  Placement = pos=(0,0,72) rot=(0,0,1;0rad)
  Solid = true
  Symmetric = false
FEATURE [Sketcher::SketchObject] Sketch038  label="topSketch010"
  FullyConstrained = true
  sketch-geometry (22):
    g0: LineSegment StartX=5.21097e-06 StartY=3 StartZ=0 EndX=5.21097e-06 EndY=19 EndZ=0
    g1: ArcOfCircle CenterX=19 CenterY=19 CenterZ=0 NormalX=0 NormalY=0 NormalZ=1 AngleXU=0 Radius=19 StartAngle=1.5708 EndAngle=3.14159
    g2: ArcOfCircle CenterX=19 CenterY=19 CenterZ=0 NormalX=0 NormalY=0 NormalZ=1 AngleXU=0 Radius=16 StartAngle=1.5708 EndAngle=3.14159
    g3: LineSegment StartX=114 StartY=35 StartZ=0 EndX=19 EndY=35 EndZ=0
    g4: LineSegment StartX=5.21097e-06 StartY=3 StartZ=0 EndX=5.21097e-06 EndY=0 EndZ=0
    g5: LineSegment StartX=3 StartY=0 StartZ=0 EndX=5.21097e-06 EndY=0 EndZ=0
    g6: LineSegment StartX=3 StartY=19 StartZ=0 EndX=3 EndY=0 EndZ=0
    g7: LineSegment StartX=19 StartY=38 StartZ=0 EndX=124 EndY=38 EndZ=0
    g8: Circle CenterX=119 CenterY=35 CenterZ=0 NormalX=0 NormalY=0 NormalZ=1 AngleXU=0 Radius=1
    g9: Circle CenterX=121 CenterY=35 CenterZ=0 NormalX=0 NormalY=0 NormalZ=1 AngleXU=0 Radius=1
    g10: Circle CenterX=121 CenterY=33 CenterZ=0 NormalX=0 NormalY=0 NormalZ=1 AngleXU=0 Radius=1
    g11: BSplineCurve PolesCount=3 KnotsCount=2 Degree=2 IsPeriodic=0
    g12: GeomPoint X=119 Y=35 Z=0
    g13: GeomPoint X=121 Y=33 Z=0
    g14: LineSegment StartX=119 StartY=35 StartZ=0 EndX=114 EndY=35 EndZ=0
    g15: ArcOfCircle CenterX=105 CenterY=19 CenterZ=0 NormalX=0 NormalY=0 NormalZ=1 AngleXU=0 Radius=16 StartAngle=5.60905 EndAngle=6.28319
    g16: LineSegment StartX=121 StartY=33 StartZ=0 EndX=121 EndY=19 EndZ=0
    g17: LineSegment StartX=117.5 StartY=9.01251 StartZ=0 EndX=121.163 EndY=9.0125 EndZ=0
    g18: ArcOfCircle CenterX=105 CenterY=19 CenterZ=0 NormalX=0 NormalY=0 NormalZ=1 AngleXU=0 Radius=20.6155 StartAngle=5.7297 EndAngle=6.28319
    g19: LineSegment StartX=121.163 StartY=9.0125 StartZ=0 EndX=122.538 EndY=8.16329 EndZ=0
    g20: LineSegment StartX=124 StartY=38 StartZ=0 EndX=125.616 EndY=38 EndZ=0
    g21: LineSegment StartX=125.616 StartY=19 StartZ=0 EndX=125.616 EndY=38 EndZ=0
  constraints (49):
    c: Vertical(g0)
    c: Block(g0)
    c: Coincident(g1,g0)
    c: Block(g1)
    c: Coincident(g2,g1)
    c: Block(g2)
    c: Coincident(g3,g2)
    c: Horizontal(g3)
    c: Tangent(g3,g2)
    c: Coincident(g4,g0)
    c: Distance(g4) = 3
    c: Vertical(g4)
    c: Coincident(g5,g4)
    c: Horizontal(g5)
    c: Coincident(g6,g2)
    c: Coincident(g6,g5)
    c: Vertical(g6)
    c: Horizontal(g7)
    c: Distance(g7) = 105
    c: Coincident(g7,g1)
    c: Block(g3)
    c: Weight(g8) = 1
    c: Equal(g8,g9)
    c: Equal(g8,g10)
    c: InternalAlignment(g8,g11)
    c: InternalAlignment(g9,g11)
    c: InternalAlignment(g10,g11)
    c: InternalAlignment(g12,g11)
    c: InternalAlignment(g13,g11)
    c: Block(g11)
    c: Coincident(g14,g11)
    c: Coincident(g14,g3)
    c: Horizontal(g14)
    c: Block(g15)
    c: Coincident(g16,g11)
    c: Coincident(g16,g15)
    c: Vertical(g16)
    c: Distance(g16) = 14
    c: Coincident(g17,g15)
    c: Block(g18)
    c: Coincident(g19,g18)
    c: Coincident(g20,g7)
    c: Horizontal(g20)
    c: Vertical(g21)
    c: Coincident(g20,g21)
    c: Block(g20)
    c: Block(g21)
    c: Block(g19)
    c: Block(g17)
FEATURE [Part::Extrusion] Extrude029
  Base = -> Sketch038
  Dir = (0,0,1)
  DirMode = 2
  FaceMakerClass = Part::FaceMakerBullseye
  LengthFwd = 72
  LengthRev = 0
  Solid = true
  Symmetric = false
FEATURE [Part::Feature] Face085
  shape: bbox 4.8 x 25.5 x 2e-07 mm, 1 faces, 0 solids (baked)
FEATURE [Part::Revolution] Revolve089  label="moreFrontCaseScrewPost003"
  Angle = 360
  Axis = (0,1,0)
  Base = (0,0,0)
  FaceMakerClass = Part::FaceMakerBullseye
  Placement = pos=(109.5,4.5,3.5) rot=(0,0,1;0rad)
  Solid = false
  Source = -> Face085
  Symmetric = false
FEATURE [Part::Feature] Face086
  shape: bbox 4.8 x 25.5 x 2e-07 mm, 1 faces, 0 solids (baked)
FEATURE [Part::Revolution] Revolve090  label="moreFrontCaseScrewPost004"
  Angle = 360
  Axis = (0,1,0)
  Base = (0,0,0)
  FaceMakerClass = Part::FaceMakerBullseye
  Placement = pos=(109.5,4.5,68.5) rot=(0,0,1;0rad)
  Solid = false
  Source = -> Face086
  Symmetric = false
FEATURE [Part::Fillet] Fillet026  label="top013"
  Base = -> Extrude029
  Edges = 1 edges r=2: [Edge35]
FEATURE [Sketcher::SketchObject] Sketch039
  FullyConstrained = true
  sketch-geometry (7):
    g0: LineSegment StartX=0 StartY=0 StartZ=0 EndX=0 EndY=6 EndZ=0
    g1: Circle CenterX=0 CenterY=0 CenterZ=0 NormalX=0 NormalY=0 NormalZ=1 AngleXU=0 Radius=1
    g2: Circle CenterX=8 CenterY=6 CenterZ=0 NormalX=0 NormalY=0 NormalZ=1 AngleXU=0 Radius=1
    g3: BSplineCurve PolesCount=3 KnotsCount=2 Degree=2 IsPeriodic=0
    g4: GeomPoint X=0 Y=0 Z=0
    g5: GeomPoint X=8 Y=6 Z=0
    g6: LineSegment StartX=0 StartY=6 StartZ=0 EndX=8 EndY=6 EndZ=0
  constraints (14):
    c: Coincident(g0,g-1)
    c: Distance(g0) = 6
    c: Vertical(g0)
    c: Coincident(g3,g0)
    c: Weight(g1) = 1
    c: Equal(g1,g2)
    c: InternalAlignment(g1,g3)
    c: InternalAlignment(g2,g3)
    c: InternalAlignment(g4,g3)
    c: InternalAlignment(g5,g3)
    c: Block(g3)
    c: Coincident(g6,g0)
    c: Coincident(g6,g3)
    c: Horizontal(g6)
FEATURE [Sketcher::SketchObject] Sketch040
  FullyConstrained = true
  sketch-geometry (7):
    g0: LineSegment StartX=0 StartY=0 StartZ=0 EndX=0 EndY=6 EndZ=0
    g1: Circle CenterX=0 CenterY=0 CenterZ=0 NormalX=0 NormalY=0 NormalZ=1 AngleXU=0 Radius=1
    g2: Circle CenterX=8 CenterY=6 CenterZ=0 NormalX=0 NormalY=0 NormalZ=1 AngleXU=0 Radius=1
    g3: BSplineCurve PolesCount=3 KnotsCount=2 Degree=2 IsPeriodic=0
    g4: GeomPoint X=0 Y=0 Z=0
    g5: GeomPoint X=8 Y=6 Z=0
    g6: LineSegment StartX=0 StartY=6 StartZ=0 EndX=8 EndY=6 EndZ=0
  constraints (14):
    c: Coincident(g0,g-1)
    c: Distance(g0) = 6
    c: Vertical(g0)
    c: Coincident(g3,g0)
    c: Weight(g1) = 1
    c: Equal(g1,g2)
    c: InternalAlignment(g1,g3)
    c: InternalAlignment(g2,g3)
    c: InternalAlignment(g4,g3)
    c: InternalAlignment(g5,g3)
    c: Block(g3)
    c: Coincident(g6,g0)
    c: Coincident(g6,g3)
    c: Horizontal(g6)
FEATURE [Sketcher::SketchObject] Sketch041
  FullyConstrained = true
  sketch-geometry (7):
    g0: LineSegment StartX=0 StartY=0 StartZ=0 EndX=0 EndY=6 EndZ=0
    g1: Circle CenterX=0 CenterY=0 CenterZ=0 NormalX=0 NormalY=0 NormalZ=1 AngleXU=0 Radius=1
    g2: Circle CenterX=8 CenterY=6 CenterZ=0 NormalX=0 NormalY=0 NormalZ=1 AngleXU=0 Radius=1
    g3: BSplineCurve PolesCount=3 KnotsCount=2 Degree=2 IsPeriodic=0
    g4: GeomPoint X=0 Y=0 Z=0
    g5: GeomPoint X=8 Y=6 Z=0
    g6: LineSegment StartX=0 StartY=6 StartZ=0 EndX=8 EndY=6 EndZ=0
  constraints (14):
    c: Coincident(g0,g-1)
    c: Distance(g0) = 6
    c: Vertical(g0)
    c: Coincident(g3,g0)
    c: Weight(g1) = 1
    c: Equal(g1,g2)
    c: InternalAlignment(g1,g3)
    c: InternalAlignment(g2,g3)
    c: InternalAlignment(g4,g3)
    c: InternalAlignment(g5,g3)
    c: Block(g3)
    c: Coincident(g6,g0)
    c: Coincident(g6,g3)
    c: Horizontal(g6)
FEATURE [Sketcher::SketchObject] Sketch042
  FullyConstrained = true
  sketch-geometry (7):
    g0: LineSegment StartX=0 StartY=0 StartZ=0 EndX=0 EndY=6 EndZ=0
    g1: Circle CenterX=0 CenterY=0 CenterZ=0 NormalX=0 NormalY=0 NormalZ=1 AngleXU=0 Radius=1
    g2: Circle CenterX=8 CenterY=6 CenterZ=0 NormalX=0 NormalY=0 NormalZ=1 AngleXU=0 Radius=1
    g3: BSplineCurve PolesCount=3 KnotsCount=2 Degree=2 IsPeriodic=0
    g4: GeomPoint X=0 Y=0 Z=0
    g5: GeomPoint X=8 Y=6 Z=0
    g6: LineSegment StartX=0 StartY=6 StartZ=0 EndX=8 EndY=6 EndZ=0
  constraints (14):
    c: Coincident(g0,g-1)
    c: Distance(g0) = 6
    c: Vertical(g0)
    c: Coincident(g3,g0)
    c: Weight(g1) = 1
    c: Equal(g1,g2)
    c: InternalAlignment(g1,g3)
    c: InternalAlignment(g2,g3)
    c: InternalAlignment(g4,g3)
    c: InternalAlignment(g5,g3)
    c: Block(g3)
    c: Coincident(g6,g0)
    c: Coincident(g6,g3)
    c: Horizontal(g6)
FEATURE [Part::Extrusion] Extrude030  label="caseScrewPillarBracket008"
  Base = -> Sketch039
  Dir = (0,0,1)
  DirMode = 2
  FaceMakerClass = Part::FaceMakerBullseye
  LengthFwd = 2.4
  LengthRev = 0
  Placement = pos=(15.76,29,8.8) rot=(0,1,0;0rad)
  Solid = true
  Symmetric = false
FEATURE [Part::Extrusion] Extrude031  label="caseScrewPillarBracket009"
  Base = -> Sketch040
  Dir = (0,0,1)
  DirMode = 2
  FaceMakerClass = Part::FaceMakerBullseye
  LengthFwd = 2.4
  LengthRev = 0
  Placement = pos=(15.76,29,60.8) rot=(0,0,1;0rad)
  Solid = true
  Symmetric = false
FEATURE [Part::Extrusion] Extrude032  label="caseScrewPillarBracket010"
  Base = -> Sketch041
  Dir = (0,0,1)
  DirMode = 2
  FaceMakerClass = Part::FaceMakerBullseye
  LengthFwd = 2.4
  LengthRev = 0
  Placement = pos=(13.7,29,13.26) rot=(0,-1,0;1.5708rad)
  Solid = true
  Symmetric = false
FEATURE [Part::Extrusion] Extrude033  label="caseScrewPillarBracket011"
  Base = -> Sketch042
  Dir = (0,0,1)
  DirMode = 2
  FaceMakerClass = Part::FaceMakerBullseye
  LengthFwd = 2.4
  LengthRev = 0
  Placement = pos=(11.3,29,58.74) rot=(0,1,0;1.5708rad)
  Solid = true
  Symmetric = false
FEATURE [Sketcher::SketchObject] Sketch043
  FullyConstrained = true
  sketch-geometry (7):
    g0: LineSegment StartX=0 StartY=0 StartZ=0 EndX=0 EndY=6 EndZ=0
    g1: Circle CenterX=0 CenterY=0 CenterZ=0 NormalX=0 NormalY=0 NormalZ=1 AngleXU=0 Radius=1
    g2: Circle CenterX=8 CenterY=6 CenterZ=0 NormalX=0 NormalY=0 NormalZ=1 AngleXU=0 Radius=1
    g3: BSplineCurve PolesCount=3 KnotsCount=2 Degree=2 IsPeriodic=0
    g4: GeomPoint X=0 Y=0 Z=0
    g5: GeomPoint X=8 Y=6 Z=0
    g6: LineSegment StartX=0 StartY=6 StartZ=0 EndX=8 EndY=6 EndZ=0
  constraints (14):
    c: Coincident(g0,g-1)
    c: Distance(g0) = 6
    c: Vertical(g0)
    c: Coincident(g3,g0)
    c: Weight(g1) = 1
    c: Equal(g1,g2)
    c: InternalAlignment(g1,g3)
    c: InternalAlignment(g2,g3)
    c: InternalAlignment(g4,g3)
    c: InternalAlignment(g5,g3)
    c: Block(g3)
    c: Coincident(g6,g0)
    c: Coincident(g6,g3)
    c: Horizontal(g6)
FEATURE [Part::Extrusion] Extrude034  label="caseScrewPillarBracket012"
  Base = -> Sketch043
  Dir = (0,0,1)
  DirMode = 2
  FaceMakerClass = Part::FaceMakerBullseye
  LengthFwd = 2.4
  LengthRev = 0
  Placement = pos=(88.3,29,65.23) rot=(0,1,0;1.5708rad)
  Solid = true
  Symmetric = false
FEATURE [Sketcher::SketchObject] Sketch044
  FullyConstrained = true
  sketch-geometry (7):
    g0: LineSegment StartX=0 StartY=0 StartZ=0 EndX=0 EndY=6 EndZ=0
    g1: Circle CenterX=0 CenterY=0 CenterZ=0 NormalX=0 NormalY=0 NormalZ=1 AngleXU=0 Radius=1
    g2: Circle CenterX=8 CenterY=6 CenterZ=0 NormalX=0 NormalY=0 NormalZ=1 AngleXU=0 Radius=1
    g3: BSplineCurve PolesCount=3 KnotsCount=2 Degree=2 IsPeriodic=0
    g4: GeomPoint X=0 Y=0 Z=0
    g5: GeomPoint X=8 Y=6 Z=0
    g6: LineSegment StartX=0 StartY=6 StartZ=0 EndX=8 EndY=6 EndZ=0
  constraints (14):
    c: Coincident(g0,g-1)
    c: Distance(g0) = 6
    c: Vertical(g0)
    c: Coincident(g3,g0)
    c: Weight(g1) = 1
    c: Equal(g1,g2)
    c: InternalAlignment(g1,g3)
    c: InternalAlignment(g2,g3)
    c: InternalAlignment(g4,g3)
    c: InternalAlignment(g5,g3)
    c: Block(g3)
    c: Coincident(g6,g0)
    c: Coincident(g6,g3)
    c: Horizontal(g6)
FEATURE [Part::Extrusion] Extrude035  label="caseScrewPillarBracket013"
  Base = -> Sketch044
  Dir = (0,0,1)
  DirMode = 2
  FaceMakerClass = Part::FaceMakerBullseye
  LengthFwd = 2.4
  LengthRev = 0
  Placement = pos=(90.7,29,6.77) rot=(0,-1,0;1.5708rad)
  Solid = true
  Symmetric = false
FEATURE [Sketcher::SketchObject] Sketch045
  FullyConstrained = true
  sketch-geometry (7):
    g0: LineSegment StartX=0 StartY=0 StartZ=0 EndX=0 EndY=6 EndZ=0
    g1: Circle CenterX=0 CenterY=0 CenterZ=0 NormalX=0 NormalY=0 NormalZ=1 AngleXU=0 Radius=1
    g2: Circle CenterX=8 CenterY=6 CenterZ=0 NormalX=0 NormalY=0 NormalZ=1 AngleXU=0 Radius=1
    g3: BSplineCurve PolesCount=3 KnotsCount=2 Degree=2 IsPeriodic=0
    g4: GeomPoint X=0 Y=0 Z=0
    g5: GeomPoint X=8 Y=6 Z=0
    g6: LineSegment StartX=0 StartY=6 StartZ=0 EndX=8 EndY=6 EndZ=0
  constraints (14):
    c: Coincident(g0,g-1)
    c: Distance(g0) = 6
    c: Vertical(g0)
    c: Coincident(g3,g0)
    c: Weight(g1) = 1
    c: Equal(g1,g2)
    c: InternalAlignment(g1,g3)
    c: InternalAlignment(g2,g3)
    c: InternalAlignment(g4,g3)
    c: InternalAlignment(g5,g3)
    c: Block(g3)
    c: Coincident(g6,g0)
    c: Coincident(g6,g3)
    c: Horizontal(g6)
FEATURE [Sketcher::SketchObject] Sketch046
  FullyConstrained = true
  sketch-geometry (7):
    g0: LineSegment StartX=0 StartY=0 StartZ=0 EndX=0 EndY=6 EndZ=0
    g1: Circle CenterX=0 CenterY=0 CenterZ=0 NormalX=0 NormalY=0 NormalZ=1 AngleXU=0 Radius=1
    g2: Circle CenterX=8 CenterY=6 CenterZ=0 NormalX=0 NormalY=0 NormalZ=1 AngleXU=0 Radius=1
    g3: BSplineCurve PolesCount=3 KnotsCount=2 Degree=2 IsPeriodic=0
    g4: GeomPoint X=0 Y=0 Z=0
    g5: GeomPoint X=8 Y=6 Z=0
    g6: LineSegment StartX=0 StartY=6 StartZ=0 EndX=8 EndY=6 EndZ=0
  constraints (14):
    c: Coincident(g0,g-1)
    c: Distance(g0) = 6
    c: Vertical(g0)
    c: Coincident(g3,g0)
    c: Weight(g1) = 1
    c: Equal(g1,g2)
    c: InternalAlignment(g1,g3)
    c: InternalAlignment(g2,g3)
    c: InternalAlignment(g4,g3)
    c: InternalAlignment(g5,g3)
    c: Block(g3)
    c: Coincident(g6,g0)
    c: Coincident(g6,g3)
    c: Horizontal(g6)
FEATURE [Part::Extrusion] Extrude036  label="caseScrewPillarBracket014"
  Base = -> Sketch045
  Dir = (0,0,1)
  DirMode = 2
  FaceMakerClass = Part::FaceMakerBullseye
  LengthFwd = 2.4
  LengthRev = 0
  Placement = pos=(110.7,29,6.77) rot=(0,-1,0;1.5708rad)
  Solid = true
  Symmetric = false
FEATURE [Part::Extrusion] Extrude037  label="caseScrewPillarBracket015"
  Base = -> Sketch046
  Dir = (0,0,1)
  DirMode = 2
  FaceMakerClass = Part::FaceMakerBullseye
  LengthFwd = 2.4
  LengthRev = 0
  Placement = pos=(108.3,29,65.23) rot=(0,1,0;1.5708rad)
  Solid = true
  Symmetric = false
FEATURE [Part::Box] Box013  label="frontCaseScrewPillarBracket002"
  AttacherType = Attacher::AttachEngine3D
  Height = 2.4
  Length = 22
  Placement = pos=(87,28,2.3) rot=(0,0,1;0rad)
  Width = 7
FEATURE [Part::Box] Box014  label="frontCaseScrewPillarBracket003"
  AttacherType = Attacher::AttachEngine3D
  Height = 2.4
  Length = 22
  Placement = pos=(87,28,67.3) rot=(0,0,1;0rad)
  Width = 7
FEATURE [Part::Feature] Face087
  shape: bbox 4.8 x 30.2 x 2e-07 mm, 1 faces, 0 solids (baked)
FEATURE [Part::Revolution] Revolve091  label="frontCaseScrewPost004"
  Angle = 360
  Axis = (0,1,0)
  Base = (0,0,0)
  FaceMakerClass = Part::FaceMakerBullseye
  Placement = pos=(89.5,4.5,3.5) rot=(0,0,1;0rad)
  Solid = false
  Source = -> Face087
  Symmetric = false
FEATURE [Part::Feature] Face088
  shape: bbox 4.8 x 30.2 x 2e-07 mm, 1 faces, 0 solids (baked)
FEATURE [Part::Revolution] Revolve092  label="frontCaseScrewPost005"
  Angle = 360
  Axis = (0,1,0)
  Base = (0,0,0)
  FaceMakerClass = Part::FaceMakerBullseye
  Placement = pos=(89.5,4.5,68.5) rot=(0,0,1;0rad)
  Solid = false
  Source = -> Face088
  Symmetric = false
FEATURE [Part::Feature] Face089
  shape: bbox 3.5 x 30.2 x 2e-07 mm, 1 faces, 0 solids (baked)
FEATURE [Part::Revolution] Revolve093  label="backCaseScrewPost002"
  Angle = 360
  Axis = (0,1,0)
  Base = (0,0,0)
  FaceMakerClass = Part::FaceMakerBullseye
  Placement = pos=(12.5,4.5,10) rot=(0,0,1;0rad)
  Solid = false
  Source = -> Face089
  Symmetric = false
FEATURE [Part::Feature] Face090
  shape: bbox 3.5 x 30.2 x 2e-07 mm, 1 faces, 0 solids (baked)
FEATURE [Part::Revolution] Revolve094  label="backCaseScrewPost003"
  Angle = 360
  Axis = (0,1,0)
  Base = (0,0,0)
  FaceMakerClass = Part::FaceMakerBullseye
  Placement = pos=(12.5,4.5,62) rot=(0,0,1;0rad)
  Solid = false
  Source = -> Face090
  Symmetric = false
FEATURE [Part::Box] Box015  label="Cube011"
  AttacherType = Attacher::AttachEngine3D
  Height = 28.8
  Length = 3
  Placement = pos=(107.3,28,21.6) rot=(0,0,1;0rad)
  Width = 7
FEATURE [Part::Box] Box016  label="Cube012"
  AttacherType = Attacher::AttachEngine3D
  Height = 3
  Length = 7.4
  Placement = pos=(107.3,28,18.6) rot=(0,0,1;0rad)
  Width = 7
FEATURE [Part::Box] Box017  label="Cube013"
  AttacherType = Attacher::AttachEngine3D
  Height = 3
  Length = 7.4
  Placement = pos=(107.3,28,50.4) rot=(0,0,1;0rad)
  Width = 7
FEATURE [Part::Cylinder] Cylinder024
  Angle = 360
  AttacherType = Attacher::AttachEngine3D
  Height = 20
  Placement = pos=(0,0,36.15) rot=(0,0,1;0rad)
  Radius = 14.3
FEATURE [Part::Cylinder] Cylinder025
  Angle = 360
  AttacherType = Attacher::AttachEngine3D
  Height = 10
  Placement = pos=(0,0,36.15) rot=(0,0,1;0rad)
  Radius = 4
FEATURE [Part::MultiFuse] Fusion066  label="removeToCreteHoleForPlugHousing009"
  Placement = pos=(70,19,36) rot=(0,1,0;1.5708rad)
  Shapes = -> [Cylinder024,Cylinder025]
FEATURE [Part::MultiFuse] Fusion065  label="plugHousingBracketHolder002"
  Shapes = -> [Box017,Box015,Box016]
FEATURE [Part::Cut] Cut025  label="plugHousingBracketHolder003"
  Base = -> Fusion065
  Placement = pos=(7,0,0) rot=(0,0,1;0rad)
  Tool = -> Fusion066
FEATURE [Sketcher::SketchObject] Sketch047
  FullyConstrained = false
  Placement = pos=(0,0,0) rot=(1,0,0;1.5708rad)
  sketch-geometry (24):
    g0: ArcOfCircle CenterX=-4 CenterY=-10.5 CenterZ=0 NormalX=0 NormalY=0 NormalZ=1 AngleXU=0 Radius=1.5 StartAngle=6e-16 EndAngle=3.14159
    g1: ArcOfCircle CenterX=-34.2 CenterY=-10.5 CenterZ=0 NormalX=0 NormalY=0 NormalZ=1 AngleXU=0 Radius=1.5 StartAngle=0 EndAngle=3.14159
    g2: ArcOfCircle CenterX=-34.2 CenterY=-27.7 CenterZ=0 NormalX=0 NormalY=0 NormalZ=1 AngleXU=0 Radius=1.5 StartAngle=3.14159 EndAngle=6.28319
    g3: ArcOfCircle CenterX=-4 CenterY=-27.7 CenterZ=0 NormalX=0 NormalY=0 NormalZ=1 AngleXU=0 Radius=1.5 StartAngle=3.1416 EndAngle=6.28319
    g4: ArcOfCircle CenterX=-10 CenterY=-4.3 CenterZ=0 NormalX=0 NormalY=0 NormalZ=1 AngleXU=0 Radius=1.5 StartAngle=2e-16 EndAngle=3.14159
    g5: ArcOfCircle CenterX=-16.1 CenterY=-1.8 CenterZ=0 NormalX=0 NormalY=0 NormalZ=1 AngleXU=0 Radius=1.5 StartAngle=5e-16 EndAngle=3.14159
    g6: ArcOfCircle CenterX=-22.1 CenterY=-1.8 CenterZ=0 NormalX=0 NormalY=0 NormalZ=1 AngleXU=0 Radius=1.5 StartAngle=5e-16 EndAngle=3.14159
    g7: ArcOfCircle CenterX=-28.2 CenterY=-4.3 CenterZ=0 NormalX=0 NormalY=0 NormalZ=1 AngleXU=0 Radius=1.5 StartAngle=2e-16 EndAngle=3.14159
    g8: ArcOfCircle CenterX=-10 CenterY=-33.9 CenterZ=0 NormalX=0 NormalY=0 NormalZ=1 AngleXU=0 Radius=1.5 StartAngle=3.14159 EndAngle=6.28319
    g9: ArcOfCircle CenterX=-16.1 CenterY=-36.4 CenterZ=0 NormalX=0 NormalY=0 NormalZ=1 AngleXU=0 Radius=1.5 StartAngle=3.14159 EndAngle=6.28319
    g10: ArcOfCircle CenterX=-22.1 CenterY=-36.4 CenterZ=0 NormalX=0 NormalY=0 NormalZ=1 AngleXU=0 Radius=1.5 StartAngle=3.14159 EndAngle=6.28319
    g11: ArcOfCircle CenterX=-28.2 CenterY=-33.9 CenterZ=0 NormalX=0 NormalY=0 NormalZ=1 AngleXU=0 Radius=1.5 StartAngle=3.14159 EndAngle=6.28319
    g12: LineSegment StartX=-35.7 StartY=-10.5 StartZ=0 EndX=-35.7 EndY=-27.7 EndZ=0
    g13: LineSegment StartX=-32.7 StartY=-10.5 StartZ=0 EndX=-32.7 EndY=-27.7 EndZ=0
    g14: LineSegment StartX=-29.7 StartY=-33.9 StartZ=0 EndX=-29.7 EndY=-4.3 EndZ=0
    g15: LineSegment StartX=-26.7 StartY=-33.9 StartZ=0 EndX=-26.7 EndY=-4.3 EndZ=0
    g16: LineSegment StartX=-2.5 StartY=-10.5 StartZ=0 EndX=-2.5 EndY=-27.7 EndZ=0
    g17: LineSegment StartX=-8.5 StartY=-4.3 StartZ=0 EndX=-8.5 EndY=-33.9 EndZ=0
    g18: LineSegment StartX=-5.5 StartY=-10.5 StartZ=0 EndX=-5.5 EndY=-27.7 EndZ=0
    g19: LineSegment StartX=-11.5 StartY=-4.3 StartZ=0 EndX=-11.5 EndY=-33.9 EndZ=0
    g20: LineSegment StartX=-14.6 StartY=-1.8 StartZ=0 EndX=-14.6 EndY=-36.4 EndZ=0
    g21: LineSegment StartX=-17.6 StartY=-1.8 StartZ=0 EndX=-17.6 EndY=-36.4 EndZ=0
    g22: LineSegment StartX=-20.6 StartY=-36.4 StartZ=0 EndX=-20.6 EndY=-1.8 EndZ=0
    g23: LineSegment StartX=-23.6 StartY=-1.8 StartZ=0 EndX=-23.6 EndY=-36.4 EndZ=0
  constraints (48):
    c: Block(g0)
    c: Block(g1)
    c: Block(g2)
    c: Block(g3)
    c: Block(g4)
    c: Block(g5)
    c: Block(g6)
    c: Block(g7)
    c: Block(g8)
    c: Block(g9)
    c: Block(g10)
    c: Block(g11)
    c: Coincident(g12,g1)
    c: Coincident(g12,g2)
    c: Vertical(g12)
    c: Coincident(g13,g1)
    c: Coincident(g13,g2)
    c: Vertical(g13)
    c: Coincident(g14,g11)
    c: Coincident(g14,g7)
    c: Vertical(g14)
    c: Coincident(g15,g11)
    c: Coincident(g15,g7)
    c: Vertical(g15)
    c: Coincident(g16,g0)
    c: Coincident(g16,g3)
    c: Vertical(g16)
    c: Coincident(g17,g4)
    c: Coincident(g17,g8)
    c: Vertical(g17)
    c: Coincident(g18,g0)
    c: Coincident(g18,g3)
    c: Vertical(g18)
    c: Coincident(g19,g4)
    c: Coincident(g19,g8)
    c: Vertical(g19)
    c: Coincident(g20,g5)
    c: Coincident(g20,g9)
    c: Vertical(g20)
    c: Coincident(g21,g5)
    c: Coincident(g21,g9)
    c: Vertical(g21)
    c: Coincident(g22,g10)
    c: Coincident(g22,g6)
    c: Vertical(g22)
    c: Coincident(g23,g6)
    c: Coincident(g23,g10)
    c: Vertical(g23)
FEATURE [Part::Extrusion] Extrude038  label="removeToCreateFanGrillHoles001"
  Base = -> Sketch047
  Dir = (0,-1,6e-16)
  DirMode = 2
  FaceMakerClass = Part::FaceMakerBullseye
  LengthFwd = 10
  LengthRev = 0
  Placement = pos=(65.4,44,54.82) rot=(0,0,1;0rad)
  Solid = true
  Symmetric = false
FEATURE [Part::Feature] Wire004
  shape: bbox 11 x 5.2 x 2e-07 mm, 0 faces, 0 solids (baked)
FEATURE [Part::Revolution] Revolve095
  Angle = 360
  Axis = (0,1,0)
  Base = (0,0,0)
  FaceMakerClass = Part::FaceMakerBullseye
  Placement = pos=(30.3,38,19.7) rot=(0,0,1;0rad)
  Solid = true
  Source = -> Wire004
  Symmetric = false
FEATURE [Part::Feature] Wire005
  shape: bbox 11 x 5.2 x 2e-07 mm, 0 faces, 0 solids (baked)
FEATURE [Part::Revolution] Revolve096
  Angle = 360
  Axis = (0,1,0)
  Base = (0,0,0)
  FaceMakerClass = Part::FaceMakerBullseye
  Placement = pos=(30.3,38,51.7) rot=(0,0,1;0rad)
  Solid = true
  Source = -> Wire005
  Symmetric = false
FEATURE [Part::Feature] Wire006
  shape: bbox 11 x 5.2 x 2e-07 mm, 0 faces, 0 solids (baked)
FEATURE [Part::Revolution] Revolve097
  Angle = 360
  Axis = (0,1,0)
  Base = (0,0,0)
  FaceMakerClass = Part::FaceMakerBullseye
  Placement = pos=(62.3,38,51.7) rot=(0,0,1;0rad)
  Solid = true
  Source = -> Wire006
  Symmetric = false
FEATURE [Part::Feature] Wire007
  shape: bbox 11 x 5.2 x 2e-07 mm, 0 faces, 0 solids (baked)
FEATURE [Part::Revolution] Revolve098
  Angle = 360
  Axis = (0,1,0)
  Base = (0,0,0)
  FaceMakerClass = Part::FaceMakerBullseye
  Placement = pos=(62.3,38,19.7) rot=(0,0,1;0rad)
  Solid = true
  Source = -> Wire007
  Symmetric = false
FEATURE [Part::MultiFuse] Fusion067  label="fanScrewHousing002"
  Shapes = -> [Revolve098,Revolve097,Revolve096,Revolve095]
FEATURE [Part::Feature] Face091 .. Face094  x4 (patterned run collapsed; names and placements below)
  shape: bbox 3.5 x 17.8 x 2e-07 mm, 1 faces, 0 solids (baked)
FEATURE [Part::Revolution] Revolve099  label="removeToCreateScrewAndThreadedInsertHole026"
  Angle = 360
  Axis = (0,1,0)
  Base = (0,0,0)
  FaceMakerClass = Part::FaceMakerBullseye
  Placement = pos=(62.3,30.3,19.7) rot=(0,0,1;0rad)
  Solid = false
  Source = -> Face091
  Symmetric = false
FEATURE [Part::Revolution] Revolve100  label="removeToCreateScrewAndThreadedInsertHole027"
  Angle = 360
  Axis = (0,1,0)
  Base = (0,0,0)
  FaceMakerClass = Part::FaceMakerBullseye
  Placement = pos=(62.3,30.3,51.7) rot=(0,0,1;0rad)
  Solid = false
  Source = -> Face092
  Symmetric = false
FEATURE [Part::Revolution] Revolve101  label="removeToCreateScrewAndThreadedInsertHole028"
  Angle = 360
  Axis = (0,1,0)
  Base = (0,0,0)
  FaceMakerClass = Part::FaceMakerBullseye
  Placement = pos=(30.3,30.3,19.7) rot=(0,0,1;0rad)
  Solid = false
  Source = -> Face093
  Symmetric = false
FEATURE [Part::Revolution] Revolve102  label="removeToCreateScrewAndThreadedInsertHole029"
  Angle = 360
  Axis = (0,1,0)
  Base = (0,0,0)
  FaceMakerClass = Part::FaceMakerBullseye
  Placement = pos=(30.3,30.3,51.7) rot=(0,0,1;0rad)
  Solid = false
  Source = -> Face094
  Symmetric = false
FEATURE [Part::MultiFuse] Fusion068  label="createThreadedInsertHolesForFan002"
  Shapes = -> [Revolve099,Revolve100,Revolve101,Revolve102]
FEATURE [Part::Cut] Cut026  label="fanScrewHousing003"
  Base = -> Fusion067
  Tool = -> Fusion068
FEATURE [Sketcher::SketchObject] Sketch048
  FullyConstrained = false
  Placement = pos=(0,0,0) rot=(1,0,0;1.5708rad)
  sketch-geometry (24):
    g0: ArcOfCircle CenterX=-4 CenterY=-10.5 CenterZ=0 NormalX=0 NormalY=0 NormalZ=1 AngleXU=0 Radius=1.5 StartAngle=6e-16 EndAngle=3.14159
    g1: ArcOfCircle CenterX=-34.2 CenterY=-10.5 CenterZ=0 NormalX=0 NormalY=0 NormalZ=1 AngleXU=0 Radius=1.5 StartAngle=0 EndAngle=3.14159
    g2: ArcOfCircle CenterX=-34.2 CenterY=-27.7 CenterZ=0 NormalX=0 NormalY=0 NormalZ=1 AngleXU=0 Radius=1.5 StartAngle=3.14159 EndAngle=6.28319
    g3: ArcOfCircle CenterX=-4 CenterY=-27.7 CenterZ=0 NormalX=0 NormalY=0 NormalZ=1 AngleXU=0 Radius=1.5 StartAngle=3.1416 EndAngle=6.28319
    g4: ArcOfCircle CenterX=-10 CenterY=-4.3 CenterZ=0 NormalX=0 NormalY=0 NormalZ=1 AngleXU=0 Radius=1.5 StartAngle=2e-16 EndAngle=3.14159
    g5: ArcOfCircle CenterX=-16.1 CenterY=-1.8 CenterZ=0 NormalX=0 NormalY=0 NormalZ=1 AngleXU=0 Radius=1.5 StartAngle=5e-16 EndAngle=3.14159
    g6: ArcOfCircle CenterX=-22.1 CenterY=-1.8 CenterZ=0 NormalX=0 NormalY=0 NormalZ=1 AngleXU=0 Radius=1.5 StartAngle=5e-16 EndAngle=3.14159
    g7: ArcOfCircle CenterX=-28.2 CenterY=-4.3 CenterZ=0 NormalX=0 NormalY=0 NormalZ=1 AngleXU=0 Radius=1.5 StartAngle=2e-16 EndAngle=3.14159
    g8: ArcOfCircle CenterX=-10 CenterY=-33.9 CenterZ=0 NormalX=0 NormalY=0 NormalZ=1 AngleXU=0 Radius=1.5 StartAngle=3.14159 EndAngle=6.28319
    g9: ArcOfCircle CenterX=-16.1 CenterY=-36.4 CenterZ=0 NormalX=0 NormalY=0 NormalZ=1 AngleXU=0 Radius=1.5 StartAngle=3.14159 EndAngle=6.28319
    g10: ArcOfCircle CenterX=-22.1 CenterY=-36.4 CenterZ=0 NormalX=0 NormalY=0 NormalZ=1 AngleXU=0 Radius=1.5 StartAngle=3.14159 EndAngle=6.28319
    g11: ArcOfCircle CenterX=-28.2 CenterY=-33.9 CenterZ=0 NormalX=0 NormalY=0 NormalZ=1 AngleXU=0 Radius=1.5 StartAngle=3.14159 EndAngle=6.28319
    g12: LineSegment StartX=-35.7 StartY=-10.5 StartZ=0 EndX=-35.7 EndY=-27.7 EndZ=0
    g13: LineSegment StartX=-32.7 StartY=-10.5 StartZ=0 EndX=-32.7 EndY=-27.7 EndZ=0
    g14: LineSegment StartX=-29.7 StartY=-33.9 StartZ=0 EndX=-29.7 EndY=-4.3 EndZ=0
    g15: LineSegment StartX=-26.7 StartY=-33.9 StartZ=0 EndX=-26.7 EndY=-4.3 EndZ=0
    g16: LineSegment StartX=-2.5 StartY=-10.5 StartZ=0 EndX=-2.5 EndY=-27.7 EndZ=0
    g17: LineSegment StartX=-8.5 StartY=-4.3 StartZ=0 EndX=-8.5 EndY=-33.9 EndZ=0
    g18: LineSegment StartX=-5.5 StartY=-10.5 StartZ=0 EndX=-5.5 EndY=-27.7 EndZ=0
    g19: LineSegment StartX=-11.5 StartY=-4.3 StartZ=0 EndX=-11.5 EndY=-33.9 EndZ=0
    g20: LineSegment StartX=-14.6 StartY=-1.8 StartZ=0 EndX=-14.6 EndY=-36.4 EndZ=0
    g21: LineSegment StartX=-17.6 StartY=-1.8 StartZ=0 EndX=-17.6 EndY=-36.4 EndZ=0
    g22: LineSegment StartX=-20.6 StartY=-36.4 StartZ=0 EndX=-20.6 EndY=-1.8 EndZ=0
    g23: LineSegment StartX=-23.6 StartY=-1.8 StartZ=0 EndX=-23.6 EndY=-36.4 EndZ=0
  constraints (48):
    c: Block(g0)
    c: Block(g1)
    c: Block(g2)
    c: Block(g3)
    c: Block(g4)
    c: Block(g5)
    c: Block(g6)
    c: Block(g7)
    c: Block(g8)
    c: Block(g9)
    c: Block(g10)
    c: Block(g11)
    c: Coincident(g12,g1)
    c: Coincident(g12,g2)
    c: Vertical(g12)
    c: Coincident(g13,g1)
    c: Coincident(g13,g2)
    c: Vertical(g13)
    c: Coincident(g14,g11)
    c: Coincident(g14,g7)
    c: Vertical(g14)
    c: Coincident(g15,g11)
    c: Coincident(g15,g7)
    c: Vertical(g15)
    c: Coincident(g16,g0)
    c: Coincident(g16,g3)
    c: Vertical(g16)
    c: Coincident(g17,g4)
    c: Coincident(g17,g8)
    c: Vertical(g17)
    c: Coincident(g18,g0)
    c: Coincident(g18,g3)
    c: Vertical(g18)
    c: Coincident(g19,g4)
    c: Coincident(g19,g8)
    c: Vertical(g19)
    c: Coincident(g20,g5)
    c: Coincident(g20,g9)
    c: Vertical(g20)
    c: Coincident(g21,g5)
    c: Coincident(g21,g9)
    c: Vertical(g21)
    c: Coincident(g22,g10)
    c: Coincident(g22,g6)
    c: Vertical(g22)
    c: Coincident(g23,g6)
    c: Coincident(g23,g10)
    c: Vertical(g23)
FEATURE [Part::Extrusion] Extrude039  label="removeToCreateFanGrillHoles002"
  Base = -> Sketch048
  Dir = (0,-1,6e-16)
  DirMode = 2
  FaceMakerClass = Part::FaceMakerBullseye
  LengthFwd = 10
  LengthRev = 0
  Placement = pos=(65.4,44,54.82) rot=(0,0,1;0rad)
  Solid = true
  Symmetric = false
FEATURE [Part::Cut] Cut027  label="fanScrewHousing004"
  Base = -> Cut026
  Tool = -> Extrude038
FEATURE [Part::Cut] Cut028  label="top014"
  Base = -> Fillet026
  Tool = -> Extrude039
FEATURE [Part::Feature] Face095 .. Face098  x4 (patterned run collapsed; names and placements below)
  shape: bbox 3.5 x 17.8 x 2e-07 mm, 1 faces, 0 solids (baked)
FEATURE [Part::Revolution] Revolve103  label="removeToCreateScrewAndThreadedInsertHole030"
  Angle = 360
  Axis = (0,1,0)
  Base = (0,0,0)
  FaceMakerClass = Part::FaceMakerBullseye
  Placement = pos=(62.3,30.3,19.7) rot=(0,0,1;0rad)
  Solid = false
  Source = -> Face095
  Symmetric = false
FEATURE [Part::Revolution] Revolve104  label="removeToCreateScrewAndThreadedInsertHole031"
  Angle = 360
  Axis = (0,1,0)
  Base = (0,0,0)
  FaceMakerClass = Part::FaceMakerBullseye
  Placement = pos=(62.3,30.3,51.7) rot=(0,0,1;0rad)
  Solid = false
  Source = -> Face096
  Symmetric = false
FEATURE [Part::Revolution] Revolve105  label="removeToCreateScrewAndThreadedInsertHole032"
  Angle = 360
  Axis = (0,1,0)
  Base = (0,0,0)
  FaceMakerClass = Part::FaceMakerBullseye
  Placement = pos=(30.3,30.3,19.7) rot=(0,0,1;0rad)
  Solid = false
  Source = -> Face097
  Symmetric = false
FEATURE [Part::Revolution] Revolve106  label="removeToCreateScrewAndThreadedInsertHole033"
  Angle = 360
  Axis = (0,1,0)
  Base = (0,0,0)
  FaceMakerClass = Part::FaceMakerBullseye
  Placement = pos=(30.3,30.3,51.7) rot=(0,0,1;0rad)
  Solid = false
  Source = -> Face098
  Symmetric = false
FEATURE [Part::MultiFuse] Fusion069  label="createThreadedInsertHolesForFan003"
  Shapes = -> [Revolve103,Revolve104,Revolve105,Revolve106]
FEATURE [Part::Cut] Cut029  label="top015"
  Base = -> Cut028
  Tool = -> Fusion054
FEATURE [Part::Cut] Cut030  label="fanScrewHousing005"
  Base = -> Cut027
  Tool = -> Fusion069
FEATURE [Part::Cylinder] Cylinder026  label="removeToCreteHoleForPlugHousing010"
  Angle = 360
  AttacherType = Attacher::AttachEngine3D
  Height = 20
  Placement = pos=(-2,19,36) rot=(0,1,0;1.5708rad)
  Radius = 14.3
FEATURE [Part::Box] Box018  label="removeToCreteHoleForPlugHousing011"
  AttacherType = Attacher::AttachEngine3D
  Height = 28.6
  Length = 10
  Placement = pos=(-2,0,21.7) rot=(0,0,1;0rad)
  Width = 19
FEATURE [Part::Box] Box019  label="wireHolderBottomCaseBit"
  AttacherType = Attacher::AttachEngine3D
  Height = 28
  Length = 3
  Placement = pos=(0,0,22) rot=(0,0,1;0rad)
  Width = 21
FEATURE [Part::Cylinder] Cylinder027  label="removeToCreteHoleForPlugHousing012"
  Angle = 360
  AttacherType = Attacher::AttachEngine3D
  Height = 20
  Placement = pos=(-2,19,36) rot=(0,1,0;1.5708rad)
  Radius = 14.3
FEATURE [Part::Cut] Cut031  label="wireHolderBottomCaseBit001"
  Base = -> Box019
  Tool = -> Cylinder027
FEATURE [Part::MultiFuse] Fusion070  label="removeToCreteHoleForPlugHousing013"
  Shapes = -> [Box018,Cylinder026]
FEATURE [Part::Cut] Cut032  label="top016"
  Base = -> Cut029
  Tool = -> Fusion070
FEATURE [Part::Cylinder] Cylinder028
  Angle = 360
  AttacherType = Attacher::AttachEngine3D
  Height = 20
  Placement = pos=(0,0,36.15) rot=(0,0,1;0rad)
  Radius = 14.3
FEATURE [Part::Cylinder] Cylinder029
  Angle = 360
  AttacherType = Attacher::AttachEngine3D
  Height = 10
  Placement = pos=(0,0,36.15) rot=(0,0,1;0rad)
  Radius = 4
FEATURE [Part::MultiFuse] Fusion071  label="removeToCreteHoleForPlugHousing014"
  Placement = pos=(70,19,36) rot=(0,1,0;1.5708rad)
  Shapes = -> [Cylinder028,Cylinder029]
FEATURE [Sketcher::SketchObject] Sketch049  label="topSketch011"
  FullyConstrained = true
  sketch-geometry (4):
    g0: ArcOfCircle CenterX=105 CenterY=19 CenterZ=0 NormalX=0 NormalY=0 NormalZ=1 AngleXU=0 Radius=20.6155 StartAngle=5.54125 EndAngle=6.28319
    g1: ArcOfCircle CenterX=105 CenterY=19 CenterZ=0 NormalX=0 NormalY=0 NormalZ=1 AngleXU=0 Radius=13 StartAngle=5.54125 EndAngle=6.28319
    g2: LineSegment StartX=118 StartY=19 StartZ=0 EndX=125.616 EndY=19 EndZ=0
    g3: LineSegment StartX=114.583 StartY=10.2157 StartZ=0 EndX=120.197 EndY=5.06982 EndZ=0
  constraints (7):
    c: Block(g0)
    c: Block(g1)
    c: Coincident(g2,g1)
    c: Coincident(g2,g0)
    c: Horizontal(g2)
    c: Coincident(g3,g1)
    c: Coincident(g3,g0)
FEATURE [Part::Box] Box020  label="removeToCreteHoleForPlugHousing015"
  AttacherType = Attacher::AttachEngine3D
  Height = 28.6
  Length = 20
  Placement = pos=(106.15,0,21.7) rot=(0,0,1;0rad)
  Width = 19
FEATURE [Part::MultiFuse] Fusion072  label="removeToCreteHoleForPlugHousing016"
  Shapes = -> [Box020,Fusion071]
FEATURE [Part::Cut] Cut033  label="removeToCreteHoleForPlugHousing017"
  Base = -> Cut032
  Tool = -> Fusion072
FEATURE [Part::Cylinder] Cylinder030
  Angle = 360
  AttacherType = Attacher::AttachEngine3D
  Height = 20
  Placement = pos=(0,0,36.15) rot=(0,0,1;0rad)
  Radius = 14.3
FEATURE [Part::Cylinder] Cylinder031
  Angle = 360
  AttacherType = Attacher::AttachEngine3D
  Height = 10
  Placement = pos=(0,0,36.15) rot=(0,0,1;0rad)
  Radius = 4
FEATURE [Part::Box] Box021  label="removeToCreteHoleForPlugHousing019"
  AttacherType = Attacher::AttachEngine3D
  Height = 28.6
  Length = 20
  Placement = pos=(106.15,0,21.7) rot=(0,0,1;0rad)
  Width = 19
FEATURE [Part::MultiFuse] Fusion074  label="removeToCreteHoleForPlugHousing020"
  Placement = pos=(70,19,36) rot=(0,1,0;1.5708rad)
  Shapes = -> [Cylinder030,Cylinder031]
FEATURE [Part::MultiFuse] Fusion073  label="removeToCreteHoleForPlugHousing018"
  Placement = pos=(0,0,28.3) rot=(0,0,1;0rad)
  Shapes = -> [Box021,Fusion074]
FEATURE [Part::Cylinder] Cylinder032
  Angle = 360
  AttacherType = Attacher::AttachEngine3D
  Height = 20
  Placement = pos=(0,0,36.15) rot=(0,0,1;0rad)
  Radius = 14.3
FEATURE [Part::Cylinder] Cylinder033
  Angle = 360
  AttacherType = Attacher::AttachEngine3D
  Height = 10
  Placement = pos=(0,0,36.15) rot=(0,0,1;0rad)
  Radius = 4
FEATURE [Part::Box] Box022  label="removeToCreteHoleForPlugHousing021"
  AttacherType = Attacher::AttachEngine3D
  Height = 28.6
  Length = 20
  Placement = pos=(106.15,0,21.7) rot=(0,0,1;0rad)
  Width = 19
FEATURE [Part::MultiFuse] Fusion076  label="removeToCreteHoleForPlugHousing023"
  Placement = pos=(70,19,36) rot=(0,1,0;1.5708rad)
  Shapes = -> [Cylinder032,Cylinder033]
FEATURE [Part::MultiFuse] Fusion075  label="removeToCreteHoleForPlugHousing022"
  Placement = pos=(0,0,-28.3) rot=(0,0,1;0rad)
  Shapes = -> [Box022,Fusion076]
FEATURE [Part::MultiFuse] Fusion077  label="removeToCreatePlugHousingBottomBit"
  Shapes = -> [Fusion075,Fusion073]
FEATURE [Part::Cylinder] Cylinder034
  Angle = 360
  AttacherType = Attacher::AttachEngine3D
  Height = 20
  Placement = pos=(0,0,36.15) rot=(0,0,1;0rad)
  Radius = 14
FEATURE [Part::Cylinder] Cylinder035
  Angle = 360
  AttacherType = Attacher::AttachEngine3D
  Height = 10
  Placement = pos=(0,0,36.15) rot=(0,0,1;0rad)
  Radius = 4
FEATURE [Part::MultiFuse] Fusion078  label="removeToCreteHoleForPlugHousing024"
  Placement = pos=(70,19,36) rot=(0,1,0;1.5708rad)
  Shapes = -> [Cylinder034,Cylinder035]
FEATURE [Part::MultiFuse] Fusion079  label="removeToCreatePlugHousingBottomBit001"
  Shapes = -> [Fusion078,Fusion077]
FEATURE [Part::Extrusion] Extrude040  label="bottomPlugHousingBit"
  Base = -> Sketch049
  Dir = (0,0,1)
  DirMode = 2
  FaceMakerClass = Part::FaceMakerBullseye
  LengthFwd = 72
  LengthRev = 0
  Solid = true
  Symmetric = false
FEATURE [Part::Cut] Cut034  label="bottomPlugHousingBit001"
  Base = -> Extrude040
  Placement = pos=(-0.09,0,0) rot=(0,0,1;0rad)
  Tool = -> Fusion079
FEATURE [Part::Box] Box023  label="Cube014"
  AttacherType = Attacher::AttachEngine3D
  Height = 16
  Length = 8
  Placement = pos=(12.7,31.52,28) rot=(0,0,1;0rad)
  Width = 4
FEATURE [Part::Cylinder] Cylinder036
  Angle = 360
  AttacherType = Attacher::AttachEngine3D
  Height = 10
  Placement = pos=(0,0,36.15) rot=(0,0,1;0rad)
  Radius = 4
FEATURE [Part::Cylinder] Cylinder037
  Angle = 360
  AttacherType = Attacher::AttachEngine3D
  Height = 20
  Placement = pos=(0,0,36.15) rot=(0,0,1;0rad)
  Radius = 8.2
FEATURE [Part::MultiFuse] Fusion080  label="removeToCreteHoleForPlugHousing025"
  Placement = pos=(-42,19,36) rot=(0,1,0;1.5708rad)
  Shapes = -> [Cylinder037,Cylinder036]
FEATURE [Sketcher::SketchObject] Sketch050  label="topSketch012"
  FullyConstrained = true
  sketch-geometry (4):
    g0: LineSegment StartX=16.8446 StartY=31.512 StartZ=0 EndX=16.3251 EndY=34.4666 EndZ=0
    g1: ArcOfCircle CenterX=19 CenterY=19.2524 CenterZ=0 NormalX=0 NormalY=0 NormalZ=1 AngleXU=0 Radius=15.4476 StartAngle=1.74483 EndAngle=2.72717
    g2: ArcOfCircle CenterX=19 CenterY=19.2524 CenterZ=0 NormalX=0 NormalY=0 NormalZ=1 AngleXU=0 Radius=12.4476 StartAngle=1.74483 EndAngle=2.73189
    g3: LineSegment StartX=4.86004 StartY=25.4725 StartZ=0 EndX=7.58253 EndY=24.2107 EndZ=0
  constraints (7):
    c: Block(g0)
    c: Coincident(g1,g0)
    c: Coincident(g2,g0)
    c: Coincident(g3,g1)
    c: Coincident(g3,g2)
    c: Block(g1)
    c: Block(g2)
FEATURE [Part::Extrusion] Extrude041
  Base = -> Sketch050
  Dir = (0,0,1)
  DirMode = 2
  FaceMakerClass = Part::FaceMakerBullseye
  LengthFwd = 10.6
  LengthRev = 0
  Placement = pos=(0,0,31) rot=(0,0,1;0rad)
  Solid = true
  Symmetric = false
FEATURE [Part::Cut] Cut035
  Base = -> Extrude041
  Placement = pos=(0,0,-0.3) rot=(0,0,1;0rad)
  Tool = -> Fusion080
FEATURE [Part::Cut] Cut036
  Base = -> Box023
  Tool = -> Cut035
FEATURE [Part::Fillet] Fillet027
  Base = -> Cut036
  Edges = 1 edges r=0.7: [Edge13]
FEATURE [Part::Fillet] Fillet028
  Base = -> Fillet027
  Edges = 1 edges r=0.7: [Edge13]
FEATURE [Part::Fillet] Fillet029
  Base = -> Fillet028
  Edges = 1 edges r=0.7: [Edge16]
FEATURE [Part::Fillet] Fillet030
  Base = -> Fillet029
  Edges = 1 edges r=0.7: [Edge11]
FEATURE [Part::Fillet] Fillet031
  Base = -> Fillet030
  Edges = 1 edges r=0.7: [Edge10]
FEATURE [Part::Fillet] Fillet032
  Base = -> Fillet031
  Edges = 1 edges r=1.2: [Edge5]
FEATURE [Part::Fillet] Fillet033
  Base = -> Fillet032
  Edges = 1 edges r=1.2: [Edge12]
FEATURE [Part::Fillet] Fillet034  label="wireHousingRetainer"
  Base = -> Fillet033
  Edges = 1 edges r=2: [Edge1]
  Placement = pos=(0.3,0,0) rot=(0,0,1;0rad)
FEATURE [Part::Feature] Face099
  shape: bbox 3.5 x 17.8 x 2e-07 mm, 1 faces, 0 solids (baked)
FEATURE [Part::Revolution] Revolve107  label="removeToCreateScrewAndThreadedInsertHole034"
  Angle = 360
  Axis = (0,1,0)
  Base = (0,0,0)
  FaceMakerClass = Part::FaceMakerBullseye
  Placement = pos=(12.5,0,10) rot=(0,0,1;0rad)
  Solid = false
  Source = -> Face099
  Symmetric = false
FEATURE [Part::Feature] Face100
  shape: bbox 3.5 x 17.8 x 2e-07 mm, 1 faces, 0 solids (baked)
FEATURE [Part::Revolution] Revolve108  label="removeToCreateScrewAndThreadedInsertHole035"
  Angle = 360
  Axis = (0,1,0)
  Base = (0,0,0)
  FaceMakerClass = Part::FaceMakerBullseye
  Placement = pos=(12.5,0,62) rot=(0,0,1;0rad)
  Solid = false
  Source = -> Face100
  Symmetric = false
FEATURE [Part::Feature] Face101
  shape: bbox 3.5 x 17.8 x 2e-07 mm, 1 faces, 0 solids (baked)
FEATURE [Part::Revolution] Revolve109  label="removeToCreateScrewAndThreadedInsertHole036"
  Angle = 360
  Axis = (0,1,0)
  Base = (0,0,0)
  FaceMakerClass = Part::FaceMakerBullseye
  Placement = pos=(89.5,0,68.5) rot=(0,0,1;0rad)
  Solid = false
  Source = -> Face101
  Symmetric = false
FEATURE [Part::Feature] Face102
  shape: bbox 3.5 x 17.8 x 2e-07 mm, 1 faces, 0 solids (baked)
FEATURE [Part::Revolution] Revolve110  label="removeToCreateScrewAndThreadedInsertHole037"
  Angle = 360
  Axis = (0,1,0)
  Base = (0,0,0)
  FaceMakerClass = Part::FaceMakerBullseye
  Placement = pos=(89.5,0,3.5) rot=(0,0,1;0rad)
  Solid = false
  Source = -> Face102
  Symmetric = false
FEATURE [Part::Feature] Face103
  shape: bbox 3.5 x 17.8 x 2e-07 mm, 1 faces, 0 solids (baked)
FEATURE [Part::Revolution] Revolve111  label="removeToCreateScrewAndThreadedInsertHole038"
  Angle = 360
  Axis = (0,1,0)
  Base = (0,0,0)
  FaceMakerClass = Part::FaceMakerBullseye
  Placement = pos=(109.5,4.7,3.5) rot=(0,0,1;0rad)
  Solid = false
  Source = -> Face103
  Symmetric = false
FEATURE [Part::Feature] Face104
  shape: bbox 3.5 x 17.8 x 2e-07 mm, 1 faces, 0 solids (baked)
FEATURE [Part::Revolution] Revolve112  label="removeToCreateScrewAndThreadedInsertHole039"
  Angle = 360
  Axis = (0,1,0)
  Base = (0,0,0)
  FaceMakerClass = Part::FaceMakerBullseye
  Placement = pos=(109.5,4.7,68.5) rot=(0,0,1;0rad)
  Solid = false
  Source = -> Face104
  Symmetric = false
FEATURE [Part::MultiFuse] Fusion081  label="removeToCreateScrewAndThreadedInsertHole040"
  Shapes = -> [Revolve107,Revolve108,Revolve109,Revolve110,Revolve111,Revolve112]
FEATURE [Part::MultiFuse] Fusion082  label="casePillars002"
  Shapes = -> [Revolve094,Revolve092,Revolve090,Revolve089,Revolve091,Revolve093]
FEATURE [Part::Cut] Cut037  label="casePillars003"
  Base = -> Fusion082
  Tool = -> Fusion081
FEATURE [Sketcher::SketchObject] Sketch051
  FullyConstrained = true
  Placement = pos=(117,19,0) rot=(0.57735,0.57735,0.57735;2.0944rad)
  sketch-geometry (48):
    g0: LineSegment StartX=-49.19 StartY=69.25 StartZ=0 EndX=-49.19 EndY=66.25 EndZ=0
    g1: LineSegment StartX=-49.19 StartY=63.5 StartZ=0 EndX=-49.19 EndY=60.5 EndZ=0
    g2: LineSegment StartX=-49.19 StartY=57.75 StartZ=0 EndX=-49.19 EndY=54.75 EndZ=0
    g3: LineSegment StartX=-49.19 StartY=52 StartZ=0 EndX=-49.19 EndY=49 EndZ=0
    g4: LineSegment StartX=-49.19 StartY=46.25 StartZ=0 EndX=-49.19 EndY=43.25 EndZ=0
    g5: LineSegment StartX=-49.19 StartY=40.5 StartZ=0 EndX=-49.19 EndY=37.5 EndZ=0
    g6: LineSegment StartX=-49.19 StartY=34.5 StartZ=0 EndX=-49.19 EndY=31.5 EndZ=0
    g7: LineSegment StartX=-49.19 StartY=28.75 StartZ=0 EndX=-49.19 EndY=25.75 EndZ=0
    g8: LineSegment StartX=-49.19 StartY=23 StartZ=0 EndX=-49.19 EndY=20 EndZ=0
    g9: LineSegment StartX=-49.19 StartY=17.25 StartZ=0 EndX=-49.19 EndY=14.25 EndZ=0
    g10: LineSegment StartX=-49.19 StartY=11.5 StartZ=0 EndX=-49.19 EndY=8.5 EndZ=0
    g11: LineSegment StartX=-49.19 StartY=5.75 StartZ=0 EndX=-49.19 EndY=2.75 EndZ=0
    g12: ArcOfCircle CenterX=-1.5 CenterY=67.75 CenterZ=0 NormalX=0 NormalY=0 NormalZ=1 AngleXU=0 Radius=1.5 StartAngle=4.71239 EndAngle=7.85398
    g13: ArcOfCircle CenterX=-1.5 CenterY=62 CenterZ=0 NormalX=0 NormalY=0 NormalZ=1 AngleXU=0 Radius=1.5 StartAngle=4.71239 EndAngle=7.85398
    g14: ArcOfCircle CenterX=-1.5 CenterY=56.25 CenterZ=0 NormalX=0 NormalY=0 NormalZ=1 AngleXU=0 Radius=1.5 StartAngle=4.71239 EndAngle=7.85398
    g15: ArcOfCircle CenterX=-11.49 CenterY=50.5 CenterZ=0 NormalX=0 NormalY=0 NormalZ=1 AngleXU=0 Radius=1.5 StartAngle=4.71239 EndAngle=7.85398
    g16: ArcOfCircle CenterX=-16.28 CenterY=44.75 CenterZ=0 NormalX=0 NormalY=0 NormalZ=1 AngleXU=0 Radius=1.5 StartAngle=4.71239 EndAngle=7.85398
    g17: ArcOfCircle CenterX=-18.2337 CenterY=39 CenterZ=0 NormalX=0 NormalY=0 NormalZ=1 AngleXU=0 Radius=1.5 StartAngle=4.71485 EndAngle=7.85398
    g18: ArcOfCircle CenterX=-16.2837 CenterY=27.25 CenterZ=0 NormalX=0 NormalY=0 NormalZ=1 AngleXU=0 Radius=1.5 StartAngle=4.71485 EndAngle=7.85398
    g19: ArcOfCircle CenterX=-18.2337 CenterY=33 CenterZ=0 NormalX=0 NormalY=0 NormalZ=1 AngleXU=0 Radius=1.5 StartAngle=4.71485 EndAngle=7.85398
    g20: ArcOfCircle CenterX=-11.49 CenterY=21.5 CenterZ=0 NormalX=0 NormalY=0 NormalZ=1 AngleXU=0 Radius=1.5 StartAngle=4.71239 EndAngle=7.85398
    g21: ArcOfCircle CenterX=-1.5 CenterY=4.25 CenterZ=0 NormalX=0 NormalY=0 NormalZ=1 AngleXU=0 Radius=1.5 StartAngle=4.71239 EndAngle=7.85398
    g22: ArcOfCircle CenterX=-1.5 CenterY=10 CenterZ=0 NormalX=0 NormalY=0 NormalZ=1 AngleXU=0 Radius=1.5 StartAngle=4.71239 EndAngle=7.85398
    g23: ArcOfCircle CenterX=-1.5 CenterY=15.75 CenterZ=0 NormalX=0 NormalY=0 NormalZ=1 AngleXU=0 Radius=1.5 StartAngle=4.71239 EndAngle=7.85398
    g24: LineSegment StartX=-49.19 StartY=69.25 StartZ=0 EndX=-1.5 EndY=69.25 EndZ=0
    g25: LineSegment StartX=-49.19 StartY=66.25 StartZ=0 EndX=-1.5 EndY=66.25 EndZ=0
    g26: LineSegment StartX=-49.19 StartY=63.5 StartZ=0 EndX=-1.5 EndY=63.5 EndZ=0
    g27: LineSegment StartX=-49.19 StartY=60.5 StartZ=0 EndX=-1.5 EndY=60.5 EndZ=0
    g28: LineSegment StartX=-49.19 StartY=57.75 StartZ=0 EndX=-1.5 EndY=57.75 EndZ=0
    g29: LineSegment StartX=-49.19 StartY=54.75 StartZ=0 EndX=-1.5 EndY=54.75 EndZ=0
    g30: LineSegment StartX=-49.19 StartY=52 StartZ=0 EndX=-11.49 EndY=52 EndZ=0
    g31: LineSegment StartX=-49.19 StartY=49 StartZ=0 EndX=-11.49 EndY=49 EndZ=0
    g32: LineSegment StartX=-49.19 StartY=46.25 StartZ=0 EndX=-16.28 EndY=46.25 EndZ=0
    g33: LineSegment StartX=-49.19 StartY=43.25 StartZ=0 EndX=-16.28 EndY=43.25 EndZ=0
    g34: LineSegment StartX=-49.19 StartY=40.5 StartZ=0 EndX=-18.2337 EndY=40.5 EndZ=0
    g35: LineSegment StartX=-49.19 StartY=37.5 StartZ=0 EndX=-18.23 EndY=37.5 EndZ=0
    g36: LineSegment StartX=-49.19 StartY=34.5 StartZ=0 EndX=-18.2337 EndY=34.5 EndZ=0
    g37: LineSegment StartX=-49.19 StartY=31.5 StartZ=0 EndX=-18.23 EndY=31.5 EndZ=0
    g38: LineSegment StartX=-49.19 StartY=28.75 StartZ=0 EndX=-16.2837 EndY=28.75 EndZ=0
    g39: LineSegment StartX=-49.19 StartY=25.75 StartZ=0 EndX=-16.28 EndY=25.75 EndZ=0
    g40: LineSegment StartX=-49.19 StartY=23 StartZ=0 EndX=-11.49 EndY=23 EndZ=0
    g41: LineSegment StartX=-49.19 StartY=20 StartZ=0 EndX=-11.49 EndY=20 EndZ=0
    g42: LineSegment StartX=-49.19 StartY=17.25 StartZ=0 EndX=-1.5 EndY=17.25 EndZ=0
    g43: LineSegment StartX=-49.19 StartY=14.25 StartZ=0 EndX=-1.5 EndY=14.25 EndZ=0
    g44: LineSegment StartX=-49.19 StartY=11.5 StartZ=0 EndX=-1.5 EndY=11.5 EndZ=0
    g45: LineSegment StartX=-49.19 StartY=8.5 StartZ=0 EndX=-1.5 EndY=8.5 EndZ=0
    g46: LineSegment StartX=-49.19 StartY=5.75 StartZ=0 EndX=-1.5 EndY=5.75 EndZ=0
    g47: LineSegment StartX=-49.19 StartY=2.75 StartZ=0 EndX=-1.5 EndY=2.75 EndZ=0
  constraints (120):
    c: Vertical(g0)
    c: Distance(g0) = 3
    c: Block(g0)
    c: Vertical(g1)
    c: Distance(g1) = 3
    c: Vertical(g2)
    c: Equal(g0,g2) = 3
    c: Block(g2)
    c: Vertical(g3)
    c: Equal(g1,g3) = 3
    c: Vertical(g4)
    c: Equal(g0,g4) = 3
    c: Block(g4)
    c: Vertical(g5)
    c: Equal(g1,g5) = 3
    c: Vertical(g6)
    c: Equal(g0,g6) = 3
    c: Block(g6)
    c: Vertical(g7)
    c: Equal(g1,g7) = 3
    c: Vertical(g8)
    c: Equal(g0,g8) = 3
    c: Block(g8)
    c: Vertical(g9)
    c: Equal(g1,g9) = 3
    c: Vertical(g10)
    c: Equal(g0,g10) = 3
    c: Block(g10)
    c: Vertical(g11)
    c: Equal(g1,g11) = 3
    c: Block(g12)
    c: Block(g13)
    c: Block(g14)
    c: Block(g15)
    c: Block(g16)
    c: Block(g17)
    c: Block(g18)
    c: Block(g19)
    c: Block(g20)
    c: Block(g21)
    c: Block(g22)
    c: Block(g23)
    c: Block(g11)
    c: Block(g9)
    c: Block(g7)
    c: Block(g5)
    c: Block(g3)
    c: Block(g1)
    c: Coincident(g24,g0)
    c: Coincident(g24,g12)
    c: Horizontal(g24)
    c: Coincident(g25,g0)
    c: Coincident(g25,g12)
    c: Horizontal(g25)
    c: Coincident(g26,g1)
    c: Coincident(g26,g13)
    c: Horizontal(g26)
    c: Coincident(g27,g1)
    c: Coincident(g27,g13)
    c: Horizontal(g27)
    c: Coincident(g28,g2)
    c: Coincident(g28,g14)
    c: Horizontal(g28)
    c: Coincident(g29,g2)
    c: Coincident(g29,g14)
    c: Horizontal(g29)
    c: Coincident(g30,g3)
    c: Coincident(g30,g15)
    c: Horizontal(g30)
    c: Coincident(g31,g3)
    c: Coincident(g31,g15)
    c: Horizontal(g31)
    c: Coincident(g32,g4)
    c: Coincident(g32,g16)
    c: Horizontal(g32)
    c: Coincident(g33,g4)
    c: Coincident(g33,g16)
    c: Horizontal(g33)
    c: Coincident(g34,g5)
    c: Coincident(g34,g17)
    c: Horizontal(g34)
    c: Coincident(g35,g5)
    c: Coincident(g35,g17)
    c: Horizontal(g35)
    c: Coincident(g36,g6)
    c: Coincident(g36,g19)
    c: Horizontal(g36)
    c: Coincident(g37,g6)
    c: Coincident(g37,g19)
    c: Horizontal(g37)
    c: Coincident(g38,g7)
    c: Coincident(g38,g18)
    c: Horizontal(g38)
    c: Coincident(g39,g7)
    c: Coincident(g39,g18)
    c: Horizontal(g39)
    c: Coincident(g40,g8)
    c: Coincident(g40,g20)
    c: Horizontal(g40)
    c: Coincident(g41,g8)
    c: Coincident(g41,g20)
    c: Horizontal(g41)
    c: Coincident(g42,g9)
    c: Coincident(g42,g23)
    c: Horizontal(g42)
    c: Coincident(g43,g9)
    c: Coincident(g43,g23)
    c: Horizontal(g43)
    c: Coincident(g44,g10)
    c: Coincident(g44,g22)
    c: Horizontal(g44)
    c: Coincident(g45,g10)
    c: Coincident(g45,g22)
    c: Horizontal(g45)
    c: Coincident(g46,g11)
    c: Coincident(g46,g21)
    c: Horizontal(g46)
    c: Coincident(g47,g11)
    c: Coincident(g47,g21)
    c: Horizontal(g47)
FEATURE [Part::Extrusion] Extrude042
  Base = -> Sketch051
  Dir = (1,-2e-16,2e-16)
  DirMode = 2
  FaceMakerClass = Part::FaceMakerBullseye
  LengthFwd = 19
  LengthRev = 0
  Placement = pos=(-19,0,0) rot=(0,0,1;0rad)
  Solid = true
  Symmetric = false
FEATURE [Part::Fillet] Fillet035  label="removeToCreateVentalationHoles"
  Base = -> Extrude042
  Edges = <same value as first occurrence — deduplicated (x6 in doc)>
  Placement = pos=(7,0,0) rot=(0,0,1;0rad)
FEATURE [Part::Cut] Cut038  label="top017"
  Base = -> Cut033
  Tool = -> Fillet035
FEATURE [Sketcher::SketchObject] Sketch052  label="bottomSketch001"
  FullyConstrained = true
  sketch-geometry (45):
    g0: LineSegment StartX=6.29999 StartY=8 StartZ=0 EndX=3.29999 EndY=8 EndZ=0
    g1: LineSegment StartX=3.29999 StartY=8 StartZ=0 EndX=3.29999 EndY=-6.03275e-07 EndZ=0
    g2: ArcOfCircle CenterX=8.29999 CenterY=5 CenterZ=0 NormalX=0 NormalY=0 NormalZ=1 AngleXU=0 Radius=2 StartAngle=3.14159 EndAngle=4.71239
    g3: LineSegment StartX=6.29999 StartY=8 StartZ=0 EndX=6.29999 EndY=5 EndZ=0
    g4: ArcOfCircle CenterX=105 CenterY=19 CenterZ=0 NormalX=0 NormalY=0 NormalZ=1 AngleXU=0 Radius=12.7 StartAngle=4.71239 EndAngle=5.94289
    g5-g11: Circle x7 (B-spline internal-alignment scaffolding for g12; pole/knot coordinates omitted)
    g12: BSplineCurve PolesCount=7 KnotsCount=5 Degree=3 IsPeriodic=0
    g13-g17: GeomPoint x5 (B-spline internal-alignment scaffolding for g12; pole/knot coordinates omitted)
    g18: ArcOfCircle CenterX=105 CenterY=19 CenterZ=0 NormalX=0 NormalY=0 NormalZ=1 AngleXU=0 Radius=15.7 StartAngle=5.81226 EndAngle=6.28319
    g19: BSplineCurve PolesCount=5 KnotsCount=3 Degree=3 IsPeriodic=0
    g20: LineSegment StartX=8.29999 StartY=3 StartZ=0 EndX=101.7 EndY=3 EndZ=0
    g21: LineSegment StartX=3.29999 StartY=-6.03275e-07 StartZ=0 EndX=105 EndY=-6.03275e-07 EndZ=0
    g22: LineSegment StartX=120.974 StartY=8.71251 StartZ=0 EndX=122.332 EndY=7.83778 EndZ=0
    g23: LineSegment StartX=105 StartY=-6.03274e-07 StartZ=0 EndX=113 EndY=-6.03274e-07 EndZ=0
    g24: ArcOfCircle CenterX=105 CenterY=19 CenterZ=0 NormalX=0 NormalY=0 NormalZ=1 AngleXU=0 Radius=20.6155 StartAngle=5.11091 EndAngle=5.71103
    g25: ArcOfCircle CenterX=117.7 CenterY=19 CenterZ=0 NormalX=0 NormalY=0 NormalZ=1 AngleXU=0 Radius=3 StartAngle=1.2e-15 EndAngle=2.10468
    g26: Circle CenterX=116.345 CenterY=16.3232 CenterZ=0 NormalX=0 NormalY=0 NormalZ=1 AngleXU=0 Radius=1
    g27: Circle CenterX=117.24 CenterY=15.7584 CenterZ=0 NormalX=0 NormalY=0 NormalZ=1 AngleXU=0 Radius=1
    g28: Circle CenterX=116.972 CenterY=14.7612 CenterZ=0 NormalX=0 NormalY=0 NormalZ=1 AngleXU=0 Radius=1
    g29: BSplineCurve PolesCount=3 KnotsCount=2 Degree=2 IsPeriodic=0
    g30: GeomPoint X=116.345 Y=16.3232 Z=0
    g31: GeomPoint X=116.972 Y=14.7612 Z=0
    g32: Circle CenterX=115.828 CenterY=17.157 CenterZ=0 NormalX=0 NormalY=0 NormalZ=1 AngleXU=0 Radius=1
    g33: Circle CenterX=115.841 CenterY=16.639 CenterZ=0 NormalX=0 NormalY=0 NormalZ=1 AngleXU=0 Radius=1
    g34: Circle CenterX=116.345 CenterY=16.3232 CenterZ=0 NormalX=0 NormalY=0 NormalZ=1 AngleXU=0 Radius=1
    g35: BSplineCurve PolesCount=3 KnotsCount=2 Degree=2 IsPeriodic=0
    g36: GeomPoint X=115.828 Y=17.157 Z=0
    g37: GeomPoint X=116.345 Y=16.3232 Z=0
    g38: LineSegment StartX=115.828 StartY=17.157 StartZ=0 EndX=115.828 EndY=20.8307 EndZ=0
    g39: Circle CenterX=115.828 CenterY=20.8307 CenterZ=0 NormalX=0 NormalY=0 NormalZ=1 AngleXU=0 Radius=1
    g40: Circle CenterX=115.831 CenterY=21.3396 CenterZ=0 NormalX=0 NormalY=0 NormalZ=1 AngleXU=0 Radius=1
    g41: Circle CenterX=116.173 CenterY=21.5825 CenterZ=0 NormalX=0 NormalY=0 NormalZ=1 AngleXU=0 Radius=1
    g42: BSplineCurve PolesCount=3 KnotsCount=2 Degree=2 IsPeriodic=0
    g43: GeomPoint X=115.828 Y=20.8307 Z=0
    g44: GeomPoint X=116.173 Y=21.5825 Z=0
  constraints (70):
    c: Horizontal(g0)
    c: Distance(g0) = 3
    c: Coincident(g1,g0)
    c: Vertical(g1)
    c: Block(g2)
    c: Block(g0)
    c: Coincident(g3,g0)
    c: Coincident(g3,g2)
    c: Vertical(g3)
    c: Block(g1)
    c: Block(g4)
    c: Coincident(g19,g4)
    c: Block(g19)
    c: Equal(g5, g6-g11) x6
    c: InternalAlignment(g5-g11 -> g12) x7
    c: InternalAlignment(g13-g17 -> g12) x5
    c: Block(g12)
    c: Coincident(g18,g12)
    c: Block(g18)
    c: Coincident(g20,g2)
    c: Coincident(g20,g19)
    c: Horizontal(g20)
    c: Distance(g20) = 93.4
    c: Coincident(g21,g1)
    c: Horizontal(g21)
    c: Distance(g21) = 101.7
    c: Horizontal(g23)
    c: Distance(g23) = 8
    c: Coincident(g24,g23)
    c: Block(g23)
    c: Coincident(g22,g24)
    c: Block(g24)
    c: Block(g22)
    c: Distance(g22) = 1.61553
    c: Coincident(g25,g18)
    c: Block(g25)
    c: Weight(g26) = 1
    c: Equal(g26,g27)
    c: Equal(g26,g28)
    c: Coincident(g29,g4)
    c: InternalAlignment(g26,g29)
    c: InternalAlignment(g27,g29)
    c: InternalAlignment(g28,g29)
    c: InternalAlignment(g30,g29)
    c: InternalAlignment(g31,g29)
    c: Block(g29)
    c: Weight(g32) = 1
    c: Equal(g32,g33)
    c: Equal(g32,g34)
    c: Coincident(g35,g29)
    c: InternalAlignment(g32,g35)
    c: InternalAlignment(g33,g35)
    c: InternalAlignment(g34,g35)
    c: InternalAlignment(g36,g35)
    c: InternalAlignment(g37,g35)
    c: Block(g35)
    c: Coincident(g38,g35)
    c: Vertical(g38)
    c: Block(g38)
    c: Coincident(g42,g38)
    c: Weight(g39) = 1
    c: Equal(g39,g40)
    c: Equal(g39,g41)
    c: Coincident(g42,g25)
    c: InternalAlignment(g39,g42)
    c: InternalAlignment(g40,g42)
    c: InternalAlignment(g41,g42)
    c: InternalAlignment(g43,g42)
    c: InternalAlignment(g44,g42)
    c: Block(g42)
FEATURE [Part::Extrusion] Extrude043  label="bottom010"
  Base = -> Sketch052
  Dir = (0,0,1)
  DirMode = 2
  FaceMakerClass = Part::FaceMakerBullseye
  LengthFwd = 71.4
  LengthRev = 0
  Placement = pos=(0,0,0.3) rot=(0,0,1;0rad)
  Solid = true
  Symmetric = false
FEATURE [Sketcher::SketchObject] Sketch053  label="topSketch013"
  FullyConstrained = true
  sketch-geometry (22):
    g0: LineSegment StartX=5.21097e-06 StartY=3 StartZ=0 EndX=5.21097e-06 EndY=19 EndZ=0
    g1: ArcOfCircle CenterX=19 CenterY=19 CenterZ=0 NormalX=0 NormalY=0 NormalZ=1 AngleXU=0 Radius=19 StartAngle=1.5708 EndAngle=3.14159
    g2: ArcOfCircle CenterX=19 CenterY=19 CenterZ=0 NormalX=0 NormalY=0 NormalZ=1 AngleXU=0 Radius=16 StartAngle=1.5708 EndAngle=3.14159
    g3: LineSegment StartX=114 StartY=35 StartZ=0 EndX=19 EndY=35 EndZ=0
    g4: LineSegment StartX=5.21097e-06 StartY=3 StartZ=0 EndX=5.21097e-06 EndY=0 EndZ=0
    g5: LineSegment StartX=3 StartY=0 StartZ=0 EndX=5.21097e-06 EndY=0 EndZ=0
    g6: LineSegment StartX=3 StartY=19 StartZ=0 EndX=3 EndY=0 EndZ=0
    g7: LineSegment StartX=19 StartY=38 StartZ=0 EndX=124 EndY=38 EndZ=0
    g8: Circle CenterX=119 CenterY=35 CenterZ=0 NormalX=0 NormalY=0 NormalZ=1 AngleXU=0 Radius=1
    g9: Circle CenterX=121 CenterY=35 CenterZ=0 NormalX=0 NormalY=0 NormalZ=1 AngleXU=0 Radius=1
    g10: Circle CenterX=121 CenterY=33 CenterZ=0 NormalX=0 NormalY=0 NormalZ=1 AngleXU=0 Radius=1
    g11: BSplineCurve PolesCount=3 KnotsCount=2 Degree=2 IsPeriodic=0
    g12: GeomPoint X=119 Y=35 Z=0
    g13: GeomPoint X=121 Y=33 Z=0
    g14: LineSegment StartX=119 StartY=35 StartZ=0 EndX=114 EndY=35 EndZ=0
    g15: ArcOfCircle CenterX=105 CenterY=19 CenterZ=0 NormalX=0 NormalY=0 NormalZ=1 AngleXU=0 Radius=16 StartAngle=5.60905 EndAngle=6.28319
    g16: LineSegment StartX=121 StartY=33 StartZ=0 EndX=121 EndY=19 EndZ=0
    g17: LineSegment StartX=117.5 StartY=9.01251 StartZ=0 EndX=121.163 EndY=9.0125 EndZ=0
    g18: ArcOfCircle CenterX=105 CenterY=19 CenterZ=0 NormalX=0 NormalY=0 NormalZ=1 AngleXU=0 Radius=20.6155 StartAngle=5.7297 EndAngle=6.28319
    g19: LineSegment StartX=121.163 StartY=9.0125 StartZ=0 EndX=122.538 EndY=8.16329 EndZ=0
    g20: LineSegment StartX=124 StartY=38 StartZ=0 EndX=125.616 EndY=38 EndZ=0
    g21: LineSegment StartX=125.616 StartY=19 StartZ=0 EndX=125.616 EndY=38 EndZ=0
  constraints (50):
    c: Vertical(g0)
    c: Block(g0)
    c: Coincident(g1,g0)
    c: Block(g1)
    c: Coincident(g2,g1)
    c: Block(g2)
    c: Coincident(g3,g2)
    c: Horizontal(g3)
    c: Tangent(g3,g2)
    c: Coincident(g4,g0)
    c: Distance(g4) = 3
    c: Vertical(g4)
    c: Coincident(g5,g4)
    c: Horizontal(g5)
    c: Coincident(g6,g2)
    c: Coincident(g6,g5)
    c: Vertical(g6)
    c: Horizontal(g7)
    c: Distance(g7) = 105
    c: Coincident(g7,g1)
    c: Block(g3)
    c: Weight(g8) = 1
    c: Equal(g8,g9)
    c: Equal(g8,g10)
    c: InternalAlignment(g8,g11)
    c: InternalAlignment(g9,g11)
    c: InternalAlignment(g10,g11)
    c: InternalAlignment(g12,g11)
    c: InternalAlignment(g13,g11)
    c: Block(g11)
    c: Coincident(g14,g11)
    c: Coincident(g14,g3)
    c: Horizontal(g14)
    c: Block(g15)
    c: Coincident(g16,g11)
    c: Coincident(g16,g15)
    c: Vertical(g16)
    c: Distance(g16) = 14
    c: Coincident(g17,g15)
    c: Block(g18)
    c: Coincident(g19,g18)
    c: Coincident(g20,g7)
    c: Horizontal(g20)
    c: Vertical(g21)
    c: Coincident(g20,g21)
    c: Block(g20)
    c: Block(g21)
    c: Block(g19)
    c: Block(g17)
    c: Distance(g20) = 1.61553
FEATURE [Part::Extrusion] Extrude044
  Base = -> Sketch053
  Dir = (0,0,1)
  DirMode = 2
  FaceMakerClass = Part::FaceMakerBullseye
  LengthFwd = 72
  LengthRev = 0
  Solid = true
  Symmetric = false
FEATURE [Part::Fillet] Fillet036  label="top018"
  Base = -> Extrude044
  Edges = 1 edges r=2: [Edge41]
FEATURE [Sketcher::SketchObject] Sketch054
  FullyConstrained = false
  Placement = pos=(0,0,0) rot=(1,0,0;1.5708rad)
  sketch-geometry (24):
    g0: ArcOfCircle CenterX=-4 CenterY=-10.5 CenterZ=0 NormalX=0 NormalY=0 NormalZ=1 AngleXU=0 Radius=1.5 StartAngle=6e-16 EndAngle=3.14159
    g1: ArcOfCircle CenterX=-34.2 CenterY=-10.5 CenterZ=0 NormalX=0 NormalY=0 NormalZ=1 AngleXU=0 Radius=1.5 StartAngle=0 EndAngle=3.14159
    g2: ArcOfCircle CenterX=-34.2 CenterY=-27.7 CenterZ=0 NormalX=0 NormalY=0 NormalZ=1 AngleXU=0 Radius=1.5 StartAngle=3.14159 EndAngle=6.28319
    g3: ArcOfCircle CenterX=-4 CenterY=-27.7 CenterZ=0 NormalX=0 NormalY=0 NormalZ=1 AngleXU=0 Radius=1.5 StartAngle=3.1416 EndAngle=6.28319
    g4: ArcOfCircle CenterX=-10 CenterY=-4.3 CenterZ=0 NormalX=0 NormalY=0 NormalZ=1 AngleXU=0 Radius=1.5 StartAngle=2e-16 EndAngle=3.14159
    g5: ArcOfCircle CenterX=-16.1 CenterY=-1.8 CenterZ=0 NormalX=0 NormalY=0 NormalZ=1 AngleXU=0 Radius=1.5 StartAngle=5e-16 EndAngle=3.14159
    g6: ArcOfCircle CenterX=-22.1 CenterY=-1.8 CenterZ=0 NormalX=0 NormalY=0 NormalZ=1 AngleXU=0 Radius=1.5 StartAngle=5e-16 EndAngle=3.14159
    g7: ArcOfCircle CenterX=-28.2 CenterY=-4.3 CenterZ=0 NormalX=0 NormalY=0 NormalZ=1 AngleXU=0 Radius=1.5 StartAngle=2e-16 EndAngle=3.14159
    g8: ArcOfCircle CenterX=-10 CenterY=-33.9 CenterZ=0 NormalX=0 NormalY=0 NormalZ=1 AngleXU=0 Radius=1.5 StartAngle=3.14159 EndAngle=6.28319
    g9: ArcOfCircle CenterX=-16.1 CenterY=-36.4 CenterZ=0 NormalX=0 NormalY=0 NormalZ=1 AngleXU=0 Radius=1.5 StartAngle=3.14159 EndAngle=6.28319
    g10: ArcOfCircle CenterX=-22.1 CenterY=-36.4 CenterZ=0 NormalX=0 NormalY=0 NormalZ=1 AngleXU=0 Radius=1.5 StartAngle=3.14159 EndAngle=6.28319
    g11: ArcOfCircle CenterX=-28.2 CenterY=-33.9 CenterZ=0 NormalX=0 NormalY=0 NormalZ=1 AngleXU=0 Radius=1.5 StartAngle=3.14159 EndAngle=6.28319
    g12: LineSegment StartX=-35.7 StartY=-10.5 StartZ=0 EndX=-35.7 EndY=-27.7 EndZ=0
    g13: LineSegment StartX=-32.7 StartY=-10.5 StartZ=0 EndX=-32.7 EndY=-27.7 EndZ=0
    g14: LineSegment StartX=-29.7 StartY=-33.9 StartZ=0 EndX=-29.7 EndY=-4.3 EndZ=0
    g15: LineSegment StartX=-26.7 StartY=-33.9 StartZ=0 EndX=-26.7 EndY=-4.3 EndZ=0
    g16: LineSegment StartX=-2.5 StartY=-10.5 StartZ=0 EndX=-2.5 EndY=-27.7 EndZ=0
    g17: LineSegment StartX=-8.5 StartY=-4.3 StartZ=0 EndX=-8.5 EndY=-33.9 EndZ=0
    g18: LineSegment StartX=-5.5 StartY=-10.5 StartZ=0 EndX=-5.5 EndY=-27.7 EndZ=0
    g19: LineSegment StartX=-11.5 StartY=-4.3 StartZ=0 EndX=-11.5 EndY=-33.9 EndZ=0
    g20: LineSegment StartX=-14.6 StartY=-1.8 StartZ=0 EndX=-14.6 EndY=-36.4 EndZ=0
    g21: LineSegment StartX=-17.6 StartY=-1.8 StartZ=0 EndX=-17.6 EndY=-36.4 EndZ=0
    g22: LineSegment StartX=-20.6 StartY=-36.4 StartZ=0 EndX=-20.6 EndY=-1.8 EndZ=0
    g23: LineSegment StartX=-23.6 StartY=-1.8 StartZ=0 EndX=-23.6 EndY=-36.4 EndZ=0
  constraints (48):
    c: Block(g0)
    c: Block(g1)
    c: Block(g2)
    c: Block(g3)
    c: Block(g4)
    c: Block(g5)
    c: Block(g6)
    c: Block(g7)
    c: Block(g8)
    c: Block(g9)
    c: Block(g10)
    c: Block(g11)
    c: Coincident(g12,g1)
    c: Coincident(g12,g2)
    c: Vertical(g12)
    c: Coincident(g13,g1)
    c: Coincident(g13,g2)
    c: Vertical(g13)
    c: Coincident(g14,g11)
    c: Coincident(g14,g7)
    c: Vertical(g14)
    c: Coincident(g15,g11)
    c: Coincident(g15,g7)
    c: Vertical(g15)
    c: Coincident(g16,g0)
    c: Coincident(g16,g3)
    c: Vertical(g16)
    c: Coincident(g17,g4)
    c: Coincident(g17,g8)
    c: Vertical(g17)
    c: Coincident(g18,g0)
    c: Coincident(g18,g3)
    c: Vertical(g18)
    c: Coincident(g19,g4)
    c: Coincident(g19,g8)
    c: Vertical(g19)
    c: Coincident(g20,g5)
    c: Coincident(g20,g9)
    c: Vertical(g20)
    c: Coincident(g21,g5)
    c: Coincident(g21,g9)
    c: Vertical(g21)
    c: Coincident(g22,g10)
    c: Coincident(g22,g6)
    c: Vertical(g22)
    c: Coincident(g23,g6)
    c: Coincident(g23,g10)
    c: Vertical(g23)
FEATURE [Part::Extrusion] Extrude045  label="removeToCreateFanGrillHoles003"
  Base = -> Sketch054
  Dir = (0,-1,6e-16)
  DirMode = 2
  FaceMakerClass = Part::FaceMakerBullseye
  LengthFwd = 10
  LengthRev = 0
  Placement = pos=(65.4,44,54.82) rot=(0,0,1;0rad)
  Solid = true
  Symmetric = false
FEATURE [Part::Feature] Face105 .. Face108  x4 (patterned run collapsed; names and placements below)
  shape: bbox 3.5 x 17.8 x 2e-07 mm, 1 faces, 0 solids (baked)
FEATURE [Part::Revolution] Revolve113  label="removeToCreateScrewAndThreadedInsertHole041"
  Angle = 360
  Axis = (0,1,0)
  Base = (0,0,0)
  FaceMakerClass = Part::FaceMakerBullseye
  Placement = pos=(62.3,30.3,19.7) rot=(0,0,1;0rad)
  Solid = false
  Source = -> Face105
  Symmetric = false
FEATURE [Part::Revolution] Revolve114  label="removeToCreateScrewAndThreadedInsertHole042"
  Angle = 360
  Axis = (0,1,0)
  Base = (0,0,0)
  FaceMakerClass = Part::FaceMakerBullseye
  Placement = pos=(62.3,30.3,51.7) rot=(0,0,1;0rad)
  Solid = false
  Source = -> Face106
  Symmetric = false
FEATURE [Part::Revolution] Revolve115  label="removeToCreateScrewAndThreadedInsertHole043"
  Angle = 360
  Axis = (0,1,0)
  Base = (0,0,0)
  FaceMakerClass = Part::FaceMakerBullseye
  Placement = pos=(30.3,30.3,19.7) rot=(0,0,1;0rad)
  Solid = false
  Source = -> Face107
  Symmetric = false
FEATURE [Part::Revolution] Revolve116  label="removeToCreateScrewAndThreadedInsertHole044"
  Angle = 360
  Axis = (0,1,0)
  Base = (0,0,0)
  FaceMakerClass = Part::FaceMakerBullseye
  Placement = pos=(30.3,30.3,51.7) rot=(0,0,1;0rad)
  Solid = false
  Source = -> Face108
  Symmetric = false
FEATURE [Part::MultiFuse] Fusion083  label="createThreadedInsertHolesForFan004"
  Shapes = -> [Revolve113,Revolve114,Revolve115,Revolve116]
FEATURE [Part::Box] Box024  label="removeToCreteHoleForPlugHousing026"
  AttacherType = Attacher::AttachEngine3D
  Height = 28.6
  Length = 10
  Placement = pos=(-2,0,21.7) rot=(0,0,1;0rad)
  Width = 19
FEATURE [Part::Cylinder] Cylinder038  label="removeToCreteHoleForPlugHousing027"
  Angle = 360
  AttacherType = Attacher::AttachEngine3D
  Height = 20
  Placement = pos=(-2,19,36) rot=(0,1,0;1.5708rad)
  Radius = 14.3
FEATURE [Part::MultiFuse] Fusion084  label="removeToCreteHoleForPlugHousing028"
  Shapes = -> [Box024,Cylinder038]
FEATURE [Part::Cylinder] Cylinder039
  Angle = 360
  AttacherType = Attacher::AttachEngine3D
  Height = 20
  Placement = pos=(0,0,36.15) rot=(0,0,1;0rad)
  Radius = 14.3
FEATURE [Part::Cylinder] Cylinder040
  Angle = 360
  AttacherType = Attacher::AttachEngine3D
  Height = 10
  Placement = pos=(0,0,36.15) rot=(0,0,1;0rad)
  Radius = 4
FEATURE [Part::Box] Box025  label="removeToCreteHoleForPlugHousing030"
  AttacherType = Attacher::AttachEngine3D
  Height = 28.6
  Length = 20
  Placement = pos=(106.15,0,21.7) rot=(0,0,1;0rad)
  Width = 19
FEATURE [Part::MultiFuse] Fusion086  label="removeToCreteHoleForPlugHousing031"
  Placement = pos=(70,19,36) rot=(0,1,0;1.5708rad)
  Shapes = -> [Cylinder039,Cylinder040]
FEATURE [Part::MultiFuse] Fusion085  label="removeToCreteHoleForPlugHousing029"
  Shapes = -> [Box025,Fusion086]
FEATURE [Sketcher::SketchObject] Sketch055
  FullyConstrained = true
  Placement = pos=(117,19,0) rot=(0.57735,0.57735,0.57735;2.0944rad)
  sketch-geometry (48):
    g0: LineSegment StartX=-49.19 StartY=69.25 StartZ=0 EndX=-49.19 EndY=66.25 EndZ=0
    g1: LineSegment StartX=-49.19 StartY=63.5 StartZ=0 EndX=-49.19 EndY=60.5 EndZ=0
    g2: LineSegment StartX=-49.19 StartY=57.75 StartZ=0 EndX=-49.19 EndY=54.75 EndZ=0
    g3: LineSegment StartX=-49.19 StartY=52 StartZ=0 EndX=-49.19 EndY=49 EndZ=0
    g4: LineSegment StartX=-49.19 StartY=46.25 StartZ=0 EndX=-49.19 EndY=43.25 EndZ=0
    g5: LineSegment StartX=-49.19 StartY=40.5 StartZ=0 EndX=-49.19 EndY=37.5 EndZ=0
    g6: LineSegment StartX=-49.19 StartY=34.5 StartZ=0 EndX=-49.19 EndY=31.5 EndZ=0
    g7: LineSegment StartX=-49.19 StartY=28.75 StartZ=0 EndX=-49.19 EndY=25.75 EndZ=0
    g8: LineSegment StartX=-49.19 StartY=23 StartZ=0 EndX=-49.19 EndY=20 EndZ=0
    g9: LineSegment StartX=-49.19 StartY=17.25 StartZ=0 EndX=-49.19 EndY=14.25 EndZ=0
    g10: LineSegment StartX=-49.19 StartY=11.5 StartZ=0 EndX=-49.19 EndY=8.5 EndZ=0
    g11: LineSegment StartX=-49.19 StartY=5.75 StartZ=0 EndX=-49.19 EndY=2.75 EndZ=0
    g12: ArcOfCircle CenterX=-1.5 CenterY=67.75 CenterZ=0 NormalX=0 NormalY=0 NormalZ=1 AngleXU=0 Radius=1.5 StartAngle=4.71239 EndAngle=7.85398
    g13: ArcOfCircle CenterX=-1.5 CenterY=62 CenterZ=0 NormalX=0 NormalY=0 NormalZ=1 AngleXU=0 Radius=1.5 StartAngle=4.71239 EndAngle=7.85398
    g14: ArcOfCircle CenterX=-1.5 CenterY=56.25 CenterZ=0 NormalX=0 NormalY=0 NormalZ=1 AngleXU=0 Radius=1.5 StartAngle=4.71239 EndAngle=7.85398
    g15: ArcOfCircle CenterX=-11.49 CenterY=50.5 CenterZ=0 NormalX=0 NormalY=0 NormalZ=1 AngleXU=0 Radius=1.5 StartAngle=4.71239 EndAngle=7.85398
    g16: ArcOfCircle CenterX=-16.28 CenterY=44.75 CenterZ=0 NormalX=0 NormalY=0 NormalZ=1 AngleXU=0 Radius=1.5 StartAngle=4.71239 EndAngle=7.85398
    g17: ArcOfCircle CenterX=-18.2337 CenterY=39 CenterZ=0 NormalX=0 NormalY=0 NormalZ=1 AngleXU=0 Radius=1.5 StartAngle=4.71485 EndAngle=7.85398
    g18: ArcOfCircle CenterX=-16.2837 CenterY=27.25 CenterZ=0 NormalX=0 NormalY=0 NormalZ=1 AngleXU=0 Radius=1.5 StartAngle=4.71485 EndAngle=7.85398
    g19: ArcOfCircle CenterX=-18.2337 CenterY=33 CenterZ=0 NormalX=0 NormalY=0 NormalZ=1 AngleXU=0 Radius=1.5 StartAngle=4.71485 EndAngle=7.85398
    g20: ArcOfCircle CenterX=-11.49 CenterY=21.5 CenterZ=0 NormalX=0 NormalY=0 NormalZ=1 AngleXU=0 Radius=1.5 StartAngle=4.71239 EndAngle=7.85398
    g21: ArcOfCircle CenterX=-1.5 CenterY=4.25 CenterZ=0 NormalX=0 NormalY=0 NormalZ=1 AngleXU=0 Radius=1.5 StartAngle=4.71239 EndAngle=7.85398
    g22: ArcOfCircle CenterX=-1.5 CenterY=10 CenterZ=0 NormalX=0 NormalY=0 NormalZ=1 AngleXU=0 Radius=1.5 StartAngle=4.71239 EndAngle=7.85398
    g23: ArcOfCircle CenterX=-1.5 CenterY=15.75 CenterZ=0 NormalX=0 NormalY=0 NormalZ=1 AngleXU=0 Radius=1.5 StartAngle=4.71239 EndAngle=7.85398
    g24: LineSegment StartX=-49.19 StartY=69.25 StartZ=0 EndX=-1.5 EndY=69.25 EndZ=0
    g25: LineSegment StartX=-49.19 StartY=66.25 StartZ=0 EndX=-1.5 EndY=66.25 EndZ=0
    g26: LineSegment StartX=-49.19 StartY=63.5 StartZ=0 EndX=-1.5 EndY=63.5 EndZ=0
    g27: LineSegment StartX=-49.19 StartY=60.5 StartZ=0 EndX=-1.5 EndY=60.5 EndZ=0
    g28: LineSegment StartX=-49.19 StartY=57.75 StartZ=0 EndX=-1.5 EndY=57.75 EndZ=0
    g29: LineSegment StartX=-49.19 StartY=54.75 StartZ=0 EndX=-1.5 EndY=54.75 EndZ=0
    g30: LineSegment StartX=-49.19 StartY=52 StartZ=0 EndX=-11.49 EndY=52 EndZ=0
    g31: LineSegment StartX=-49.19 StartY=49 StartZ=0 EndX=-11.49 EndY=49 EndZ=0
    g32: LineSegment StartX=-49.19 StartY=46.25 StartZ=0 EndX=-16.28 EndY=46.25 EndZ=0
    g33: LineSegment StartX=-49.19 StartY=43.25 StartZ=0 EndX=-16.28 EndY=43.25 EndZ=0
    g34: LineSegment StartX=-49.19 StartY=40.5 StartZ=0 EndX=-18.2337 EndY=40.5 EndZ=0
    g35: LineSegment StartX=-49.19 StartY=37.5 StartZ=0 EndX=-18.23 EndY=37.5 EndZ=0
    g36: LineSegment StartX=-49.19 StartY=34.5 StartZ=0 EndX=-18.2337 EndY=34.5 EndZ=0
    g37: LineSegment StartX=-49.19 StartY=31.5 StartZ=0 EndX=-18.23 EndY=31.5 EndZ=0
    g38: LineSegment StartX=-49.19 StartY=28.75 StartZ=0 EndX=-16.2837 EndY=28.75 EndZ=0
    g39: LineSegment StartX=-49.19 StartY=25.75 StartZ=0 EndX=-16.28 EndY=25.75 EndZ=0
    g40: LineSegment StartX=-49.19 StartY=23 StartZ=0 EndX=-11.49 EndY=23 EndZ=0
    g41: LineSegment StartX=-49.19 StartY=20 StartZ=0 EndX=-11.49 EndY=20 EndZ=0
    g42: LineSegment StartX=-49.19 StartY=17.25 StartZ=0 EndX=-1.5 EndY=17.25 EndZ=0
    g43: LineSegment StartX=-49.19 StartY=14.25 StartZ=0 EndX=-1.5 EndY=14.25 EndZ=0
    g44: LineSegment StartX=-49.19 StartY=11.5 StartZ=0 EndX=-1.5 EndY=11.5 EndZ=0
    g45: LineSegment StartX=-49.19 StartY=8.5 StartZ=0 EndX=-1.5 EndY=8.5 EndZ=0
    g46: LineSegment StartX=-49.19 StartY=5.75 StartZ=0 EndX=-1.5 EndY=5.75 EndZ=0
    g47: LineSegment StartX=-49.19 StartY=2.75 StartZ=0 EndX=-1.5 EndY=2.75 EndZ=0
  constraints (120):
    c: Vertical(g0)
    c: Distance(g0) = 3
    c: Block(g0)
    c: Vertical(g1)
    c: Distance(g1) = 3
    c: Vertical(g2)
    c: Equal(g0,g2) = 3
    c: Block(g2)
    c: Vertical(g3)
    c: Equal(g1,g3) = 3
    c: Vertical(g4)
    c: Equal(g0,g4) = 3
    c: Block(g4)
    c: Vertical(g5)
    c: Equal(g1,g5) = 3
    c: Vertical(g6)
    c: Equal(g0,g6) = 3
    c: Block(g6)
    c: Vertical(g7)
    c: Equal(g1,g7) = 3
    c: Vertical(g8)
    c: Equal(g0,g8) = 3
    c: Block(g8)
    c: Vertical(g9)
    c: Equal(g1,g9) = 3
    c: Vertical(g10)
    c: Equal(g0,g10) = 3
    c: Block(g10)
    c: Vertical(g11)
    c: Equal(g1,g11) = 3
    c: Block(g12)
    c: Block(g13)
    c: Block(g14)
    c: Block(g15)
    c: Block(g16)
    c: Block(g17)
    c: Block(g18)
    c: Block(g19)
    c: Block(g20)
    c: Block(g21)
    c: Block(g22)
    c: Block(g23)
    c: Block(g11)
    c: Block(g9)
    c: Block(g7)
    c: Block(g5)
    c: Block(g3)
    c: Block(g1)
    c: Coincident(g24,g0)
    c: Coincident(g24,g12)
    c: Horizontal(g24)
    c: Coincident(g25,g0)
    c: Coincident(g25,g12)
    c: Horizontal(g25)
    c: Coincident(g26,g1)
    c: Coincident(g26,g13)
    c: Horizontal(g26)
    c: Coincident(g27,g1)
    c: Coincident(g27,g13)
    c: Horizontal(g27)
    c: Coincident(g28,g2)
    c: Coincident(g28,g14)
    c: Horizontal(g28)
    c: Coincident(g29,g2)
    c: Coincident(g29,g14)
    c: Horizontal(g29)
    c: Coincident(g30,g3)
    c: Coincident(g30,g15)
    c: Horizontal(g30)
    c: Coincident(g31,g3)
    c: Coincident(g31,g15)
    c: Horizontal(g31)
    c: Coincident(g32,g4)
    c: Coincident(g32,g16)
    c: Horizontal(g32)
    c: Coincident(g33,g4)
    c: Coincident(g33,g16)
    c: Horizontal(g33)
    c: Coincident(g34,g5)
    c: Coincident(g34,g17)
    c: Horizontal(g34)
    c: Coincident(g35,g5)
    c: Coincident(g35,g17)
    c: Horizontal(g35)
    c: Coincident(g36,g6)
    c: Coincident(g36,g19)
    c: Horizontal(g36)
    c: Coincident(g37,g6)
    c: Coincident(g37,g19)
    c: Horizontal(g37)
    c: Coincident(g38,g7)
    c: Coincident(g38,g18)
    c: Horizontal(g38)
    c: Coincident(g39,g7)
    c: Coincident(g39,g18)
    c: Horizontal(g39)
    c: Coincident(g40,g8)
    c: Coincident(g40,g20)
    c: Horizontal(g40)
    c: Coincident(g41,g8)
    c: Coincident(g41,g20)
    c: Horizontal(g41)
    c: Coincident(g42,g9)
    c: Coincident(g42,g23)
    c: Horizontal(g42)
    c: Coincident(g43,g9)
    c: Coincident(g43,g23)
    c: Horizontal(g43)
    c: Coincident(g44,g10)
    c: Coincident(g44,g22)
    c: Horizontal(g44)
    c: Coincident(g45,g10)
    c: Coincident(g45,g22)
    c: Horizontal(g45)
    c: Coincident(g46,g11)
    c: Coincident(g46,g21)
    c: Horizontal(g46)
    c: Coincident(g47,g11)
    c: Coincident(g47,g21)
    c: Horizontal(g47)
FEATURE [Part::Extrusion] Extrude046
  Base = -> Sketch055
  Dir = (1,0,0)
  DirMode = 2
  FaceMakerClass = Part::FaceMakerBullseye
  LengthFwd = 23
  LengthRev = 0
  Placement = pos=(-19,0,0) rot=(0,0,1;0rad)
  Solid = true
  Symmetric = false
FEATURE [Part::Fillet] Fillet038  label="removeToCreateVentalationHoles001"
  Base = -> Extrude046
  Edges = <same value as first occurrence — deduplicated (x6 in doc)>
  Placement = pos=(7,0,0) rot=(0,0,1;0rad)
FEATURE [Sketcher::SketchObject] Sketch056  label="topSketch014"
  FullyConstrained = true
  sketch-geometry (22):
    g0: LineSegment StartX=5.21097e-06 StartY=3 StartZ=0 EndX=5.21097e-06 EndY=19 EndZ=0
    g1: ArcOfCircle CenterX=19 CenterY=19 CenterZ=0 NormalX=0 NormalY=0 NormalZ=1 AngleXU=0 Radius=19 StartAngle=1.5708 EndAngle=3.14159
    g2: ArcOfCircle CenterX=19 CenterY=19 CenterZ=0 NormalX=0 NormalY=0 NormalZ=1 AngleXU=0 Radius=16 StartAngle=1.5708 EndAngle=3.14159
    g3: LineSegment StartX=114 StartY=35 StartZ=0 EndX=19 EndY=35 EndZ=0
    g4: LineSegment StartX=5.21097e-06 StartY=3 StartZ=0 EndX=5.21097e-06 EndY=0 EndZ=0
    g5: LineSegment StartX=3 StartY=0 StartZ=0 EndX=5.21097e-06 EndY=0 EndZ=0
    g6: LineSegment StartX=3 StartY=19 StartZ=0 EndX=3 EndY=0 EndZ=0
    g7: LineSegment StartX=19 StartY=38 StartZ=0 EndX=124 EndY=38 EndZ=0
    g8: Circle CenterX=119 CenterY=35 CenterZ=0 NormalX=0 NormalY=0 NormalZ=1 AngleXU=0 Radius=1
    g9: Circle CenterX=121 CenterY=35 CenterZ=0 NormalX=0 NormalY=0 NormalZ=1 AngleXU=0 Radius=1
    g10: Circle CenterX=121 CenterY=33 CenterZ=0 NormalX=0 NormalY=0 NormalZ=1 AngleXU=0 Radius=1
    g11: BSplineCurve PolesCount=3 KnotsCount=2 Degree=2 IsPeriodic=0
    g12: GeomPoint X=119 Y=35 Z=0
    g13: GeomPoint X=121 Y=33 Z=0
    g14: LineSegment StartX=119 StartY=35 StartZ=0 EndX=114 EndY=35 EndZ=0
    g15: ArcOfCircle CenterX=105 CenterY=19 CenterZ=0 NormalX=0 NormalY=0 NormalZ=1 AngleXU=0 Radius=16 StartAngle=5.60905 EndAngle=6.28319
    g16: LineSegment StartX=121 StartY=33 StartZ=0 EndX=121 EndY=19 EndZ=0
    g17: LineSegment StartX=117.5 StartY=9.01251 StartZ=0 EndX=121.163 EndY=9.0125 EndZ=0
    g18: ArcOfCircle CenterX=105 CenterY=19 CenterZ=0 NormalX=0 NormalY=0 NormalZ=1 AngleXU=0 Radius=20.6155 StartAngle=5.7297 EndAngle=6.28319
    g19: LineSegment StartX=121.163 StartY=9.0125 StartZ=0 EndX=122.538 EndY=8.16329 EndZ=0
    g20: LineSegment StartX=124 StartY=38 StartZ=0 EndX=125.616 EndY=38 EndZ=0
    g21: LineSegment StartX=125.616 StartY=19 StartZ=0 EndX=125.616 EndY=38 EndZ=0
  constraints (49):
    c: Vertical(g0)
    c: Block(g0)
    c: Coincident(g1,g0)
    c: Block(g1)
    c: Coincident(g2,g1)
    c: Block(g2)
    c: Coincident(g3,g2)
    c: Horizontal(g3)
    c: Tangent(g3,g2)
    c: Coincident(g4,g0)
    c: Distance(g4) = 3
    c: Vertical(g4)
    c: Coincident(g5,g4)
    c: Horizontal(g5)
    c: Coincident(g6,g2)
    c: Coincident(g6,g5)
    c: Vertical(g6)
    c: Horizontal(g7)
    c: Distance(g7) = 105
    c: Coincident(g7,g1)
    c: Block(g3)
    c: Weight(g8) = 1
    c: Equal(g8,g9)
    c: Equal(g8,g10)
    c: InternalAlignment(g8,g11)
    c: InternalAlignment(g9,g11)
    c: InternalAlignment(g10,g11)
    c: InternalAlignment(g12,g11)
    c: InternalAlignment(g13,g11)
    c: Block(g11)
    c: Coincident(g14,g11)
    c: Coincident(g14,g3)
    c: Horizontal(g14)
    c: Block(g15)
    c: Coincident(g16,g11)
    c: Coincident(g16,g15)
    c: Vertical(g16)
    c: Distance(g16) = 14
    c: Coincident(g17,g15)
    c: Block(g18)
    c: Coincident(g19,g18)
    c: Coincident(g20,g7)
    c: Horizontal(g20)
    c: Vertical(g21)
    c: Coincident(g20,g21)
    c: Block(g20)
    c: Block(g21)
    c: Block(g19)
    c: Block(g17)
FEATURE [Part::Box] Box026  label="removeToCreteHoleForPlugHousing032"
  AttacherType = Attacher::AttachEngine3D
  Height = 28.6
  Length = 10
  Placement = pos=(-2,0,21.7) rot=(0,0,1;0rad)
  Width = 19
FEATURE [Part::Feature] Face109 .. Face112  x4 (patterned run collapsed; names and placements below)
  shape: bbox 3.5 x 17.8 x 2e-07 mm, 1 faces, 0 solids (baked)
FEATURE [Part::Revolution] Revolve117  label="removeToCreateScrewAndThreadedInsertHole045"
  Angle = 360
  Axis = (0,1,0)
  Base = (0,0,0)
  FaceMakerClass = Part::FaceMakerBullseye
  Placement = pos=(62.3,30.3,19.7) rot=(0,0,1;0rad)
  Solid = false
  Source = -> Face109
  Symmetric = false
FEATURE [Part::Revolution] Revolve118  label="removeToCreateScrewAndThreadedInsertHole046"
  Angle = 360
  Axis = (0,1,0)
  Base = (0,0,0)
  FaceMakerClass = Part::FaceMakerBullseye
  Placement = pos=(62.3,30.3,51.7) rot=(0,0,1;0rad)
  Solid = false
  Source = -> Face110
  Symmetric = false
FEATURE [Part::Revolution] Revolve119  label="removeToCreateScrewAndThreadedInsertHole047"
  Angle = 360
  Axis = (0,1,0)
  Base = (0,0,0)
  FaceMakerClass = Part::FaceMakerBullseye
  Placement = pos=(30.3,30.3,19.7) rot=(0,0,1;0rad)
  Solid = false
  Source = -> Face111
  Symmetric = false
FEATURE [Part::Revolution] Revolve120  label="removeToCreateScrewAndThreadedInsertHole048"
  Angle = 360
  Axis = (0,1,0)
  Base = (0,0,0)
  FaceMakerClass = Part::FaceMakerBullseye
  Placement = pos=(30.3,30.3,51.7) rot=(0,0,1;0rad)
  Solid = false
  Source = -> Face112
  Symmetric = false
FEATURE [Part::MultiFuse] Fusion087  label="createThreadedInsertHolesForFan005"
  Shapes = -> [Revolve117,Revolve118,Revolve119,Revolve120]
FEATURE [Part::Extrusion] Extrude047
  Base = -> Sketch056
  Dir = (0,0,1)
  DirMode = 2
  FaceMakerClass = Part::FaceMakerBullseye
  LengthFwd = 72
  LengthRev = 0
  Solid = true
  Symmetric = false
FEATURE [Part::Fillet] Fillet039  label="top019"
  Base = -> Extrude047
  Edges = 1 edges r=2: [Edge35]
FEATURE [Sketcher::SketchObject] Sketch057
  FullyConstrained = false
  Placement = pos=(0,0,0) rot=(1,0,0;1.5708rad)
  sketch-geometry (24):
    g0: ArcOfCircle CenterX=-4 CenterY=-10.5 CenterZ=0 NormalX=0 NormalY=0 NormalZ=1 AngleXU=0 Radius=1.5 StartAngle=6e-16 EndAngle=3.14159
    g1: ArcOfCircle CenterX=-34.2 CenterY=-10.5 CenterZ=0 NormalX=0 NormalY=0 NormalZ=1 AngleXU=0 Radius=1.5 StartAngle=0 EndAngle=3.14159
    g2: ArcOfCircle CenterX=-34.2 CenterY=-27.7 CenterZ=0 NormalX=0 NormalY=0 NormalZ=1 AngleXU=0 Radius=1.5 StartAngle=3.14159 EndAngle=6.28319
    g3: ArcOfCircle CenterX=-4 CenterY=-27.7 CenterZ=0 NormalX=0 NormalY=0 NormalZ=1 AngleXU=0 Radius=1.5 StartAngle=3.1416 EndAngle=6.28319
    g4: ArcOfCircle CenterX=-10 CenterY=-4.3 CenterZ=0 NormalX=0 NormalY=0 NormalZ=1 AngleXU=0 Radius=1.5 StartAngle=2e-16 EndAngle=3.14159
    g5: ArcOfCircle CenterX=-16.1 CenterY=-1.8 CenterZ=0 NormalX=0 NormalY=0 NormalZ=1 AngleXU=0 Radius=1.5 StartAngle=5e-16 EndAngle=3.14159
    g6: ArcOfCircle CenterX=-22.1 CenterY=-1.8 CenterZ=0 NormalX=0 NormalY=0 NormalZ=1 AngleXU=0 Radius=1.5 StartAngle=5e-16 EndAngle=3.14159
    g7: ArcOfCircle CenterX=-28.2 CenterY=-4.3 CenterZ=0 NormalX=0 NormalY=0 NormalZ=1 AngleXU=0 Radius=1.5 StartAngle=2e-16 EndAngle=3.14159
    g8: ArcOfCircle CenterX=-10 CenterY=-33.9 CenterZ=0 NormalX=0 NormalY=0 NormalZ=1 AngleXU=0 Radius=1.5 StartAngle=3.14159 EndAngle=6.28319
    g9: ArcOfCircle CenterX=-16.1 CenterY=-36.4 CenterZ=0 NormalX=0 NormalY=0 NormalZ=1 AngleXU=0 Radius=1.5 StartAngle=3.14159 EndAngle=6.28319
    g10: ArcOfCircle CenterX=-22.1 CenterY=-36.4 CenterZ=0 NormalX=0 NormalY=0 NormalZ=1 AngleXU=0 Radius=1.5 StartAngle=3.14159 EndAngle=6.28319
    g11: ArcOfCircle CenterX=-28.2 CenterY=-33.9 CenterZ=0 NormalX=0 NormalY=0 NormalZ=1 AngleXU=0 Radius=1.5 StartAngle=3.14159 EndAngle=6.28319
    g12: LineSegment StartX=-35.7 StartY=-10.5 StartZ=0 EndX=-35.7 EndY=-27.7 EndZ=0
    g13: LineSegment StartX=-32.7 StartY=-10.5 StartZ=0 EndX=-32.7 EndY=-27.7 EndZ=0
    g14: LineSegment StartX=-29.7 StartY=-33.9 StartZ=0 EndX=-29.7 EndY=-4.3 EndZ=0
    g15: LineSegment StartX=-26.7 StartY=-33.9 StartZ=0 EndX=-26.7 EndY=-4.3 EndZ=0
    g16: LineSegment StartX=-2.5 StartY=-10.5 StartZ=0 EndX=-2.5 EndY=-27.7 EndZ=0
    g17: LineSegment StartX=-8.5 StartY=-4.3 StartZ=0 EndX=-8.5 EndY=-33.9 EndZ=0
    g18: LineSegment StartX=-5.5 StartY=-10.5 StartZ=0 EndX=-5.5 EndY=-27.7 EndZ=0
    g19: LineSegment StartX=-11.5 StartY=-4.3 StartZ=0 EndX=-11.5 EndY=-33.9 EndZ=0
    g20: LineSegment StartX=-14.6 StartY=-1.8 StartZ=0 EndX=-14.6 EndY=-36.4 EndZ=0
    g21: LineSegment StartX=-17.6 StartY=-1.8 StartZ=0 EndX=-17.6 EndY=-36.4 EndZ=0
    g22: LineSegment StartX=-20.6 StartY=-36.4 StartZ=0 EndX=-20.6 EndY=-1.8 EndZ=0
    g23: LineSegment StartX=-23.6 StartY=-1.8 StartZ=0 EndX=-23.6 EndY=-36.4 EndZ=0
  constraints (48):
    c: Block(g0)
    c: Block(g1)
    c: Block(g2)
    c: Block(g3)
    c: Block(g4)
    c: Block(g5)
    c: Block(g6)
    c: Block(g7)
    c: Block(g8)
    c: Block(g9)
    c: Block(g10)
    c: Block(g11)
    c: Coincident(g12,g1)
    c: Coincident(g12,g2)
    c: Vertical(g12)
    c: Coincident(g13,g1)
    c: Coincident(g13,g2)
    c: Vertical(g13)
    c: Coincident(g14,g11)
    c: Coincident(g14,g7)
    c: Vertical(g14)
    c: Coincident(g15,g11)
    c: Coincident(g15,g7)
    c: Vertical(g15)
    c: Coincident(g16,g0)
    c: Coincident(g16,g3)
    c: Vertical(g16)
    c: Coincident(g17,g4)
    c: Coincident(g17,g8)
    c: Vertical(g17)
    c: Coincident(g18,g0)
    c: Coincident(g18,g3)
    c: Vertical(g18)
    c: Coincident(g19,g4)
    c: Coincident(g19,g8)
    c: Vertical(g19)
    c: Coincident(g20,g5)
    c: Coincident(g20,g9)
    c: Vertical(g20)
    c: Coincident(g21,g5)
    c: Coincident(g21,g9)
    c: Vertical(g21)
    c: Coincident(g22,g10)
    c: Coincident(g22,g6)
    c: Vertical(g22)
    c: Coincident(g23,g6)
    c: Coincident(g23,g10)
    c: Vertical(g23)
FEATURE [Part::Extrusion] Extrude048  label="removeToCreateFanGrillHoles004"
  Base = -> Sketch057
  Dir = (0,-1,6e-16)
  DirMode = 2
  FaceMakerClass = Part::FaceMakerBullseye
  LengthFwd = 10
  LengthRev = 0
  Placement = pos=(65.4,44,54.82) rot=(0,0,1;0rad)
  Solid = true
  Symmetric = false
FEATURE [Part::Cut] Cut040  label="top021"
  Base = -> Fillet039
  Tool = -> Extrude048
FEATURE [Part::Cylinder] Cylinder041  label="removeToCreteHoleForPlugHousing034"
  Angle = 360
  AttacherType = Attacher::AttachEngine3D
  Height = 20
  Placement = pos=(-2,19,36) rot=(0,1,0;1.5708rad)
  Radius = 14.3
FEATURE [Part::MultiFuse] Fusion089  label="removeToCreteHoleForPlugHousing035"
  Shapes = -> [Box026,Cylinder041]
FEATURE [Part::Cylinder] Cylinder042
  Angle = 360
  AttacherType = Attacher::AttachEngine3D
  Height = 20
  Placement = pos=(0,0,36.15) rot=(0,0,1;0rad)
  Radius = 14.3
FEATURE [Part::Cylinder] Cylinder043
  Angle = 360
  AttacherType = Attacher::AttachEngine3D
  Height = 10
  Placement = pos=(0,0,36.15) rot=(0,0,1;0rad)
  Radius = 4
FEATURE [Part::Box] Box027  label="removeToCreteHoleForPlugHousing036"
  AttacherType = Attacher::AttachEngine3D
  Height = 28.6
  Length = 20
  Placement = pos=(106.15,0,21.7) rot=(0,0,1;0rad)
  Width = 19
FEATURE [Part::Cut] Cut041  label="top022"
  Base = -> Cut040
  Tool = -> Fusion087
FEATURE [Part::Cut] Cut039  label="top020"
  Base = -> Cut041
  Tool = -> Fusion089
FEATURE [Part::MultiFuse] Fusion090  label="removeToCreteHoleForPlugHousing037"
  Placement = pos=(70,19,36) rot=(0,1,0;1.5708rad)
  Shapes = -> [Cylinder042,Cylinder043]
FEATURE [Part::MultiFuse] Fusion088  label="removeToCreteHoleForPlugHousing033"
  Shapes = -> [Box027,Fusion090]
FEATURE [Part::Cut] Cut042  label="removeToCreteHoleForPlugHousing038"
  Base = -> Cut039
  Tool = -> Fusion088
FEATURE [Part::MultiFuse] Fusion091  label="removeFromTop"
  Shapes = -> [Fillet038,Fusion085,Fusion084,Fusion083,Extrude045]
FEATURE [Part::Cut] Cut043  label="REAL TOP ====="
  Base = -> Fillet036
  Tool = -> Fusion091
FEATURE [Part::MultiFuse] Fusion092  label="caseScrewPillarBracket016"
  Shapes = -> [Extrude030,Extrude031,Extrude032,Extrude033,Extrude034,Extrude035,Extrude036,Extrude037,Box013,Box014]
FEATURE [Sketcher::SketchObject] Sketch058  label="topSketch015"
  FullyConstrained = true
  sketch-geometry (20):
    g0: LineSegment StartX=5.21097e-06 StartY=3 StartZ=0 EndX=5.21097e-06 EndY=19 EndZ=0
    g1: ArcOfCircle CenterX=19 CenterY=19 CenterZ=0 NormalX=0 NormalY=0 NormalZ=1 AngleXU=0 Radius=19 StartAngle=1.5708 EndAngle=3.14159
    g2: ArcOfCircle CenterX=19 CenterY=19 CenterZ=0 NormalX=0 NormalY=0 NormalZ=1 AngleXU=0 Radius=16 StartAngle=1.5708 EndAngle=3.14159
    g3: LineSegment StartX=114 StartY=35 StartZ=0 EndX=19 EndY=35 EndZ=0
    g4: LineSegment StartX=5.21097e-06 StartY=3 StartZ=0 EndX=5.21097e-06 EndY=0 EndZ=0
    g5: LineSegment StartX=3 StartY=0 StartZ=0 EndX=5.21097e-06 EndY=0 EndZ=0
    g6: LineSegment StartX=3 StartY=19 StartZ=0 EndX=3 EndY=0 EndZ=0
    g7: LineSegment StartX=19 StartY=38 StartZ=0 EndX=124 EndY=38 EndZ=0
    g8: Circle CenterX=119 CenterY=35 CenterZ=0 NormalX=0 NormalY=0 NormalZ=1 AngleXU=0 Radius=1
    g9: Circle CenterX=121 CenterY=35 CenterZ=0 NormalX=0 NormalY=0 NormalZ=1 AngleXU=0 Radius=1
    g10: Circle CenterX=121 CenterY=33 CenterZ=0 NormalX=0 NormalY=0 NormalZ=1 AngleXU=0 Radius=1
    g11: BSplineCurve PolesCount=3 KnotsCount=2 Degree=2 IsPeriodic=0
    g12: GeomPoint X=119 Y=35 Z=0
    g13: GeomPoint X=121 Y=33 Z=0
    g14: LineSegment StartX=119 StartY=35 StartZ=0 EndX=114 EndY=35 EndZ=0
    g15: ArcOfCircle CenterX=105 CenterY=19 CenterZ=0 NormalX=0 NormalY=0 NormalZ=1 AngleXU=0 Radius=19 StartAngle=5.7297 EndAngle=6.28319
    g16: ArcOfCircle CenterX=105 CenterY=19 CenterZ=0 NormalX=0 NormalY=0 NormalZ=1 AngleXU=0 Radius=16 StartAngle=5.60905 EndAngle=6.28319
    g17: LineSegment StartX=121 StartY=33 StartZ=0 EndX=121 EndY=19 EndZ=0
    g18: LineSegment StartX=124 StartY=38 StartZ=0 EndX=124 EndY=19 EndZ=0
    g19: LineSegment StartX=117.5 StartY=9.01251 StartZ=0 EndX=121.163 EndY=9.0125 EndZ=0
  constraints (46):
    c: Vertical(g0)
    c: Block(g0)
    c: Coincident(g1,g0)
    c: Block(g1)
    c: Coincident(g2,g1)
    c: Block(g2)
    c: Coincident(g3,g2)
    c: Horizontal(g3)
    c: Tangent(g3,g2)
    c: Coincident(g4,g0)
    c: Distance(g4) = 3
    c: Vertical(g4)
    c: Coincident(g5,g4)
    c: Horizontal(g5)
    c: Coincident(g6,g2)
    c: Coincident(g6,g5)
    c: Vertical(g6)
    c: Horizontal(g7)
    c: Distance(g7) = 105
    c: Coincident(g7,g1)
    c: Block(g3)
    c: Weight(g8) = 1
    c: Equal(g8,g9)
    c: Equal(g8,g10)
    c: InternalAlignment(g8,g11)
    c: InternalAlignment(g9,g11)
    c: InternalAlignment(g10,g11)
    c: InternalAlignment(g12,g11)
    c: InternalAlignment(g13,g11)
    c: Block(g11)
    c: Coincident(g14,g11)
    c: Coincident(g14,g3)
    c: Horizontal(g14)
    c: Block(g15)
    c: Coincident(g16,g15)
    c: Block(g16)
    c: Coincident(g17,g11)
    c: Coincident(g17,g16)
    c: Vertical(g17)
    c: Distance(g17) = 14
    c: Coincident(g18,g7)
    c: Coincident(g18,g15)
    c: Vertical(g18)
    c: Distance(g18) = 19
    c: Coincident(g19,g16)
    c: Coincident(g19,g15)
FEATURE [Part::Extrusion] Extrude049  label="top023"
  Base = -> Sketch058
  Dir = (0,0,1)
  DirMode = 2
  FaceMakerClass = Part::FaceMakerBullseye
  LengthFwd = 72
  LengthRev = 0
  Solid = true
  Symmetric = false
FEATURE [Sketcher::SketchObject] Sketch059
  FullyConstrained = true
  MapMode = 3
  Placement = pos=(0,0,0) rot=(1,0,0;1.5708rad)
  Support = -> [Extrude049]
  sketch-geometry (8):
    g0: Circle CenterX=80.351 CenterY=-67.6202 CenterZ=0 NormalX=0 NormalY=0 NormalZ=1 AngleXU=0 Radius=2
    g1: Circle CenterX=80.351 CenterY=-67.6202 CenterZ=0 NormalX=0 NormalY=0 NormalZ=1 AngleXU=0 Radius=3
    g2: Circle CenterX=80.351 CenterY=-4.92017 CenterZ=0 NormalX=0 NormalY=0 NormalZ=1 AngleXU=0 Radius=2
    g3: Circle CenterX=80.351 CenterY=-4.92017 CenterZ=0 NormalX=0 NormalY=0 NormalZ=1 AngleXU=0 Radius=3
    g4: Circle CenterX=23.851 CenterY=-4.92017 CenterZ=0 NormalX=0 NormalY=0 NormalZ=1 AngleXU=0 Radius=2
    g5: Circle CenterX=23.851 CenterY=-4.92017 CenterZ=0 NormalX=0 NormalY=0 NormalZ=1 AngleXU=0 Radius=3
    g6: Circle CenterX=23.851 CenterY=-67.6202 CenterZ=0 NormalX=0 NormalY=0 NormalZ=1 AngleXU=0 Radius=2
    g7: Circle CenterX=23.851 CenterY=-67.6202 CenterZ=0 NormalX=0 NormalY=0 NormalZ=1 AngleXU=0 Radius=3
  constraints (8):
    c: Block(g3)
    c: Block(g2)
    c: Block(g1)
    c: Block(g0)
    c: Block(g6)
    c: Block(g7)
    c: Block(g4)
    c: Block(g5)
FEATURE [Sketcher::SketchObject] Sketch060
  FullyConstrained = true
  MapMode = 3
  Placement = pos=(0,0,0) rot=(1,0,0;1.5708rad)
  Support = -> [Extrude049]
  sketch-geometry (8):
    g0: Circle CenterX=80.351 CenterY=-67.6202 CenterZ=0 NormalX=0 NormalY=0 NormalZ=1 AngleXU=0 Radius=3
    g1: Circle CenterX=80.351 CenterY=-4.92017 CenterZ=0 NormalX=0 NormalY=0 NormalZ=1 AngleXU=0 Radius=3
    g2: Circle CenterX=23.851 CenterY=-4.92017 CenterZ=0 NormalX=0 NormalY=0 NormalZ=1 AngleXU=0 Radius=3
    g3: Circle CenterX=23.851 CenterY=-67.6202 CenterZ=0 NormalX=0 NormalY=0 NormalZ=1 AngleXU=0 Radius=3
    g4: Circle CenterX=23.851 CenterY=-67.6202 CenterZ=0 NormalX=0 NormalY=0 NormalZ=1 AngleXU=0 Radius=5
    g5: Circle CenterX=80.351 CenterY=-67.6202 CenterZ=0 NormalX=0 NormalY=0 NormalZ=1 AngleXU=0 Radius=5
    g6: Circle CenterX=23.851 CenterY=-4.92017 CenterZ=0 NormalX=0 NormalY=0 NormalZ=1 AngleXU=0 Radius=5
    g7: Circle CenterX=80.351 CenterY=-4.92017 CenterZ=0 NormalX=0 NormalY=0 NormalZ=1 AngleXU=0 Radius=5
  constraints (8):
    c: Block(g1)
    c: Block(g0)
    c: Block(g3)
    c: Block(g2)
    c: Block(g5)
    c: Block(g4)
    c: Block(g6)
    c: Block(g7)
FEATURE [Sketcher::SketchObject] Sketch061
  FullyConstrained = true
  MapMode = 3
  Placement = pos=(0,0,0) rot=(1,0,0;1.5708rad)
  sketch-geometry (8):
    g0: Circle CenterX=80.351 CenterY=-67.6202 CenterZ=0 NormalX=0 NormalY=0 NormalZ=1 AngleXU=0 Radius=3
    g1: Circle CenterX=80.351 CenterY=-4.92017 CenterZ=0 NormalX=0 NormalY=0 NormalZ=1 AngleXU=0 Radius=3
    g2: Circle CenterX=23.851 CenterY=-4.92017 CenterZ=0 NormalX=0 NormalY=0 NormalZ=1 AngleXU=0 Radius=3
    g3: Circle CenterX=23.851 CenterY=-67.6202 CenterZ=0 NormalX=0 NormalY=0 NormalZ=1 AngleXU=0 Radius=3
    g4: Circle CenterX=23.851 CenterY=-67.6202 CenterZ=0 NormalX=0 NormalY=0 NormalZ=1 AngleXU=0 Radius=5
    g5: Circle CenterX=80.351 CenterY=-67.6202 CenterZ=0 NormalX=0 NormalY=0 NormalZ=1 AngleXU=0 Radius=5
    g6: Circle CenterX=23.851 CenterY=-4.92017 CenterZ=0 NormalX=0 NormalY=0 NormalZ=1 AngleXU=0 Radius=5
    g7: Circle CenterX=80.351 CenterY=-4.92017 CenterZ=0 NormalX=0 NormalY=0 NormalZ=1 AngleXU=0 Radius=5
  constraints (8):
    c: Block(g1)
    c: Block(g0)
    c: Block(g3)
    c: Block(g2)
    c: Block(g5)
    c: Block(g4)
    c: Block(g6)
    c: Block(g7)
FEATURE [Sketcher::SketchObject] Sketch062  label="topSketch016"
  FullyConstrained = true
  sketch-geometry (20):
    g0: LineSegment StartX=5.21097e-06 StartY=3 StartZ=0 EndX=5.21097e-06 EndY=19 EndZ=0
    g1: ArcOfCircle CenterX=19 CenterY=19 CenterZ=0 NormalX=0 NormalY=0 NormalZ=1 AngleXU=0 Radius=19 StartAngle=1.5708 EndAngle=3.14159
    g2: ArcOfCircle CenterX=19 CenterY=19 CenterZ=0 NormalX=0 NormalY=0 NormalZ=1 AngleXU=0 Radius=16 StartAngle=1.5708 EndAngle=3.14159
    g3: LineSegment StartX=114 StartY=35 StartZ=0 EndX=19 EndY=35 EndZ=0
    g4: LineSegment StartX=5.21097e-06 StartY=3 StartZ=0 EndX=5.21097e-06 EndY=0 EndZ=0
    g5: LineSegment StartX=3 StartY=0 StartZ=0 EndX=5.21097e-06 EndY=0 EndZ=0
    g6: LineSegment StartX=3 StartY=19 StartZ=0 EndX=3 EndY=0 EndZ=0
    g7: LineSegment StartX=19 StartY=38 StartZ=0 EndX=124 EndY=38 EndZ=0
    g8: Circle CenterX=119 CenterY=35 CenterZ=0 NormalX=0 NormalY=0 NormalZ=1 AngleXU=0 Radius=1
    g9: Circle CenterX=121 CenterY=35 CenterZ=0 NormalX=0 NormalY=0 NormalZ=1 AngleXU=0 Radius=1
    g10: Circle CenterX=121 CenterY=33 CenterZ=0 NormalX=0 NormalY=0 NormalZ=1 AngleXU=0 Radius=1
    g11: BSplineCurve PolesCount=3 KnotsCount=2 Degree=2 IsPeriodic=0
    g12: GeomPoint X=119 Y=35 Z=0
    g13: GeomPoint X=121 Y=33 Z=0
    g14: LineSegment StartX=119 StartY=35 StartZ=0 EndX=114 EndY=35 EndZ=0
    g15: ArcOfCircle CenterX=105 CenterY=19 CenterZ=0 NormalX=0 NormalY=0 NormalZ=1 AngleXU=0 Radius=19 StartAngle=5.7297 EndAngle=6.28319
    g16: ArcOfCircle CenterX=105 CenterY=19 CenterZ=0 NormalX=0 NormalY=0 NormalZ=1 AngleXU=0 Radius=16 StartAngle=5.60905 EndAngle=6.28319
    g17: LineSegment StartX=121 StartY=33 StartZ=0 EndX=121 EndY=19 EndZ=0
    g18: LineSegment StartX=124 StartY=38 StartZ=0 EndX=124 EndY=19 EndZ=0
    g19: LineSegment StartX=117.5 StartY=9.01251 StartZ=0 EndX=121.163 EndY=9.0125 EndZ=0
  constraints (46):
    c: Vertical(g0)
    c: Block(g0)
    c: Coincident(g1,g0)
    c: Block(g1)
    c: Coincident(g2,g1)
    c: Block(g2)
    c: Coincident(g3,g2)
    c: Horizontal(g3)
    c: Tangent(g3,g2)
    c: Coincident(g4,g0)
    c: Distance(g4) = 3
    c: Vertical(g4)
    c: Coincident(g5,g4)
    c: Horizontal(g5)
    c: Coincident(g6,g2)
    c: Coincident(g6,g5)
    c: Vertical(g6)
    c: Horizontal(g7)
    c: Distance(g7) = 105
    c: Coincident(g7,g1)
    c: Block(g3)
    c: Weight(g8) = 1
    c: Equal(g8,g9)
    c: Equal(g8,g10)
    c: InternalAlignment(g8,g11)
    c: InternalAlignment(g9,g11)
    c: InternalAlignment(g10,g11)
    c: InternalAlignment(g12,g11)
    c: InternalAlignment(g13,g11)
    c: Block(g11)
    c: Coincident(g14,g11)
    c: Coincident(g14,g3)
    c: Horizontal(g14)
    c: Block(g15)
    c: Coincident(g16,g15)
    c: Block(g16)
    c: Coincident(g17,g11)
    c: Coincident(g17,g16)
    c: Vertical(g17)
    c: Distance(g17) = 14
    c: Coincident(g18,g7)
    c: Coincident(g18,g15)
    c: Vertical(g18)
    c: Distance(g18) = 19
    c: Coincident(g19,g16)
    c: Coincident(g19,g15)
FEATURE [Part::Extrusion] Extrude053  label="top024"
  Base = -> Sketch062
  Dir = (0,0,1)
  DirMode = 2
  FaceMakerClass = Part::FaceMakerBullseye
  LengthFwd = 72
  LengthRev = 0
  Solid = true
  Symmetric = false
FEATURE [Sketcher::SketchObject] Sketch063
  FullyConstrained = true
  MapMode = 3
  Placement = pos=(0,0,0) rot=(1,0,0;1.5708rad)
  Support = -> [Extrude053]
  sketch-geometry (8):
    g0: Circle CenterX=80.351 CenterY=-67.6202 CenterZ=0 NormalX=0 NormalY=0 NormalZ=1 AngleXU=0 Radius=2
    g1: Circle CenterX=80.351 CenterY=-67.6202 CenterZ=0 NormalX=0 NormalY=0 NormalZ=1 AngleXU=0 Radius=3
    g2: Circle CenterX=80.351 CenterY=-4.92017 CenterZ=0 NormalX=0 NormalY=0 NormalZ=1 AngleXU=0 Radius=2
    g3: Circle CenterX=80.351 CenterY=-4.92017 CenterZ=0 NormalX=0 NormalY=0 NormalZ=1 AngleXU=0 Radius=3
    g4: Circle CenterX=23.851 CenterY=-4.92017 CenterZ=0 NormalX=0 NormalY=0 NormalZ=1 AngleXU=0 Radius=2
    g5: Circle CenterX=23.851 CenterY=-4.92017 CenterZ=0 NormalX=0 NormalY=0 NormalZ=1 AngleXU=0 Radius=3
    g6: Circle CenterX=23.851 CenterY=-67.6202 CenterZ=0 NormalX=0 NormalY=0 NormalZ=1 AngleXU=0 Radius=2
    g7: Circle CenterX=23.851 CenterY=-67.6202 CenterZ=0 NormalX=0 NormalY=0 NormalZ=1 AngleXU=0 Radius=3
  constraints (8):
    c: Block(g3)
    c: Block(g2)
    c: Block(g1)
    c: Block(g0)
    c: Block(g6)
    c: Block(g7)
    c: Block(g4)
    c: Block(g5)
FEATURE [Part::Extrusion] Extrude054
  Base = -> Sketch063
  Dir = (0,-1,2e-16)
  DirMode = 2
  FaceMakerClass = Part::FaceMakerBullseye
  LengthFwd = 6
  LengthRev = 0
  Placement = pos=(0,9,0) rot=(0,0,1;0rad)
  Solid = true
  Symmetric = false
FEATURE [Sketcher::SketchObject] Sketch064  label="topSketch017"
  FullyConstrained = true
  sketch-geometry (20):
    g0: LineSegment StartX=5.21097e-06 StartY=3 StartZ=0 EndX=5.21097e-06 EndY=19 EndZ=0
    g1: ArcOfCircle CenterX=19 CenterY=19 CenterZ=0 NormalX=0 NormalY=0 NormalZ=1 AngleXU=0 Radius=19 StartAngle=1.5708 EndAngle=3.14159
    g2: ArcOfCircle CenterX=19 CenterY=19 CenterZ=0 NormalX=0 NormalY=0 NormalZ=1 AngleXU=0 Radius=16 StartAngle=1.5708 EndAngle=3.14159
    g3: LineSegment StartX=114 StartY=35 StartZ=0 EndX=19 EndY=35 EndZ=0
    g4: LineSegment StartX=5.21097e-06 StartY=3 StartZ=0 EndX=5.21097e-06 EndY=0 EndZ=0
    g5: LineSegment StartX=3 StartY=0 StartZ=0 EndX=5.21097e-06 EndY=0 EndZ=0
    g6: LineSegment StartX=3 StartY=19 StartZ=0 EndX=3 EndY=0 EndZ=0
    g7: LineSegment StartX=19 StartY=38 StartZ=0 EndX=124 EndY=38 EndZ=0
    g8: Circle CenterX=119 CenterY=35 CenterZ=0 NormalX=0 NormalY=0 NormalZ=1 AngleXU=0 Radius=1
    g9: Circle CenterX=121 CenterY=35 CenterZ=0 NormalX=0 NormalY=0 NormalZ=1 AngleXU=0 Radius=1
    g10: Circle CenterX=121 CenterY=33 CenterZ=0 NormalX=0 NormalY=0 NormalZ=1 AngleXU=0 Radius=1
    g11: BSplineCurve PolesCount=3 KnotsCount=2 Degree=2 IsPeriodic=0
    g12: GeomPoint X=119 Y=35 Z=0
    g13: GeomPoint X=121 Y=33 Z=0
    g14: LineSegment StartX=119 StartY=35 StartZ=0 EndX=114 EndY=35 EndZ=0
    g15: ArcOfCircle CenterX=105 CenterY=19 CenterZ=0 NormalX=0 NormalY=0 NormalZ=1 AngleXU=0 Radius=19 StartAngle=5.7297 EndAngle=6.28319
    g16: ArcOfCircle CenterX=105 CenterY=19 CenterZ=0 NormalX=0 NormalY=0 NormalZ=1 AngleXU=0 Radius=16 StartAngle=5.60905 EndAngle=6.28319
    g17: LineSegment StartX=121 StartY=33 StartZ=0 EndX=121 EndY=19 EndZ=0
    g18: LineSegment StartX=124 StartY=38 StartZ=0 EndX=124 EndY=19 EndZ=0
    g19: LineSegment StartX=117.5 StartY=9.01251 StartZ=0 EndX=121.163 EndY=9.0125 EndZ=0
  constraints (46):
    c: Vertical(g0)
    c: Block(g0)
    c: Coincident(g1,g0)
    c: Block(g1)
    c: Coincident(g2,g1)
    c: Block(g2)
    c: Coincident(g3,g2)
    c: Horizontal(g3)
    c: Tangent(g3,g2)
    c: Coincident(g4,g0)
    c: Distance(g4) = 3
    c: Vertical(g4)
    c: Coincident(g5,g4)
    c: Horizontal(g5)
    c: Coincident(g6,g2)
    c: Coincident(g6,g5)
    c: Vertical(g6)
    c: Horizontal(g7)
    c: Distance(g7) = 105
    c: Coincident(g7,g1)
    c: Block(g3)
    c: Weight(g8) = 1
    c: Equal(g8,g9)
    c: Equal(g8,g10)
    c: InternalAlignment(g8,g11)
    c: InternalAlignment(g9,g11)
    c: InternalAlignment(g10,g11)
    c: InternalAlignment(g12,g11)
    c: InternalAlignment(g13,g11)
    c: Block(g11)
    c: Coincident(g14,g11)
    c: Coincident(g14,g3)
    c: Horizontal(g14)
    c: Block(g15)
    c: Coincident(g16,g15)
    c: Block(g16)
    c: Coincident(g17,g11)
    c: Coincident(g17,g16)
    c: Vertical(g17)
    c: Distance(g17) = 14
    c: Coincident(g18,g7)
    c: Coincident(g18,g15)
    c: Vertical(g18)
    c: Distance(g18) = 19
    c: Coincident(g19,g16)
    c: Coincident(g19,g15)
FEATURE [Sketcher::SketchObject] Sketch065
  FullyConstrained = true
  MapMode = 3
  Placement = pos=(0,0,0) rot=(1,0,0;1.5708rad)
  sketch-geometry (8):
    g0: Circle CenterX=80.351 CenterY=-67.6202 CenterZ=0 NormalX=0 NormalY=0 NormalZ=1 AngleXU=0 Radius=3
    g1: Circle CenterX=80.351 CenterY=-4.92017 CenterZ=0 NormalX=0 NormalY=0 NormalZ=1 AngleXU=0 Radius=3
    g2: Circle CenterX=23.851 CenterY=-4.92017 CenterZ=0 NormalX=0 NormalY=0 NormalZ=1 AngleXU=0 Radius=3
    g3: Circle CenterX=23.851 CenterY=-67.6202 CenterZ=0 NormalX=0 NormalY=0 NormalZ=1 AngleXU=0 Radius=3
    g4: Circle CenterX=23.851 CenterY=-67.6202 CenterZ=0 NormalX=0 NormalY=0 NormalZ=1 AngleXU=0 Radius=5
    g5: Circle CenterX=80.351 CenterY=-67.6202 CenterZ=0 NormalX=0 NormalY=0 NormalZ=1 AngleXU=0 Radius=5
    g6: Circle CenterX=23.851 CenterY=-4.92017 CenterZ=0 NormalX=0 NormalY=0 NormalZ=1 AngleXU=0 Radius=5
    g7: Circle CenterX=80.351 CenterY=-4.92017 CenterZ=0 NormalX=0 NormalY=0 NormalZ=1 AngleXU=0 Radius=5
  constraints (8):
    c: Block(g1)
    c: Block(g0)
    c: Block(g3)
    c: Block(g2)
    c: Block(g5)
    c: Block(g4)
    c: Block(g6)
    c: Block(g7)
FEATURE [Part::Extrusion] Extrude056
  Base = -> Sketch065
  Dir = (0,-1,2e-16)
  DirMode = 2
  FaceMakerClass = Part::FaceMakerBullseye
  LengthFwd = 2
  LengthRev = 0
  Solid = true
  Symmetric = false
FEATURE [Part::Extrusion] Extrude057  label="top025"
  Base = -> Sketch064
  Dir = (0,0,1)
  DirMode = 2
  FaceMakerClass = Part::FaceMakerBullseye
  LengthFwd = 72
  LengthRev = 0
  Solid = true
  Symmetric = false
FEATURE [Sketcher::SketchObject] Sketch066
  FullyConstrained = true
  MapMode = 3
  Placement = pos=(0,0,0) rot=(1,0,0;1.5708rad)
  Support = -> [Extrude057]
  sketch-geometry (8):
    g0: Circle CenterX=80.351 CenterY=-67.6202 CenterZ=0 NormalX=0 NormalY=0 NormalZ=1 AngleXU=0 Radius=3
    g1: Circle CenterX=80.351 CenterY=-4.92017 CenterZ=0 NormalX=0 NormalY=0 NormalZ=1 AngleXU=0 Radius=3
    g2: Circle CenterX=23.851 CenterY=-4.92017 CenterZ=0 NormalX=0 NormalY=0 NormalZ=1 AngleXU=0 Radius=3
    g3: Circle CenterX=23.851 CenterY=-67.6202 CenterZ=0 NormalX=0 NormalY=0 NormalZ=1 AngleXU=0 Radius=3
    g4: Circle CenterX=23.851 CenterY=-67.6202 CenterZ=0 NormalX=0 NormalY=0 NormalZ=1 AngleXU=0 Radius=5
    g5: Circle CenterX=80.351 CenterY=-67.6202 CenterZ=0 NormalX=0 NormalY=0 NormalZ=1 AngleXU=0 Radius=5
    g6: Circle CenterX=23.851 CenterY=-4.92017 CenterZ=0 NormalX=0 NormalY=0 NormalZ=1 AngleXU=0 Radius=5
    g7: Circle CenterX=80.351 CenterY=-4.92017 CenterZ=0 NormalX=0 NormalY=0 NormalZ=1 AngleXU=0 Radius=5
  constraints (8):
    c: Block(g1)
    c: Block(g0)
    c: Block(g3)
    c: Block(g2)
    c: Block(g5)
    c: Block(g4)
    c: Block(g6)
    c: Block(g7)
FEATURE [Part::Extrusion] Extrude055
  Base = -> Sketch066
  Dir = (0,-1,2e-16)
  DirMode = 2
  FaceMakerClass = Part::FaceMakerBullseye
  LengthFwd = 2
  LengthRev = 0
  Solid = true
  Symmetric = false
FEATURE [Part::Fillet] Fillet041
  Base = -> Extrude056
  Edges = 4 edges r=1.99: [Edge6,Edge12,Edge18,Edge24]
FEATURE [Part::Cut] Cut045
  Base = -> Extrude055
  Placement = pos=(0,6,0) rot=(0,0,1;0rad)
  Tool = -> Fillet041
FEATURE [Part::MultiFuse] Fusion095  label="pcbScrewPillars"
  Placement = pos=(-3.2,-1,72.3) rot=(0,0,1;0rad)
  Shapes = -> [Cut045,Extrude054]
FEATURE [Part::Feature] Face113
  shape: bbox 3.2 x 1.5 x 2e-07 mm, 1 faces, 0 solids (baked)
FEATURE [Part::Revolution] Revolve121  label="backCaseScrewRetainer002"
  Angle = 360
  Axis = (0,1,0)
  Base = (0,0,0)
  FaceMakerClass = Part::FaceMakerBullseye
  Placement = pos=(12.5,3,62) rot=(0,0,1;0rad)
  Solid = false
  Source = -> Face113
  Symmetric = false
FEATURE [Part::Feature] Face114
  shape: bbox 3.2 x 1.5 x 2e-07 mm, 1 faces, 0 solids (baked)
FEATURE [Part::Feature] Face115
  shape: bbox 3.2 x 1.5 x 2e-07 mm, 1 faces, 0 solids (baked)
FEATURE [Part::Feature] Face116
  shape: bbox 3.2 x 1.5 x 2e-07 mm, 1 faces, 0 solids (baked)
FEATURE [Part::Revolution] Revolve122  label="frontCaseScrewRetainer004"
  Angle = 360
  Axis = (0,1,0)
  Base = (0,0,0)
  FaceMakerClass = Part::FaceMakerBullseye
  Placement = pos=(89.5,3,68.5) rot=(0,0,1;0rad)
  Solid = false
  Source = -> Face115
  Symmetric = false
FEATURE [Part::Revolution] Revolve123  label="frontCaseScrewRetainer005"
  Angle = 360
  Axis = (0,1,0)
  Base = (0,0,0)
  FaceMakerClass = Part::FaceMakerBullseye
  Placement = pos=(89.5,3,3.5) rot=(0,0,1;0rad)
  Solid = false
  Source = -> Face116
  Symmetric = false
FEATURE [Part::Revolution] Revolve124  label="backCaseScrewRetainer003"
  Angle = 360
  Axis = (0,1,0)
  Base = (0,0,0)
  FaceMakerClass = Part::FaceMakerBullseye
  Placement = pos=(12.5,3,10) rot=(0,0,1;0rad)
  Solid = false
  Source = -> Face114
  Symmetric = false
FEATURE [Part::Feature] Face117
  shape: bbox 3.6 x 3.2 x 2e-07 mm, 1 faces, 0 solids (baked)
FEATURE [Part::Revolution] Revolve125  label="moreFrontCaseScrewRetainer004"
  Angle = 360
  Axis = (0,1,0)
  Base = (0,0,0)
  FaceMakerClass = Part::FaceMakerBullseye
  Placement = pos=(109.5,4.5,68.5) rot=(0,0,1;0rad)
  Solid = false
  Source = -> Face117
  Symmetric = false
FEATURE [Part::Feature] Face118
  shape: bbox 3.6 x 3.2 x 2e-07 mm, 1 faces, 0 solids (baked)
FEATURE [Part::Revolution] Revolve126  label="moreFrontCaseScrewRetainer005"
  Angle = 360
  Axis = (0,1,0)
  Base = (0,0,0)
  FaceMakerClass = Part::FaceMakerBullseye
  Placement = pos=(109.5,4.5,3.5) rot=(0,0,1;0rad)
  Solid = false
  Source = -> Face118
  Symmetric = false
FEATURE [Part::MultiFuse] Fusion096  label="screwRetainers001"
  Shapes = -> [Revolve126,Revolve125,Revolve124,Revolve123,Revolve122,Revolve121]
FEATURE [Part::Feature] Face119
  shape: bbox 10 x 16.5 x 2e-07 mm, 1 faces, 0 solids (baked)
FEATURE [Part::Revolution] Revolve130  label="plugHousing050"
  Angle = 360
  Axis = (0,1,0)
  Base = (0,0,0)
  FaceMakerClass = Part::FaceMakerBullseye
  Placement = pos=(0,0,36.15) rot=(0,0,1;0rad)
  Solid = false
  Source = -> Face119
  Symmetric = false
FEATURE [Part::Feature] Face120
  shape: bbox 10 x 16.5 x 2e-07 mm, 1 faces, 0 solids (baked)
FEATURE [Part::Feature] Face121
  shape: bbox 10 x 16.5 x 2e-07 mm, 1 faces, 0 solids (baked)
FEATURE [Part::Revolution] Revolve127  label="plugHousing047"
  Angle = 360
  Axis = (0,1,0)
  Base = (0,0,0)
  FaceMakerClass = Part::FaceMakerBullseye
  Placement = pos=(0,0,36.15) rot=(0,0,1;0rad)
  Solid = false
  Source = -> Face121
  Symmetric = false
FEATURE [Part::Feature] Face122
  shape: bbox 10 x 16.5 x 2e-07 mm, 1 faces, 0 solids (baked)
FEATURE [Part::Feature] Face123
  shape: bbox 10 x 16.5 x 2e-07 mm, 1 faces, 0 solids (baked)
FEATURE [Part::Revolution] Revolve128  label="plugHousing048"
  Angle = 360
  Axis = (0,1,0)
  Base = (0,0,0)
  FaceMakerClass = Part::FaceMakerBullseye
  Placement = pos=(0,0,36.15) rot=(0,0,1;0rad)
  Solid = false
  Source = -> Face123
  Symmetric = false
FEATURE [Part::MultiFuse] Fusion100  label="plugHousing054"
  Placement = pos=(0,0,0) rot=(0,0,1;1.5708rad)
  Shapes = -> [Revolve130,Revolve128]
FEATURE [Part::Feature] Face124
  shape: bbox 10 x 16.5 x 2e-07 mm, 1 faces, 0 solids (baked)
FEATURE [Part::Feature] Face125
  shape: bbox 10 x 16.5 x 2e-07 mm, 1 faces, 0 solids (baked)
FEATURE [Part::Revolution] Revolve129  label="plugHousing049"
  Angle = 360
  Axis = (0,1,0)
  Base = (0,0,0)
  FaceMakerClass = Part::FaceMakerBullseye
  Placement = pos=(0,0,36.15) rot=(0,0,1;0rad)
  Solid = false
  Source = -> Face125
  Symmetric = false
FEATURE [Part::Feature] Face126
  shape: bbox 10 x 16.5 x 2e-07 mm, 1 faces, 0 solids (baked)
FEATURE [Part::Revolution] Revolve131  label="plugHousing058"
  Angle = 360
  Axis = (0,1,0)
  Base = (0,0,0)
  FaceMakerClass = Part::FaceMakerBullseye
  Placement = pos=(0,0,36.15) rot=(0,0,1;0rad)
  Solid = false
  Source = -> Face120
  Symmetric = false
FEATURE [Part::MultiFuse] Fusion099  label="plugHousing053"
  Placement = pos=(0,0,0) rot=(0,0,1;1.5708rad)
  Shapes = -> [Revolve127,Revolve131]
FEATURE [Part::MultiFuse] Fusion102  label="plugHousing056"
  Placement = pos=(0,19,0) rot=(0,0,1;3.14159rad)
  Shapes = -> [Fusion100,Fusion099]
FEATURE [Part::Revolution] Revolve132  label="plugHousing059"
  Angle = 360
  Axis = (0,1,0)
  Base = (0,0,0)
  FaceMakerClass = Part::FaceMakerBullseye
  Placement = pos=(0,0,36.15) rot=(0,0,1;0rad)
  Solid = false
  Source = -> Face126
  Symmetric = false
FEATURE [Part::Revolution] Revolve133  label="plugHousing060"
  Angle = 360
  Axis = (0,1,0)
  Base = (0,0,0)
  FaceMakerClass = Part::FaceMakerBullseye
  Placement = pos=(0,0,36.15) rot=(0,0,1;0rad)
  Solid = false
  Source = -> Face122
  Symmetric = false
FEATURE [Part::MultiFuse] Fusion097  label="plugHousing051"
  Placement = pos=(0,0,0) rot=(0,0,1;1.5708rad)
  Shapes = -> [Revolve133,Revolve132]
FEATURE [Part::Revolution] Revolve134  label="plugHousing061"
  Angle = 360
  Axis = (0,1,0)
  Base = (0,0,0)
  FaceMakerClass = Part::FaceMakerBullseye
  Placement = pos=(0,0,36.15) rot=(0,0,1;0rad)
  Solid = false
  Source = -> Face124
  Symmetric = false
FEATURE [Part::MultiFuse] Fusion101  label="plugHousing055"
  Placement = pos=(0,0,0) rot=(0,0,1;1.5708rad)
  Shapes = -> [Revolve129,Revolve134]
FEATURE [Part::MultiFuse] Fusion098  label="plugHousing052"
  Placement = pos=(0,19,0) rot=(0,0,1;3.14159rad)
  Shapes = -> [Fusion097,Fusion101]
FEATURE [Part::MultiFuse] Fusion103  label="plugHousing057"
  Placement = pos=(122.621,0,-0.15) rot=(0,0,1;0rad)
  Shapes = -> [Fusion102,Fusion098]
FEATURE [Part::Box] Box028  label="Cube015"
  AttacherType = Attacher::AttachEngine3D
  Height = 28
  Length = 3
  Placement = pos=(110.7,19,22) rot=(0,0,1;0rad)
  Width = 15.7
FEATURE [Part::Cylinder] Cylinder044
  Angle = 360
  AttacherType = Attacher::AttachEngine3D
  Height = 20
  Placement = pos=(0,0,36.15) rot=(0,0,1;0rad)
  Radius = 10.3
FEATURE [Part::Cylinder] Cylinder045
  Angle = 360
  AttacherType = Attacher::AttachEngine3D
  Height = 10
  Placement = pos=(0,0,36.15) rot=(0,0,1;0rad)
  Radius = 4
FEATURE [Part::MultiFuse] Fusion104  label="removeToCreteHoleForPlugHousing040"
  Placement = pos=(70,19,36) rot=(0,1,0;1.5708rad)
  Shapes = -> [Cylinder044,Cylinder045]
FEATURE [Part::Cut] Cut046  label="plugHousingTab003"
  Base = -> Box028
  Tool = -> Fusion104
FEATURE [Part::MultiFuse] Fusion105  label="plugHousing062"
  Shapes = -> [Fusion103,Cut046]
FEATURE [Part::Fillet] Fillet042
  Base = -> Fusion105
  Edges = 1 edges r=2: [Edge25]
FEATURE [Part::Fillet] Fillet043  label="plugHousing063"
  Base = -> Fillet042
  Edges = 1 edges r=2: [Edge8]
  Placement = pos=(7,0,0) rot=(0,0,1;0rad)
FEATURE [Part::Feature] Face127
  shape: bbox 10 x 16.5 x 2e-07 mm, 1 faces, 0 solids (baked)
FEATURE [Part::Feature] Face128
  shape: bbox 10 x 16.5 x 2e-07 mm, 1 faces, 0 solids (baked)
FEATURE [Part::Revolution] Revolve137  label="plugHousing070"
  Angle = 360
  Axis = (0,1,0)
  Base = (0,0,0)
  FaceMakerClass = Part::FaceMakerBullseye
  Placement = pos=(0,0,36.15) rot=(0,0,1;0rad)
  Solid = false
  Source = -> Face127
  Symmetric = false
FEATURE [Part::Revolution] Revolve140  label="plugHousing073"
  Angle = 360
  Axis = (0,1,0)
  Base = (0,0,0)
  FaceMakerClass = Part::FaceMakerBullseye
  Placement = pos=(0,0,36.15) rot=(0,0,1;0rad)
  Solid = false
  Source = -> Face128
  Symmetric = false
FEATURE [Part::Feature] Face129
  shape: bbox 10 x 16.5 x 2e-07 mm, 1 faces, 0 solids (baked)
FEATURE [Part::Revolution] Revolve138  label="plugHousing071"
  Angle = 360
  Axis = (0,1,0)
  Base = (0,0,0)
  FaceMakerClass = Part::FaceMakerBullseye
  Placement = pos=(0,0,36.15) rot=(0,0,1;0rad)
  Solid = false
  Source = -> Face129
  Symmetric = false
FEATURE [Part::Feature] Face130
  shape: bbox 10 x 16.5 x 2e-07 mm, 1 faces, 0 solids (baked)
FEATURE [Part::Revolution] Revolve139  label="plugHousing072"
  Angle = 360
  Axis = (0,1,0)
  Base = (0,0,0)
  FaceMakerClass = Part::FaceMakerBullseye
  Placement = pos=(0,0,36.15) rot=(0,0,1;0rad)
  Solid = false
  Source = -> Face130
  Symmetric = false
FEATURE [Part::Feature] Face131
  shape: bbox 10 x 16.5 x 2e-07 mm, 1 faces, 0 solids (baked)
FEATURE [Part::Revolution] Revolve135  label="plugHousing068"
  Angle = 360
  Axis = (0,1,0)
  Base = (0,0,0)
  FaceMakerClass = Part::FaceMakerBullseye
  Placement = pos=(0,0,36.15) rot=(0,0,1;0rad)
  Solid = false
  Source = -> Face131
  Symmetric = false
FEATURE [Part::MultiFuse] Fusion112  label="plugHousing078"
  Placement = pos=(0,0,0) rot=(0,0,1;1.5708rad)
  Shapes = -> [Revolve135,Revolve139]
FEATURE [Part::Feature] Face132
  shape: bbox 10 x 16.5 x 2e-07 mm, 1 faces, 0 solids (baked)
FEATURE [Part::Revolution] Revolve141  label="plugHousing074"
  Angle = 360
  Axis = (0,1,0)
  Base = (0,0,0)
  FaceMakerClass = Part::FaceMakerBullseye
  Placement = pos=(0,0,36.15) rot=(0,0,1;0rad)
  Solid = false
  Source = -> Face132
  Symmetric = false
FEATURE [Part::MultiFuse] Fusion110  label="plugHousing076"
  Placement = pos=(0,0,0) rot=(0,0,1;1.5708rad)
  Shapes = -> [Revolve141,Revolve140]
FEATURE [Part::Feature] Face133
  shape: bbox 10 x 16.5 x 2e-07 mm, 1 faces, 0 solids (baked)
FEATURE [Part::Revolution] Revolve136  label="plugHousing069"
  Angle = 360
  Axis = (0,1,0)
  Base = (0,0,0)
  FaceMakerClass = Part::FaceMakerBullseye
  Placement = pos=(0,0,36.15) rot=(0,0,1;0rad)
  Solid = false
  Source = -> Face133
  Symmetric = false
FEATURE [Part::MultiFuse] Fusion106  label="plugHousing064"
  Placement = pos=(0,0,0) rot=(0,0,1;1.5708rad)
  Shapes = -> [Revolve138,Revolve136]
FEATURE [Part::MultiFuse] Fusion108  label="plugHousing066"
  Placement = pos=(0,19,0) rot=(0,0,1;3.14159rad)
  Shapes = -> [Fusion106,Fusion112]
FEATURE [Part::Feature] Face134
  shape: bbox 10 x 16.5 x 2e-07 mm, 1 faces, 0 solids (baked)
FEATURE [Part::Revolution] Revolve142  label="plugHousing075"
  Angle = 360
  Axis = (0,1,0)
  Base = (0,0,0)
  FaceMakerClass = Part::FaceMakerBullseye
  Placement = pos=(0,0,36.15) rot=(0,0,1;0rad)
  Solid = false
  Source = -> Face134
  Symmetric = false
FEATURE [Part::MultiFuse] Fusion107  label="plugHousing065"
  Placement = pos=(0,0,0) rot=(0,0,1;1.5708rad)
  Shapes = -> [Revolve137,Revolve142]
FEATURE [Part::MultiFuse] Fusion111  label="plugHousing077"
  Placement = pos=(0,19,0) rot=(0,0,1;3.14159rad)
  Shapes = -> [Fusion110,Fusion107]
FEATURE [Part::MultiFuse] Fusion109  label="plugHousing067"
  Placement = pos=(131.236,0,-0.15) rot=(0,0,1;0rad)
  Shapes = -> [Fusion108,Fusion111]
FEATURE [Part::MultiFuse] Fusion113  label="plugHousing079"
  Shapes = -> [Fillet043,Fusion109]
FEATURE [Part::Feature] Face135
  shape: bbox 3.5 x 17.8 x 2e-07 mm, 1 faces, 0 solids (baked)
FEATURE [Part::Revolution] Revolve143  label="removeToCreateScrewAndThreadedInsertHole049"
  Angle = 360
  Axis = (0,1,0)
  Base = (0,0,0)
  FaceMakerClass = Part::FaceMakerBullseye
  Placement = pos=(12.5,0,10) rot=(0,0,1;0rad)
  Solid = false
  Source = -> Face135
  Symmetric = false
FEATURE [Part::Feature] Face136
  shape: bbox 3.5 x 17.8 x 2e-07 mm, 1 faces, 0 solids (baked)
FEATURE [Part::Revolution] Revolve144  label="removeToCreateScrewAndThreadedInsertHole050"
  Angle = 360
  Axis = (0,1,0)
  Base = (0,0,0)
  FaceMakerClass = Part::FaceMakerBullseye
  Placement = pos=(12.5,0,62) rot=(0,0,1;0rad)
  Solid = false
  Source = -> Face136
  Symmetric = false
FEATURE [Part::Feature] Face137
  shape: bbox 3.5 x 17.8 x 2e-07 mm, 1 faces, 0 solids (baked)
FEATURE [Part::Revolution] Revolve145  label="removeToCreateScrewAndThreadedInsertHole051"
  Angle = 360
  Axis = (0,1,0)
  Base = (0,0,0)
  FaceMakerClass = Part::FaceMakerBullseye
  Placement = pos=(89.5,0,68.5) rot=(0,0,1;0rad)
  Solid = false
  Source = -> Face137
  Symmetric = false
FEATURE [Part::Feature] Face138
  shape: bbox 3.5 x 17.8 x 2e-07 mm, 1 faces, 0 solids (baked)
FEATURE [Part::Revolution] Revolve146  label="removeToCreateScrewAndThreadedInsertHole052"
  Angle = 360
  Axis = (0,1,0)
  Base = (0,0,0)
  FaceMakerClass = Part::FaceMakerBullseye
  Placement = pos=(89.5,0,3.5) rot=(0,0,1;0rad)
  Solid = false
  Source = -> Face138
  Symmetric = false
FEATURE [Part::Feature] Face139
  shape: bbox 3.5 x 17.8 x 2e-07 mm, 1 faces, 0 solids (baked)
FEATURE [Part::Revolution] Revolve147  label="removeToCreateScrewAndThreadedInsertHole053"
  Angle = 360
  Axis = (0,1,0)
  Base = (0,0,0)
  FaceMakerClass = Part::FaceMakerBullseye
  Placement = pos=(109.5,4.7,3.5) rot=(0,0,1;0rad)
  Solid = false
  Source = -> Face139
  Symmetric = false
FEATURE [Part::Feature] Face140
  shape: bbox 3.5 x 17.8 x 2e-07 mm, 1 faces, 0 solids (baked)
FEATURE [Part::Revolution] Revolve148  label="removeToCreateScrewAndThreadedInsertHole054"
  Angle = 360
  Axis = (0,1,0)
  Base = (0,0,0)
  FaceMakerClass = Part::FaceMakerBullseye
  Placement = pos=(109.5,4.7,68.5) rot=(0,0,1;0rad)
  Solid = false
  Source = -> Face140
  Symmetric = false
FEATURE [Part::MultiFuse] Fusion114  label="removeToCreateScrewAndThreadedInsertHole055"
  Shapes = -> [Revolve148,Revolve147,Revolve146,Revolve145,Revolve144,Revolve143]
FEATURE [Part::Cut] Cut047  label="casePillars004"
  Base = -> Cut037
  Tool = -> Fusion114
FEATURE [Part::Feature] Face141
  shape: bbox 3.5 x 17.8 x 2e-07 mm, 1 faces, 0 solids (baked)
FEATURE [Part::Feature] Face142
  shape: bbox 3.5 x 17.8 x 2e-07 mm, 1 faces, 0 solids (baked)
FEATURE [Part::Feature] Face143
  shape: bbox 3.5 x 17.8 x 2e-07 mm, 1 faces, 0 solids (baked)
FEATURE [Part::Revolution] Revolve149  label="removeToCreateScrewAndThreadedInsertHole057"
  Angle = 360
  Axis = (0,1,0)
  Base = (0,0,0)
  FaceMakerClass = Part::FaceMakerBullseye
  Placement = pos=(12.5,0,10) rot=(0,0,1;0rad)
  Solid = false
  Source = -> Face141
  Symmetric = false
FEATURE [Part::Feature] Face144
  shape: bbox 3.5 x 17.8 x 2e-07 mm, 1 faces, 0 solids (baked)
FEATURE [Part::Feature] Face145
  shape: bbox 3.5 x 17.8 x 2e-07 mm, 1 faces, 0 solids (baked)
FEATURE [Part::Feature] Face146
  shape: bbox 3.5 x 17.8 x 2e-07 mm, 1 faces, 0 solids (baked)
FEATURE [Part::Revolution] Revolve150  label="removeToCreateScrewAndThreadedInsertHole058"
  Angle = 360
  Axis = (0,1,0)
  Base = (0,0,0)
  FaceMakerClass = Part::FaceMakerBullseye
  Placement = pos=(12.5,0,62) rot=(0,0,1;0rad)
  Solid = false
  Source = -> Face146
  Symmetric = false
FEATURE [Part::Revolution] Revolve151  label="removeToCreateScrewAndThreadedInsertHole059"
  Angle = 360
  Axis = (0,1,0)
  Base = (0,0,0)
  FaceMakerClass = Part::FaceMakerBullseye
  Placement = pos=(89.5,0,68.5) rot=(0,0,1;0rad)
  Solid = false
  Source = -> Face143
  Symmetric = false
FEATURE [Part::Revolution] Revolve152  label="removeToCreateScrewAndThreadedInsertHole060"
  Angle = 360
  Axis = (0,1,0)
  Base = (0,0,0)
  FaceMakerClass = Part::FaceMakerBullseye
  Placement = pos=(89.5,0,3.5) rot=(0,0,1;0rad)
  Solid = false
  Source = -> Face142
  Symmetric = false
FEATURE [Part::Revolution] Revolve153  label="removeToCreateScrewAndThreadedInsertHole061"
  Angle = 360
  Axis = (0,1,0)
  Base = (0,0,0)
  FaceMakerClass = Part::FaceMakerBullseye
  Placement = pos=(109.5,4.7,3.5) rot=(0,0,1;0rad)
  Solid = false
  Source = -> Face145
  Symmetric = false
FEATURE [Part::Revolution] Revolve154  label="removeToCreateScrewAndThreadedInsertHole062"
  Angle = 360
  Axis = (0,1,0)
  Base = (0,0,0)
  FaceMakerClass = Part::FaceMakerBullseye
  Placement = pos=(109.5,4.7,68.5) rot=(0,0,1;0rad)
  Solid = false
  Source = -> Face144
  Symmetric = false
FEATURE [Part::MultiFuse] Fusion115  label="removeToCreateScrewAndThreadedInsertHole056"
  Shapes = -> [Revolve154,Revolve153,Revolve152,Revolve151,Revolve150,Revolve149]
FEATURE [Part::Feature] Face147
  shape: bbox 9.8 x 26.5 x 2e-07 mm, 1 faces, 0 solids (baked)
FEATURE [Part::Revolution] Revolve155
  Angle = 360
  Axis = (0,1,0)
  Base = (0,0,0)
  FaceMakerClass = Part::FaceMakerBullseye
  Placement = pos=(0,0,0) rot=(0,0,1;1.5708rad)
  Solid = false
  Source = -> Face147
  Symmetric = false
FEATURE [Part::Feature] Face148
  shape: bbox 9.8 x 26.5 x 2e-07 mm, 1 faces, 0 solids (baked)
FEATURE [Part::Revolution] Revolve156
  Angle = 360
  Axis = (0,1,0)
  Base = (0,0,0)
  FaceMakerClass = Part::FaceMakerBullseye
  Placement = pos=(0,0,0) rot=(0,0,1;1.5708rad)
  Solid = false
  Source = -> Face148
  Symmetric = false
FEATURE [Part::MultiFuse] Fusion116
  Placement = pos=(-18,19,36) rot=(0,0,1;0rad)
  Shapes = -> [Revolve156,Revolve155]
FEATURE [Part::Box] Box029  label="Cube016"
  AttacherType = Attacher::AttachEngine3D
  Height = 28
  Length = 3
  Placement = pos=(110.7,19,22) rot=(0,0,1;0rad)
  Width = 15.7
FEATURE [Part::Cylinder] Cylinder046
  Angle = 360
  AttacherType = Attacher::AttachEngine3D
  Height = 10
  Placement = pos=(0,0,36.15) rot=(0,0,1;0rad)
  Radius = 4
FEATURE [Part::Cylinder] Cylinder047
  Angle = 360
  AttacherType = Attacher::AttachEngine3D
  Height = 20
  Placement = pos=(0,0,36.15) rot=(0,0,1;0rad)
  Radius = 10.3
FEATURE [Part::MultiFuse] Fusion117  label="removeToCreteHoleForPlugHousing041"
  Placement = pos=(70,19,36) rot=(0,1,0;1.5708rad)
  Shapes = -> [Cylinder047,Cylinder046]
FEATURE [Part::Cut] Cut049  label="plugHousingTab004"
  Base = -> Box029
  Placement = pos=(-107.4,-14,0) rot=(0,0,1;0rad)
  Tool = -> Fusion117
FEATURE [Part::Box] Box030  label="Cube017"
  AttacherType = Attacher::AttachEngine3D
  Height = 28
  Length = 3
  Placement = pos=(110.7,19,22) rot=(0,0,1;0rad)
  Width = 15.7
FEATURE [Part::Cylinder] Cylinder048
  Angle = 360
  AttacherType = Attacher::AttachEngine3D
  Height = 10
  Placement = pos=(0,0,36.15) rot=(0,0,1;0rad)
  Radius = 4
FEATURE [Part::Cylinder] Cylinder049
  Angle = 360
  AttacherType = Attacher::AttachEngine3D
  Height = 20
  Placement = pos=(0,0,36.15) rot=(0,0,1;0rad)
  Radius = 10.3
FEATURE [Part::MultiFuse] Fusion118  label="removeToCreteHoleForPlugHousing042"
  Placement = pos=(70,19,36) rot=(0,1,0;1.5708rad)
  Shapes = -> [Cylinder049,Cylinder048]
FEATURE [Part::Cut] Cut050  label="plugHousingTab005"
  Base = -> Box030
  Placement = pos=(-107.4,-14,0) rot=(0,0,1;0rad)
  Tool = -> Fusion118
FEATURE [Part::MultiFuse] Fusion119
  Placement = pos=(9.6,23,0) rot=(0,0,1;3.14159rad)
  Shapes = -> [Cut049,Cut050]
FEATURE [Part::Box] Box031  label="Cube018"
  AttacherType = Attacher::AttachEngine3D
  Height = 10
  Length = 3
  Placement = pos=(3.3,4,12) rot=(0,0,1;0rad)
  Width = 10
FEATURE [Part::Fillet] Fillet044
  Base = -> Box031
  Edges = 1 edges r=2: [Edge11]
FEATURE [Part::Box] Box032  label="Cube019"
  AttacherType = Attacher::AttachEngine3D
  Height = 10
  Length = 3
  Placement = pos=(3.3,4,50) rot=(0,0,1;0rad)
  Width = 10
FEATURE [Part::Fillet] Fillet045
  Base = -> Box032
  Edges = 1 edges r=2: [Edge12]
FEATURE [Part::Box] Box033  label="Cube020"
  AttacherType = Attacher::AttachEngine3D
  Height = 28
  Length = 4
  Placement = pos=(5,0,22) rot=(0,0,1;0rad)
  Width = 10
FEATURE [Part::Fillet] Fillet046
  Base = -> Box033
  Edges = 1 edges r=1: [Edge7]
FEATURE [Part::Fillet] Fillet047
  Base = -> Fillet046
  Edges = 1 edges r=2: [Edge5]
FEATURE [Part::Fillet] Fillet048
  Base = -> Fillet047
  Edges = 1 edges r=2: [Edge2]
FEATURE [Part::Cylinder] Cylinder050
  Angle = 360
  AttacherType = Attacher::AttachEngine3D
  Height = 20
  Placement = pos=(0,0,36.15) rot=(0,0,1;0rad)
  Radius = 8.2
FEATURE [Part::Cylinder] Cylinder051
  Angle = 360
  AttacherType = Attacher::AttachEngine3D
  Height = 10
  Placement = pos=(0,0,36.15) rot=(0,0,1;0rad)
  Radius = 4
FEATURE [Part::MultiFuse] Fusion120  label="removeToCreteHoleForPlugHousing043"
  Placement = pos=(-42,19,36) rot=(0,1,0;1.5708rad)
  Shapes = -> [Cylinder050,Cylinder051]
FEATURE [Sketcher::SketchObject] Sketch067  label="topSketch018"
  FullyConstrained = true
  sketch-geometry (4):
    g0: LineSegment StartX=16.8446 StartY=31.512 StartZ=0 EndX=16.3251 EndY=34.4666 EndZ=0
    g1: ArcOfCircle CenterX=19 CenterY=19.2524 CenterZ=0 NormalX=0 NormalY=0 NormalZ=1 AngleXU=0 Radius=15.4476 StartAngle=1.74483 EndAngle=2.72717
    g2: ArcOfCircle CenterX=19 CenterY=19.2524 CenterZ=0 NormalX=0 NormalY=0 NormalZ=1 AngleXU=0 Radius=12.4476 StartAngle=1.74483 EndAngle=2.73189
    g3: LineSegment StartX=4.86004 StartY=25.4725 StartZ=0 EndX=7.58253 EndY=24.2107 EndZ=0
  constraints (7):
    c: Block(g0)
    c: Coincident(g1,g0)
    c: Coincident(g2,g0)
    c: Coincident(g3,g1)
    c: Coincident(g3,g2)
    c: Block(g1)
    c: Block(g2)
FEATURE [Part::Extrusion] Extrude058
  Base = -> Sketch067
  Dir = (0,0,1)
  DirMode = 2
  FaceMakerClass = Part::FaceMakerBullseye
  LengthFwd = 10
  LengthRev = 0
  Placement = pos=(0,0,31) rot=(0,0,1;0rad)
  Solid = true
  Symmetric = false
FEATURE [Part::Cut] Cut051
  Base = -> Extrude058
  Tool = -> Fusion120
FEATURE [Part::Fillet] Fillet049
  Base = -> Cut051
  Edges = 1 edges r=2: [Edge1]
FEATURE [Part::Fillet] Fillet050
  Base = -> Fillet049
  Edges = 1 edges r=2.5: [Edge1]
FEATURE [Part::Fillet] Fillet051
  Base = -> Fillet050
  Edges = 1 edges r=2.5: [Edge2]
FEATURE [Part::MultiFuse] Fusion121  label="wireHolder003"
  Shapes = -> [Fusion116,Fillet051]
FEATURE [Part::MultiFuse] Fusion122
  Shapes = -> [Fillet045,Fusion121]
FEATURE [Part::MultiFuse] Fusion123  label="wireHolder004"
  Shapes = -> [Fusion122,Fillet048]
FEATURE [Part::MultiFuse] Fusion124  label="wireHolder005"
  Shapes = -> [Fillet044,Fusion119,Fusion123]
FEATURE [Sketcher::SketchObject] Sketch068  label="topSketch019"
  FullyConstrained = true
  sketch-geometry (6):
    g0: LineSegment StartX=19 StartY=38 StartZ=0 EndX=117 EndY=38 EndZ=0
    g1: ArcOfCircle CenterX=19 CenterY=19 CenterZ=0 NormalX=0 NormalY=0 NormalZ=1 AngleXU=0 Radius=19 StartAngle=1.5708 EndAngle=3.14159
    g2: LineSegment StartX=117 StartY=38 StartZ=0 EndX=117 EndY=19 EndZ=0
    g3: LineSegment StartX=98 StartY=1.0161e-12 StartZ=0 EndX=5.22862e-06 EndY=1.0161e-12 EndZ=0
    g4: LineSegment StartX=5.22862e-06 StartY=19 StartZ=0 EndX=5.22862e-06 EndY=1.0161e-12 EndZ=0
    g5: ArcOfCircle CenterX=98 CenterY=19 CenterZ=0 NormalX=0 NormalY=0 NormalZ=1 AngleXU=0 Radius=19 StartAngle=4.71239 EndAngle=6.28319
  constraints (16):
    c: Horizontal(g0)
    c: Distance(g0) = 98
    c: Coincident(g1,g0)
    c: Block(g1)
    c: Coincident(g2,g0)
    c: Vertical(g2)
    c: Distance(g2) = 19
    c: Horizontal(g3)
    c: Coincident(g4,g1)
    c: Vertical(g4)
    c: Coincident(g3,g4)
    c: Block(g3)
    c: Coincident(g5,g2)
    c: Coincident(g5,g3)
    c: Block(g0)
    c: Block(g5)
FEATURE [Part::Extrusion] Extrude059  label="sideA002"
  Base = -> Sketch068
  Dir = (0,0,1)
  DirMode = 2
  FaceMakerClass = Part::FaceMakerBullseye
  LengthFwd = 3
  LengthRev = 0
  Placement = pos=(0,0,-2.7) rot=(0,0,1;0rad)
  Solid = true
  Symmetric = false
FEATURE [Sketcher::SketchObject] Sketch069  label="topSketch020"
  FullyConstrained = true
  sketch-geometry (6):
    g0: LineSegment StartX=19 StartY=38 StartZ=0 EndX=117 EndY=38 EndZ=0
    g1: ArcOfCircle CenterX=19 CenterY=19 CenterZ=0 NormalX=0 NormalY=0 NormalZ=1 AngleXU=0 Radius=19 StartAngle=1.5708 EndAngle=3.14159
    g2: LineSegment StartX=117 StartY=38 StartZ=0 EndX=117 EndY=19 EndZ=0
    g3: LineSegment StartX=98 StartY=1.0161e-12 StartZ=0 EndX=5.22862e-06 EndY=1.0161e-12 EndZ=0
    g4: LineSegment StartX=5.22862e-06 StartY=19 StartZ=0 EndX=5.22862e-06 EndY=1.0161e-12 EndZ=0
    g5: ArcOfCircle CenterX=98 CenterY=19 CenterZ=0 NormalX=0 NormalY=0 NormalZ=1 AngleXU=0 Radius=19 StartAngle=4.71239 EndAngle=6.28319
  constraints (16):
    c: Horizontal(g0)
    c: Distance(g0) = 98
    c: Coincident(g1,g0)
    c: Block(g1)
    c: Coincident(g2,g0)
    c: Vertical(g2)
    c: Distance(g2) = 19
    c: Horizontal(g3)
    c: Coincident(g4,g1)
    c: Vertical(g4)
    c: Coincident(g3,g4)
    c: Block(g3)
    c: Coincident(g5,g2)
    c: Coincident(g5,g3)
    c: Block(g0)
    c: Block(g5)
FEATURE [Part::Extrusion] Extrude060  label="sideB002"
  Base = -> Sketch069
  Dir = (0,0,1)
  DirMode = 2
  FaceMakerClass = Part::FaceMakerBullseye
  LengthFwd = 3
  LengthRev = 0
  Placement = pos=(0,0,71.7) rot=(0,0,1;0rad)
  Solid = true
  Symmetric = false
FEATURE [Part::MultiFuse] Fusion127  label="removeFromBottom001"
  Placement = pos=(2,0,0) rot=(0,0,1;0rad)
  Shapes = -> [Extrude059,Extrude060]
FEATURE [Part::Cylinder] Cylinder052
  Angle = 360
  AttacherType = Attacher::AttachEngine3D
  Height = 20
  Placement = pos=(0,0,36.15) rot=(0,0,1;0rad)
  Radius = 14
FEATURE [Part::Cylinder] Cylinder053
  Angle = 360
  AttacherType = Attacher::AttachEngine3D
  Height = 10
  Placement = pos=(0,0,36.15) rot=(0,0,1;0rad)
  Radius = 4
FEATURE [Part::MultiFuse] Fusion128  label="removeToCreteHoleForPlugHousing044"
  Placement = pos=(70,19,36) rot=(0,1,0;1.5708rad)
  Shapes = -> [Cylinder052,Cylinder053]
FEATURE [Part::Cut] Cut052  label="bottom011"
  Base = -> Extrude043
  Tool = -> Fusion128
FEATURE [Part::Cut] Cut054  label="bottom012"
  Base = -> Cut052
  Tool = -> Fusion115
FEATURE [Sketcher::SketchObject] Sketch070
  FullyConstrained = true
  Placement = pos=(117,19,0) rot=(0.57735,0.57735,0.57735;2.0944rad)
  sketch-geometry (48):
    g0: LineSegment StartX=-49.19 StartY=69.25 StartZ=0 EndX=-49.19 EndY=66.25 EndZ=0
    g1: LineSegment StartX=-49.19 StartY=63.5 StartZ=0 EndX=-49.19 EndY=60.5 EndZ=0
    g2: LineSegment StartX=-49.19 StartY=57.75 StartZ=0 EndX=-49.19 EndY=54.75 EndZ=0
    g3: LineSegment StartX=-49.19 StartY=52 StartZ=0 EndX=-49.19 EndY=49 EndZ=0
    g4: LineSegment StartX=-49.19 StartY=46.25 StartZ=0 EndX=-49.19 EndY=43.25 EndZ=0
    g5: LineSegment StartX=-49.19 StartY=40.5 StartZ=0 EndX=-49.19 EndY=37.5 EndZ=0
    g6: LineSegment StartX=-49.19 StartY=34.5 StartZ=0 EndX=-49.19 EndY=31.5 EndZ=0
    g7: LineSegment StartX=-49.19 StartY=28.75 StartZ=0 EndX=-49.19 EndY=25.75 EndZ=0
    g8: LineSegment StartX=-49.19 StartY=23 StartZ=0 EndX=-49.19 EndY=20 EndZ=0
    g9: LineSegment StartX=-49.19 StartY=17.25 StartZ=0 EndX=-49.19 EndY=14.25 EndZ=0
    g10: LineSegment StartX=-49.19 StartY=11.5 StartZ=0 EndX=-49.19 EndY=8.5 EndZ=0
    g11: LineSegment StartX=-49.19 StartY=5.75 StartZ=0 EndX=-49.19 EndY=2.75 EndZ=0
    g12: ArcOfCircle CenterX=-1.5 CenterY=67.75 CenterZ=0 NormalX=0 NormalY=0 NormalZ=1 AngleXU=0 Radius=1.5 StartAngle=4.71239 EndAngle=7.85398
    g13: ArcOfCircle CenterX=-1.5 CenterY=62 CenterZ=0 NormalX=0 NormalY=0 NormalZ=1 AngleXU=0 Radius=1.5 StartAngle=4.71239 EndAngle=7.85398
    g14: ArcOfCircle CenterX=-1.5 CenterY=56.25 CenterZ=0 NormalX=0 NormalY=0 NormalZ=1 AngleXU=0 Radius=1.5 StartAngle=4.71239 EndAngle=7.85398
    g15: ArcOfCircle CenterX=-11.49 CenterY=50.5 CenterZ=0 NormalX=0 NormalY=0 NormalZ=1 AngleXU=0 Radius=1.5 StartAngle=4.71239 EndAngle=7.85398
    g16: ArcOfCircle CenterX=-16.28 CenterY=44.75 CenterZ=0 NormalX=0 NormalY=0 NormalZ=1 AngleXU=0 Radius=1.5 StartAngle=4.71239 EndAngle=7.85398
    g17: ArcOfCircle CenterX=-18.2337 CenterY=39 CenterZ=0 NormalX=0 NormalY=0 NormalZ=1 AngleXU=0 Radius=1.5 StartAngle=4.71485 EndAngle=7.85398
    g18: ArcOfCircle CenterX=-16.2837 CenterY=27.25 CenterZ=0 NormalX=0 NormalY=0 NormalZ=1 AngleXU=0 Radius=1.5 StartAngle=4.71485 EndAngle=7.85398
    g19: ArcOfCircle CenterX=-18.2337 CenterY=33 CenterZ=0 NormalX=0 NormalY=0 NormalZ=1 AngleXU=0 Radius=1.5 StartAngle=4.71485 EndAngle=7.85398
    g20: ArcOfCircle CenterX=-11.49 CenterY=21.5 CenterZ=0 NormalX=0 NormalY=0 NormalZ=1 AngleXU=0 Radius=1.5 StartAngle=4.71239 EndAngle=7.85398
    g21: ArcOfCircle CenterX=-1.5 CenterY=4.25 CenterZ=0 NormalX=0 NormalY=0 NormalZ=1 AngleXU=0 Radius=1.5 StartAngle=4.71239 EndAngle=7.85398
    g22: ArcOfCircle CenterX=-1.5 CenterY=10 CenterZ=0 NormalX=0 NormalY=0 NormalZ=1 AngleXU=0 Radius=1.5 StartAngle=4.71239 EndAngle=7.85398
    g23: ArcOfCircle CenterX=-1.5 CenterY=15.75 CenterZ=0 NormalX=0 NormalY=0 NormalZ=1 AngleXU=0 Radius=1.5 StartAngle=4.71239 EndAngle=7.85398
    g24: LineSegment StartX=-49.19 StartY=69.25 StartZ=0 EndX=-1.5 EndY=69.25 EndZ=0
    g25: LineSegment StartX=-49.19 StartY=66.25 StartZ=0 EndX=-1.5 EndY=66.25 EndZ=0
    g26: LineSegment StartX=-49.19 StartY=63.5 StartZ=0 EndX=-1.5 EndY=63.5 EndZ=0
    g27: LineSegment StartX=-49.19 StartY=60.5 StartZ=0 EndX=-1.5 EndY=60.5 EndZ=0
    g28: LineSegment StartX=-49.19 StartY=57.75 StartZ=0 EndX=-1.5 EndY=57.75 EndZ=0
    g29: LineSegment StartX=-49.19 StartY=54.75 StartZ=0 EndX=-1.5 EndY=54.75 EndZ=0
    g30: LineSegment StartX=-49.19 StartY=52 StartZ=0 EndX=-11.49 EndY=52 EndZ=0
    g31: LineSegment StartX=-49.19 StartY=49 StartZ=0 EndX=-11.49 EndY=49 EndZ=0
    g32: LineSegment StartX=-49.19 StartY=46.25 StartZ=0 EndX=-16.28 EndY=46.25 EndZ=0
    g33: LineSegment StartX=-49.19 StartY=43.25 StartZ=0 EndX=-16.28 EndY=43.25 EndZ=0
    g34: LineSegment StartX=-49.19 StartY=40.5 StartZ=0 EndX=-18.2337 EndY=40.5 EndZ=0
    g35: LineSegment StartX=-49.19 StartY=37.5 StartZ=0 EndX=-18.23 EndY=37.5 EndZ=0
    g36: LineSegment StartX=-49.19 StartY=34.5 StartZ=0 EndX=-18.2337 EndY=34.5 EndZ=0
    g37: LineSegment StartX=-49.19 StartY=31.5 StartZ=0 EndX=-18.23 EndY=31.5 EndZ=0
    g38: LineSegment StartX=-49.19 StartY=28.75 StartZ=0 EndX=-16.2837 EndY=28.75 EndZ=0
    g39: LineSegment StartX=-49.19 StartY=25.75 StartZ=0 EndX=-16.28 EndY=25.75 EndZ=0
    g40: LineSegment StartX=-49.19 StartY=23 StartZ=0 EndX=-11.49 EndY=23 EndZ=0
    g41: LineSegment StartX=-49.19 StartY=20 StartZ=0 EndX=-11.49 EndY=20 EndZ=0
    g42: LineSegment StartX=-49.19 StartY=17.25 StartZ=0 EndX=-1.5 EndY=17.25 EndZ=0
    g43: LineSegment StartX=-49.19 StartY=14.25 StartZ=0 EndX=-1.5 EndY=14.25 EndZ=0
    g44: LineSegment StartX=-49.19 StartY=11.5 StartZ=0 EndX=-1.5 EndY=11.5 EndZ=0
    g45: LineSegment StartX=-49.19 StartY=8.5 StartZ=0 EndX=-1.5 EndY=8.5 EndZ=0
    g46: LineSegment StartX=-49.19 StartY=5.75 StartZ=0 EndX=-1.5 EndY=5.75 EndZ=0
    g47: LineSegment StartX=-49.19 StartY=2.75 StartZ=0 EndX=-1.5 EndY=2.75 EndZ=0
  constraints (120):
    c: Vertical(g0)
    c: Distance(g0) = 3
    c: Block(g0)
    c: Vertical(g1)
    c: Distance(g1) = 3
    c: Vertical(g2)
    c: Equal(g0,g2) = 3
    c: Block(g2)
    c: Vertical(g3)
    c: Equal(g1,g3) = 3
    c: Vertical(g4)
    c: Equal(g0,g4) = 3
    c: Block(g4)
    c: Vertical(g5)
    c: Equal(g1,g5) = 3
    c: Vertical(g6)
    c: Equal(g0,g6) = 3
    c: Block(g6)
    c: Vertical(g7)
    c: Equal(g1,g7) = 3
    c: Vertical(g8)
    c: Equal(g0,g8) = 3
    c: Block(g8)
    c: Vertical(g9)
    c: Equal(g1,g9) = 3
    c: Vertical(g10)
    c: Equal(g0,g10) = 3
    c: Block(g10)
    c: Vertical(g11)
    c: Equal(g1,g11) = 3
    c: Block(g12)
    c: Block(g13)
    c: Block(g14)
    c: Block(g15)
    c: Block(g16)
    c: Block(g17)
    c: Block(g18)
    c: Block(g19)
    c: Block(g20)
    c: Block(g21)
    c: Block(g22)
    c: Block(g23)
    c: Block(g11)
    c: Block(g9)
    c: Block(g7)
    c: Block(g5)
    c: Block(g3)
    c: Block(g1)
    c: Coincident(g24,g0)
    c: Coincident(g24,g12)
    c: Horizontal(g24)
    c: Coincident(g25,g0)
    c: Coincident(g25,g12)
    c: Horizontal(g25)
    c: Coincident(g26,g1)
    c: Coincident(g26,g13)
    c: Horizontal(g26)
    c: Coincident(g27,g1)
    c: Coincident(g27,g13)
    c: Horizontal(g27)
    c: Coincident(g28,g2)
    c: Coincident(g28,g14)
    c: Horizontal(g28)
    c: Coincident(g29,g2)
    c: Coincident(g29,g14)
    c: Horizontal(g29)
    c: Coincident(g30,g3)
    c: Coincident(g30,g15)
    c: Horizontal(g30)
    c: Coincident(g31,g3)
    c: Coincident(g31,g15)
    c: Horizontal(g31)
    c: Coincident(g32,g4)
    c: Coincident(g32,g16)
    c: Horizontal(g32)
    c: Coincident(g33,g4)
    c: Coincident(g33,g16)
    c: Horizontal(g33)
    c: Coincident(g34,g5)
    c: Coincident(g34,g17)
    c: Horizontal(g34)
    c: Coincident(g35,g5)
    c: Coincident(g35,g17)
    c: Horizontal(g35)
    c: Coincident(g36,g6)
    c: Coincident(g36,g19)
    c: Horizontal(g36)
    c: Coincident(g37,g6)
    c: Coincident(g37,g19)
    c: Horizontal(g37)
    c: Coincident(g38,g7)
    c: Coincident(g38,g18)
    c: Horizontal(g38)
    c: Coincident(g39,g7)
    c: Coincident(g39,g18)
    c: Horizontal(g39)
    c: Coincident(g40,g8)
    c: Coincident(g40,g20)
    c: Horizontal(g40)
    c: Coincident(g41,g8)
    c: Coincident(g41,g20)
    c: Horizontal(g41)
    c: Coincident(g42,g9)
    c: Coincident(g42,g23)
    c: Horizontal(g42)
    c: Coincident(g43,g9)
    c: Coincident(g43,g23)
    c: Horizontal(g43)
    c: Coincident(g44,g10)
    c: Coincident(g44,g22)
    c: Horizontal(g44)
    c: Coincident(g45,g10)
    c: Coincident(g45,g22)
    c: Horizontal(g45)
    c: Coincident(g46,g11)
    c: Coincident(g46,g21)
    c: Horizontal(g46)
    c: Coincident(g47,g11)
    c: Coincident(g47,g21)
    c: Horizontal(g47)
FEATURE [Part::Extrusion] Extrude061
  Base = -> Sketch070
  Dir = (1,0,0)
  DirMode = 2
  FaceMakerClass = Part::FaceMakerBullseye
  LengthFwd = 23
  LengthRev = 0
  Placement = pos=(-19,0,0) rot=(0,0,1;0rad)
  Solid = true
  Symmetric = false
FEATURE [Part::Fillet] Fillet052  label="removeToCreateVentalationHoles002"
  Base = -> Extrude061
  Edges = <same value as first occurrence — deduplicated (x6 in doc)>
  Placement = pos=(7,0.02,0) rot=(0,0,1;0rad)
FEATURE [Part::MultiFuse] Fusion130  label="bottom013"
  Shapes = -> [Cut054,Cut034]
FEATURE [Part::Cut] Cut055
  Base = -> Fusion130
  Tool = -> Fillet052
FEATURE [Part::Cylinder] Cylinder054
  Angle = 360
  AttacherType = Attacher::AttachEngine3D
  Height = 20
  Placement = pos=(0,0,36.15) rot=(0,0,1;0rad)
  Radius = 4
FEATURE [Sketcher::SketchObject] Sketch071  label="bottomSketch002"
  FullyConstrained = true
  sketch-geometry (32):
    g0: LineSegment StartX=3.3 StartY=-6.03275e-07 StartZ=0 EndX=98 EndY=-6.03275e-07 EndZ=0
    g1: ArcOfCircle CenterX=98 CenterY=19 CenterZ=0 NormalX=0 NormalY=0 NormalZ=1 AngleXU=0 Radius=19 StartAngle=4.71239 EndAngle=5.71103
    g2: LineSegment StartX=6.3 StartY=8 StartZ=0 EndX=3.3 EndY=8 EndZ=0
    g3: LineSegment StartX=3.3 StartY=8 StartZ=0 EndX=3.3 EndY=-6.03275e-07 EndZ=0
    g4: ArcOfCircle CenterX=8.3 CenterY=5 CenterZ=0 NormalX=0 NormalY=0 NormalZ=1 AngleXU=0 Radius=2 StartAngle=3.14159 EndAngle=4.71239
    g5: LineSegment StartX=6.3 StartY=8 StartZ=0 EndX=6.3 EndY=5 EndZ=0
    g6: ArcOfCircle CenterX=98 CenterY=19 CenterZ=0 NormalX=0 NormalY=0 NormalZ=1 AngleXU=0 Radius=12.7 StartAngle=4.71239 EndAngle=6.28319
    g7: LineSegment StartX=94.7 StartY=3 StartZ=0 EndX=8.3 EndY=3 EndZ=0
    g8-g12: Circle x5 (B-spline internal-alignment scaffolding for g13; pole/knot coordinates omitted)
    g13: BSplineCurve PolesCount=5 KnotsCount=3 Degree=3 IsPeriodic=0
    g14: GeomPoint X=98 Y=6.3 Z=0
    g15: GeomPoint X=96.3938 Y=4.71946 Z=0
    g16: GeomPoint X=94.7 Y=3 Z=0
    g17-g23: Circle x7 (B-spline internal-alignment scaffolding for g24; pole/knot coordinates omitted)
    g24: BSplineCurve PolesCount=7 KnotsCount=5 Degree=3 IsPeriodic=0
    g25-g29: GeomPoint x5 (B-spline internal-alignment scaffolding for g24; pole/knot coordinates omitted)
    g30: ArcOfCircle CenterX=98 CenterY=19 CenterZ=0 NormalX=0 NormalY=0 NormalZ=1 AngleXU=0 Radius=15.7 StartAngle=5.81226 EndAngle=6.28319
    g31: LineSegment StartX=110.7 StartY=19 StartZ=0 EndX=113.7 EndY=19 EndZ=0
  constraints (41):
    c: Horizontal(g0)
    c: Coincident(g1,g0)
    c: Block(g1)
    c: Horizontal(g2)
    c: Distance(g2) = 3
    c: Coincident(g3,g2)
    c: Vertical(g3)
    c: Coincident(g3,g0)
    c: Block(g4)
    c: Block(g2)
    c: Coincident(g5,g2)
    c: Coincident(g5,g4)
    c: Vertical(g5)
    c: Coincident(g6,g1)
    c: Block(g6)
    c: Coincident(g7,g4)
    c: Horizontal(g7)
    c: Block(g0)
    c: Block(g7)
    c: Block(g3)
    c: Coincident(g13,g6)
    c: Weight(g8) = 1
    c: Equal(g8, g9-g12) x4
    c: Coincident(g13,g7)
    c: InternalAlignment(g8-g12 -> g13) x5
    c: InternalAlignment(g14,g13)
    c: InternalAlignment(g15,g13)
    c: InternalAlignment(g16,g13)
    c: Block(g13)
    c: Weight(g17) = 1
    c: Equal(g17, g18-g23) x6
    c: Coincident(g24,g1)
    c: InternalAlignment(g17-g23 -> g24) x7
    c: InternalAlignment(g25-g29 -> g24) x5
    c: Block(g24)
    c: Coincident(g30,g24)
    c: Coincident(g31,g6)
    c: Coincident(g31,g30)
    c: Horizontal(g31)
    c: Block(g31)
    c: Block(g30)
FEATURE [Part::Extrusion] Extrude062  label="bottom014"
  Base = -> Sketch071
  Dir = (0,0,1)
  DirMode = 2
  FaceMakerClass = Part::FaceMakerBullseye
  LengthFwd = 71.4
  LengthRev = 0
  Placement = pos=(0,0,0.3) rot=(0,0,1;0rad)
  Solid = true
  Symmetric = false
FEATURE [Part::Fillet] Fillet054
  Base = -> Extrude062
  Edges = 1 edges r=2.4: [Edge17]
FEATURE [Part::Fillet] Fillet055  label="bottom015"
  Base = -> Fillet054
  Edges = 1 edges r=2.4: [Edge36]
FEATURE [Part::Cylinder] Cylinder055
  Angle = 360
  AttacherType = Attacher::AttachEngine3D
  Height = 10
  Placement = pos=(0,0,36.15) rot=(0,0,1;0rad)
  Radius = 4
FEATURE [Part::MultiFuse] Fusion131  label="removeToCreateHoleForPlugHousing002"
  Placement = pos=(70,19,36.15) rot=(0,1,0;1.5708rad)
  Shapes = -> [Cylinder054,Cylinder055]
FEATURE [Part::Cut] Cut056  label="Bottom001"
  Base = -> Fillet055
  Placement = pos=(9,0,0) rot=(0,0,1;0rad)
  Tool = -> Fusion131
FEATURE [Part::Cut] Cut057
  Base = -> Cut055
  Tool = -> Cut056
FEATURE [Sketcher::SketchObject] Sketch072  label="topSketch021"
  FullyConstrained = true
  sketch-geometry (4):
    g0: ArcOfCircle CenterX=105 CenterY=19 CenterZ=0 NormalX=0 NormalY=0 NormalZ=1 AngleXU=0 Radius=20.6155 StartAngle=5.54125 EndAngle=6.28319
    g1: ArcOfCircle CenterX=105 CenterY=19 CenterZ=0 NormalX=0 NormalY=0 NormalZ=1 AngleXU=0 Radius=13 StartAngle=5.54125 EndAngle=6.28319
    g2: LineSegment StartX=118 StartY=19 StartZ=0 EndX=125.616 EndY=19 EndZ=0
    g3: LineSegment StartX=114.583 StartY=10.2157 StartZ=0 EndX=120.197 EndY=5.06982 EndZ=0
  constraints (7):
    c: Block(g0)
    c: Block(g1)
    c: Coincident(g2,g1)
    c: Coincident(g2,g0)
    c: Horizontal(g2)
    c: Coincident(g3,g1)
    c: Coincident(g3,g0)
FEATURE [Part::Extrusion] Extrude063  label="bottomPlugHousingBit003"
  Base = -> Sketch072
  Dir = (0,0,1)
  DirMode = 2
  FaceMakerClass = Part::FaceMakerBullseye
  LengthFwd = 72
  LengthRev = 0
  Solid = true
  Symmetric = false
FEATURE [Part::Cylinder] Cylinder056
  Angle = 360
  AttacherType = Attacher::AttachEngine3D
  Height = 20
  Placement = pos=(0,0,36.15) rot=(0,0,1;0rad)
  Radius = 14.3
FEATURE [Part::Cylinder] Cylinder057
  Angle = 360
  AttacherType = Attacher::AttachEngine3D
  Height = 10
  Placement = pos=(0,0,36.15) rot=(0,0,1;0rad)
  Radius = 4
FEATURE [Part::Box] Box034  label="removeToCreteHoleForPlugHousing047"
  AttacherType = Attacher::AttachEngine3D
  Height = 28.6
  Length = 20
  Placement = pos=(106.15,0,21.7) rot=(0,0,1;0rad)
  Width = 19
FEATURE [Part::Cylinder] Cylinder058
  Angle = 360
  AttacherType = Attacher::AttachEngine3D
  Height = 20
  Placement = pos=(0,0,36.15) rot=(0,0,1;0rad)
  Radius = 14.3
FEATURE [Part::Cylinder] Cylinder059
  Angle = 360
  AttacherType = Attacher::AttachEngine3D
  Height = 10
  Placement = pos=(0,0,36.15) rot=(0,0,1;0rad)
  Radius = 4
FEATURE [Part::MultiFuse] Fusion134  label="removeToCreteHoleForPlugHousing046"
  Placement = pos=(70,19,36) rot=(0,1,0;1.5708rad)
  Shapes = -> [Cylinder058,Cylinder059]
FEATURE [Part::Cylinder] Cylinder060
  Angle = 360
  AttacherType = Attacher::AttachEngine3D
  Height = 20
  Placement = pos=(0,0,36.15) rot=(0,0,1;0rad)
  Radius = 14
FEATURE [Part::Cylinder] Cylinder061
  Angle = 360
  AttacherType = Attacher::AttachEngine3D
  Height = 10
  Placement = pos=(0,0,36.15) rot=(0,0,1;0rad)
  Radius = 4
FEATURE [Part::MultiFuse] Fusion135  label="removeToCreteHoleForPlugHousing048"
  Placement = pos=(70,19,36) rot=(0,1,0;1.5708rad)
  Shapes = -> [Cylinder060,Cylinder061]
FEATURE [Part::Box] Box035  label="removeToCreteHoleForPlugHousing049"
  AttacherType = Attacher::AttachEngine3D
  Height = 28.6
  Length = 20
  Placement = pos=(106.15,0,21.7) rot=(0,0,1;0rad)
  Width = 19
FEATURE [Part::MultiFuse] Fusion133  label="removeToCreteHoleForPlugHousing045"
  Placement = pos=(0,0,-28.3) rot=(0,0,1;0rad)
  Shapes = -> [Box035,Fusion134]
FEATURE [Part::MultiFuse] Fusion138  label="removeToCreteHoleForPlugHousing051"
  Placement = pos=(70,19,36) rot=(0,1,0;1.5708rad)
  Shapes = -> [Cylinder056,Cylinder057]
FEATURE [Part::MultiFuse] Fusion137  label="removeToCreteHoleForPlugHousing050"
  Placement = pos=(0,0,28.3) rot=(0,0,1;0rad)
  Shapes = -> [Box034,Fusion138]
FEATURE [Part::MultiFuse] Fusion132  label="removeToCreatePlugHousingBottomBit002"
  Shapes = -> [Fusion133,Fusion137]
FEATURE [Part::MultiFuse] Fusion136  label="removeToCreatePlugHousingBottomBit003"
  Shapes = -> [Fusion135,Fusion132]
FEATURE [Part::Cut] Cut058  label="bottomPlugHousingBit002"
  Base = -> Extrude063
  Placement = pos=(-0.09,0,0) rot=(0,0,1;0rad)
  Tool = -> Fusion136
FEATURE [Sketcher::SketchObject] Sketch073  label="bottomSketch003"
  FullyConstrained = true
  sketch-geometry (45):
    g0: LineSegment StartX=6.29999 StartY=8 StartZ=0 EndX=3.29999 EndY=8 EndZ=0
    g1: LineSegment StartX=3.29999 StartY=8 StartZ=0 EndX=3.29999 EndY=-6.03275e-07 EndZ=0
    g2: ArcOfCircle CenterX=8.29999 CenterY=5 CenterZ=0 NormalX=0 NormalY=0 NormalZ=1 AngleXU=0 Radius=2 StartAngle=3.14159 EndAngle=4.71239
    g3: LineSegment StartX=6.29999 StartY=8 StartZ=0 EndX=6.29999 EndY=5 EndZ=0
    g4: ArcOfCircle CenterX=105 CenterY=19 CenterZ=0 NormalX=0 NormalY=0 NormalZ=1 AngleXU=0 Radius=12.7 StartAngle=4.71239 EndAngle=5.94289
    g5-g11: Circle x7 (B-spline internal-alignment scaffolding for g12; pole/knot coordinates omitted)
    g12: BSplineCurve PolesCount=7 KnotsCount=5 Degree=3 IsPeriodic=0
    g13-g17: GeomPoint x5 (B-spline internal-alignment scaffolding for g12; pole/knot coordinates omitted)
    g18: ArcOfCircle CenterX=105 CenterY=19 CenterZ=0 NormalX=0 NormalY=0 NormalZ=1 AngleXU=0 Radius=15.7 StartAngle=5.81226 EndAngle=6.28319
    g19: BSplineCurve PolesCount=5 KnotsCount=3 Degree=3 IsPeriodic=0
    g20: LineSegment StartX=8.29999 StartY=3 StartZ=0 EndX=101.7 EndY=3 EndZ=0
    g21: LineSegment StartX=3.29999 StartY=-6.03275e-07 StartZ=0 EndX=105 EndY=-6.03275e-07 EndZ=0
    g22: LineSegment StartX=120.974 StartY=8.71251 StartZ=0 EndX=122.332 EndY=7.83778 EndZ=0
    g23: LineSegment StartX=105 StartY=-6.03274e-07 StartZ=0 EndX=113 EndY=-6.03274e-07 EndZ=0
    g24: ArcOfCircle CenterX=105 CenterY=19 CenterZ=0 NormalX=0 NormalY=0 NormalZ=1 AngleXU=0 Radius=20.6155 StartAngle=5.11091 EndAngle=5.71103
    g25: ArcOfCircle CenterX=117.7 CenterY=19 CenterZ=0 NormalX=0 NormalY=0 NormalZ=1 AngleXU=0 Radius=3 StartAngle=1.2e-15 EndAngle=2.10468
    g26: Circle CenterX=116.345 CenterY=16.3232 CenterZ=0 NormalX=0 NormalY=0 NormalZ=1 AngleXU=0 Radius=1
    g27: Circle CenterX=117.24 CenterY=15.7584 CenterZ=0 NormalX=0 NormalY=0 NormalZ=1 AngleXU=0 Radius=1
    g28: Circle CenterX=116.972 CenterY=14.7612 CenterZ=0 NormalX=0 NormalY=0 NormalZ=1 AngleXU=0 Radius=1
    g29: BSplineCurve PolesCount=3 KnotsCount=2 Degree=2 IsPeriodic=0
    g30: GeomPoint X=116.345 Y=16.3232 Z=0
    g31: GeomPoint X=116.972 Y=14.7612 Z=0
    g32: Circle CenterX=115.828 CenterY=17.157 CenterZ=0 NormalX=0 NormalY=0 NormalZ=1 AngleXU=0 Radius=1
    g33: Circle CenterX=115.841 CenterY=16.639 CenterZ=0 NormalX=0 NormalY=0 NormalZ=1 AngleXU=0 Radius=1
    g34: Circle CenterX=116.345 CenterY=16.3232 CenterZ=0 NormalX=0 NormalY=0 NormalZ=1 AngleXU=0 Radius=1
    g35: BSplineCurve PolesCount=3 KnotsCount=2 Degree=2 IsPeriodic=0
    g36: GeomPoint X=115.828 Y=17.157 Z=0
    g37: GeomPoint X=116.345 Y=16.3232 Z=0
    g38: LineSegment StartX=115.828 StartY=17.157 StartZ=0 EndX=115.828 EndY=20.8307 EndZ=0
    g39: Circle CenterX=115.828 CenterY=20.8307 CenterZ=0 NormalX=0 NormalY=0 NormalZ=1 AngleXU=0 Radius=1
    g40: Circle CenterX=115.831 CenterY=21.3396 CenterZ=0 NormalX=0 NormalY=0 NormalZ=1 AngleXU=0 Radius=1
    g41: Circle CenterX=116.173 CenterY=21.5825 CenterZ=0 NormalX=0 NormalY=0 NormalZ=1 AngleXU=0 Radius=1
    g42: BSplineCurve PolesCount=3 KnotsCount=2 Degree=2 IsPeriodic=0
    g43: GeomPoint X=115.828 Y=20.8307 Z=0
    g44: GeomPoint X=116.173 Y=21.5825 Z=0
  constraints (70):
    c: Horizontal(g0)
    c: Distance(g0) = 3
    c: Coincident(g1,g0)
    c: Vertical(g1)
    c: Block(g2)
    c: Block(g0)
    c: Coincident(g3,g0)
    c: Coincident(g3,g2)
    c: Vertical(g3)
    c: Block(g1)
    c: Block(g4)
    c: Coincident(g19,g4)
    c: Block(g19)
    c: Equal(g5, g6-g11) x6
    c: InternalAlignment(g5-g11 -> g12) x7
    c: InternalAlignment(g13-g17 -> g12) x5
    c: Block(g12)
    c: Coincident(g18,g12)
    c: Block(g18)
    c: Coincident(g20,g2)
    c: Coincident(g20,g19)
    c: Horizontal(g20)
    c: Distance(g20) = 93.4
    c: Coincident(g21,g1)
    c: Horizontal(g21)
    c: Distance(g21) = 101.7
    c: Horizontal(g23)
    c: Distance(g23) = 8
    c: Coincident(g24,g23)
    c: Block(g23)
    c: Coincident(g22,g24)
    c: Block(g24)
    c: Block(g22)
    c: Distance(g22) = 1.61553
    c: Coincident(g25,g18)
    c: Block(g25)
    c: Weight(g26) = 1
    c: Equal(g26,g27)
    c: Equal(g26,g28)
    c: Coincident(g29,g4)
    c: InternalAlignment(g26,g29)
    c: InternalAlignment(g27,g29)
    c: InternalAlignment(g28,g29)
    c: InternalAlignment(g30,g29)
    c: InternalAlignment(g31,g29)
    c: Block(g29)
    c: Weight(g32) = 1
    c: Equal(g32,g33)
    c: Equal(g32,g34)
    c: Coincident(g35,g29)
    c: InternalAlignment(g32,g35)
    c: InternalAlignment(g33,g35)
    c: InternalAlignment(g34,g35)
    c: InternalAlignment(g36,g35)
    c: InternalAlignment(g37,g35)
    c: Block(g35)
    c: Coincident(g38,g35)
    c: Vertical(g38)
    c: Block(g38)
    c: Coincident(g42,g38)
    c: Weight(g39) = 1
    c: Equal(g39,g40)
    c: Equal(g39,g41)
    c: Coincident(g42,g25)
    c: InternalAlignment(g39,g42)
    c: InternalAlignment(g40,g42)
    c: InternalAlignment(g41,g42)
    c: InternalAlignment(g43,g42)
    c: InternalAlignment(g44,g42)
    c: Block(g42)
FEATURE [Part::Extrusion] Extrude064  label="bottom016"
  Base = -> Sketch073
  Dir = (0,0,1)
  DirMode = 2
  FaceMakerClass = Part::FaceMakerBullseye
  LengthFwd = 71.4
  LengthRev = 0
  Placement = pos=(0,0,0.3) rot=(0,0,1;0rad)
  Solid = true
  Symmetric = false
FEATURE [Part::Revolution] Revolve157  label="removeToCreateScrewAndThreadedInsertHole063"
  Angle = 360
  Axis = (0,1,0)
  Base = (0,0,0)
  FaceMakerClass = Part::FaceMakerBullseye
  Placement = pos=(12.5,0,10) rot=(0,0,1;0rad)
  Solid = false
  Source = -> Face141
  Symmetric = false
FEATURE [Sketcher::SketchObject] Sketch074
  FullyConstrained = true
  Placement = pos=(117,19,0) rot=(0.57735,0.57735,0.57735;2.0944rad)
  sketch-geometry (48):
    g0: LineSegment StartX=-49.19 StartY=69.25 StartZ=0 EndX=-49.19 EndY=66.25 EndZ=0
    g1: LineSegment StartX=-49.19 StartY=63.5 StartZ=0 EndX=-49.19 EndY=60.5 EndZ=0
    g2: LineSegment StartX=-49.19 StartY=57.75 StartZ=0 EndX=-49.19 EndY=54.75 EndZ=0
    g3: LineSegment StartX=-49.19 StartY=52 StartZ=0 EndX=-49.19 EndY=49 EndZ=0
    g4: LineSegment StartX=-49.19 StartY=46.25 StartZ=0 EndX=-49.19 EndY=43.25 EndZ=0
    g5: LineSegment StartX=-49.19 StartY=40.5 StartZ=0 EndX=-49.19 EndY=37.5 EndZ=0
    g6: LineSegment StartX=-49.19 StartY=34.5 StartZ=0 EndX=-49.19 EndY=31.5 EndZ=0
    g7: LineSegment StartX=-49.19 StartY=28.75 StartZ=0 EndX=-49.19 EndY=25.75 EndZ=0
    g8: LineSegment StartX=-49.19 StartY=23 StartZ=0 EndX=-49.19 EndY=20 EndZ=0
    g9: LineSegment StartX=-49.19 StartY=17.25 StartZ=0 EndX=-49.19 EndY=14.25 EndZ=0
    g10: LineSegment StartX=-49.19 StartY=11.5 StartZ=0 EndX=-49.19 EndY=8.5 EndZ=0
    g11: LineSegment StartX=-49.19 StartY=5.75 StartZ=0 EndX=-49.19 EndY=2.75 EndZ=0
    g12: ArcOfCircle CenterX=-1.5 CenterY=67.75 CenterZ=0 NormalX=0 NormalY=0 NormalZ=1 AngleXU=0 Radius=1.5 StartAngle=4.71239 EndAngle=7.85398
    g13: ArcOfCircle CenterX=-1.5 CenterY=62 CenterZ=0 NormalX=0 NormalY=0 NormalZ=1 AngleXU=0 Radius=1.5 StartAngle=4.71239 EndAngle=7.85398
    g14: ArcOfCircle CenterX=-1.5 CenterY=56.25 CenterZ=0 NormalX=0 NormalY=0 NormalZ=1 AngleXU=0 Radius=1.5 StartAngle=4.71239 EndAngle=7.85398
    g15: ArcOfCircle CenterX=-11.49 CenterY=50.5 CenterZ=0 NormalX=0 NormalY=0 NormalZ=1 AngleXU=0 Radius=1.5 StartAngle=4.71239 EndAngle=7.85398
    g16: ArcOfCircle CenterX=-16.28 CenterY=44.75 CenterZ=0 NormalX=0 NormalY=0 NormalZ=1 AngleXU=0 Radius=1.5 StartAngle=4.71239 EndAngle=7.85398
    g17: ArcOfCircle CenterX=-18.2337 CenterY=39 CenterZ=0 NormalX=0 NormalY=0 NormalZ=1 AngleXU=0 Radius=1.5 StartAngle=4.71485 EndAngle=7.85398
    g18: ArcOfCircle CenterX=-16.2837 CenterY=27.25 CenterZ=0 NormalX=0 NormalY=0 NormalZ=1 AngleXU=0 Radius=1.5 StartAngle=4.71485 EndAngle=7.85398
    g19: ArcOfCircle CenterX=-18.2337 CenterY=33 CenterZ=0 NormalX=0 NormalY=0 NormalZ=1 AngleXU=0 Radius=1.5 StartAngle=4.71485 EndAngle=7.85398
    g20: ArcOfCircle CenterX=-11.49 CenterY=21.5 CenterZ=0 NormalX=0 NormalY=0 NormalZ=1 AngleXU=0 Radius=1.5 StartAngle=4.71239 EndAngle=7.85398
    g21: ArcOfCircle CenterX=-1.5 CenterY=4.25 CenterZ=0 NormalX=0 NormalY=0 NormalZ=1 AngleXU=0 Radius=1.5 StartAngle=4.71239 EndAngle=7.85398
    g22: ArcOfCircle CenterX=-1.5 CenterY=10 CenterZ=0 NormalX=0 NormalY=0 NormalZ=1 AngleXU=0 Radius=1.5 StartAngle=4.71239 EndAngle=7.85398
    g23: ArcOfCircle CenterX=-1.5 CenterY=15.75 CenterZ=0 NormalX=0 NormalY=0 NormalZ=1 AngleXU=0 Radius=1.5 StartAngle=4.71239 EndAngle=7.85398
    g24: LineSegment StartX=-49.19 StartY=69.25 StartZ=0 EndX=-1.5 EndY=69.25 EndZ=0
    g25: LineSegment StartX=-49.19 StartY=66.25 StartZ=0 EndX=-1.5 EndY=66.25 EndZ=0
    g26: LineSegment StartX=-49.19 StartY=63.5 StartZ=0 EndX=-1.5 EndY=63.5 EndZ=0
    g27: LineSegment StartX=-49.19 StartY=60.5 StartZ=0 EndX=-1.5 EndY=60.5 EndZ=0
    g28: LineSegment StartX=-49.19 StartY=57.75 StartZ=0 EndX=-1.5 EndY=57.75 EndZ=0
    g29: LineSegment StartX=-49.19 StartY=54.75 StartZ=0 EndX=-1.5 EndY=54.75 EndZ=0
    g30: LineSegment StartX=-49.19 StartY=52 StartZ=0 EndX=-11.49 EndY=52 EndZ=0
    g31: LineSegment StartX=-49.19 StartY=49 StartZ=0 EndX=-11.49 EndY=49 EndZ=0
    g32: LineSegment StartX=-49.19 StartY=46.25 StartZ=0 EndX=-16.28 EndY=46.25 EndZ=0
    g33: LineSegment StartX=-49.19 StartY=43.25 StartZ=0 EndX=-16.28 EndY=43.25 EndZ=0
    g34: LineSegment StartX=-49.19 StartY=40.5 StartZ=0 EndX=-18.2337 EndY=40.5 EndZ=0
    g35: LineSegment StartX=-49.19 StartY=37.5 StartZ=0 EndX=-18.23 EndY=37.5 EndZ=0
    g36: LineSegment StartX=-49.19 StartY=34.5 StartZ=0 EndX=-18.2337 EndY=34.5 EndZ=0
    g37: LineSegment StartX=-49.19 StartY=31.5 StartZ=0 EndX=-18.23 EndY=31.5 EndZ=0
    g38: LineSegment StartX=-49.19 StartY=28.75 StartZ=0 EndX=-16.2837 EndY=28.75 EndZ=0
    g39: LineSegment StartX=-49.19 StartY=25.75 StartZ=0 EndX=-16.28 EndY=25.75 EndZ=0
    g40: LineSegment StartX=-49.19 StartY=23 StartZ=0 EndX=-11.49 EndY=23 EndZ=0
    g41: LineSegment StartX=-49.19 StartY=20 StartZ=0 EndX=-11.49 EndY=20 EndZ=0
    g42: LineSegment StartX=-49.19 StartY=17.25 StartZ=0 EndX=-1.5 EndY=17.25 EndZ=0
    g43: LineSegment StartX=-49.19 StartY=14.25 StartZ=0 EndX=-1.5 EndY=14.25 EndZ=0
    g44: LineSegment StartX=-49.19 StartY=11.5 StartZ=0 EndX=-1.5 EndY=11.5 EndZ=0
    g45: LineSegment StartX=-49.19 StartY=8.5 StartZ=0 EndX=-1.5 EndY=8.5 EndZ=0
    g46: LineSegment StartX=-49.19 StartY=5.75 StartZ=0 EndX=-1.5 EndY=5.75 EndZ=0
    g47: LineSegment StartX=-49.19 StartY=2.75 StartZ=0 EndX=-1.5 EndY=2.75 EndZ=0
  constraints (120):
    c: Vertical(g0)
    c: Distance(g0) = 3
    c: Block(g0)
    c: Vertical(g1)
    c: Distance(g1) = 3
    c: Vertical(g2)
    c: Equal(g0,g2) = 3
    c: Block(g2)
    c: Vertical(g3)
    c: Equal(g1,g3) = 3
    c: Vertical(g4)
    c: Equal(g0,g4) = 3
    c: Block(g4)
    c: Vertical(g5)
    c: Equal(g1,g5) = 3
    c: Vertical(g6)
    c: Equal(g0,g6) = 3
    c: Block(g6)
    c: Vertical(g7)
    c: Equal(g1,g7) = 3
    c: Vertical(g8)
    c: Equal(g0,g8) = 3
    c: Block(g8)
    c: Vertical(g9)
    c: Equal(g1,g9) = 3
    c: Vertical(g10)
    c: Equal(g0,g10) = 3
    c: Block(g10)
    c: Vertical(g11)
    c: Equal(g1,g11) = 3
    c: Block(g12)
    c: Block(g13)
    c: Block(g14)
    c: Block(g15)
    c: Block(g16)
    c: Block(g17)
    c: Block(g18)
    c: Block(g19)
    c: Block(g20)
    c: Block(g21)
    c: Block(g22)
    c: Block(g23)
    c: Block(g11)
    c: Block(g9)
    c: Block(g7)
    c: Block(g5)
    c: Block(g3)
    c: Block(g1)
    c: Coincident(g24,g0)
    c: Coincident(g24,g12)
    c: Horizontal(g24)
    c: Coincident(g25,g0)
    c: Coincident(g25,g12)
    c: Horizontal(g25)
    c: Coincident(g26,g1)
    c: Coincident(g26,g13)
    c: Horizontal(g26)
    c: Coincident(g27,g1)
    c: Coincident(g27,g13)
    c: Horizontal(g27)
    c: Coincident(g28,g2)
    c: Coincident(g28,g14)
    c: Horizontal(g28)
    c: Coincident(g29,g2)
    c: Coincident(g29,g14)
    c: Horizontal(g29)
    c: Coincident(g30,g3)
    c: Coincident(g30,g15)
    c: Horizontal(g30)
    c: Coincident(g31,g3)
    c: Coincident(g31,g15)
    c: Horizontal(g31)
    c: Coincident(g32,g4)
    c: Coincident(g32,g16)
    c: Horizontal(g32)
    c: Coincident(g33,g4)
    c: Coincident(g33,g16)
    c: Horizontal(g33)
    c: Coincident(g34,g5)
    c: Coincident(g34,g17)
    c: Horizontal(g34)
    c: Coincident(g35,g5)
    c: Coincident(g35,g17)
    c: Horizontal(g35)
    c: Coincident(g36,g6)
    c: Coincident(g36,g19)
    c: Horizontal(g36)
    c: Coincident(g37,g6)
    c: Coincident(g37,g19)
    c: Horizontal(g37)
    c: Coincident(g38,g7)
    c: Coincident(g38,g18)
    c: Horizontal(g38)
    c: Coincident(g39,g7)
    c: Coincident(g39,g18)
    c: Horizontal(g39)
    c: Coincident(g40,g8)
    c: Coincident(g40,g20)
    c: Horizontal(g40)
    c: Coincident(g41,g8)
    c: Coincident(g41,g20)
    c: Horizontal(g41)
    c: Coincident(g42,g9)
    c: Coincident(g42,g23)
    c: Horizontal(g42)
    c: Coincident(g43,g9)
    c: Coincident(g43,g23)
    c: Horizontal(g43)
    c: Coincident(g44,g10)
    c: Coincident(g44,g22)
    c: Horizontal(g44)
    c: Coincident(g45,g10)
    c: Coincident(g45,g22)
    c: Horizontal(g45)
    c: Coincident(g46,g11)
    c: Coincident(g46,g21)
    c: Horizontal(g46)
    c: Coincident(g47,g11)
    c: Coincident(g47,g21)
    c: Horizontal(g47)
FEATURE [Part::Extrusion] Extrude065
  Base = -> Sketch074
  Dir = (1,0,0)
  DirMode = 2
  FaceMakerClass = Part::FaceMakerBullseye
  LengthFwd = 23
  LengthRev = 0
  Placement = pos=(-19,0,0) rot=(0,0,1;0rad)
  Solid = true
  Symmetric = false
FEATURE [Part::Fillet] Fillet056  label="removeToCreateVentalationHoles003"
  Base = -> Extrude065
  Edges = <same value as first occurrence — deduplicated (x6 in doc)>
  Placement = pos=(7,0.02,0) rot=(0,0,1;0rad)
FEATURE [Part::Revolution] Revolve158  label="removeToCreateScrewAndThreadedInsertHole065"
  Angle = 360
  Axis = (0,1,0)
  Base = (0,0,0)
  FaceMakerClass = Part::FaceMakerBullseye
  Placement = pos=(12.5,0,62) rot=(0,0,1;0rad)
  Solid = false
  Source = -> Face146
  Symmetric = false
FEATURE [Part::Revolution] Revolve159  label="removeToCreateScrewAndThreadedInsertHole066"
  Angle = 360
  Axis = (0,1,0)
  Base = (0,0,0)
  FaceMakerClass = Part::FaceMakerBullseye
  Placement = pos=(89.5,0,68.5) rot=(0,0,1;0rad)
  Solid = false
  Source = -> Face143
  Symmetric = false
FEATURE [Part::Revolution] Revolve160  label="removeToCreateScrewAndThreadedInsertHole067"
  Angle = 360
  Axis = (0,1,0)
  Base = (0,0,0)
  FaceMakerClass = Part::FaceMakerBullseye
  Placement = pos=(89.5,0,3.5) rot=(0,0,1;0rad)
  Solid = false
  Source = -> Face142
  Symmetric = false
FEATURE [Part::Revolution] Revolve161  label="removeToCreateScrewAndThreadedInsertHole068"
  Angle = 360
  Axis = (0,1,0)
  Base = (0,0,0)
  FaceMakerClass = Part::FaceMakerBullseye
  Placement = pos=(109.5,4.7,3.5) rot=(0,0,1;0rad)
  Solid = false
  Source = -> Face145
  Symmetric = false
FEATURE [Part::Revolution] Revolve162  label="removeToCreateScrewAndThreadedInsertHole069"
  Angle = 360
  Axis = (0,1,0)
  Base = (0,0,0)
  FaceMakerClass = Part::FaceMakerBullseye
  Placement = pos=(109.5,4.7,68.5) rot=(0,0,1;0rad)
  Solid = false
  Source = -> Face144
  Symmetric = false
FEATURE [Part::MultiFuse] Fusion141  label="removeToCreateScrewAndThreadedInsertHole064"
  Shapes = -> [Revolve162,Revolve161,Revolve160,Revolve159,Revolve158,Revolve157]
FEATURE [Part::Cylinder] Cylinder062
  Angle = 360
  AttacherType = Attacher::AttachEngine3D
  Height = 20
  Placement = pos=(0,0,36.15) rot=(0,0,1;0rad)
  Radius = 14
FEATURE [Part::Cylinder] Cylinder063
  Angle = 360
  AttacherType = Attacher::AttachEngine3D
  Height = 10
  Placement = pos=(0,0,36.15) rot=(0,0,1;0rad)
  Radius = 4
FEATURE [Part::MultiFuse] Fusion139  label="removeToCreteHoleForPlugHousing052"
  Placement = pos=(70,19,36) rot=(0,1,0;1.5708rad)
  Shapes = -> [Cylinder062,Cylinder063]
FEATURE [Part::Cut] Cut060  label="bottom017"
  Base = -> Extrude064
  Tool = -> Fusion139
FEATURE [Part::Cut] Cut061  label="bottom019"
  Base = -> Cut060
  Tool = -> Fusion141
FEATURE [Part::MultiFuse] Fusion140  label="bottom018"
  Shapes = -> [Cut061,Cut058]
FEATURE [Part::Cut] Cut059  label="bottom020"
  Base = -> Fusion140
  Tool = -> Fillet056
FEATURE [Part::Box] Box036  label="Cube021"
  AttacherType = Attacher::AttachEngine3D
  Height = 80
  Length = 26
  Placement = pos=(0,-1,-5) rot=(0,0,1;0rad)
  Width = 11
FEATURE [Part::Cut] Cut062  label="removeFromBottom002"
  Base = -> Cut057
  Tool = -> Box036
FEATURE [Part::Cut] Cut063
  Base = -> Cut059
  Tool = -> Cut062
FEATURE [Part::Cut] Cut064  label="pcbStands"
  Base = -> Fusion095
  Tool = -> Fusion127
FEATURE [Sketcher::SketchObject] Sketch075  label="topSketch022"
  FullyConstrained = true
  sketch-geometry (6):
    g0: LineSegment StartX=19 StartY=38 StartZ=0 EndX=117 EndY=38 EndZ=0
    g1: ArcOfCircle CenterX=19 CenterY=19 CenterZ=0 NormalX=0 NormalY=0 NormalZ=1 AngleXU=0 Radius=19 StartAngle=1.5708 EndAngle=3.14159
    g2: LineSegment StartX=117 StartY=38 StartZ=0 EndX=117 EndY=19 EndZ=0
    g3: LineSegment StartX=98 StartY=1.0161e-12 StartZ=0 EndX=5.22862e-06 EndY=1.0161e-12 EndZ=0
    g4: LineSegment StartX=5.22862e-06 StartY=19 StartZ=0 EndX=5.22862e-06 EndY=1.0161e-12 EndZ=0
    g5: ArcOfCircle CenterX=98 CenterY=19 CenterZ=0 NormalX=0 NormalY=0 NormalZ=1 AngleXU=0 Radius=19 StartAngle=4.71239 EndAngle=6.28319
  constraints (16):
    c: Horizontal(g0)
    c: Distance(g0) = 98
    c: Coincident(g1,g0)
    c: Block(g1)
    c: Coincident(g2,g0)
    c: Vertical(g2)
    c: Distance(g2) = 19
    c: Horizontal(g3)
    c: Coincident(g4,g1)
    c: Vertical(g4)
    c: Coincident(g3,g4)
    c: Block(g3)
    c: Coincident(g5,g2)
    c: Coincident(g5,g3)
    c: Block(g0)
    c: Block(g5)
FEATURE [Part::Extrusion] Extrude067  label="sideB003"
  Base = -> Sketch075
  Dir = (0,0,1)
  DirMode = 2
  FaceMakerClass = Part::FaceMakerBullseye
  LengthFwd = 3
  LengthRev = 0
  Placement = pos=(0,0,71.7) rot=(0,0,1;0rad)
  Solid = true
  Symmetric = false
FEATURE [Sketcher::SketchObject] Sketch076  label="topSketch023"
  FullyConstrained = true
  sketch-geometry (6):
    g0: LineSegment StartX=19 StartY=38 StartZ=0 EndX=117 EndY=38 EndZ=0
    g1: ArcOfCircle CenterX=19 CenterY=19 CenterZ=0 NormalX=0 NormalY=0 NormalZ=1 AngleXU=0 Radius=19 StartAngle=1.5708 EndAngle=3.14159
    g2: LineSegment StartX=117 StartY=38 StartZ=0 EndX=117 EndY=19 EndZ=0
    g3: LineSegment StartX=98 StartY=1.0161e-12 StartZ=0 EndX=5.22862e-06 EndY=1.0161e-12 EndZ=0
    g4: LineSegment StartX=5.22862e-06 StartY=19 StartZ=0 EndX=5.22862e-06 EndY=1.0161e-12 EndZ=0
    g5: ArcOfCircle CenterX=98 CenterY=19 CenterZ=0 NormalX=0 NormalY=0 NormalZ=1 AngleXU=0 Radius=19 StartAngle=4.71239 EndAngle=6.28319
  constraints (16):
    c: Horizontal(g0)
    c: Distance(g0) = 98
    c: Coincident(g1,g0)
    c: Block(g1)
    c: Coincident(g2,g0)
    c: Vertical(g2)
    c: Distance(g2) = 19
    c: Horizontal(g3)
    c: Coincident(g4,g1)
    c: Vertical(g4)
    c: Coincident(g3,g4)
    c: Block(g3)
    c: Coincident(g5,g2)
    c: Coincident(g5,g3)
    c: Block(g0)
    c: Block(g5)
FEATURE [Part::Extrusion] Extrude066  label="sideA003"
  Base = -> Sketch076
  Dir = (0,0,1)
  DirMode = 2
  FaceMakerClass = Part::FaceMakerBullseye
  LengthFwd = 3
  LengthRev = 0
  Placement = pos=(0,0,-2.7) rot=(0,0,1;0rad)
  Solid = true
  Symmetric = false
FEATURE [Part::MultiFuse] Fusion142  label="removeFromBottom003"
  Placement = pos=(2,0,0) rot=(0,0,1;0rad)
  Shapes = -> [Extrude066,Extrude067]
FEATURE [Part::Cut] Cut065  label="screwRetainers002"
  Base = -> Fusion096
  Tool = -> Fusion142
FEATURE [Sketcher::SketchObject] Sketch077
  FullyConstrained = true
  Placement = pos=(117,19,0) rot=(0.57735,0.57735,0.57735;2.0944rad)
  sketch-geometry (8):
    g0: LineSegment StartX=-49.19 StartY=63.5 StartZ=0 EndX=-49.19 EndY=60.5 EndZ=0
    g1: LineSegment StartX=-49.19 StartY=11.5 StartZ=0 EndX=-49.19 EndY=8.5 EndZ=0
    g2: ArcOfCircle CenterX=-1.5 CenterY=62 CenterZ=0 NormalX=0 NormalY=0 NormalZ=1 AngleXU=0 Radius=1.5 StartAngle=4.71239 EndAngle=7.85398
    g3: ArcOfCircle CenterX=-1.5 CenterY=10 CenterZ=0 NormalX=0 NormalY=0 NormalZ=1 AngleXU=0 Radius=1.5 StartAngle=4.71239 EndAngle=7.85398
    g4: LineSegment StartX=-49.19 StartY=63.5 StartZ=0 EndX=-1.5 EndY=63.5 EndZ=0
    g5: LineSegment StartX=-49.19 StartY=60.5 StartZ=0 EndX=-1.5 EndY=60.5 EndZ=0
    g6: LineSegment StartX=-49.19 StartY=11.5 StartZ=0 EndX=-1.5 EndY=11.5 EndZ=0
    g7: LineSegment StartX=-49.19 StartY=8.5 StartZ=0 EndX=-1.5 EndY=8.5 EndZ=0
  constraints (19):
    c: Vertical(g0)
    c: Distance(g0) = 3
    c: Vertical(g1)
    c: Block(g1)
    c: Block(g2)
    c: Block(g3)
    c: Block(g0)
    c: Coincident(g4,g0)
    c: Coincident(g4,g2)
    c: Horizontal(g4)
    c: Coincident(g5,g0)
    c: Coincident(g5,g2)
    c: Horizontal(g5)
    c: Coincident(g6,g1)
    c: Coincident(g6,g3)
    c: Horizontal(g6)
    c: Coincident(g7,g1)
    c: Coincident(g7,g3)
    c: Horizontal(g7)
FEATURE [Part::Extrusion] Extrude068
  Base = -> Sketch077
  Dir = (1,0,0)
  DirMode = 2
  FaceMakerClass = Part::FaceMakerBullseye
  LengthFwd = 10
  LengthRev = 0
  Solid = true
  Symmetric = false
FEATURE [Part::Fillet] Fillet057  label="removeFromtMoreFrontCaseScrewRetainers002"
  Base = -> Extrude068
  Edges = 4 edges r=1.49: [Edge6,Edge11,Edge18,Edge23]
  Placement = pos=(-12,0,0) rot=(0,0,1;0rad)
FEATURE [Sketcher::SketchObject] Sketch078
  FullyConstrained = true
  Placement = pos=(117,19,0) rot=(0.57735,0.57735,0.57735;2.0944rad)
  sketch-geometry (8):
    g0: LineSegment StartX=-49.19 StartY=69.25 StartZ=0 EndX=-49.19 EndY=66.25 EndZ=0
    g1: LineSegment StartX=-49.19 StartY=5.75 StartZ=0 EndX=-49.19 EndY=2.75 EndZ=0
    g2: ArcOfCircle CenterX=-1.5 CenterY=67.75 CenterZ=0 NormalX=0 NormalY=0 NormalZ=1 AngleXU=0 Radius=1.5 StartAngle=4.71239 EndAngle=7.85398
    g3: ArcOfCircle CenterX=-1.5 CenterY=4.25 CenterZ=0 NormalX=0 NormalY=0 NormalZ=1 AngleXU=0 Radius=1.5 StartAngle=4.71239 EndAngle=7.85398
    g4: LineSegment StartX=-49.19 StartY=69.25 StartZ=0 EndX=-1.5 EndY=69.25 EndZ=0
    g5: LineSegment StartX=-49.19 StartY=66.25 StartZ=0 EndX=-1.5 EndY=66.25 EndZ=0
    g6: LineSegment StartX=-49.19 StartY=5.75 StartZ=0 EndX=-1.5 EndY=5.75 EndZ=0
    g7: LineSegment StartX=-49.19 StartY=2.75 StartZ=0 EndX=-1.5 EndY=2.75 EndZ=0
  constraints (19):
    c: Vertical(g0)
    c: Distance(g0) = 3
    c: Block(g0)
    c: Vertical(g1)
    c: Block(g2)
    c: Block(g3)
    c: Block(g1)
    c: Coincident(g4,g0)
    c: Coincident(g4,g2)
    c: Horizontal(g4)
    c: Coincident(g5,g0)
    c: Coincident(g5,g2)
    c: Horizontal(g5)
    c: Coincident(g6,g1)
    c: Coincident(g6,g3)
    c: Horizontal(g6)
    c: Coincident(g7,g1)
    c: Coincident(g7,g3)
    c: Horizontal(g7)
FEATURE [Part::Extrusion] Extrude069
  Base = -> Sketch078
  Dir = (1,0,0)
  DirMode = 2
  FaceMakerClass = Part::FaceMakerBullseye
  LengthFwd = 10
  LengthRev = 0
  Solid = true
  Symmetric = false
FEATURE [Part::Fillet] Fillet058  label="removeFromtMoreFrontCaseScrewRetainers003"
  Base = -> Extrude069
  Edges = 4 edges r=1.49: [Edge6,Edge11,Edge18,Edge23]
  Placement = pos=(-4,0,0) rot=(0,0,1;0rad)
FEATURE [Part::Cut] Cut066
  Base = -> Cut065
  Tool = -> Fillet058
FEATURE [Part::Cut] Cut067  label="screwPillars"
  Base = -> Cut066
  Tool = -> Fillet057
FEATURE [Part::MultiFuse] Fusion143  label="bottom021"
  Shapes = -> [Cut031,Cut063]
FEATURE [Part::Cylinder] Cylinder
  Angle = 360
  AttacherType = Attacher::AttachEngine3D
  Height = 10
  Placement = pos=(20.65,12,4.68) rot=(1,0,0;1.5708rad)
  Radius = 2
FEATURE [Part::Cylinder] Cylinder064
  Angle = 360
  AttacherType = Attacher::AttachEngine3D
  Height = 10
  Placement = pos=(20.65,12,67.38) rot=(1,0,0;1.5708rad)
  Radius = 2
FEATURE [Part::Cylinder] Cylinder065
  Angle = 360
  AttacherType = Attacher::AttachEngine3D
  Height = 10
  Placement = pos=(77.15,12,67.38) rot=(1,0,0;1.5708rad)
  Radius = 2
FEATURE [Part::Cylinder] Cylinder066
  Angle = 360
  AttacherType = Attacher::AttachEngine3D
  Height = 10
  Placement = pos=(77.15,12,4.68) rot=(1,0,0;1.5708rad)
  Radius = 2
FEATURE [Part::MultiFuse] Fusion144  label="removeFromThreadedInsertHousing"
  Shapes = -> [Cylinder065,Cylinder064,Cylinder,Cylinder066]
FEATURE [Part::Cut] Cut068  label="pcbStands001"
  Base = -> Cut064
  Tool = -> Fusion144
FEATURE [Part::MultiFuse] Fusion145
  Shapes = -> [Cut068,Fusion143]
FEATURE [Part::MultiFuse] Fusion146
  Shapes = -> [Fusion145]
FEATURE [Part::MultiFuse] Fusion147  label="bottom022"
  Shapes = -> [Cut067,Fusion146]
FEATURE [Part::MultiFuse] Fusion148  label="casePillars005"
  Shapes = -> [Cut047,Fusion092]
FEATURE [Part::MultiFuse] Fusion149  label="bottom023"
  Shapes = -> [Fusion124,Fusion113,Fusion147]
FEATURE [Part::MultiFuse] Fusion150  label="topBits"
  Shapes = -> [Cut025,Fusion148,Cut030,Fillet034]
FEATURE [Part::Feature] Face149 .. Face152  x4 (patterned run collapsed; names and placements below)
  shape: bbox 3.2 x 1.5 x 2e-07 mm, 1 faces, 0 solids (baked)
FEATURE [Part::Feature] Face153
  shape: bbox 3.6 x 3.2 x 2e-07 mm, 1 faces, 0 solids (baked)
FEATURE [Part::Feature] Face154
  shape: bbox 3.6 x 3.2 x 2e-07 mm, 1 faces, 0 solids (baked)
FEATURE [Sketcher::SketchObject] Sketch079  label="topSketch024"
  FullyConstrained = true
  sketch-geometry (6):
    g0: LineSegment StartX=19 StartY=38 StartZ=0 EndX=117 EndY=38 EndZ=0
    g1: ArcOfCircle CenterX=19 CenterY=19 CenterZ=0 NormalX=0 NormalY=0 NormalZ=1 AngleXU=0 Radius=19 StartAngle=1.5708 EndAngle=3.14159
    g2: LineSegment StartX=117 StartY=38 StartZ=0 EndX=117 EndY=19 EndZ=0
    g3: LineSegment StartX=98 StartY=1.0161e-12 StartZ=0 EndX=5.22862e-06 EndY=1.0161e-12 EndZ=0
    g4: LineSegment StartX=5.22862e-06 StartY=19 StartZ=0 EndX=5.22862e-06 EndY=1.0161e-12 EndZ=0
    g5: ArcOfCircle CenterX=98 CenterY=19 CenterZ=0 NormalX=0 NormalY=0 NormalZ=1 AngleXU=0 Radius=19 StartAngle=4.71239 EndAngle=6.28319
  constraints (16):
    c: Horizontal(g0)
    c: Distance(g0) = 98
    c: Coincident(g1,g0)
    c: Block(g1)
    c: Coincident(g2,g0)
    c: Vertical(g2)
    c: Distance(g2) = 19
    c: Horizontal(g3)
    c: Coincident(g4,g1)
    c: Vertical(g4)
    c: Coincident(g3,g4)
    c: Block(g3)
    c: Coincident(g5,g2)
    c: Coincident(g5,g3)
    c: Block(g0)
    c: Block(g5)
FEATURE [Sketcher::SketchObject] Sketch080  label="topSketch025"
  FullyConstrained = true
  sketch-geometry (6):
    g0: LineSegment StartX=19 StartY=38 StartZ=0 EndX=117 EndY=38 EndZ=0
    g1: ArcOfCircle CenterX=19 CenterY=19 CenterZ=0 NormalX=0 NormalY=0 NormalZ=1 AngleXU=0 Radius=19 StartAngle=1.5708 EndAngle=3.14159
    g2: LineSegment StartX=117 StartY=38 StartZ=0 EndX=117 EndY=19 EndZ=0
    g3: LineSegment StartX=98 StartY=1.0161e-12 StartZ=0 EndX=5.22862e-06 EndY=1.0161e-12 EndZ=0
    g4: LineSegment StartX=5.22862e-06 StartY=19 StartZ=0 EndX=5.22862e-06 EndY=1.0161e-12 EndZ=0
    g5: ArcOfCircle CenterX=98 CenterY=19 CenterZ=0 NormalX=0 NormalY=0 NormalZ=1 AngleXU=0 Radius=19 StartAngle=4.71239 EndAngle=6.28319
  constraints (16):
    c: Horizontal(g0)
    c: Distance(g0) = 98
    c: Coincident(g1,g0)
    c: Block(g1)
    c: Coincident(g2,g0)
    c: Vertical(g2)
    c: Distance(g2) = 19
    c: Horizontal(g3)
    c: Coincident(g4,g1)
    c: Vertical(g4)
    c: Coincident(g3,g4)
    c: Block(g3)
    c: Coincident(g5,g2)
    c: Coincident(g5,g3)
    c: Block(g0)
    c: Block(g5)
FEATURE [Part::Extrusion] Extrude070  label="sideA004"
  Base = -> Sketch080
  Dir = (0,0,1)
  DirMode = 2
  FaceMakerClass = Part::FaceMakerBullseye
  LengthFwd = 3
  LengthRev = 0
  Placement = pos=(0,0,-2.7) rot=(0,0,1;0rad)
  Solid = true
  Symmetric = false
FEATURE [Sketcher::SketchObject] Sketch081
  FullyConstrained = true
  Placement = pos=(117,19,0) rot=(0.57735,0.57735,0.57735;2.0944rad)
  sketch-geometry (8):
    g0: LineSegment StartX=-49.19 StartY=63.5 StartZ=0 EndX=-49.19 EndY=60.5 EndZ=0
    g1: LineSegment StartX=-49.19 StartY=11.5 StartZ=0 EndX=-49.19 EndY=8.5 EndZ=0
    g2: ArcOfCircle CenterX=-1.5 CenterY=62 CenterZ=0 NormalX=0 NormalY=0 NormalZ=1 AngleXU=0 Radius=1.5 StartAngle=4.71239 EndAngle=7.85398
    g3: ArcOfCircle CenterX=-1.5 CenterY=10 CenterZ=0 NormalX=0 NormalY=0 NormalZ=1 AngleXU=0 Radius=1.5 StartAngle=4.71239 EndAngle=7.85398
    g4: LineSegment StartX=-49.19 StartY=63.5 StartZ=0 EndX=-1.5 EndY=63.5 EndZ=0
    g5: LineSegment StartX=-49.19 StartY=60.5 StartZ=0 EndX=-1.5 EndY=60.5 EndZ=0
    g6: LineSegment StartX=-49.19 StartY=11.5 StartZ=0 EndX=-1.5 EndY=11.5 EndZ=0
    g7: LineSegment StartX=-49.19 StartY=8.5 StartZ=0 EndX=-1.5 EndY=8.5 EndZ=0
  constraints (19):
    c: Vertical(g0)
    c: Distance(g0) = 3
    c: Vertical(g1)
    c: Block(g1)
    c: Block(g2)
    c: Block(g3)
    c: Block(g0)
    c: Coincident(g4,g0)
    c: Coincident(g4,g2)
    c: Horizontal(g4)
    c: Coincident(g5,g0)
    c: Coincident(g5,g2)
    c: Horizontal(g5)
    c: Coincident(g6,g1)
    c: Coincident(g6,g3)
    c: Horizontal(g6)
    c: Coincident(g7,g1)
    c: Coincident(g7,g3)
    c: Horizontal(g7)
FEATURE [Part::Extrusion] Extrude071  label="sideB004"
  Base = -> Sketch079
  Dir = (0,0,1)
  DirMode = 2
  FaceMakerClass = Part::FaceMakerBullseye
  LengthFwd = 3
  LengthRev = 0
  Placement = pos=(0,0,71.7) rot=(0,0,1;0rad)
  Solid = true
  Symmetric = false
FEATURE [Part::MultiFuse] Fusion152  label="removeFromBottom004"
  Placement = pos=(2,0,0) rot=(0,0,1;0rad)
  Shapes = -> [Extrude070,Extrude071]
FEATURE [Part::Extrusion] Extrude072
  Base = -> Sketch081
  Dir = (1,0,0)
  DirMode = 2
  FaceMakerClass = Part::FaceMakerBullseye
  LengthFwd = 10
  LengthRev = 0
  Solid = true
  Symmetric = false
FEATURE [Part::Fillet] Fillet059  label="removeFromtMoreFrontCaseScrewRetainers004"
  Base = -> Extrude072
  Edges = 4 edges r=1.49: [Edge6,Edge11,Edge18,Edge23]
  Placement = pos=(-12,0,0) rot=(0,0,1;0rad)
FEATURE [Sketcher::SketchObject] Sketch082
  FullyConstrained = true
  Placement = pos=(117,19,0) rot=(0.57735,0.57735,0.57735;2.0944rad)
  sketch-geometry (8):
    g0: LineSegment StartX=-49.19 StartY=69.25 StartZ=0 EndX=-49.19 EndY=66.25 EndZ=0
    g1: LineSegment StartX=-49.19 StartY=5.75 StartZ=0 EndX=-49.19 EndY=2.75 EndZ=0
    g2: ArcOfCircle CenterX=-1.5 CenterY=67.75 CenterZ=0 NormalX=0 NormalY=0 NormalZ=1 AngleXU=0 Radius=1.5 StartAngle=4.71239 EndAngle=7.85398
    g3: ArcOfCircle CenterX=-1.5 CenterY=4.25 CenterZ=0 NormalX=0 NormalY=0 NormalZ=1 AngleXU=0 Radius=1.5 StartAngle=4.71239 EndAngle=7.85398
    g4: LineSegment StartX=-49.19 StartY=69.25 StartZ=0 EndX=-1.5 EndY=69.25 EndZ=0
    g5: LineSegment StartX=-49.19 StartY=66.25 StartZ=0 EndX=-1.5 EndY=66.25 EndZ=0
    g6: LineSegment StartX=-49.19 StartY=5.75 StartZ=0 EndX=-1.5 EndY=5.75 EndZ=0
    g7: LineSegment StartX=-49.19 StartY=2.75 StartZ=0 EndX=-1.5 EndY=2.75 EndZ=0
  constraints (19):
    c: Vertical(g0)
    c: Distance(g0) = 3
    c: Block(g0)
    c: Vertical(g1)
    c: Block(g2)
    c: Block(g3)
    c: Block(g1)
    c: Coincident(g4,g0)
    c: Coincident(g4,g2)
    c: Horizontal(g4)
    c: Coincident(g5,g0)
    c: Coincident(g5,g2)
    c: Horizontal(g5)
    c: Coincident(g6,g1)
    c: Coincident(g6,g3)
    c: Horizontal(g6)
    c: Coincident(g7,g1)
    c: Coincident(g7,g3)
    c: Horizontal(g7)
FEATURE [Part::Extrusion] Extrude073
  Base = -> Sketch082
  Dir = (1,0,0)
  DirMode = 2
  FaceMakerClass = Part::FaceMakerBullseye
  LengthFwd = 10
  LengthRev = 0
  Solid = true
  Symmetric = false
FEATURE [Part::Fillet] Fillet060  label="removeFromtMoreFrontCaseScrewRetainers005"
  Base = -> Extrude073
  Edges = 4 edges r=1.49: [Edge6,Edge11,Edge18,Edge23]
  Placement = pos=(-4,0,0) rot=(0,0,1;0rad)
FEATURE [Part::Revolution] Revolve163  label="backCaseScrewRetainer004"
  Angle = 360
  Axis = (0,1,0)
  Base = (0,0,0)
  FaceMakerClass = Part::FaceMakerBullseye
  Placement = pos=(12.5,3,62) rot=(0,0,1;0rad)
  Solid = false
  Source = -> Face149
  Symmetric = false
FEATURE [Part::Revolution] Revolve164  label="frontCaseScrewRetainer006"
  Angle = 360
  Axis = (0,1,0)
  Base = (0,0,0)
  FaceMakerClass = Part::FaceMakerBullseye
  Placement = pos=(89.5,3,68.5) rot=(0,0,1;0rad)
  Solid = false
  Source = -> Face151
  Symmetric = false
FEATURE [Part::Revolution] Revolve165  label="frontCaseScrewRetainer007"
  Angle = 360
  Axis = (0,1,0)
  Base = (0,0,0)
  FaceMakerClass = Part::FaceMakerBullseye
  Placement = pos=(89.5,3,3.5) rot=(0,0,1;0rad)
  Solid = false
  Source = -> Face152
  Symmetric = false
FEATURE [Part::Revolution] Revolve166  label="backCaseScrewRetainer005"
  Angle = 360
  Axis = (0,1,0)
  Base = (0,0,0)
  FaceMakerClass = Part::FaceMakerBullseye
  Placement = pos=(12.5,3,10) rot=(0,0,1;0rad)
  Solid = false
  Source = -> Face150
  Symmetric = false
FEATURE [Part::Revolution] Revolve167  label="moreFrontCaseScrewRetainer006"
  Angle = 360
  Axis = (0,1,0)
  Base = (0,0,0)
  FaceMakerClass = Part::FaceMakerBullseye
  Placement = pos=(109.5,4.5,68.5) rot=(0,0,1;0rad)
  Solid = false
  Source = -> Face153
  Symmetric = false
FEATURE [Part::Revolution] Revolve168  label="moreFrontCaseScrewRetainer007"
  Angle = 360
  Axis = (0,1,0)
  Base = (0,0,0)
  FaceMakerClass = Part::FaceMakerBullseye
  Placement = pos=(109.5,4.5,3.5) rot=(0,0,1;0rad)
  Solid = false
  Source = -> Face154
  Symmetric = false
FEATURE [Part::MultiFuse] Fusion151  label="screwRetainers003"
  Shapes = -> [Revolve168,Revolve167,Revolve166,Revolve165,Revolve164,Revolve163]
FEATURE [Part::Cut] Cut069  label="screwRetainers004"
  Base = -> Fusion151
  Tool = -> Fusion152
FEATURE [Part::Cut] Cut070
  Base = -> Cut069
  Tool = -> Fillet060
FEATURE [Part::Cut] Cut071  label="screwPillars001"
  Base = -> Cut070
  Tool = -> Fillet059
FEATURE [Part::MultiFuse] Fusion153  label="bottom024"
  Shapes = -> [Fusion149,Cut071]
FEATURE [Part::Cylinder] Cylinder067
  Angle = 360
  AttacherType = Attacher::AttachEngine3D
  Height = 10
  Placement = pos=(20.65,12,4.68) rot=(1,0,0;1.5708rad)
  Radius = 2
FEATURE [Part::Cylinder] Cylinder068
  Angle = 360
  AttacherType = Attacher::AttachEngine3D
  Height = 10
  Placement = pos=(20.65,12,67.38) rot=(1,0,0;1.5708rad)
  Radius = 2
FEATURE [Part::Cylinder] Cylinder069
  Angle = 360
  AttacherType = Attacher::AttachEngine3D
  Height = 10
  Placement = pos=(77.15,12,67.38) rot=(1,0,0;1.5708rad)
  Radius = 2
FEATURE [Part::Cylinder] Cylinder070
  Angle = 360
  AttacherType = Attacher::AttachEngine3D
  Height = 10
  Placement = pos=(77.15,12,4.68) rot=(1,0,0;1.5708rad)
  Radius = 2
FEATURE [Part::MultiFuse] Fusion154  label="removeFromThreadedInsertHousing001"
  Shapes = -> [Cylinder069,Cylinder068,Cylinder067,Cylinder070]
FEATURE [Part::Cut] Cut072  label="bottom025"
  Base = -> Fusion153
  Tool = -> Fusion154
FEATURE [Image::ImagePlane] ImagePlane
  XSize = 339
  YSize = 72
FEATURE [Sketcher::SketchObject] Sketch083
  FullyConstrained = true
  MapMode = 5
  Support = -> [XY_Plane]
  sketch-geometry (338):
    g0: LineSegment StartX=-151.619 StartY=28.8932 StartZ=0 EndX=-140.819 EndY=28.8932 EndZ=0
    g1: LineSegment StartX=-151.619 StartY=24.0313 StartZ=0 EndX=-151.619 EndY=28.8932 EndZ=0
    g2: LineSegment StartX=-140.819 StartY=17.7713 StartZ=0 EndX=-151.619 EndY=17.7713 EndZ=0
    g3: LineSegment StartX=-151.619 StartY=17.7713 StartZ=0 EndX=-151.619 EndY=22.6313 EndZ=0
    g4: LineSegment StartX=-151.619 StartY=22.6313 StartZ=0 EndX=-145.128 EndY=22.6313 EndZ=0
    g5: LineSegment StartX=-145.128 StartY=24.0313 StartZ=0 EndX=-140.819 EndY=28.8932 EndZ=0
    g6: LineSegment StartX=-145.128 StartY=22.6313 StartZ=0 EndX=-140.819 EndY=17.7713 EndZ=0
    g7: ArcOfCircle CenterX=-155.157 CenterY=23.3323 CenterZ=0 NormalX=0 NormalY=0 NormalZ=1 AngleXU=0 Radius=6.92354 StartAngle=1.03434 EndAngle=5.24885
    g8: ArcOfCircle CenterX=-155.157 CenterY=23.3323 CenterZ=0 NormalX=0 NormalY=0 NormalZ=1 AngleXU=0 Radius=12.6269 StartAngle=1.28675 EndAngle=4.99643
    g9: LineSegment StartX=-151.619 StartY=35.4532 StartZ=0 EndX=-151.619 EndY=29.2832 EndZ=0
    g10: LineSegment StartX=-151.619 StartY=17.3813 StartZ=0 EndX=-151.619 EndY=11.2113 EndZ=0
    g11-g21: Circle x11 (B-spline internal-alignment scaffolding for g22; pole/knot coordinates omitted)
    g22: BSplineCurve PolesCount=11 KnotsCount=9 Degree=3 IsPeriodic=0
    g23-g31: GeomPoint x9 (B-spline internal-alignment scaffolding for g22; pole/knot coordinates omitted)
    g32-g49: Circle x18 (B-spline internal-alignment scaffolding for g50; pole/knot coordinates omitted)
    g50: BSplineCurve PolesCount=18 KnotsCount=16 Degree=3 IsPeriodic=0
    g51-g66: GeomPoint x16 (B-spline internal-alignment scaffolding for g50; pole/knot coordinates omitted)
    g67: LineSegment StartX=-117.124 StartY=30.093 StartZ=0 EndX=-117.603 EndY=26.5272 EndZ=0
    g68: LineSegment StartX=-117.603 StartY=17.8472 StartZ=0 EndX=-117.124 EndY=14.2659 EndZ=0
    g69: Ellipse CenterX=-109.671 CenterY=20.025 CenterZ=0 NormalX=0 NormalY=0 NormalZ=1 MajorRadius=3.34798 MinorRadius=2.71052 AngleXU=-1.56793
    g70: GeomPoint X=-109.666 Y=18.0598 Z=0
    g71: GeomPoint X=-109.677 Y=21.9902 Z=0
    g72: Ellipse CenterX=-109.671 CenterY=20.0123 CenterZ=0 NormalX=0 NormalY=0 NormalZ=1 MajorRadius=6.93002 MinorRadius=6.36273 AngleXU=-3.13976
    g73: GeomPoint X=-112.417 Y=20.0073 Z=0
    g74: GeomPoint X=-106.925 Y=20.0173 Z=0
    g75: Ellipse CenterX=-51.7682 CenterY=20.1463 CenterZ=0 NormalX=0 NormalY=0 NormalZ=1 MajorRadius=3.19279 MinorRadius=2.71052 AngleXU=-1.52774
    g76: GeomPoint X=-51.6955 Y=18.4606 Z=0
    g77: GeomPoint X=-51.8408 Y=21.832 Z=0
    g78: GeomPoint X=-54.5142 Y=20.1413 Z=0
    g79: GeomPoint X=-49.0221 Y=20.1513 Z=0
    g80: Ellipse CenterX=-51.7682 CenterY=20.1463 CenterZ=0 NormalX=0 NormalY=0 NormalZ=1 MajorRadius=6.93002 MinorRadius=6.36273 AngleXU=-3.13976
    g81: Ellipse CenterX=-22.8436 CenterY=20.1783 CenterZ=0 NormalX=0 NormalY=0 NormalZ=1 MajorRadius=3.31512 MinorRadius=2.71052 AngleXU=-1.60214
    g82: GeomPoint X=-22.9034 Y=18.2706 Z=0
    g83: GeomPoint X=-22.7838 Y=22.0861 Z=0
    g84: GeomPoint X=-25.5897 Y=20.1733 Z=0
    g85: GeomPoint X=-20.0976 Y=20.1833 Z=0
    g86: Ellipse CenterX=-22.8436 CenterY=20.1783 CenterZ=0 NormalX=0 NormalY=0 NormalZ=1 MajorRadius=6.93002 MinorRadius=6.36273 AngleXU=-3.13976
    g87: LineSegment StartX=-101.889 StartY=14.1107 StartZ=0 EndX=-97.7455 EndY=14.1107 EndZ=0
    g88: LineSegment StartX=-93.8155 StartY=14.1107 StartZ=0 EndX=-89.6755 EndY=14.1107 EndZ=0
    g89: LineSegment StartX=-85.7455 StartY=14.1107 StartZ=0 EndX=-81.6055 EndY=14.1107 EndZ=0
    g90: LineSegment StartX=-101.889 StartY=14.1107 StartZ=0 EndX=-101.889 EndY=25.9907 EndZ=0
    g91: LineSegment StartX=-101.889 StartY=25.9907 StartZ=0 EndX=-97.8594 EndY=25.9907 EndZ=0
    g92: LineSegment StartX=-97.8594 StartY=25.9907 StartZ=0 EndX=-97.8594 EndY=24.0907 EndZ=0
    g93: LineSegment StartX=-97.7455 StartY=14.1107 StartZ=0 EndX=-97.7455 EndY=19.9107 EndZ=0
    g94: LineSegment StartX=-89.6755 StartY=14.1107 StartZ=0 EndX=-89.6755 EndY=19.9107 EndZ=0
    g95: LineSegment StartX=-93.8155 StartY=14.1107 StartZ=0 EndX=-93.8155 EndY=21.0107 EndZ=0
    g96-g106: Circle x11 (B-spline internal-alignment scaffolding for g107; pole/knot coordinates omitted)
    g107: BSplineCurve PolesCount=11 KnotsCount=9 Degree=3 IsPeriodic=0
    g108-g116: GeomPoint x9 (B-spline internal-alignment scaffolding for g107; pole/knot coordinates omitted)
    g117: BSplineCurve PolesCount=11 KnotsCount=9 Degree=3 IsPeriodic=0
    g118-g125: Circle x8 (B-spline internal-alignment scaffolding for g126; pole/knot coordinates omitted)
    g126: BSplineCurve PolesCount=8 KnotsCount=6 Degree=3 IsPeriodic=0
    g127-g132: GeomPoint x6 (B-spline internal-alignment scaffolding for g126; pole/knot coordinates omitted)
    g133: BSplineCurve PolesCount=8 KnotsCount=6 Degree=3 IsPeriodic=0
    g134: LineSegment StartX=-85.7455 StartY=21.0107 StartZ=0 EndX=-85.7455 EndY=14.1107 EndZ=0
    g135: LineSegment StartX=-80.0879 StartY=14.1107 StartZ=0 EndX=-75.944 EndY=14.1107 EndZ=0
    g136: LineSegment StartX=-72.014 StartY=14.1107 StartZ=0 EndX=-67.874 EndY=14.1107 EndZ=0
    g137: LineSegment StartX=-63.944 StartY=14.1107 StartZ=0 EndX=-59.804 EndY=14.1107 EndZ=0
    g138: LineSegment StartX=-80.0879 StartY=14.1107 StartZ=0 EndX=-80.0879 EndY=25.9907 EndZ=0
    g139: LineSegment StartX=-80.0879 StartY=25.9907 StartZ=0 EndX=-76.0579 EndY=25.9907 EndZ=0
    g140: LineSegment StartX=-76.0579 StartY=25.9907 StartZ=0 EndX=-76.0579 EndY=24.0907 EndZ=0
    g141: LineSegment StartX=-75.944 StartY=14.1107 StartZ=0 EndX=-75.944 EndY=19.9107 EndZ=0
    g142: LineSegment StartX=-67.874 StartY=14.1107 StartZ=0 EndX=-67.874 EndY=19.9107 EndZ=0
    g143: LineSegment StartX=-72.014 StartY=14.1107 StartZ=0 EndX=-72.014 EndY=21.0107 EndZ=0
    g144-g148: Circle x5 (B-spline internal-alignment scaffolding for g149; pole/knot coordinates omitted)
    g149: BSplineCurve PolesCount=11 KnotsCount=9 Degree=3 IsPeriodic=0
    g150-g158: GeomPoint x9 (B-spline internal-alignment scaffolding for g149; pole/knot coordinates omitted)
    g159: BSplineCurve PolesCount=11 KnotsCount=9 Degree=3 IsPeriodic=0
    g160-g167: Circle x8 (B-spline internal-alignment scaffolding for g168; pole/knot coordinates omitted)
    g168: BSplineCurve PolesCount=8 KnotsCount=6 Degree=3 IsPeriodic=0
    g169-g174: GeomPoint x6 (B-spline internal-alignment scaffolding for g168; pole/knot coordinates omitted)
    g175: BSplineCurve PolesCount=8 KnotsCount=6 Degree=3 IsPeriodic=0
    g176: LineSegment StartX=-63.944 StartY=21.0107 StartZ=0 EndX=-63.944 EndY=14.1107 EndZ=0
    g177: LineSegment StartX=-59.804 StartY=14.1107 StartZ=0 EndX=-59.804 EndY=21.5868 EndZ=0
    g178: BSplineCurve PolesCount=4 KnotsCount=2 Degree=3 IsPeriodic=0
    g179: GeomPoint X=-59.804 Y=21.5868 Z=0
    g180: GeomPoint X=-60.2379 Y=24.0907 Z=0
    g181: LineSegment StartX=-81.6055 StartY=14.1107 StartZ=0 EndX=-81.6055 EndY=21.5868 EndZ=0
    g182: LineSegment StartX=-151.619 StartY=24.0313 StartZ=0 EndX=-145.128 EndY=24.0313 EndZ=0
    g183: Circle CenterX=-82.0394 CenterY=24.0907 CenterZ=0 NormalX=0 NormalY=0 NormalZ=1 AngleXU=0 Radius=1
    g184: Circle CenterX=-81.7131 CenterY=23.2736 CenterZ=0 NormalX=0 NormalY=0 NormalZ=1 AngleXU=0 Radius=1
    g185: Circle CenterX=-81.6055 CenterY=21.5868 CenterZ=0 NormalX=0 NormalY=0 NormalZ=1 AngleXU=0 Radius=1
    g186: BSplineCurve PolesCount=3 KnotsCount=2 Degree=2 IsPeriodic=0
    g187: GeomPoint X=-82.0394 Y=24.0907 Z=0
    g188: GeomPoint X=-81.6055 Y=21.5868 Z=0
    g189: Ellipse CenterX=-37.3522 CenterY=19.9515 CenterZ=0 NormalX=0 NormalY=0 NormalZ=1 MajorRadius=2.99755 MinorRadius=2.49 AngleXU=1.5708
    g190: GeomPoint X=-37.3522 Y=21.6203 Z=0
    g191: GeomPoint X=-37.3522 Y=18.2826 Z=0
    g192: ArcOfEllipse CenterX=-38.7647 CenterY=20.06 CenterZ=0 NormalX=0 NormalY=0 NormalZ=1 MajorRadius=6.30025 MinorRadius=5.3849 AngleXU=1.57276 StartAngle=5.50632 EndAngle=10.3035
    g193: GeomPoint X=-38.7711 Y=23.3304 Z=0
    g194: GeomPoint X=-38.7583 Y=16.7895 Z=0
    g195: LineSegment StartX=-34.6109 StartY=14.1107 StartZ=0 EndX=-30.8984 EndY=14.1107 EndZ=0
    g196: LineSegment StartX=-30.8984 StartY=14.1107 StartZ=0 EndX=-30.8984 EndY=31.1784 EndZ=0
    g197: LineSegment StartX=-30.8984 StartY=31.1784 StartZ=0 EndX=-34.9984 EndY=31.1784 EndZ=0
    g198: LineSegment StartX=-34.9984 StartY=24.5602 StartZ=0 EndX=-34.9984 EndY=31.1784 EndZ=0
    g199: LineSegment StartX=-34.6109 StartY=16.0476 StartZ=0 EndX=-34.6109 EndY=14.1107 EndZ=0
    g200: LineSegment StartX=-14.8781 StartY=14.1107 StartZ=0 EndX=-10.5106 EndY=14.1107 EndZ=0
    g201: LineSegment StartX=-14.8781 StartY=14.1107 StartZ=0 EndX=-14.8781 EndY=25.8504 EndZ=0
    g202: LineSegment StartX=-14.8781 StartY=25.8504 StartZ=0 EndX=-10.8534 EndY=25.8504 EndZ=0
    g203: LineSegment StartX=-10.8534 StartY=25.8504 StartZ=0 EndX=-10.8534 EndY=24.0923 EndZ=0
    g204: LineSegment StartX=-10.5106 StartY=14.1107 StartZ=0 EndX=-10.5106 EndY=19.7752 EndZ=0
    g205: LineSegment StartX=-5.96397 StartY=25.9304 StartZ=0 EndX=-5.96397 EndY=22.574 EndZ=0
    g206-g214: Circle x9 (B-spline internal-alignment scaffolding for g215; pole/knot coordinates omitted)
    g215: BSplineCurve PolesCount=9 KnotsCount=7 Degree=3 IsPeriodic=0
    g216-g222: GeomPoint x7 (B-spline internal-alignment scaffolding for g215; pole/knot coordinates omitted)
    g223-g232: Circle x10 (B-spline internal-alignment scaffolding for g233; pole/knot coordinates omitted)
    g233: BSplineCurve PolesCount=10 KnotsCount=8 Degree=3 IsPeriodic=0
    g234-g241: GeomPoint x8 (B-spline internal-alignment scaffolding for g233; pole/knot coordinates omitted)
    g242: LineSegment StartX=-1.58923 StartY=21.0696 StartZ=0 EndX=2.62034 EndY=21.0696 EndZ=0
    g243: LineSegment StartX=-1.55856 StartY=18.7342 StartZ=0 EndX=6.45946 EndY=18.7342 EndZ=0
    g244: LineSegment StartX=5.29231 StartY=17.386 StartZ=0 EndX=5.29231 EndY=14.3674 EndZ=0
    g245-g269: Circle x25 (B-spline internal-alignment scaffolding for g270; pole/knot coordinates omitted)
    g270: BSplineCurve PolesCount=25 KnotsCount=23 Degree=3 IsPeriodic=0
    g271-g293: GeomPoint x23 (B-spline internal-alignment scaffolding for g270; pole/knot coordinates omitted)
    g294-g304: Circle x11 (B-spline internal-alignment scaffolding for g305; pole/knot coordinates omitted)
    g305: BSplineCurve PolesCount=11 KnotsCount=9 Degree=3 IsPeriodic=0
    g306-g314: GeomPoint x9 (B-spline internal-alignment scaffolding for g305; pole/knot coordinates omitted)
    g315-g326: Circle x12 (B-spline internal-alignment scaffolding for g327; pole/knot coordinates omitted)
    g327: BSplineCurve PolesCount=12 KnotsCount=10 Degree=3 IsPeriodic=0
    g328-g337: GeomPoint x10 (B-spline internal-alignment scaffolding for g327; pole/knot coordinates omitted)
  constraints (252):
    c: Coincident(g1,g0)
    c: Horizontal(g0)
    c: Vertical(g1)
    c: Coincident(g2,g3)
    c: Coincident(g3,g4)
    c: Horizontal(g4)
    c: Horizontal(g2)
    c: Vertical(g3)
    c: Block(g1)
    c: Distance(g3) = 4.86
    c: Block(g4)
    c: Distance(g0) = 10.8
    c: Distance(g2) = 10.8
    c: Coincident(g5,g0)
    c: Coincident(g6,g4)
    c: Coincident(g6,g2)
    c: Block(g8)
    c: Block(g7)
    c: Coincident(g9,g8)
    c: Coincident(g9,g7)
    c: Vertical(g9)
    c: Coincident(g10,g7)
    c: Coincident(g10,g8)
    c: Vertical(g10)
    c: Weight(g11) = 1
    c: Equal(g11, g12-g21) x10
    c: InternalAlignment(g11-g21 -> g22) x11
    c: InternalAlignment(g23-g31 -> g22) x9
    c: Block(g22)
    c: Weight(g32) = 1
    c: Equal(g32, g33-g49) x17
    c: InternalAlignment(g32-g49 -> g50) x18
    c: InternalAlignment(g51-g66 -> g50) x16
    c: Block(g50)
    c: Coincident(g67,g50)
    c: Coincident(g67,g22)
    c: Coincident(g68,g22)
    c: Coincident(g68,g50)
    c: InternalAlignment(g70,g69)
    c: InternalAlignment(g71,g69)
    c: Block(g69)
    c: InternalAlignment(g73,g72)
    c: InternalAlignment(g74,g72)
    c: Block(g72)
    c: InternalAlignment(g76,g75)
    c: InternalAlignment(g77,g75)
    c: InternalAlignment(g78,g80)
    c: InternalAlignment(g79,g80)
    c: Block(g80)
    c: Coincident(g75,g80)
    c: Block(g75)
    c: InternalAlignment(g82,g81)
    c: InternalAlignment(g83,g81)
    c: InternalAlignment(g84,g86)
    c: InternalAlignment(g85,g86)
    c: Block(g86)
    c: Coincident(g81,g86)
    c: Block(g81)
    c: Horizontal(g87)
    c: Block(g87)
    c: Horizontal(g88)
    c: Distance(g88) = 4.14
    c: Horizontal(g89)
    c: Equal(g88,g89) = 4.14
    c: Block(g89)
    c: Block(g88)
    c: Coincident(g90,g87)
    c: Vertical(g90)
    c: Distance(g90) = 11.88
    c: Coincident(g91,g90)
    c: Horizontal(g91)
    c: Coincident(g92,g91)
    c: Vertical(g92)
    c: Distance(g91) = 4.03
    c: Distance(g92) = 1.9
    c: Coincident(g93,g87)
    c: Vertical(g93)
    c: Vertical(g94)
    c: Coincident(g94,g88)
    c: Distance(g93) = 5.8
    c: Distance(g94) = 5.8
    c: Vertical(g95)
    c: Coincident(g95,g88)
    c: Distance(g95) = 6.9
    c: Coincident(g107,g92)
    c: Weight(g96) = 1
    c: Equal(g96, g97-g106) x10
    c: InternalAlignment(g96-g106 -> g107) x11
    c: InternalAlignment(g108-g116 -> g107) x9
    c: Block(g107)
    c: Block(g117)
    c: Coincident(g126,g93)
    c: Weight(g118) = 1
    c: Equal(g118, g119-g125) x7
    c: Coincident(g126,g95)
    c: InternalAlignment(g118-g125 -> g126) x8
    c: InternalAlignment(g127-g132 -> g126) x6
    c: Coincident(g133,g94)
    c: Block(g126)
    c: Block(g133)
    c: Coincident(g134,g133)
    c: Coincident(g134,g89)
    c: Vertical(g134)
    c: Horizontal(g135)
    c: Block(g135)
    c: Horizontal(g136)
    c: Equal(g88,g136) = 4.14
    c: Horizontal(g137)
    c: Equal(g136,g137) = 4.14
    c: Block(g137)
    c: Block(g136)
    c: Coincident(g138,g135)
    c: Vertical(g138)
    c: Equal(g90,g138) = 11.88
    c: Coincident(g139,g138)
    c: Horizontal(g139)
    c: Coincident(g140,g139)
    c: Vertical(g140)
    c: Equal(g91,g139) = 4.03
    c: Equal(g92,g140) = 1.9
    c: Coincident(g141,g135)
    c: Vertical(g141)
    c: Vertical(g142)
    c: Coincident(g142,g136)
    c: Equal(g93,g141) = 5.8
    c: Equal(g94,g142) = 5.8
    c: Vertical(g143)
    c: Coincident(g143,g136)
    c: Equal(g95,g143) = 6.9
    c: Coincident(g149,g140)
    c: Equal(g96,g144) = 1
    c: Equal(g144, g145-g148) x4
    c: InternalAlignment(g144-g148 -> g149) x5
    c: InternalAlignment(g150-g158 -> g149) x9
    c: Block(g149)
    c: Block(g159)
    c: Coincident(g168,g141)
    c: Equal(g118,g160) = 1
    c: Equal(g160, g161-g167) x7
    c: Coincident(g168,g143)
    c: InternalAlignment(g160-g167 -> g168) x8
    c: InternalAlignment(g169-g174 -> g168) x6
    c: Coincident(g175,g142)
    c: Block(g168)
    c: Block(g175)
    c: Coincident(g176,g175)
    c: Coincident(g176,g137)
    c: Vertical(g176)
    c: Coincident(g177,g137)
    c: Vertical(g177)
    c: Coincident(g178,g177)
    c: Coincident(g178,g159)
    c: InternalAlignment(g179,g178)
    c: InternalAlignment(g180,g178)
    c: Block(g178)
    c: Vertical(g181)
    c: Coincident(g181,g89)
    c: Block(g5)
    c: Coincident(g182,g1)
    c: Coincident(g182,g5)
    c: Horizontal(g182)
    c: Coincident(g186,g117)
    c: Weight(g183) = 1
    c: Equal(g183,g184)
    c: Equal(g183,g185)
    c: Coincident(g186,g181)
    c: InternalAlignment(g183,g186)
    c: InternalAlignment(g184,g186)
    c: InternalAlignment(g185,g186)
    c: InternalAlignment(g187,g186)
    c: InternalAlignment(g188,g186)
    c: Block(g186)
    c: InternalAlignment(g190,g189)
    c: InternalAlignment(g191,g189)
    c: Block(g189)
    c: InternalAlignment(g193,g192)
    c: InternalAlignment(g194,g192)
    c: Block(g192)
    c: Horizontal(g195)
    c: Block(g195)
    c: Coincident(g196,g195)
    c: Vertical(g196)
    c: Block(g196)
    c: Distance(g195) = 3.71244
    c: Coincident(g197,g196)
    c: Horizontal(g197)
    c: Distance(g197) = 4.1
    c: Coincident(g198,g192)
    c: Coincident(g198,g197)
    c: Vertical(g198)
    c: Block(g198)
    c: Coincident(g199,g192)
    c: Coincident(g199,g195)
    c: Vertical(g199)
    c: Block(g199)
    c: Horizontal(g200)
    c: Block(g200)
    c: Coincident(g201,g200)
    c: Vertical(g201)
    c: Block(g201)
    c: Coincident(g202,g201)
    c: Horizontal(g202)
    c: Block(g202)
    c: Coincident(g203,g202)
    c: Vertical(g203)
    c: Block(g203)
    c: Coincident(g204,g200)
    c: Vertical(g204)
    c: Block(g204)
    c: Coincident(g215,g203)
    c: Weight(g206) = 1
    c: Equal(g206, g207-g214) x8
    c: Coincident(g215,g205)
    c: InternalAlignment(g206-g214 -> g215) x9
    c: InternalAlignment(g216-g222 -> g215) x7
    c: Coincident(g233,g204)
    c: Weight(g223) = 1
    c: Equal(g223, g224-g232) x9
    c: Coincident(g233,g205)
    c: InternalAlignment(g223-g232 -> g233) x10
    c: InternalAlignment(g234-g241 -> g233) x8
    c: Vertical(g205)
    c: Block(g205)
    c: Block(g215)
    c: Block(g233)
    c: Horizontal(g242)
    c: Horizontal(g243)
    c: Block(g242)
    c: Block(g243)
    c: Vertical(g244)
    c: Block(g244)
    c: Coincident(g270,g243)
    c: Weight(g245) = 1
    c: Equal(g245, g246-g269) x24
    c: Coincident(g270,g244)
    c: InternalAlignment(g245-g269 -> g270) x25
    c: InternalAlignment(g271-g293 -> g270) x23
    c: Coincident(g305,g242)
    c: Weight(g294) = 1
    c: Equal(g294, g295-g304) x10
    c: Coincident(g305,g242)
    c: InternalAlignment(g294-g304 -> g305) x11
    c: InternalAlignment(g306-g314 -> g305) x9
    c: Block(g305)
    c: Coincident(g327,g243)
    c: Weight(g315) = 1
    c: Equal(g315, g316-g326) x11
    c: Coincident(g327,g244)
    c: InternalAlignment(g315-g326 -> g327) x12
    c: InternalAlignment(g328-g337 -> g327) x10
    c: Block(g327)
    c: Block(g270)
FEATURE [PartDesign::Body] Body  label="CommodoreLogoAndText"
  Group = -> [Sketch083]
  Origin = -> Origin
FEATURE [Part::Extrusion] Extrude074  label="CommodoreLogoAndText001"
  Base = -> Sketch083
  Dir = (0,0,1)
  DirMode = 2
  FaceMakerClass = Part::FaceMakerBullseye
  LengthFwd = 10
  LengthRev = 0
  Solid = true
  Symmetric = false
FEATURE [Part::FeaturePython] Clone  label="CommodoreLogoAndTextScale"  # Draft clone (typed FeaturePython)
  AttacherType = Attacher::AttachEngine3D
  Fuse = false
  Objects = -> [Extrude074]
  Placement = pos=(111,5.37,-11.6) rot=(0,0,1;0rad)
  Scale = (0.62,0.62,1)
FEATURE [Part::Mirroring] Part__Mirroring  label="CommodoreLogoAndTextScale (Mirror #1)"
  Base = (0,0,0)
  Normal = (1,0,0)
  Placement = pos=(123.576,0,0) rot=(0,0,1;0rad)
  Source = -> Clone
FEATURE [Sketcher::SketchObject] Sketch084
  FullyConstrained = true
  MapMode = 5
  Support = -> [XY_Plane001]
  sketch-geometry (338):
    g0: LineSegment StartX=-151.619 StartY=28.8932 StartZ=0 EndX=-140.819 EndY=28.8932 EndZ=0
    g1: LineSegment StartX=-151.619 StartY=24.0313 StartZ=0 EndX=-151.619 EndY=28.8932 EndZ=0
    g2: LineSegment StartX=-140.819 StartY=17.7713 StartZ=0 EndX=-151.619 EndY=17.7713 EndZ=0
    g3: LineSegment StartX=-151.619 StartY=17.7713 StartZ=0 EndX=-151.619 EndY=22.6313 EndZ=0
    g4: LineSegment StartX=-151.619 StartY=22.6313 StartZ=0 EndX=-145.128 EndY=22.6313 EndZ=0
    g5: LineSegment StartX=-145.128 StartY=24.0313 StartZ=0 EndX=-140.819 EndY=28.8932 EndZ=0
    g6: LineSegment StartX=-145.128 StartY=22.6313 StartZ=0 EndX=-140.819 EndY=17.7713 EndZ=0
    g7: ArcOfCircle CenterX=-155.157 CenterY=23.3323 CenterZ=0 NormalX=0 NormalY=0 NormalZ=1 AngleXU=0 Radius=6.92354 StartAngle=1.03434 EndAngle=5.24885
    g8: ArcOfCircle CenterX=-155.157 CenterY=23.3323 CenterZ=0 NormalX=0 NormalY=0 NormalZ=1 AngleXU=0 Radius=12.6269 StartAngle=1.28675 EndAngle=4.99643
    g9: LineSegment StartX=-151.619 StartY=35.4532 StartZ=0 EndX=-151.619 EndY=29.2832 EndZ=0
    g10: LineSegment StartX=-151.619 StartY=17.3813 StartZ=0 EndX=-151.619 EndY=11.2113 EndZ=0
    g11-g21: Circle x11 (B-spline internal-alignment scaffolding for g22; pole/knot coordinates omitted)
    g22: BSplineCurve PolesCount=11 KnotsCount=9 Degree=3 IsPeriodic=0
    g23-g31: GeomPoint x9 (B-spline internal-alignment scaffolding for g22; pole/knot coordinates omitted)
    g32-g49: Circle x18 (B-spline internal-alignment scaffolding for g50; pole/knot coordinates omitted)
    g50: BSplineCurve PolesCount=18 KnotsCount=16 Degree=3 IsPeriodic=0
    g51-g66: GeomPoint x16 (B-spline internal-alignment scaffolding for g50; pole/knot coordinates omitted)
    g67: LineSegment StartX=-117.124 StartY=30.093 StartZ=0 EndX=-117.603 EndY=26.5272 EndZ=0
    g68: LineSegment StartX=-117.603 StartY=17.8472 StartZ=0 EndX=-117.124 EndY=14.2659 EndZ=0
    g69: Ellipse CenterX=-109.671 CenterY=20.025 CenterZ=0 NormalX=0 NormalY=0 NormalZ=1 MajorRadius=3.34798 MinorRadius=2.71052 AngleXU=-1.56793
    g70: GeomPoint X=-109.666 Y=18.0598 Z=0
    g71: GeomPoint X=-109.677 Y=21.9902 Z=0
    g72: Ellipse CenterX=-109.671 CenterY=20.0123 CenterZ=0 NormalX=0 NormalY=0 NormalZ=1 MajorRadius=6.93002 MinorRadius=6.36273 AngleXU=-3.13976
    g73: GeomPoint X=-112.417 Y=20.0073 Z=0
    g74: GeomPoint X=-106.925 Y=20.0173 Z=0
    g75: Ellipse CenterX=-51.7682 CenterY=20.1463 CenterZ=0 NormalX=0 NormalY=0 NormalZ=1 MajorRadius=3.19279 MinorRadius=2.71052 AngleXU=-1.52774
    g76: GeomPoint X=-51.6955 Y=18.4606 Z=0
    g77: GeomPoint X=-51.8408 Y=21.832 Z=0
    g78: GeomPoint X=-54.5142 Y=20.1413 Z=0
    g79: GeomPoint X=-49.0221 Y=20.1513 Z=0
    g80: Ellipse CenterX=-51.7682 CenterY=20.1463 CenterZ=0 NormalX=0 NormalY=0 NormalZ=1 MajorRadius=6.93002 MinorRadius=6.36273 AngleXU=-3.13976
    g81: Ellipse CenterX=-22.8436 CenterY=20.1783 CenterZ=0 NormalX=0 NormalY=0 NormalZ=1 MajorRadius=3.31512 MinorRadius=2.71052 AngleXU=-1.60214
    g82: GeomPoint X=-22.9034 Y=18.2706 Z=0
    g83: GeomPoint X=-22.7838 Y=22.0861 Z=0
    g84: GeomPoint X=-25.5897 Y=20.1733 Z=0
    g85: GeomPoint X=-20.0976 Y=20.1833 Z=0
    g86: Ellipse CenterX=-22.8436 CenterY=20.1783 CenterZ=0 NormalX=0 NormalY=0 NormalZ=1 MajorRadius=6.93002 MinorRadius=6.36273 AngleXU=-3.13976
    g87: LineSegment StartX=-101.889 StartY=14.1107 StartZ=0 EndX=-97.7455 EndY=14.1107 EndZ=0
    g88: LineSegment StartX=-93.8155 StartY=14.1107 StartZ=0 EndX=-89.6755 EndY=14.1107 EndZ=0
    g89: LineSegment StartX=-85.7455 StartY=14.1107 StartZ=0 EndX=-81.6055 EndY=14.1107 EndZ=0
    g90: LineSegment StartX=-101.889 StartY=14.1107 StartZ=0 EndX=-101.889 EndY=25.9907 EndZ=0
    g91: LineSegment StartX=-101.889 StartY=25.9907 StartZ=0 EndX=-97.8594 EndY=25.9907 EndZ=0
    g92: LineSegment StartX=-97.8594 StartY=25.9907 StartZ=0 EndX=-97.8594 EndY=24.0907 EndZ=0
    g93: LineSegment StartX=-97.7455 StartY=14.1107 StartZ=0 EndX=-97.7455 EndY=19.9107 EndZ=0
    g94: LineSegment StartX=-89.6755 StartY=14.1107 StartZ=0 EndX=-89.6755 EndY=19.9107 EndZ=0
    g95: LineSegment StartX=-93.8155 StartY=14.1107 StartZ=0 EndX=-93.8155 EndY=21.0107 EndZ=0
    g96-g106: Circle x11 (B-spline internal-alignment scaffolding for g107; pole/knot coordinates omitted)
    g107: BSplineCurve PolesCount=11 KnotsCount=9 Degree=3 IsPeriodic=0
    g108-g116: GeomPoint x9 (B-spline internal-alignment scaffolding for g107; pole/knot coordinates omitted)
    g117: BSplineCurve PolesCount=11 KnotsCount=9 Degree=3 IsPeriodic=0
    g118-g125: Circle x8 (B-spline internal-alignment scaffolding for g126; pole/knot coordinates omitted)
    g126: BSplineCurve PolesCount=8 KnotsCount=6 Degree=3 IsPeriodic=0
    g127-g132: GeomPoint x6 (B-spline internal-alignment scaffolding for g126; pole/knot coordinates omitted)
    g133: BSplineCurve PolesCount=8 KnotsCount=6 Degree=3 IsPeriodic=0
    g134: LineSegment StartX=-85.7455 StartY=21.0107 StartZ=0 EndX=-85.7455 EndY=14.1107 EndZ=0
    g135: LineSegment StartX=-80.0879 StartY=14.1107 StartZ=0 EndX=-75.944 EndY=14.1107 EndZ=0
    g136: LineSegment StartX=-72.014 StartY=14.1107 StartZ=0 EndX=-67.874 EndY=14.1107 EndZ=0
    g137: LineSegment StartX=-63.944 StartY=14.1107 StartZ=0 EndX=-59.804 EndY=14.1107 EndZ=0
    g138: LineSegment StartX=-80.0879 StartY=14.1107 StartZ=0 EndX=-80.0879 EndY=25.9907 EndZ=0
    g139: LineSegment StartX=-80.0879 StartY=25.9907 StartZ=0 EndX=-76.0579 EndY=25.9907 EndZ=0
    g140: LineSegment StartX=-76.0579 StartY=25.9907 StartZ=0 EndX=-76.0579 EndY=24.0907 EndZ=0
    g141: LineSegment StartX=-75.944 StartY=14.1107 StartZ=0 EndX=-75.944 EndY=19.9107 EndZ=0
    g142: LineSegment StartX=-67.874 StartY=14.1107 StartZ=0 EndX=-67.874 EndY=19.9107 EndZ=0
    g143: LineSegment StartX=-72.014 StartY=14.1107 StartZ=0 EndX=-72.014 EndY=21.0107 EndZ=0
    g144-g148: Circle x5 (B-spline internal-alignment scaffolding for g149; pole/knot coordinates omitted)
    g149: BSplineCurve PolesCount=11 KnotsCount=9 Degree=3 IsPeriodic=0
    g150-g158: GeomPoint x9 (B-spline internal-alignment scaffolding for g149; pole/knot coordinates omitted)
    g159: BSplineCurve PolesCount=11 KnotsCount=9 Degree=3 IsPeriodic=0
    g160-g167: Circle x8 (B-spline internal-alignment scaffolding for g168; pole/knot coordinates omitted)
    g168: BSplineCurve PolesCount=8 KnotsCount=6 Degree=3 IsPeriodic=0
    g169-g174: GeomPoint x6 (B-spline internal-alignment scaffolding for g168; pole/knot coordinates omitted)
    g175: BSplineCurve PolesCount=8 KnotsCount=6 Degree=3 IsPeriodic=0
    g176: LineSegment StartX=-63.944 StartY=21.0107 StartZ=0 EndX=-63.944 EndY=14.1107 EndZ=0
    g177: LineSegment StartX=-59.804 StartY=14.1107 StartZ=0 EndX=-59.804 EndY=21.5868 EndZ=0
    g178: BSplineCurve PolesCount=4 KnotsCount=2 Degree=3 IsPeriodic=0
    g179: GeomPoint X=-59.804 Y=21.5868 Z=0
    g180: GeomPoint X=-60.2379 Y=24.0907 Z=0
    g181: LineSegment StartX=-81.6055 StartY=14.1107 StartZ=0 EndX=-81.6055 EndY=21.5868 EndZ=0
    g182: LineSegment StartX=-151.619 StartY=24.0313 StartZ=0 EndX=-145.128 EndY=24.0313 EndZ=0
    g183: Circle CenterX=-82.0394 CenterY=24.0907 CenterZ=0 NormalX=0 NormalY=0 NormalZ=1 AngleXU=0 Radius=1
    g184: Circle CenterX=-81.7131 CenterY=23.2736 CenterZ=0 NormalX=0 NormalY=0 NormalZ=1 AngleXU=0 Radius=1
    g185: Circle CenterX=-81.6055 CenterY=21.5868 CenterZ=0 NormalX=0 NormalY=0 NormalZ=1 AngleXU=0 Radius=1
    g186: BSplineCurve PolesCount=3 KnotsCount=2 Degree=2 IsPeriodic=0
    g187: GeomPoint X=-82.0394 Y=24.0907 Z=0
    g188: GeomPoint X=-81.6055 Y=21.5868 Z=0
    g189: Ellipse CenterX=-37.3522 CenterY=19.9515 CenterZ=0 NormalX=0 NormalY=0 NormalZ=1 MajorRadius=2.99755 MinorRadius=2.49 AngleXU=1.5708
    g190: GeomPoint X=-37.3522 Y=21.6203 Z=0
    g191: GeomPoint X=-37.3522 Y=18.2826 Z=0
    g192: ArcOfEllipse CenterX=-38.7647 CenterY=20.06 CenterZ=0 NormalX=0 NormalY=0 NormalZ=1 MajorRadius=6.30025 MinorRadius=5.3849 AngleXU=1.57276 StartAngle=5.50632 EndAngle=10.3035
    g193: GeomPoint X=-38.7711 Y=23.3304 Z=0
    g194: GeomPoint X=-38.7583 Y=16.7895 Z=0
    g195: LineSegment StartX=-34.6109 StartY=14.1107 StartZ=0 EndX=-30.8984 EndY=14.1107 EndZ=0
    g196: LineSegment StartX=-30.8984 StartY=14.1107 StartZ=0 EndX=-30.8984 EndY=31.1784 EndZ=0
    g197: LineSegment StartX=-30.8984 StartY=31.1784 StartZ=0 EndX=-34.9984 EndY=31.1784 EndZ=0
    g198: LineSegment StartX=-34.9984 StartY=24.5602 StartZ=0 EndX=-34.9984 EndY=31.1784 EndZ=0
    g199: LineSegment StartX=-34.6109 StartY=16.0476 StartZ=0 EndX=-34.6109 EndY=14.1107 EndZ=0
    g200: LineSegment StartX=-14.8781 StartY=14.1107 StartZ=0 EndX=-10.5106 EndY=14.1107 EndZ=0
    g201: LineSegment StartX=-14.8781 StartY=14.1107 StartZ=0 EndX=-14.8781 EndY=25.8504 EndZ=0
    g202: LineSegment StartX=-14.8781 StartY=25.8504 StartZ=0 EndX=-10.8534 EndY=25.8504 EndZ=0
    g203: LineSegment StartX=-10.8534 StartY=25.8504 StartZ=0 EndX=-10.8534 EndY=24.0923 EndZ=0
    g204: LineSegment StartX=-10.5106 StartY=14.1107 StartZ=0 EndX=-10.5106 EndY=19.7752 EndZ=0
    g205: LineSegment StartX=-5.96397 StartY=25.9304 StartZ=0 EndX=-5.96397 EndY=22.574 EndZ=0
    g206-g214: Circle x9 (B-spline internal-alignment scaffolding for g215; pole/knot coordinates omitted)
    g215: BSplineCurve PolesCount=9 KnotsCount=7 Degree=3 IsPeriodic=0
    g216-g222: GeomPoint x7 (B-spline internal-alignment scaffolding for g215; pole/knot coordinates omitted)
    g223-g232: Circle x10 (B-spline internal-alignment scaffolding for g233; pole/knot coordinates omitted)
    g233: BSplineCurve PolesCount=10 KnotsCount=8 Degree=3 IsPeriodic=0
    g234-g241: GeomPoint x8 (B-spline internal-alignment scaffolding for g233; pole/knot coordinates omitted)
    g242: LineSegment StartX=-1.58923 StartY=21.0696 StartZ=0 EndX=2.62034 EndY=21.0696 EndZ=0
    g243: LineSegment StartX=-1.55856 StartY=18.7342 StartZ=0 EndX=6.45946 EndY=18.7342 EndZ=0
    g244: LineSegment StartX=5.29231 StartY=17.386 StartZ=0 EndX=5.29231 EndY=14.3674 EndZ=0
    g245-g269: Circle x25 (B-spline internal-alignment scaffolding for g270; pole/knot coordinates omitted)
    g270: BSplineCurve PolesCount=25 KnotsCount=23 Degree=3 IsPeriodic=0
    g271-g293: GeomPoint x23 (B-spline internal-alignment scaffolding for g270; pole/knot coordinates omitted)
    g294-g304: Circle x11 (B-spline internal-alignment scaffolding for g305; pole/knot coordinates omitted)
    g305: BSplineCurve PolesCount=11 KnotsCount=9 Degree=3 IsPeriodic=0
    g306-g314: GeomPoint x9 (B-spline internal-alignment scaffolding for g305; pole/knot coordinates omitted)
    g315-g326: Circle x12 (B-spline internal-alignment scaffolding for g327; pole/knot coordinates omitted)
    g327: BSplineCurve PolesCount=12 KnotsCount=10 Degree=3 IsPeriodic=0
    g328-g337: GeomPoint x10 (B-spline internal-alignment scaffolding for g327; pole/knot coordinates omitted)
  constraints (252):
    c: Coincident(g1,g0)
    c: Horizontal(g0)
    c: Vertical(g1)
    c: Coincident(g2,g3)
    c: Coincident(g3,g4)
    c: Horizontal(g4)
    c: Horizontal(g2)
    c: Vertical(g3)
    c: Block(g1)
    c: Distance(g3) = 4.86
    c: Block(g4)
    c: Distance(g0) = 10.8
    c: Distance(g2) = 10.8
    c: Coincident(g5,g0)
    c: Coincident(g6,g4)
    c: Coincident(g6,g2)
    c: Block(g8)
    c: Block(g7)
    c: Coincident(g9,g8)
    c: Coincident(g9,g7)
    c: Vertical(g9)
    c: Coincident(g10,g7)
    c: Coincident(g10,g8)
    c: Vertical(g10)
    c: Weight(g11) = 1
    c: Equal(g11, g12-g21) x10
    c: InternalAlignment(g11-g21 -> g22) x11
    c: InternalAlignment(g23-g31 -> g22) x9
    c: Block(g22)
    c: Weight(g32) = 1
    c: Equal(g32, g33-g49) x17
    c: InternalAlignment(g32-g49 -> g50) x18
    c: InternalAlignment(g51-g66 -> g50) x16
    c: Block(g50)
    c: Coincident(g67,g50)
    c: Coincident(g67,g22)
    c: Coincident(g68,g22)
    c: Coincident(g68,g50)
    c: InternalAlignment(g70,g69)
    c: InternalAlignment(g71,g69)
    c: Block(g69)
    c: InternalAlignment(g73,g72)
    c: InternalAlignment(g74,g72)
    c: Block(g72)
    c: InternalAlignment(g76,g75)
    c: InternalAlignment(g77,g75)
    c: InternalAlignment(g78,g80)
    c: InternalAlignment(g79,g80)
    c: Block(g80)
    c: Coincident(g75,g80)
    c: Block(g75)
    c: InternalAlignment(g82,g81)
    c: InternalAlignment(g83,g81)
    c: InternalAlignment(g84,g86)
    c: InternalAlignment(g85,g86)
    c: Block(g86)
    c: Coincident(g81,g86)
    c: Block(g81)
    c: Horizontal(g87)
    c: Block(g87)
    c: Horizontal(g88)
    c: Distance(g88) = 4.14
    c: Horizontal(g89)
    c: Equal(g88,g89) = 4.14
    c: Block(g89)
    c: Block(g88)
    c: Coincident(g90,g87)
    c: Vertical(g90)
    c: Distance(g90) = 11.88
    c: Coincident(g91,g90)
    c: Horizontal(g91)
    c: Coincident(g92,g91)
    c: Vertical(g92)
    c: Distance(g91) = 4.03
    c: Distance(g92) = 1.9
    c: Coincident(g93,g87)
    c: Vertical(g93)
    c: Vertical(g94)
    c: Coincident(g94,g88)
    c: Distance(g93) = 5.8
    c: Distance(g94) = 5.8
    c: Vertical(g95)
    c: Coincident(g95,g88)
    c: Distance(g95) = 6.9
    c: Coincident(g107,g92)
    c: Weight(g96) = 1
    c: Equal(g96, g97-g106) x10
    c: InternalAlignment(g96-g106 -> g107) x11
    c: InternalAlignment(g108-g116 -> g107) x9
    c: Block(g107)
    c: Block(g117)
    c: Coincident(g126,g93)
    c: Weight(g118) = 1
    c: Equal(g118, g119-g125) x7
    c: Coincident(g126,g95)
    c: InternalAlignment(g118-g125 -> g126) x8
    c: InternalAlignment(g127-g132 -> g126) x6
    c: Coincident(g133,g94)
    c: Block(g126)
    c: Block(g133)
    c: Coincident(g134,g133)
    c: Coincident(g134,g89)
    c: Vertical(g134)
    c: Horizontal(g135)
    c: Block(g135)
    c: Horizontal(g136)
    c: Equal(g88,g136) = 4.14
    c: Horizontal(g137)
    c: Equal(g136,g137) = 4.14
    c: Block(g137)
    c: Block(g136)
    c: Coincident(g138,g135)
    c: Vertical(g138)
    c: Equal(g90,g138) = 11.88
    c: Coincident(g139,g138)
    c: Horizontal(g139)
    c: Coincident(g140,g139)
    c: Vertical(g140)
    c: Equal(g91,g139) = 4.03
    c: Equal(g92,g140) = 1.9
    c: Coincident(g141,g135)
    c: Vertical(g141)
    c: Vertical(g142)
    c: Coincident(g142,g136)
    c: Equal(g93,g141) = 5.8
    c: Equal(g94,g142) = 5.8
    c: Vertical(g143)
    c: Coincident(g143,g136)
    c: Equal(g95,g143) = 6.9
    c: Coincident(g149,g140)
    c: Equal(g96,g144) = 1
    c: Equal(g144, g145-g148) x4
    c: InternalAlignment(g144-g148 -> g149) x5
    c: InternalAlignment(g150-g158 -> g149) x9
    c: Block(g149)
    c: Block(g159)
    c: Coincident(g168,g141)
    c: Equal(g118,g160) = 1
    c: Equal(g160, g161-g167) x7
    c: Coincident(g168,g143)
    c: InternalAlignment(g160-g167 -> g168) x8
    c: InternalAlignment(g169-g174 -> g168) x6
    c: Coincident(g175,g142)
    c: Block(g168)
    c: Block(g175)
    c: Coincident(g176,g175)
    c: Coincident(g176,g137)
    c: Vertical(g176)
    c: Coincident(g177,g137)
    c: Vertical(g177)
    c: Coincident(g178,g177)
    c: Coincident(g178,g159)
    c: InternalAlignment(g179,g178)
    c: InternalAlignment(g180,g178)
    c: Block(g178)
    c: Vertical(g181)
    c: Coincident(g181,g89)
    c: Block(g5)
    c: Coincident(g182,g1)
    c: Coincident(g182,g5)
    c: Horizontal(g182)
    c: Coincident(g186,g117)
    c: Weight(g183) = 1
    c: Equal(g183,g184)
    c: Equal(g183,g185)
    c: Coincident(g186,g181)
    c: InternalAlignment(g183,g186)
    c: InternalAlignment(g184,g186)
    c: InternalAlignment(g185,g186)
    c: InternalAlignment(g187,g186)
    c: InternalAlignment(g188,g186)
    c: Block(g186)
    c: InternalAlignment(g190,g189)
    c: InternalAlignment(g191,g189)
    c: Block(g189)
    c: InternalAlignment(g193,g192)
    c: InternalAlignment(g194,g192)
    c: Block(g192)
    c: Horizontal(g195)
    c: Block(g195)
    c: Coincident(g196,g195)
    c: Vertical(g196)
    c: Block(g196)
    c: Distance(g195) = 3.71244
    c: Coincident(g197,g196)
    c: Horizontal(g197)
    c: Distance(g197) = 4.1
    c: Coincident(g198,g192)
    c: Coincident(g198,g197)
    c: Vertical(g198)
    c: Block(g198)
    c: Coincident(g199,g192)
    c: Coincident(g199,g195)
    c: Vertical(g199)
    c: Block(g199)
    c: Horizontal(g200)
    c: Block(g200)
    c: Coincident(g201,g200)
    c: Vertical(g201)
    c: Block(g201)
    c: Coincident(g202,g201)
    c: Horizontal(g202)
    c: Block(g202)
    c: Coincident(g203,g202)
    c: Vertical(g203)
    c: Block(g203)
    c: Coincident(g204,g200)
    c: Vertical(g204)
    c: Block(g204)
    c: Coincident(g215,g203)
    c: Weight(g206) = 1
    c: Equal(g206, g207-g214) x8
    c: Coincident(g215,g205)
    c: InternalAlignment(g206-g214 -> g215) x9
    c: InternalAlignment(g216-g222 -> g215) x7
    c: Coincident(g233,g204)
    c: Weight(g223) = 1
    c: Equal(g223, g224-g232) x9
    c: Coincident(g233,g205)
    c: InternalAlignment(g223-g232 -> g233) x10
    c: InternalAlignment(g234-g241 -> g233) x8
    c: Vertical(g205)
    c: Block(g205)
    c: Block(g215)
    c: Block(g233)
    c: Horizontal(g242)
    c: Horizontal(g243)
    c: Block(g242)
    c: Block(g243)
    c: Vertical(g244)
    c: Block(g244)
    c: Coincident(g270,g243)
    c: Weight(g245) = 1
    c: Equal(g245, g246-g269) x24
    c: Coincident(g270,g244)
    c: InternalAlignment(g245-g269 -> g270) x25
    c: InternalAlignment(g271-g293 -> g270) x23
    c: Coincident(g305,g242)
    c: Weight(g294) = 1
    c: Equal(g294, g295-g304) x10
    c: Coincident(g305,g242)
    c: InternalAlignment(g294-g304 -> g305) x11
    c: InternalAlignment(g306-g314 -> g305) x9
    c: Block(g305)
    c: Coincident(g327,g243)
    c: Weight(g315) = 1
    c: Equal(g315, g316-g326) x11
    c: Coincident(g327,g244)
    c: InternalAlignment(g315-g326 -> g327) x12
    c: InternalAlignment(g328-g337 -> g327) x10
    c: Block(g327)
    c: Block(g270)
FEATURE [Part::Extrusion] Extrude075  label="CommodoreLogoAndText002"
  Base = -> Sketch084
  Dir = (0,0,1)
  DirMode = 2
  FaceMakerClass = Part::FaceMakerBullseye
  LengthFwd = 10
  LengthRev = 0
  Solid = true
  Symmetric = false
FEATURE [Part::FeaturePython] Clone001  label="CommodoreLogoAndTextScale001"  # Draft clone (typed FeaturePython)
  AttacherType = Attacher::AttachEngine3D
  Fuse = false
  Objects = -> [Extrude075]
  Placement = pos=(112.566,5.37,73.6) rot=(0,0,1;0rad)
  Scale = (0.62,0.62,1)
FEATURE [Part::Cut] Cut073  label="sideA005"
  Base = -> Extrude002
  Tool = -> Part__Mirroring
FEATURE [Part::Cut] Cut074  label="sideB005"
  Base = -> Extrude028
  Tool = -> Clone001
FEATURE [Sketcher::SketchObject] Sketch085
  FullyConstrained = true
  Placement = pos=(0,0,0) rot=(-1,0,0;4.71239rad)
  sketch-geometry (10):
    g0: LineSegment StartX=0 StartY=0 StartZ=0 EndX=-7 EndY=0 EndZ=0
    g1: LineSegment StartX=-7 StartY=10 StartZ=0 EndX=-6.5 EndY=10 EndZ=0
    g2: LineSegment StartX=0 StartY=10 StartZ=0 EndX=-0.5 EndY=10 EndZ=0
    g3: ArcOfCircle CenterX=-3.5 CenterY=10 CenterZ=0 NormalX=0 NormalY=0 NormalZ=1 AngleXU=0 Radius=3 StartAngle=3.14159 EndAngle=6.28319
    g4: LineSegment StartX=-7 StartY=0 StartZ=0 EndX=-10.5 EndY=0 EndZ=0
    g5: LineSegment StartX=0 StartY=0 StartZ=0 EndX=3.5 EndY=0 EndZ=0
    g6: ArcOfCircle CenterX=-10.5 CenterY=3.5 CenterZ=0 NormalX=0 NormalY=0 NormalZ=1 AngleXU=0 Radius=3.5 StartAngle=4.71239 EndAngle=6.28319
    g7: ArcOfCircle CenterX=3.5 CenterY=3.5 CenterZ=0 NormalX=0 NormalY=0 NormalZ=1 AngleXU=0 Radius=3.5 StartAngle=3.14159 EndAngle=4.71239
    g8: LineSegment StartX=-7 StartY=3.5 StartZ=0 EndX=-7 EndY=10 EndZ=0
    g9: LineSegment StartX=0 StartY=10 StartZ=0 EndX=0 EndY=3.5 EndZ=0
  constraints (26):
    c: Coincident(g0,g-1)
    c: Horizontal(g0)
    c: Distance(g0) = 7
    c: Horizontal(g1)
    c: Distance(g1) = 0.5
    c: Horizontal(g2)
    c: Distance(g2) = 0.5
    c: Coincident(g3,g1)
    c: Coincident(g3,g2)
    c: Block(g3)
    c: Coincident(g4,g0)
    c: Horizontal(g4)
    c: Distance(g4) = 3.5
    c: Coincident(g5,g0)
    c: Distance(g5) = 3.5
    c: Horizontal(g5)
    c: Coincident(g6,g4)
    c: Block(g6)
    c: Coincident(g7,g5)
    c: Block(g7)
    c: Coincident(g8,g6)
    c: Coincident(g8,g1)
    c: Vertical(g8)
    c: Coincident(g9,g2)
    c: Coincident(g9,g7)
    c: Vertical(g9)
FEATURE [Part::Extrusion] Extrude076  label="backRightCasePillarSideBracket"
  Base = -> Sketch085
  Dir = (0,-1,3e-16)
  DirMode = 2
  FaceMakerClass = Part::FaceMakerBullseye
  LengthFwd = 6.7
  LengthRev = 0
  Placement = pos=(16,11.5,0) rot=(0,0,1;0rad)
  Solid = true
  Symmetric = false
FEATURE [Sketcher::SketchObject] Sketch086
  FullyConstrained = true
  Placement = pos=(0,0,0) rot=(1,0,0;1.5708rad)
  sketch-geometry (10):
    g0: LineSegment StartX=0 StartY=0 StartZ=0 EndX=-7 EndY=0 EndZ=0
    g1: LineSegment StartX=-7 StartY=10 StartZ=0 EndX=-6.5 EndY=10 EndZ=0
    g2: LineSegment StartX=0 StartY=10 StartZ=0 EndX=-0.5 EndY=10 EndZ=0
    g3: ArcOfCircle CenterX=-3.5 CenterY=10 CenterZ=0 NormalX=0 NormalY=0 NormalZ=1 AngleXU=0 Radius=3 StartAngle=3.14159 EndAngle=6.28319
    g4: LineSegment StartX=-7 StartY=0 StartZ=0 EndX=-10.5 EndY=0 EndZ=0
    g5: LineSegment StartX=0 StartY=0 StartZ=0 EndX=3.5 EndY=0 EndZ=0
    g6: ArcOfCircle CenterX=-10.5 CenterY=3.5 CenterZ=0 NormalX=0 NormalY=0 NormalZ=1 AngleXU=0 Radius=3.5 StartAngle=4.71239 EndAngle=6.28319
    g7: ArcOfCircle CenterX=3.5 CenterY=3.5 CenterZ=0 NormalX=0 NormalY=0 NormalZ=1 AngleXU=0 Radius=3.5 StartAngle=3.14159 EndAngle=4.71239
    g8: LineSegment StartX=-7 StartY=3.5 StartZ=0 EndX=-7 EndY=10 EndZ=0
    g9: LineSegment StartX=0 StartY=10 StartZ=0 EndX=0 EndY=3.5 EndZ=0
  constraints (26):
    c: Coincident(g0,g-1)
    c: Horizontal(g0)
    c: Distance(g0) = 7
    c: Horizontal(g1)
    c: Distance(g1) = 0.5
    c: Horizontal(g2)
    c: Distance(g2) = 0.5
    c: Coincident(g3,g1)
    c: Coincident(g3,g2)
    c: Block(g3)
    c: Coincident(g4,g0)
    c: Horizontal(g4)
    c: Distance(g4) = 3.5
    c: Coincident(g5,g0)
    c: Distance(g5) = 3.5
    c: Horizontal(g5)
    c: Coincident(g6,g4)
    c: Block(g6)
    c: Coincident(g7,g5)
    c: Block(g7)
    c: Coincident(g8,g6)
    c: Coincident(g8,g1)
    c: Vertical(g8)
    c: Coincident(g9,g2)
    c: Coincident(g9,g7)
    c: Vertical(g9)
FEATURE [Part::Extrusion] Extrude077  label="backLeftCasePillarSideBracket001"
  Base = -> Sketch086
  Dir = (0,-1,3e-16)
  DirMode = 2
  FaceMakerClass = Part::FaceMakerBullseye
  LengthFwd = 6.7
  LengthRev = 0
  Placement = pos=(9,11.5,72) rot=(0,1,0;3.14159rad)
  Solid = true
  Symmetric = false
FEATURE [Sketcher::SketchObject] Sketch087
  FullyConstrained = true
  Placement = pos=(0,0,0) rot=(1,0,0;1.5708rad)
  sketch-geometry (8):
    g0: LineSegment StartX=0 StartY=4e-16 StartZ=0 EndX=-7 EndY=4e-16 EndZ=0
    g1: LineSegment StartX=-7 StartY=4e-16 StartZ=0 EndX=-10.5 EndY=4e-16 EndZ=0
    g2: LineSegment StartX=0 StartY=4e-16 StartZ=0 EndX=3.5 EndY=4e-16 EndZ=0
    g3: ArcOfCircle CenterX=-10.5 CenterY=3.5 CenterZ=0 NormalX=0 NormalY=0 NormalZ=1 AngleXU=0 Radius=3.5 StartAngle=4.71239 EndAngle=6.28319
    g4: ArcOfCircle CenterX=3.5 CenterY=3.5 CenterZ=0 NormalX=0 NormalY=0 NormalZ=1 AngleXU=0 Radius=3.5 StartAngle=3.14159 EndAngle=4.71239
    g5: ArcOfCircle CenterX=-3.5 CenterY=3.5 CenterZ=0 NormalX=0 NormalY=0 NormalZ=1 AngleXU=0 Radius=3 StartAngle=3.14159 EndAngle=6.28319
    g6: LineSegment StartX=-7 StartY=3.5 StartZ=0 EndX=-6.5 EndY=3.5 EndZ=0
    g7: LineSegment StartX=-0.5 StartY=3.5 StartZ=0 EndX=0 EndY=3.5 EndZ=0
  constraints (20):
    c: Coincident(g0,g-1)
    c: Horizontal(g0)
    c: Distance(g0) = 7
    c: Coincident(g1,g0)
    c: Horizontal(g1)
    c: Distance(g1) = 3.5
    c: Coincident(g2,g0)
    c: Distance(g2) = 3.5
    c: Horizontal(g2)
    c: Coincident(g3,g1)
    c: Block(g3)
    c: Coincident(g4,g2)
    c: Block(g4)
    c: Horizontal(g6)
    c: Coincident(g5,g6)
    c: Block(g5)
    c: Coincident(g6,g3)
    c: Coincident(g7,g5)
    c: Coincident(g7,g4)
    c: Horizontal(g7)
FEATURE [Part::Extrusion] Extrude078  label="frontBackLeftCasePillarSideBracket001"
  Base = -> Sketch087
  Dir = (0,-1,2e-16)
  DirMode = 2
  FaceMakerClass = Part::FaceMakerBullseye
  LengthFwd = 6.7
  LengthRev = 0
  Placement = pos=(93,11.5,0) rot=(0,0,1;0rad)
  Solid = true
  Symmetric = false
FEATURE [Sketcher::SketchObject] Sketch088
  FullyConstrained = true
  Placement = pos=(0,0,0) rot=(1,0,0;1.5708rad)
  sketch-geometry (8):
    g0: LineSegment StartX=0 StartY=4e-16 StartZ=0 EndX=-7 EndY=4e-16 EndZ=0
    g1: LineSegment StartX=-7 StartY=4e-16 StartZ=0 EndX=-10.5 EndY=4e-16 EndZ=0
    g2: LineSegment StartX=0 StartY=4e-16 StartZ=0 EndX=3.5 EndY=4e-16 EndZ=0
    g3: ArcOfCircle CenterX=-10.5 CenterY=3.5 CenterZ=0 NormalX=0 NormalY=0 NormalZ=1 AngleXU=0 Radius=3.5 StartAngle=4.71239 EndAngle=6.28319
    g4: ArcOfCircle CenterX=3.5 CenterY=3.5 CenterZ=0 NormalX=0 NormalY=0 NormalZ=1 AngleXU=0 Radius=3.5 StartAngle=3.14159 EndAngle=4.71239
    g5: ArcOfCircle CenterX=-3.5 CenterY=3.5 CenterZ=0 NormalX=0 NormalY=0 NormalZ=1 AngleXU=0 Radius=3 StartAngle=3.14159 EndAngle=6.28319
    g6: LineSegment StartX=-7 StartY=3.5 StartZ=0 EndX=-6.5 EndY=3.5 EndZ=0
    g7: LineSegment StartX=-0.5 StartY=3.5 StartZ=0 EndX=0 EndY=3.5 EndZ=0
  constraints (20):
    c: Coincident(g0,g-1)
    c: Horizontal(g0)
    c: Distance(g0) = 7
    c: Coincident(g1,g0)
    c: Horizontal(g1)
    c: Distance(g1) = 3.5
    c: Coincident(g2,g0)
    c: Distance(g2) = 3.5
    c: Horizontal(g2)
    c: Coincident(g3,g1)
    c: Block(g3)
    c: Coincident(g4,g2)
    c: Block(g4)
    c: Horizontal(g6)
    c: Coincident(g5,g6)
    c: Block(g5)
    c: Coincident(g6,g3)
    c: Coincident(g7,g5)
    c: Coincident(g7,g4)
    c: Horizontal(g7)
FEATURE [Part::Extrusion] Extrude079  label="frontFrontRightCasePillarSideBracket002"
  Base = -> Sketch088
  Dir = (0,-1,2e-16)
  DirMode = 2
  FaceMakerClass = Part::FaceMakerBullseye
  LengthFwd = 2
  LengthRev = 0
  Placement = pos=(106,11.5,72) rot=(0,1,0;3.14159rad)
  Solid = true
  Symmetric = false
FEATURE [Part::Chamfer] Chamfer
  Base = -> Extrude076
  Edges = 1 edges r=3: [Edge19]
FEATURE [Part::Chamfer] Chamfer002
  Base = -> Extrude077
  Edges = 1 edges r=3: [Edge7]
FEATURE [Part::Chamfer] Chamfer003  label="backLeftCasePillarSideBracket002"
  Base = -> Chamfer002
  Edges = 1 edges r=3.8: [Edge29]
FEATURE [Part::Chamfer] Chamfer004  label="backRightCasePillarSideBracket001"
  Base = -> Chamfer
  Edges = 1 edges r=3.8: [Edge24]
FEATURE [Sketcher::SketchObject] Sketch089
  FullyConstrained = true
  Placement = pos=(0,0,0) rot=(1,0,0;1.5708rad)
  sketch-geometry (8):
    g0: LineSegment StartX=0 StartY=4e-16 StartZ=0 EndX=-7 EndY=4e-16 EndZ=0
    g1: LineSegment StartX=-7 StartY=4e-16 StartZ=0 EndX=-10.5 EndY=4e-16 EndZ=0
    g2: LineSegment StartX=0 StartY=4e-16 StartZ=0 EndX=3.5 EndY=4e-16 EndZ=0
    g3: ArcOfCircle CenterX=-10.5 CenterY=3.5 CenterZ=0 NormalX=0 NormalY=0 NormalZ=1 AngleXU=0 Radius=3.5 StartAngle=4.71239 EndAngle=6.28319
    g4: ArcOfCircle CenterX=3.5 CenterY=3.5 CenterZ=0 NormalX=0 NormalY=0 NormalZ=1 AngleXU=0 Radius=3.5 StartAngle=3.14159 EndAngle=4.71239
    g5: ArcOfCircle CenterX=-3.5 CenterY=3.5 CenterZ=0 NormalX=0 NormalY=0 NormalZ=1 AngleXU=0 Radius=3 StartAngle=3.14159 EndAngle=6.28319
    g6: LineSegment StartX=-7 StartY=3.5 StartZ=0 EndX=-6.5 EndY=3.5 EndZ=0
    g7: LineSegment StartX=-0.5 StartY=3.5 StartZ=0 EndX=0 EndY=3.5 EndZ=0
  constraints (20):
    c: Coincident(g0,g-1)
    c: Horizontal(g0)
    c: Distance(g0) = 7
    c: Coincident(g1,g0)
    c: Horizontal(g1)
    c: Distance(g1) = 3.5
    c: Coincident(g2,g0)
    c: Distance(g2) = 3.5
    c: Horizontal(g2)
    c: Coincident(g3,g1)
    c: Block(g3)
    c: Coincident(g4,g2)
    c: Block(g4)
    c: Horizontal(g6)
    c: Coincident(g5,g6)
    c: Block(g5)
    c: Coincident(g6,g3)
    c: Coincident(g7,g5)
    c: Coincident(g7,g4)
    c: Horizontal(g7)
FEATURE [Part::Extrusion] Extrude080  label="frontBackLeftCasePillarSideBracket002"
  Base = -> Sketch089
  Dir = (0,-1,2e-16)
  DirMode = 2
  FaceMakerClass = Part::FaceMakerBullseye
  LengthFwd = 6.7
  LengthRev = 0
  Placement = pos=(86,11.5,72) rot=(0,1,0;3.14159rad)
  Solid = true
  Symmetric = false
FEATURE [Part::Box] Box037  label="backLeftCasePillarAngledSideBracket"
  AttacherType = Attacher::AttachEngine3D
  Height = 14
  Length = 3.4
  Placement = pos=(0,10.8,0) rot=(0,1,0;0.785398rad)
  Width = 4
FEATURE [Part::Box] Box038  label="backRightCasePillarAngledSideBracket"
  AttacherType = Attacher::AttachEngine3D
  Height = 14
  Length = 3.4
  Placement = pos=(9.9,10.8,62.1) rot=(0,1,0;-0.785398rad)
  Width = 4
FEATURE [Sketcher::SketchObject] Sketch090  label="topSketch026"
  FullyConstrained = true
  sketch-geometry (8):
    g0: ArcOfCircle CenterX=19 CenterY=19.1201 CenterZ=0 NormalX=0 NormalY=0 NormalZ=1 AngleXU=0 Radius=18.8799 StartAngle=1.5708 EndAngle=3.14793
    g1: LineSegment StartX=0.120501 StartY=19.0004 StartZ=0 EndX=0.120501 EndY=0.000382114 EndZ=0
    g2: LineSegment StartX=19 StartY=38 StartZ=0 EndX=124 EndY=38 EndZ=0
    g3: LineSegment StartX=0.120501 StartY=0.000382114 StartZ=0 EndX=105.121 EndY=0.000382114 EndZ=0
    g4: LineSegment StartX=124 StartY=38 StartZ=0 EndX=125.616 EndY=38 EndZ=0
    g5: LineSegment StartX=105.121 StartY=0.000382114 StartZ=0 EndX=106.736 EndY=0.000382114 EndZ=0
    g6: ArcOfCircle CenterX=106.616 CenterY=19 CenterZ=0 NormalX=0 NormalY=0 NormalZ=1 AngleXU=0 Radius=19 StartAngle=4.71873 EndAngle=6.28319
    g7: LineSegment StartX=125.616 StartY=38 StartZ=0 EndX=125.616 EndY=19 EndZ=0
  constraints (21):
    c: Block(g0)
    c: Coincident(g1,g0)
    c: Vertical(g1)
    c: Horizontal(g2)
    c: Distance(g2) = 105
    c: Coincident(g2,g0)
    c: Distance(g1) = 19
    c: Coincident(g3,g1)
    c: Horizontal(g3)
    c: Distance(g3) = 105
    c: Coincident(g4,g2)
    c: Horizontal(g4)
    c: Distance(g4) = 1.61553
    c: Horizontal(g5)
    c: Equal(g4,g5) = 1.61553
    c: Coincident(g5,g3)
    c: Block(g6)
    c: Coincident(g6,g5)
    c: Coincident(g7,g4)
    c: Coincident(g7,g6)
    c: Vertical(g7)
FEATURE [Part::Extrusion] Extrude081  label="sideB006"
  Base = -> Sketch090
  Dir = (0,0,1)
  DirMode = 2
  FaceMakerClass = Part::FaceMakerBullseye
  LengthFwd = 3
  LengthRev = 0
  Placement = pos=(-0.1205,0,72) rot=(0,0,1;0rad)
  Solid = true
  Symmetric = false
FEATURE [Sketcher::SketchObject] Sketch091  label="topSketch027"
  FullyConstrained = true
  sketch-geometry (8):
    g0: ArcOfCircle CenterX=19 CenterY=19.1201 CenterZ=0 NormalX=0 NormalY=0 NormalZ=1 AngleXU=0 Radius=18.8799 StartAngle=1.5708 EndAngle=3.14793
    g1: LineSegment StartX=0.120501 StartY=19.0004 StartZ=0 EndX=0.120501 EndY=0.000382114 EndZ=0
    g2: LineSegment StartX=19 StartY=38 StartZ=0 EndX=124 EndY=38 EndZ=0
    g3: LineSegment StartX=0.120501 StartY=0.000382114 StartZ=0 EndX=105.121 EndY=0.000382114 EndZ=0
    g4: LineSegment StartX=124 StartY=38 StartZ=0 EndX=125.616 EndY=38 EndZ=0
    g5: LineSegment StartX=105.121 StartY=0.000382114 StartZ=0 EndX=106.736 EndY=0.000382114 EndZ=0
    g6: ArcOfCircle CenterX=106.616 CenterY=19 CenterZ=0 NormalX=0 NormalY=0 NormalZ=1 AngleXU=0 Radius=19 StartAngle=4.71873 EndAngle=6.28319
    g7: LineSegment StartX=125.616 StartY=38 StartZ=0 EndX=125.616 EndY=19 EndZ=0
  constraints (21):
    c: Block(g0)
    c: Coincident(g1,g0)
    c: Vertical(g1)
    c: Horizontal(g2)
    c: Distance(g2) = 105
    c: Coincident(g2,g0)
    c: Distance(g1) = 19
    c: Coincident(g3,g1)
    c: Horizontal(g3)
    c: Distance(g3) = 105
    c: Coincident(g4,g2)
    c: Horizontal(g4)
    c: Distance(g4) = 1.61553
    c: Horizontal(g5)
    c: Equal(g4,g5) = 1.61553
    c: Coincident(g5,g3)
    c: Block(g6)
    c: Coincident(g6,g5)
    c: Coincident(g7,g4)
    c: Coincident(g7,g6)
    c: Vertical(g7)
FEATURE [Part::Extrusion] Extrude082  label="sideB007"
  Base = -> Sketch091
  Dir = (0,0,1)
  DirMode = 2
  FaceMakerClass = Part::FaceMakerBullseye
  LengthFwd = 3
  LengthRev = 0
  Placement = pos=(0,0,72) rot=(0,0,1;0rad)
  Solid = true
  Symmetric = false
FEATURE [Part::Cut] Cut075
  Base = -> Extrude081
  Placement = pos=(0.05,0,0) rot=(0,0,1;0rad)
  Tool = -> Extrude082
FEATURE [Sketcher::SketchObject] Sketch092  label="topSketch028"
  FullyConstrained = true
  sketch-geometry (8):
    g0: ArcOfCircle CenterX=19 CenterY=19.1201 CenterZ=0 NormalX=0 NormalY=0 NormalZ=1 AngleXU=0 Radius=18.8799 StartAngle=1.5708 EndAngle=3.14793
    g1: LineSegment StartX=0.120501 StartY=19.0004 StartZ=0 EndX=0.120501 EndY=0.000382114 EndZ=0
    g2: LineSegment StartX=19 StartY=38 StartZ=0 EndX=124 EndY=38 EndZ=0
    g3: LineSegment StartX=0.120501 StartY=0.000382114 StartZ=0 EndX=105.121 EndY=0.000382114 EndZ=0
    g4: LineSegment StartX=124 StartY=38 StartZ=0 EndX=125.616 EndY=38 EndZ=0
    g5: LineSegment StartX=105.121 StartY=0.000382114 StartZ=0 EndX=106.736 EndY=0.000382114 EndZ=0
    g6: ArcOfCircle CenterX=106.616 CenterY=19 CenterZ=0 NormalX=0 NormalY=0 NormalZ=1 AngleXU=0 Radius=19 StartAngle=4.71873 EndAngle=6.28319
    g7: LineSegment StartX=125.616 StartY=38 StartZ=0 EndX=125.616 EndY=19 EndZ=0
  constraints (21):
    c: Block(g0)
    c: Coincident(g1,g0)
    c: Vertical(g1)
    c: Horizontal(g2)
    c: Distance(g2) = 105
    c: Coincident(g2,g0)
    c: Distance(g1) = 19
    c: Coincident(g3,g1)
    c: Horizontal(g3)
    c: Distance(g3) = 105
    c: Coincident(g4,g2)
    c: Horizontal(g4)
    c: Distance(g4) = 1.61553
    c: Horizontal(g5)
    c: Equal(g4,g5) = 1.61553
    c: Coincident(g5,g3)
    c: Block(g6)
    c: Coincident(g6,g5)
    c: Coincident(g7,g4)
    c: Coincident(g7,g6)
    c: Vertical(g7)
FEATURE [Part::Extrusion] Extrude083  label="sideB008"
  Base = -> Sketch092
  Dir = (0,0,1)
  DirMode = 2
  FaceMakerClass = Part::FaceMakerBullseye
  LengthFwd = 3
  LengthRev = 0
  Placement = pos=(-0.1205,0,72) rot=(0,0,1;0rad)
  Solid = true
  Symmetric = false
FEATURE [Sketcher::SketchObject] Sketch093  label="topSketch029"
  FullyConstrained = true
  sketch-geometry (8):
    g0: ArcOfCircle CenterX=19 CenterY=19.1201 CenterZ=0 NormalX=0 NormalY=0 NormalZ=1 AngleXU=0 Radius=18.8799 StartAngle=1.5708 EndAngle=3.14793
    g1: LineSegment StartX=0.120501 StartY=19.0004 StartZ=0 EndX=0.120501 EndY=0.000382114 EndZ=0
    g2: LineSegment StartX=19 StartY=38 StartZ=0 EndX=124 EndY=38 EndZ=0
    g3: LineSegment StartX=0.120501 StartY=0.000382114 StartZ=0 EndX=105.121 EndY=0.000382114 EndZ=0
    g4: LineSegment StartX=124 StartY=38 StartZ=0 EndX=125.616 EndY=38 EndZ=0
    g5: LineSegment StartX=105.121 StartY=0.000382114 StartZ=0 EndX=106.736 EndY=0.000382114 EndZ=0
    g6: ArcOfCircle CenterX=106.616 CenterY=19 CenterZ=0 NormalX=0 NormalY=0 NormalZ=1 AngleXU=0 Radius=19 StartAngle=4.71873 EndAngle=6.28319
    g7: LineSegment StartX=125.616 StartY=38 StartZ=0 EndX=125.616 EndY=19 EndZ=0
  constraints (21):
    c: Block(g0)
    c: Coincident(g1,g0)
    c: Vertical(g1)
    c: Horizontal(g2)
    c: Distance(g2) = 105
    c: Coincident(g2,g0)
    c: Distance(g1) = 19
    c: Coincident(g3,g1)
    c: Horizontal(g3)
    c: Distance(g3) = 105
    c: Coincident(g4,g2)
    c: Horizontal(g4)
    c: Distance(g4) = 1.61553
    c: Horizontal(g5)
    c: Equal(g4,g5) = 1.61553
    c: Coincident(g5,g3)
    c: Block(g6)
    c: Coincident(g6,g5)
    c: Coincident(g7,g4)
    c: Coincident(g7,g6)
    c: Vertical(g7)
FEATURE [Part::Extrusion] Extrude084  label="sideB009"
  Base = -> Sketch093
  Dir = (0,0,1)
  DirMode = 2
  FaceMakerClass = Part::FaceMakerBullseye
  LengthFwd = 3
  LengthRev = 0
  Placement = pos=(0,0,72) rot=(0,0,1;0rad)
  Solid = true
  Symmetric = false
FEATURE [Part::Cut] Cut076
  Base = -> Extrude083
  Placement = pos=(0.05,0,-75) rot=(0,0,1;0rad)
  Tool = -> Extrude084
FEATURE [Part::MultiFuse] Fusion155  label="sideA006"
  Shapes = -> [Cut076,Cut073]
FEATURE [Part::MultiFuse] Fusion156  label="sideB010"
  Shapes = -> [Cut075,Cut074]
